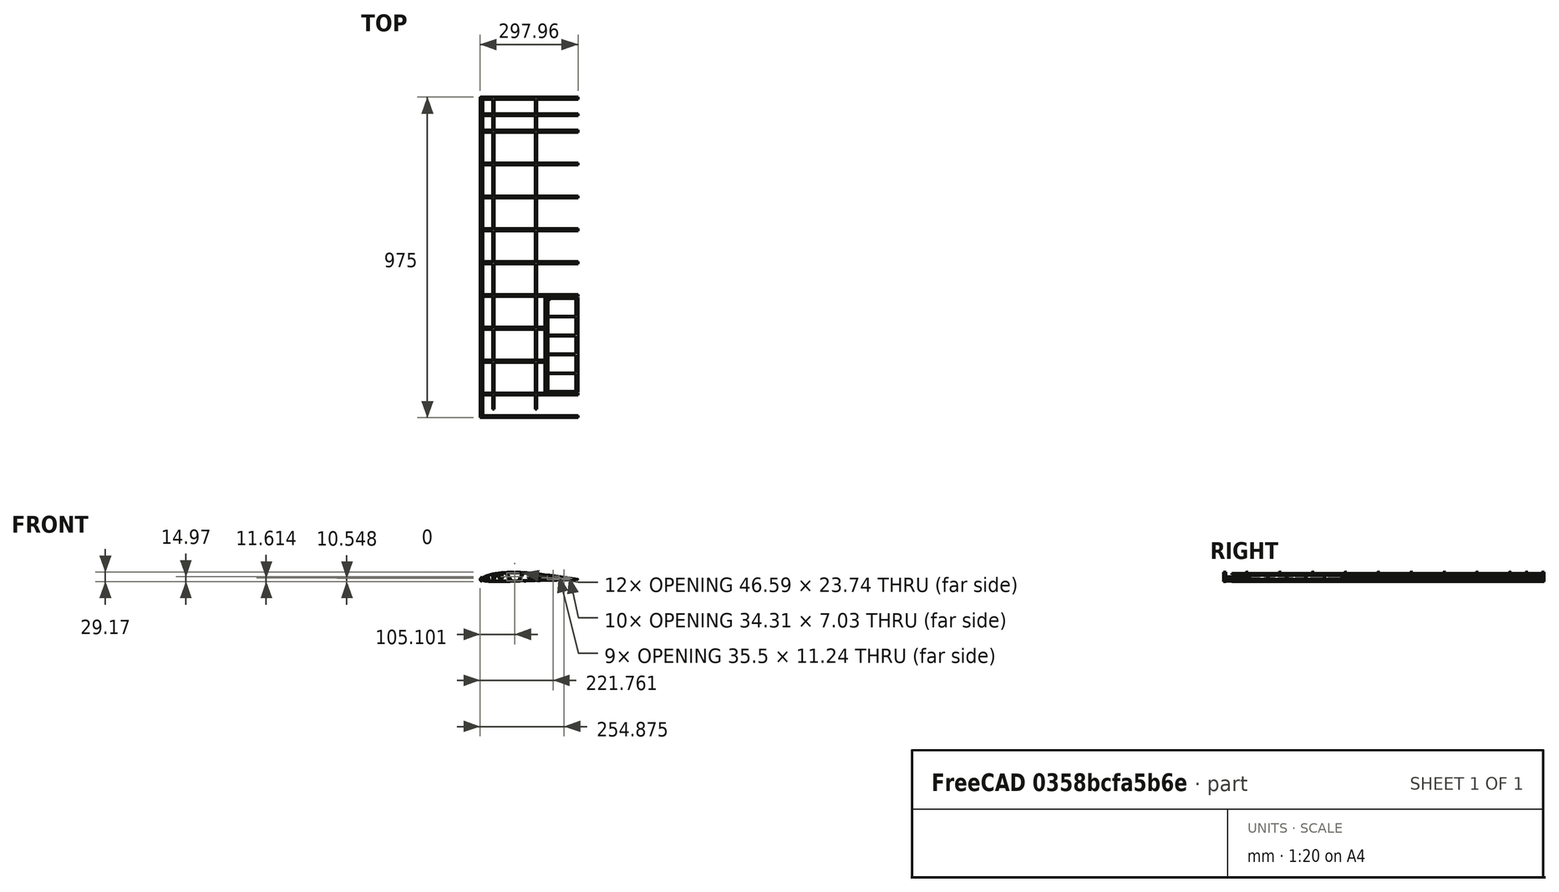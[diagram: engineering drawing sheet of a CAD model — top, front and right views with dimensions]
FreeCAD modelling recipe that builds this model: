
FCSTD DOCUMENT  (FreeCAD 1.0R39319 (Git))
Label: fpv_plane_wing_smarter
License: All rights reserved
LicenseURL: https://en.wikipedia.org/wiki/All_rights_reserved
objects: Sketcher::SketchObject×141, PartDesign::Pocket×77, PartDesign::Pad×64, PartDesign::Body×27, PartDesign::Thickness×11, PartDesign::Chamfer×5, Part::Part2DObjectPython×3, PartDesign::Plane×2, App::DocumentObjectGroup×1, PartDesign::Revolution×1
note: 788 computed .brp shape members not serialized (recipe doc carries the construction recipe); baked Part::Feature solids carry a one-line shape summary decoded from their .brp

FEATURE [Part::Part2DObjectPython] Wire  # Draft 2D object (typed FeaturePython)
  Area = 0.0621999
  ChamferSize = 0
  Closed = true
  End = (1.00001,0,0)
  FilletRadius = 0
  Length = 2.02855
  MakeFace = true
  Placement = pos=(0,0,0) rot=(1,0,0;1.5708rad)
  Points = (61) [(1,0,0),(0.99663,0.00039,0),(0.98679,0.00172,0),(0.97104,0.00419,0),(0.94996,0.00769,0),(0.92398,0.01193,0),(0.89336,0.0167,0),(0.8584,0.02198,0),+53 more]
  Start = (1,0,0)
  Subdivisions = 0
FEATURE [Part::Part2DObjectPython] Wire002  label="wing_wire_300mm"  # Draft 2D object (typed FeaturePython)
  Area = 5597.99
  ChamferSize = 0
  Closed = true
  End = (300.003,0,0)
  FilletRadius = 0
  Length = 608.564
  MakeFace = true
  Placement = pos=(0,0,0) rot=(1,0,0;1.5708rad)
  Points = (61) [(300,0,0),(298.989,0.117,0),(296.037,0.516,0),(291.312,1.257,0),(284.988,2.307,0),(277.194,3.579,0),(268.008,5.01,0),(257.52,6.594,0),+53 more]
  Start = (300,0,0)
  Subdivisions = 0
FEATURE [App::DocumentObjectGroup] s3021
  Group = -> [Wire,Wire002]
FEATURE [Part::Part2DObjectPython] BSpline001  label="wing_wire_300mm001"  # Draft 2D object (typed FeaturePython)
  Area = 5612.28
  Closed = true
  MakeFace = true
  Parameterization = 1
  Placement = pos=(0,0,0) rot=(1,0,0;1.5708rad)
  Points = (61) [(300,0,0),(298.989,0.117,0),(296.037,0.516,0),(291.312,1.257,0),(284.988,2.307,0),(277.194,3.579,0),(268.008,5.01,0),(257.52,6.594,0),+53 more]
FEATURE [Sketcher::SketchObject] Sketch003
  ArcFitTolerance = 1e-06
  FullyConstrained = false
  MakeInternals = false
  Placement = pos=(0,0,0) rot=(1,0,0;1.5708rad)
  sketch-geometry (125):
    g0: BSplineCurve PolesCount=62 KnotsCount=62 Degree=3 IsPeriodic=1
    g1-g62: Circle [constr] x62 (B-spline internal-alignment scaffolding for g0; pole/knot coordinates omitted)
    g63-g124: GeomPoint [constr] x62 (B-spline internal-alignment scaffolding for g0; pole/knot coordinates omitted)
  constraints (125):
    c: InternalAlignment(g1,g0)
    c: Weight(g1) = 1
    c: InternalAlignment(g2,g0)
    c: Equal(g2,g1)
    c: InternalAlignment(g3,g0)
    c: Equal(g3,g1)
    c: InternalAlignment(g4,g0)
    c: Equal(g4,g1)
    c: InternalAlignment(g5,g0)
    c: Equal(g5,g1)
    c: InternalAlignment(g6,g0)
    c: Equal(g6,g1)
    c: InternalAlignment(g7,g0)
    c: Equal(g7,g1)
    c: InternalAlignment(g8,g0)
    c: Equal(g8,g1)
    c: InternalAlignment(g9,g0)
    c: Equal(g9,g1)
    c: InternalAlignment(g10,g0)
    c: Equal(g10,g1)
    c: InternalAlignment(g11,g0)
    c: Equal(g11,g1)
    c: InternalAlignment(g12,g0)
    c: Equal(g12,g1)
    c: InternalAlignment(g13,g0)
    c: Equal(g13,g1)
    c: InternalAlignment(g14,g0)
    c: Equal(g14,g1)
    c: InternalAlignment(g15,g0)
    c: Equal(g15,g1)
    c: InternalAlignment(g16,g0)
    c: Equal(g16,g1)
    c: InternalAlignment(g17,g0)
    c: Equal(g17,g1)
    c: InternalAlignment(g18,g0)
    c: Equal(g18,g1)
    c: InternalAlignment(g19,g0)
    c: Equal(g19,g1)
    c: InternalAlignment(g20,g0)
    c: Equal(g20,g1)
    c: InternalAlignment(g21,g0)
    c: Equal(g21,g1)
    c: InternalAlignment(g22,g0)
    c: Equal(g22,g1)
    c: InternalAlignment(g23,g0)
    c: Equal(g23,g1)
    c: InternalAlignment(g24,g0)
    c: Equal(g24,g1)
    c: InternalAlignment(g25,g0)
    c: Equal(g25,g1)
    c: InternalAlignment(g26,g0)
    c: Equal(g26,g1)
    c: InternalAlignment(g27,g0)
    c: Equal(g27,g1)
    c: InternalAlignment(g28,g0)
    c: Equal(g28,g1)
    c: InternalAlignment(g29,g0)
    c: Equal(g29,g1)
    c: InternalAlignment(g30,g0)
    c: Equal(g30,g1)
    c: InternalAlignment(g31,g0)
    c: Equal(g31,g1)
    c: InternalAlignment(g32,g0)
    c: Equal(g32,g1)
    c: InternalAlignment(g33,g0)
    c: Equal(g33,g1)
    c: InternalAlignment(g34,g0)
    c: Equal(g34,g1)
    c: InternalAlignment(g35,g0)
    c: Equal(g35,g1)
    c: InternalAlignment(g36,g0)
    c: Equal(g36,g1)
    c: InternalAlignment(g37,g0)
    c: Equal(g37,g1)
    c: InternalAlignment(g38,g0)
    c: Equal(g38,g1)
    c: InternalAlignment(g39,g0)
    c: Equal(g39,g1)
    c: InternalAlignment(g40,g0)
    c: Equal(g40,g1)
    c: InternalAlignment(g41,g0)
    c: Equal(g41,g1)
    c: InternalAlignment(g42,g0)
    c: Equal(g42,g1)
    c: InternalAlignment(g43,g0)
    c: Equal(g43,g1)
    c: InternalAlignment(g44,g0)
    c: Equal(g44,g1)
    c: InternalAlignment(g45,g0)
    c: Equal(g45,g1)
    c: InternalAlignment(g46,g0)
    c: Equal(g46,g1)
    c: InternalAlignment(g47,g0)
    c: Equal(g47,g1)
    c: InternalAlignment(g48,g0)
    c: Equal(g48,g1)
    c: InternalAlignment(g49,g0)
    c: Equal(g49,g1)
    c: InternalAlignment(g50,g0)
    c: Equal(g50,g1)
    c: InternalAlignment(g51,g0)
    c: Equal(g51,g1)
    c: InternalAlignment(g52,g0)
    c: Equal(g52,g1)
    c: InternalAlignment(g53,g0)
    c: Equal(g53,g1)
    c: InternalAlignment(g54,g0)
    c: Equal(g54,g1)
    c: InternalAlignment(g55,g0)
    c: Equal(g55,g1)
    c: InternalAlignment(g56,g0)
    c: Equal(g56,g1)
    c: InternalAlignment(g57,g0)
    c: Equal(g57,g1)
    c: InternalAlignment(g58,g0)
    c: Equal(g58,g1)
    c: InternalAlignment(g59,g0)
    c: Equal(g59,g1)
    c: InternalAlignment(g60,g0)
    c: Equal(g60,g1)
    c: InternalAlignment(g61,g0)
    c: Equal(g61,g1)
    c: InternalAlignment(g62,g0)
    c: Equal(g62,g1)
    c: InternalAlignment(g63-g124 -> g0) x62
FEATURE [PartDesign::Pad] Pad
  Direction = (0,-1,2e-16)
  Length = 49.95
  Length2 = 10
  Placement = pos=(0,0,0) rot=(1,0,0;1.5708rad)
  Profile = -> Sketch003
  ReferenceAxis = -> Sketch003 [N_Axis]
  Refine = true
  Suppressed = false
  Type = 0
FEATURE [Sketcher::SketchObject] Sketch004
  ArcFitTolerance = 1e-06
  AttachmentSupport = -> [XY_Plane001]
  FullyConstrained = false
  MakeInternals = false
  MapMode = 5
  sketch-geometry (4):
    g0: LineSegment StartX=295 StartY=36.1981 StartZ=0 EndX=295 EndY=-1016.06 EndZ=0
    g1: LineSegment StartX=295 StartY=-1016.06 StartZ=0 EndX=488.335 EndY=-1016.06 EndZ=0
    g2: LineSegment StartX=488.335 StartY=-1016.06 StartZ=0 EndX=488.335 EndY=36.1981 EndZ=0
    g3: LineSegment StartX=488.335 StartY=36.1981 StartZ=0 EndX=295 EndY=36.1981 EndZ=0
  constraints (9):
    c: Coincident(g0,g1)
    c: Coincident(g1,g2)
    c: Coincident(g2,g3)
    c: Coincident(g3,g0)
    c: Vertical(g0)
    c: Vertical(g2)
    c: Horizontal(g1)
    c: Horizontal(g3)
    c: DistanceX(g-1,g0) = 295
FEATURE [Sketcher::SketchObject] Sketch006
  ArcFitTolerance = 1e-06
  AttachmentSupport = -> [Pad]
  FullyConstrained = false
  MakeInternals = false
  MapMode = 5
  Placement = pos=(0,-49.95,1.1e-14) rot=(1,0,0;1.5708rad)
  sketch-geometry (29):
    g0: LineSegment StartX=2.71326 StartY=0.775372 StartZ=0 EndX=3.3867 EndY=1.52303 EndZ=0
    g1: LineSegment StartX=3.3867 StartY=1.52303 StartZ=0 EndX=5.99321 EndY=4.17962 EndZ=0
    g2: LineSegment StartX=5.99321 StartY=4.17962 StartZ=0 EndX=11.2308 EndY=7.18071 EndZ=0
    g3: LineSegment StartX=11.2308 StartY=7.18071 StartZ=0 EndX=18.9287 EndY=10.4927 EndZ=0
    g4: LineSegment StartX=18.9287 StartY=10.4927 StartZ=0 EndX=30.0156 EndY=13.8045 EndZ=0
    g5: LineSegment StartX=30.0156 StartY=13.8045 StartZ=0 EndX=43.7053 EndY=16.6585 EndZ=0
    g6: LineSegment StartX=43.7053 StartY=16.6585 StartZ=0 EndX=58.3753 EndY=18.5837 EndZ=0
    g7: LineSegment StartX=58.3753 StartY=18.5837 StartZ=0 EndX=81.9328 EndY=20.1998 EndZ=0
    g8: LineSegment StartX=81.9328 StartY=20.1998 StartZ=0 EndX=99.116 EndY=20.5815 EndZ=0
    g9: LineSegment StartX=99.116 StartY=20.5815 StartZ=0 EndX=120.506 EndY=20.1998 EndZ=0
    g10: LineSegment StartX=120.506 StartY=20.1998 StartZ=0 EndX=145.772 EndY=18.6559 EndZ=0
    g11: LineSegment StartX=145.772 StartY=18.6559 StartZ=0 EndX=175.748 EndY=15.7728 EndZ=0
    g12: LineSegment StartX=175.748 StartY=15.7728 StartZ=0 EndX=200.436 EndY=12.5699 EndZ=0
    g13: LineSegment StartX=200.436 StartY=12.5699 StartZ=0 EndX=229.384 EndY=8.60252 EndZ=0
    g14: LineSegment StartX=229.384 StartY=8.60252 StartZ=0 EndX=252.135 EndY=5.21302 EndZ=0
    g15: LineSegment StartX=252.135 StartY=5.21302 StartZ=0 EndX=269.07 EndY=2.67143 EndZ=0
    g16: LineSegment StartX=269.07 StartY=2.67143 StartZ=0 EndX=269.07 EndY=1.39956 EndZ=0
    g17: LineSegment StartX=269.07 StartY=1.39956 StartZ=0 EndX=224.761 EndY=0.436598 EndZ=0
    g18: LineSegment StartX=224.761 StartY=0.436598 StartZ=0 EndX=175.487 EndY=-1.02731 EndZ=0
    g19: LineSegment StartX=175.487 StartY=-1.02731 StartZ=0 EndX=123.478 EndY=-2.41293 EndZ=0
    g20: LineSegment StartX=123.478 StartY=-2.41293 StartZ=0 EndX=62.0775 EndY=-3.87655 EndZ=0
    g21: LineSegment StartX=62.0775 StartY=-3.87655 StartZ=0 EndX=32.0529 EndY=-3.76091 EndZ=0
    g22: LineSegment StartX=32.0529 StartY=-3.76091 StartZ=0 EndX=18.888 EndY=-3.18288 EndZ=0
    g23: LineSegment StartX=18.888 StartY=-3.18288 StartZ=0 EndX=12.7286 EndY=-2.48971 EndZ=0
    g24: LineSegment StartX=12.7286 StartY=-2.48971 StartZ=0 EndX=8.49342 EndY=-1.8722 EndZ=0
    g25: LineSegment StartX=8.49342 StartY=-1.8722 StartZ=0 EndX=4.56236 EndY=-0.768246 EndZ=0
    g26: LineSegment StartX=4.56236 StartY=-0.768246 StartZ=0 EndX=3.01395 EndY=-0.301296 EndZ=0
    g27: ArcOfCircle CenterX=3.20505 CenterY=0.332397 CenterZ=0 NormalX=0 NormalY=0 NormalZ=1 AngleXU=0 Radius=0.661881 StartAngle=2.40837 EndAngle=4.41949
    g28: GeomPoint [constr] X=2.01486 Y=0 Z=0
  constraints (32):
    c: PointOnObject(g28,g-1)
    c: Coincident(g0,g1)
    c: Coincident(g1,g2)
    c: Coincident(g2,g3)
    c: Coincident(g3,g4)
    c: Coincident(g4,g5)
    c: Coincident(g5,g6)
    c: Coincident(g6,g7)
    c: Coincident(g7,g8)
    c: Coincident(g8,g9)
    c: Coincident(g9,g10)
    c: Coincident(g10,g11)
    c: Coincident(g11,g12)
    c: Coincident(g12,g13)
    c: Coincident(g13,g14)
    c: Coincident(g14,g15)
    c: Coincident(g15,g16)
    c: Vertical(g16)
    c: Coincident(g16,g17)
    c: Coincident(g17,g18)
    c: Coincident(g18,g19)
    c: Coincident(g19,g20)
    c: Coincident(g20,g21)
    c: Coincident(g21,g22)
    c: Coincident(g22,g23)
    c: Coincident(g23,g24)
    c: Coincident(g24,g25)
    c: Coincident(g25,g26)
    c: PointOnObject(g28,g0)
    c: PointOnObject(g28,g26)
    c: Tangent(g0,g27) = 1.5708
    c: Tangent(g26,g27) = 1.5708
FEATURE [PartDesign::Pocket] Pocket002
  BaseFeature = -> Pad
  Direction = (0,1,-2e-16)
  Length = 49.95
  Length2 = 5
  Placement = pos=(0,0,0) rot=(1,0,0;1.5708rad)
  Profile = -> Sketch006
  ReferenceAxis = -> Sketch006 [N_Axis]
  Refine = true
  Suppressed = false
  Type = 0
FEATURE [Sketcher::SketchObject] Sketch007
  ArcFitTolerance = 1e-06
  AttachmentSupport = -> [XY_Plane]
  FullyConstrained = false
  MakeInternals = false
  MapMode = 5
  sketch-geometry (4):
    g0: LineSegment StartX=295 StartY=17.3691 StartZ=0 EndX=295 EndY=-79.0747 EndZ=0
    g1: LineSegment StartX=295 StartY=-79.0747 StartZ=0 EndX=384.545 EndY=-79.0747 EndZ=0
    g2: LineSegment StartX=384.545 StartY=-79.0747 StartZ=0 EndX=384.545 EndY=17.3691 EndZ=0
    g3: LineSegment StartX=384.545 StartY=17.3691 StartZ=0 EndX=295 EndY=17.3691 EndZ=0
  constraints (9):
    c: Coincident(g0,g1)
    c: Coincident(g1,g2)
    c: Coincident(g2,g3)
    c: Coincident(g3,g0)
    c: Vertical(g0)
    c: Vertical(g2)
    c: Horizontal(g1)
    c: Horizontal(g3)
    c: DistanceX(g-1,g0) = 295
FEATURE [PartDesign::Pocket] Pocket003
  BaseFeature = -> Pocket002
  Direction = (0,0,-1)
  Length = 5
  Length2 = 5
  Midplane = true
  Placement = pos=(0,0,0) rot=(1,0,0;1.5708rad)
  Profile = -> Sketch007
  ReferenceAxis = -> Sketch007 [N_Axis]
  Refine = true
  Suppressed = false
  Type = 0
FEATURE [Sketcher::SketchObject] Sketch017
  ArcFitTolerance = 1e-06
  FullyConstrained = false
  MakeInternals = false
  Placement = pos=(0,0,0) rot=(1,0,0;1.5708rad)
  sketch-geometry (125):
    g0: BSplineCurve PolesCount=62 KnotsCount=62 Degree=3 IsPeriodic=1
    g1-g62: Circle [constr] x62 (B-spline internal-alignment scaffolding for g0; pole/knot coordinates omitted)
    g63-g124: GeomPoint [constr] x62 (B-spline internal-alignment scaffolding for g0; pole/knot coordinates omitted)
  constraints (125):
    c: InternalAlignment(g1,g0)
    c: Weight(g1) = 1
    c: InternalAlignment(g2,g0)
    c: Equal(g2,g1)
    c: InternalAlignment(g3,g0)
    c: Equal(g3,g1)
    c: InternalAlignment(g4,g0)
    c: Equal(g4,g1)
    c: InternalAlignment(g5,g0)
    c: Equal(g5,g1)
    c: InternalAlignment(g6,g0)
    c: Equal(g6,g1)
    c: InternalAlignment(g7,g0)
    c: Equal(g7,g1)
    c: InternalAlignment(g8,g0)
    c: Equal(g8,g1)
    c: InternalAlignment(g9,g0)
    c: Equal(g9,g1)
    c: InternalAlignment(g10,g0)
    c: Equal(g10,g1)
    c: InternalAlignment(g11,g0)
    c: Equal(g11,g1)
    c: InternalAlignment(g12,g0)
    c: Equal(g12,g1)
    c: InternalAlignment(g13,g0)
    c: Equal(g13,g1)
    c: InternalAlignment(g14,g0)
    c: Equal(g14,g1)
    c: InternalAlignment(g15,g0)
    c: Equal(g15,g1)
    c: InternalAlignment(g16,g0)
    c: Equal(g16,g1)
    c: InternalAlignment(g17,g0)
    c: Equal(g17,g1)
    c: InternalAlignment(g18,g0)
    c: Equal(g18,g1)
    c: InternalAlignment(g19,g0)
    c: Equal(g19,g1)
    c: InternalAlignment(g20,g0)
    c: Equal(g20,g1)
    c: InternalAlignment(g21,g0)
    c: Equal(g21,g1)
    c: InternalAlignment(g22,g0)
    c: Equal(g22,g1)
    c: InternalAlignment(g23,g0)
    c: Equal(g23,g1)
    c: InternalAlignment(g24,g0)
    c: Equal(g24,g1)
    c: InternalAlignment(g25,g0)
    c: Equal(g25,g1)
    c: InternalAlignment(g26,g0)
    c: Equal(g26,g1)
    c: InternalAlignment(g27,g0)
    c: Equal(g27,g1)
    c: InternalAlignment(g28,g0)
    c: Equal(g28,g1)
    c: InternalAlignment(g29,g0)
    c: Equal(g29,g1)
    c: InternalAlignment(g30,g0)
    c: Equal(g30,g1)
    c: InternalAlignment(g31,g0)
    c: Equal(g31,g1)
    c: InternalAlignment(g32,g0)
    c: Equal(g32,g1)
    c: InternalAlignment(g33,g0)
    c: Equal(g33,g1)
    c: InternalAlignment(g34,g0)
    c: Equal(g34,g1)
    c: InternalAlignment(g35,g0)
    c: Equal(g35,g1)
    c: InternalAlignment(g36,g0)
    c: Equal(g36,g1)
    c: InternalAlignment(g37,g0)
    c: Equal(g37,g1)
    c: InternalAlignment(g38,g0)
    c: Equal(g38,g1)
    c: InternalAlignment(g39,g0)
    c: Equal(g39,g1)
    c: InternalAlignment(g40,g0)
    c: Equal(g40,g1)
    c: InternalAlignment(g41,g0)
    c: Equal(g41,g1)
    c: InternalAlignment(g42,g0)
    c: Equal(g42,g1)
    c: InternalAlignment(g43,g0)
    c: Equal(g43,g1)
    c: InternalAlignment(g44,g0)
    c: Equal(g44,g1)
    c: InternalAlignment(g45,g0)
    c: Equal(g45,g1)
    c: InternalAlignment(g46,g0)
    c: Equal(g46,g1)
    c: InternalAlignment(g47,g0)
    c: Equal(g47,g1)
    c: InternalAlignment(g48,g0)
    c: Equal(g48,g1)
    c: InternalAlignment(g49,g0)
    c: Equal(g49,g1)
    c: InternalAlignment(g50,g0)
    c: Equal(g50,g1)
    c: InternalAlignment(g51,g0)
    c: Equal(g51,g1)
    c: InternalAlignment(g52,g0)
    c: Equal(g52,g1)
    c: InternalAlignment(g53,g0)
    c: Equal(g53,g1)
    c: InternalAlignment(g54,g0)
    c: Equal(g54,g1)
    c: InternalAlignment(g55,g0)
    c: Equal(g55,g1)
    c: InternalAlignment(g56,g0)
    c: Equal(g56,g1)
    c: InternalAlignment(g57,g0)
    c: Equal(g57,g1)
    c: InternalAlignment(g58,g0)
    c: Equal(g58,g1)
    c: InternalAlignment(g59,g0)
    c: Equal(g59,g1)
    c: InternalAlignment(g60,g0)
    c: Equal(g60,g1)
    c: InternalAlignment(g61,g0)
    c: Equal(g61,g1)
    c: InternalAlignment(g62,g0)
    c: Equal(g62,g1)
    c: InternalAlignment(g63-g124 -> g0) x62
FEATURE [PartDesign::Pad] Pad006
  Direction = (0,-1,2e-16)
  Length = 53.4
  Length2 = 10
  Placement = pos=(0,0,0) rot=(1,0,0;1.5708rad)
  Profile = -> Sketch017
  ReferenceAxis = -> Sketch017 [N_Axis]
  Refine = true
  Suppressed = false
  Type = 0
FEATURE [PartDesign::Pocket] Pocket
  BaseFeature = -> Pad006
  Direction = (0,0,-1)
  Length = 100
  Length2 = 5
  Midplane = true
  Placement = pos=(0,0,0) rot=(1,0,0;1.5708rad)
  Profile = -> Sketch004
  ReferenceAxis = -> Sketch004 [N_Axis]
  Refine = true
  Suppressed = false
  Type = 0
FEATURE [PartDesign::Thickness] Thickness
  Base = -> Pocket [Face4,Face2]
  BaseFeature = -> Pocket
  Intersection = false
  Join = 0
  Mode = 0
  Refine = true
  SupportTransform = false
  Suppressed = false
  Value = 3
FEATURE [Sketcher::SketchObject] Sketch005
  ArcFitTolerance = 1e-06
  AttachmentSupport = -> [Thickness]
  FullyConstrained = false
  MakeInternals = false
  MapMode = 5
  Placement = pos=(0,-53.4,1.17e-14) rot=(1,0,0;1.5708rad)
  sketch-geometry (15):
    g0: LineSegment [constr] StartX=4.5568 StartY=5.71171 StartZ=0 EndX=7.88662 EndY=7.89278 EndZ=0
    g1: LineSegment StartX=5.46609 StartY=6.3073 StartZ=0 EndX=2.696 EndY=10.5364 EndZ=0
    g2: LineSegment StartX=2.696 StartY=10.5364 StartZ=0 EndX=32.4943 EndY=27.0739 EndZ=0
    g3: LineSegment StartX=32.4943 StartY=27.0739 StartZ=0 EndX=156.488 EndY=39.0363 EndZ=0
    g4: LineSegment StartX=156.488 StartY=39.0363 StartZ=0 EndX=248.898 EndY=26.6449 EndZ=0
    g5: LineSegment StartX=248.898 StartY=26.6449 StartZ=0 EndX=329.144 EndY=7.08029 EndZ=0
    g6: LineSegment StartX=329.144 StartY=7.08029 StartZ=0 EndX=328 EndY=-15.9084 EndZ=0
    g7: LineSegment StartX=328 StartY=-15.9084 StartZ=0 EndX=200.054 EndY=-15.9084 EndZ=0
    g8: LineSegment StartX=200.054 StartY=-15.9084 StartZ=0 EndX=64.7748 EndY=-15.9084 EndZ=0
    g9: LineSegment StartX=64.7748 StartY=-15.9084 StartZ=0 EndX=16.3454 EndY=-20.7039 EndZ=0
    g10: LineSegment StartX=16.3454 StartY=-20.7039 StartZ=0 EndX=2.88885 EndY=-12.2412 EndZ=0
    g11: LineSegment [constr] StartX=2.3291 StartY=-2.35546 StartZ=0 EndX=5.23499 EndY=-3.24958 EndZ=0
    g12: LineSegment StartX=2.88053 StartY=-2.52513 StartZ=0 EndX=1.81302 EndY=-5.99451 EndZ=0
    g13: LineSegment StartX=1.81302 StartY=-5.99451 StartZ=0 EndX=2.88885 EndY=-12.2412 EndZ=0
    g14: LineSegment StartX=5.46609 StartY=6.3073 StartZ=0 EndX=2.88053 EndY=-2.52513 EndZ=0
  constraints (22):
    c: PointOnObject(g1,g0)
    c: Perpendicular(g0,g1)
    c: Block(g1)
    c: Block(g0)
    c: Coincident(g1,g2)
    c: Coincident(g2,g3)
    c: Coincident(g3,g4)
    c: Coincident(g4,g5)
    c: Coincident(g5,g6)
    c: Coincident(g6,g7)
    c: Horizontal(g7)
    c: Coincident(g7,g8)
    c: Horizontal(g8)
    c: Coincident(g8,g9)
    c: Coincident(g9,g10)
    c: Block(g11)
    c: PointOnObject(g12,g11)
    c: Perpendicular(g11,g12)
    c: Coincident(g13,g12)
    c: Coincident(g13,g10)
    c: Coincident(g14,g1)
    c: Coincident(g14,g12)
FEATURE [PartDesign::Pocket] Pocket001
  BaseFeature = -> Thickness
  Direction = (0,1,-2e-16)
  Length = 1000
  Length2 = 5
  Profile = -> Sketch005
  ReferenceAxis = -> Sketch005 [N_Axis]
  Refine = true
  Suppressed = false
  Type = 0
FEATURE [PartDesign::Body] Body001  label="leading edge 001"
  AllowCompound = false
  Group = -> [Pad006,Sketch004,Pocket,Thickness,Sketch005,Pocket001,Sketch017]
  Origin = -> Origin001
  Tip = -> Pocket001
FEATURE [Sketcher::SketchObject] Sketch027
  ArcFitTolerance = 1e-06
  AttachmentSupport = -> [XY_Plane005]
  FullyConstrained = false
  MakeInternals = false
  MapMode = 5
  sketch-geometry (4):
    g0: LineSegment StartX=295 StartY=36.1981 StartZ=0 EndX=295 EndY=-1016.06 EndZ=0
    g1: LineSegment StartX=295 StartY=-1016.06 StartZ=0 EndX=488.335 EndY=-1016.06 EndZ=0
    g2: LineSegment StartX=488.335 StartY=-1016.06 StartZ=0 EndX=488.335 EndY=36.1981 EndZ=0
    g3: LineSegment StartX=488.335 StartY=36.1981 StartZ=0 EndX=295 EndY=36.1981 EndZ=0
  constraints (9):
    c: Coincident(g0,g1)
    c: Coincident(g1,g2)
    c: Coincident(g2,g3)
    c: Coincident(g3,g0)
    c: Vertical(g0)
    c: Vertical(g2)
    c: Horizontal(g1)
    c: Horizontal(g3)
    c: DistanceX(g-1,g0) = 295
FEATURE [Sketcher::SketchObject] Sketch029
  ArcFitTolerance = 1e-06
  FullyConstrained = false
  MakeInternals = false
  Placement = pos=(0,0,0) rot=(1,0,0;1.5708rad)
  sketch-geometry (125):
    g0: BSplineCurve PolesCount=62 KnotsCount=62 Degree=3 IsPeriodic=1
    g1-g62: Circle [constr] x62 (B-spline internal-alignment scaffolding for g0; pole/knot coordinates omitted)
    g63-g124: GeomPoint [constr] x62 (B-spline internal-alignment scaffolding for g0; pole/knot coordinates omitted)
  constraints (125):
    c: InternalAlignment(g1,g0)
    c: Weight(g1) = 1
    c: InternalAlignment(g2,g0)
    c: Equal(g2,g1)
    c: InternalAlignment(g3,g0)
    c: Equal(g3,g1)
    c: InternalAlignment(g4,g0)
    c: Equal(g4,g1)
    c: InternalAlignment(g5,g0)
    c: Equal(g5,g1)
    c: InternalAlignment(g6,g0)
    c: Equal(g6,g1)
    c: InternalAlignment(g7,g0)
    c: Equal(g7,g1)
    c: InternalAlignment(g8,g0)
    c: Equal(g8,g1)
    c: InternalAlignment(g9,g0)
    c: Equal(g9,g1)
    c: InternalAlignment(g10,g0)
    c: Equal(g10,g1)
    c: InternalAlignment(g11,g0)
    c: Equal(g11,g1)
    c: InternalAlignment(g12,g0)
    c: Equal(g12,g1)
    c: InternalAlignment(g13,g0)
    c: Equal(g13,g1)
    c: InternalAlignment(g14,g0)
    c: Equal(g14,g1)
    c: InternalAlignment(g15,g0)
    c: Equal(g15,g1)
    c: InternalAlignment(g16,g0)
    c: Equal(g16,g1)
    c: InternalAlignment(g17,g0)
    c: Equal(g17,g1)
    c: InternalAlignment(g18,g0)
    c: Equal(g18,g1)
    c: InternalAlignment(g19,g0)
    c: Equal(g19,g1)
    c: InternalAlignment(g20,g0)
    c: Equal(g20,g1)
    c: InternalAlignment(g21,g0)
    c: Equal(g21,g1)
    c: InternalAlignment(g22,g0)
    c: Equal(g22,g1)
    c: InternalAlignment(g23,g0)
    c: Equal(g23,g1)
    c: InternalAlignment(g24,g0)
    c: Equal(g24,g1)
    c: InternalAlignment(g25,g0)
    c: Equal(g25,g1)
    c: InternalAlignment(g26,g0)
    c: Equal(g26,g1)
    c: InternalAlignment(g27,g0)
    c: Equal(g27,g1)
    c: InternalAlignment(g28,g0)
    c: Equal(g28,g1)
    c: InternalAlignment(g29,g0)
    c: Equal(g29,g1)
    c: InternalAlignment(g30,g0)
    c: Equal(g30,g1)
    c: InternalAlignment(g31,g0)
    c: Equal(g31,g1)
    c: InternalAlignment(g32,g0)
    c: Equal(g32,g1)
    c: InternalAlignment(g33,g0)
    c: Equal(g33,g1)
    c: InternalAlignment(g34,g0)
    c: Equal(g34,g1)
    c: InternalAlignment(g35,g0)
    c: Equal(g35,g1)
    c: InternalAlignment(g36,g0)
    c: Equal(g36,g1)
    c: InternalAlignment(g37,g0)
    c: Equal(g37,g1)
    c: InternalAlignment(g38,g0)
    c: Equal(g38,g1)
    c: InternalAlignment(g39,g0)
    c: Equal(g39,g1)
    c: InternalAlignment(g40,g0)
    c: Equal(g40,g1)
    c: InternalAlignment(g41,g0)
    c: Equal(g41,g1)
    c: InternalAlignment(g42,g0)
    c: Equal(g42,g1)
    c: InternalAlignment(g43,g0)
    c: Equal(g43,g1)
    c: InternalAlignment(g44,g0)
    c: Equal(g44,g1)
    c: InternalAlignment(g45,g0)
    c: Equal(g45,g1)
    c: InternalAlignment(g46,g0)
    c: Equal(g46,g1)
    c: InternalAlignment(g47,g0)
    c: Equal(g47,g1)
    c: InternalAlignment(g48,g0)
    c: Equal(g48,g1)
    c: InternalAlignment(g49,g0)
    c: Equal(g49,g1)
    c: InternalAlignment(g50,g0)
    c: Equal(g50,g1)
    c: InternalAlignment(g51,g0)
    c: Equal(g51,g1)
    c: InternalAlignment(g52,g0)
    c: Equal(g52,g1)
    c: InternalAlignment(g53,g0)
    c: Equal(g53,g1)
    c: InternalAlignment(g54,g0)
    c: Equal(g54,g1)
    c: InternalAlignment(g55,g0)
    c: Equal(g55,g1)
    c: InternalAlignment(g56,g0)
    c: Equal(g56,g1)
    c: InternalAlignment(g57,g0)
    c: Equal(g57,g1)
    c: InternalAlignment(g58,g0)
    c: Equal(g58,g1)
    c: InternalAlignment(g59,g0)
    c: Equal(g59,g1)
    c: InternalAlignment(g60,g0)
    c: Equal(g60,g1)
    c: InternalAlignment(g61,g0)
    c: Equal(g61,g1)
    c: InternalAlignment(g62,g0)
    c: Equal(g62,g1)
    c: InternalAlignment(g63-g124 -> g0) x62
FEATURE [PartDesign::Pad] Pad011
  Direction = (0,-1,2e-16)
  Length = 49.8
  Length2 = 10
  Placement = pos=(0,0,0) rot=(1,0,0;1.5708rad)
  Profile = -> Sketch029
  ReferenceAxis = -> Sketch029 [N_Axis]
  Refine = true
  Suppressed = false
  Type = 0
FEATURE [PartDesign::Pocket] Pocket014
  BaseFeature = -> Pad011
  Direction = (0,0,-1)
  Length = 100
  Length2 = 5
  Midplane = true
  Placement = pos=(0,0,0) rot=(1,0,0;1.5708rad)
  Profile = -> Sketch027
  ReferenceAxis = -> Sketch027 [N_Axis]
  Refine = true
  Suppressed = false
  Type = 0
FEATURE [PartDesign::Thickness] Thickness001
  Base = -> Pocket014 [Face4,Face2]
  BaseFeature = -> Pocket014
  Intersection = false
  Join = 0
  Mode = 0
  Refine = true
  SupportTransform = false
  Suppressed = false
  Value = 3
FEATURE [Sketcher::SketchObject] Sketch028
  ArcFitTolerance = 1e-06
  AttachmentSupport = -> [Thickness001]
  FullyConstrained = false
  MakeInternals = false
  MapMode = 5
  Placement = pos=(0,-49.8,1.1e-14) rot=(1,0,0;1.5708rad)
  sketch-geometry (15):
    g0: LineSegment [constr] StartX=4.5568 StartY=5.71171 StartZ=0 EndX=7.88662 EndY=7.89278 EndZ=0
    g1: LineSegment StartX=5.46609 StartY=6.3073 StartZ=0 EndX=2.696 EndY=10.5364 EndZ=0
    g2: LineSegment StartX=2.696 StartY=10.5364 StartZ=0 EndX=32.4943 EndY=27.0739 EndZ=0
    g3: LineSegment StartX=32.4943 StartY=27.0739 StartZ=0 EndX=156.488 EndY=39.0363 EndZ=0
    g4: LineSegment StartX=156.488 StartY=39.0363 StartZ=0 EndX=248.898 EndY=26.6449 EndZ=0
    g5: LineSegment StartX=248.898 StartY=26.6449 StartZ=0 EndX=329.144 EndY=7.08029 EndZ=0
    g6: LineSegment StartX=329.144 StartY=7.08029 StartZ=0 EndX=328 EndY=-15.9084 EndZ=0
    g7: LineSegment StartX=328 StartY=-15.9084 StartZ=0 EndX=200.054 EndY=-15.9084 EndZ=0
    g8: LineSegment StartX=200.054 StartY=-15.9084 StartZ=0 EndX=64.7748 EndY=-15.9084 EndZ=0
    g9: LineSegment StartX=64.7748 StartY=-15.9084 StartZ=0 EndX=16.3454 EndY=-20.7039 EndZ=0
    g10: LineSegment StartX=16.3454 StartY=-20.7039 StartZ=0 EndX=2.88885 EndY=-12.2412 EndZ=0
    g11: LineSegment [constr] StartX=2.3291 StartY=-2.35546 StartZ=0 EndX=5.23499 EndY=-3.24958 EndZ=0
    g12: LineSegment StartX=2.88053 StartY=-2.52513 StartZ=0 EndX=1.81302 EndY=-5.99451 EndZ=0
    g13: LineSegment StartX=1.81302 StartY=-5.99451 StartZ=0 EndX=2.88885 EndY=-12.2412 EndZ=0
    g14: LineSegment StartX=5.46609 StartY=6.3073 StartZ=0 EndX=2.88053 EndY=-2.52513 EndZ=0
  constraints (22):
    c: PointOnObject(g1,g0)
    c: Perpendicular(g0,g1)
    c: Block(g1)
    c: Block(g0)
    c: Coincident(g1,g2)
    c: Coincident(g2,g3)
    c: Coincident(g3,g4)
    c: Coincident(g4,g5)
    c: Coincident(g5,g6)
    c: Coincident(g6,g7)
    c: Horizontal(g7)
    c: Coincident(g7,g8)
    c: Horizontal(g8)
    c: Coincident(g8,g9)
    c: Coincident(g9,g10)
    c: Block(g11)
    c: PointOnObject(g12,g11)
    c: Perpendicular(g11,g12)
    c: Coincident(g13,g12)
    c: Coincident(g13,g10)
    c: Coincident(g14,g1)
    c: Coincident(g14,g12)
FEATURE [PartDesign::Pocket] Pocket015
  BaseFeature = -> Thickness001
  Direction = (0,1,-2e-16)
  Length = 1000
  Length2 = 5
  Profile = -> Sketch028
  ReferenceAxis = -> Sketch028 [N_Axis]
  Refine = true
  Suppressed = false
  Type = 0
FEATURE [PartDesign::Body] Body005  label="leading edge 002"
  AllowCompound = false
  Group = -> [Pad011,Sketch027,Pocket014,Thickness001,Sketch028,Pocket015,Sketch029]
  Origin = -> Origin005
  Placement = pos=(0,-53.6,0) rot=(0,0,1;0rad)
  Tip = -> Pocket015
FEATURE [Sketcher::SketchObject] Sketch030
  ArcFitTolerance = 1e-06
  FullyConstrained = false
  MakeInternals = false
  Placement = pos=(0,0,0) rot=(1,0,0;1.5708rad)
  sketch-geometry (125):
    g0: BSplineCurve PolesCount=62 KnotsCount=62 Degree=3 IsPeriodic=1
    g1-g62: Circle [constr] x62 (B-spline internal-alignment scaffolding for g0; pole/knot coordinates omitted)
    g63-g124: GeomPoint [constr] x62 (B-spline internal-alignment scaffolding for g0; pole/knot coordinates omitted)
  constraints (125):
    c: InternalAlignment(g1,g0)
    c: Weight(g1) = 1
    c: InternalAlignment(g2,g0)
    c: Equal(g2,g1)
    c: InternalAlignment(g3,g0)
    c: Equal(g3,g1)
    c: InternalAlignment(g4,g0)
    c: Equal(g4,g1)
    c: InternalAlignment(g5,g0)
    c: Equal(g5,g1)
    c: InternalAlignment(g6,g0)
    c: Equal(g6,g1)
    c: InternalAlignment(g7,g0)
    c: Equal(g7,g1)
    c: InternalAlignment(g8,g0)
    c: Equal(g8,g1)
    c: InternalAlignment(g9,g0)
    c: Equal(g9,g1)
    c: InternalAlignment(g10,g0)
    c: Equal(g10,g1)
    c: InternalAlignment(g11,g0)
    c: Equal(g11,g1)
    c: InternalAlignment(g12,g0)
    c: Equal(g12,g1)
    c: InternalAlignment(g13,g0)
    c: Equal(g13,g1)
    c: InternalAlignment(g14,g0)
    c: Equal(g14,g1)
    c: InternalAlignment(g15,g0)
    c: Equal(g15,g1)
    c: InternalAlignment(g16,g0)
    c: Equal(g16,g1)
    c: InternalAlignment(g17,g0)
    c: Equal(g17,g1)
    c: InternalAlignment(g18,g0)
    c: Equal(g18,g1)
    c: InternalAlignment(g19,g0)
    c: Equal(g19,g1)
    c: InternalAlignment(g20,g0)
    c: Equal(g20,g1)
    c: InternalAlignment(g21,g0)
    c: Equal(g21,g1)
    c: InternalAlignment(g22,g0)
    c: Equal(g22,g1)
    c: InternalAlignment(g23,g0)
    c: Equal(g23,g1)
    c: InternalAlignment(g24,g0)
    c: Equal(g24,g1)
    c: InternalAlignment(g25,g0)
    c: Equal(g25,g1)
    c: InternalAlignment(g26,g0)
    c: Equal(g26,g1)
    c: InternalAlignment(g27,g0)
    c: Equal(g27,g1)
    c: InternalAlignment(g28,g0)
    c: Equal(g28,g1)
    c: InternalAlignment(g29,g0)
    c: Equal(g29,g1)
    c: InternalAlignment(g30,g0)
    c: Equal(g30,g1)
    c: InternalAlignment(g31,g0)
    c: Equal(g31,g1)
    c: InternalAlignment(g32,g0)
    c: Equal(g32,g1)
    c: InternalAlignment(g33,g0)
    c: Equal(g33,g1)
    c: InternalAlignment(g34,g0)
    c: Equal(g34,g1)
    c: InternalAlignment(g35,g0)
    c: Equal(g35,g1)
    c: InternalAlignment(g36,g0)
    c: Equal(g36,g1)
    c: InternalAlignment(g37,g0)
    c: Equal(g37,g1)
    c: InternalAlignment(g38,g0)
    c: Equal(g38,g1)
    c: InternalAlignment(g39,g0)
    c: Equal(g39,g1)
    c: InternalAlignment(g40,g0)
    c: Equal(g40,g1)
    c: InternalAlignment(g41,g0)
    c: Equal(g41,g1)
    c: InternalAlignment(g42,g0)
    c: Equal(g42,g1)
    c: InternalAlignment(g43,g0)
    c: Equal(g43,g1)
    c: InternalAlignment(g44,g0)
    c: Equal(g44,g1)
    c: InternalAlignment(g45,g0)
    c: Equal(g45,g1)
    c: InternalAlignment(g46,g0)
    c: Equal(g46,g1)
    c: InternalAlignment(g47,g0)
    c: Equal(g47,g1)
    c: InternalAlignment(g48,g0)
    c: Equal(g48,g1)
    c: InternalAlignment(g49,g0)
    c: Equal(g49,g1)
    c: InternalAlignment(g50,g0)
    c: Equal(g50,g1)
    c: InternalAlignment(g51,g0)
    c: Equal(g51,g1)
    c: InternalAlignment(g52,g0)
    c: Equal(g52,g1)
    c: InternalAlignment(g53,g0)
    c: Equal(g53,g1)
    c: InternalAlignment(g54,g0)
    c: Equal(g54,g1)
    c: InternalAlignment(g55,g0)
    c: Equal(g55,g1)
    c: InternalAlignment(g56,g0)
    c: Equal(g56,g1)
    c: InternalAlignment(g57,g0)
    c: Equal(g57,g1)
    c: InternalAlignment(g58,g0)
    c: Equal(g58,g1)
    c: InternalAlignment(g59,g0)
    c: Equal(g59,g1)
    c: InternalAlignment(g60,g0)
    c: Equal(g60,g1)
    c: InternalAlignment(g61,g0)
    c: Equal(g61,g1)
    c: InternalAlignment(g62,g0)
    c: Equal(g62,g1)
    c: InternalAlignment(g63-g124 -> g0) x62
FEATURE [PartDesign::Pad] Pad012
  Direction = (0,-1,2e-16)
  Length = 99.95
  Length2 = 10
  Placement = pos=(0,0,0) rot=(1,0,0;1.5708rad)
  Profile = -> Sketch030
  ReferenceAxis = -> Sketch030 [N_Axis]
  Refine = true
  Suppressed = false
  Type = 0
FEATURE [Sketcher::SketchObject] Sketch031
  ArcFitTolerance = 1e-06
  AttachmentSupport = -> [Pad012]
  FullyConstrained = false
  MakeInternals = false
  MapMode = 5
  Placement = pos=(0,-99.95,2.2e-14) rot=(1,0,0;1.5708rad)
  sketch-geometry (29):
    g0: LineSegment StartX=2.71326 StartY=0.775372 StartZ=0 EndX=3.3867 EndY=1.52303 EndZ=0
    g1: LineSegment StartX=3.3867 StartY=1.52303 StartZ=0 EndX=5.99321 EndY=4.17962 EndZ=0
    g2: LineSegment StartX=5.99321 StartY=4.17962 StartZ=0 EndX=11.2308 EndY=7.18071 EndZ=0
    g3: LineSegment StartX=11.2308 StartY=7.18071 StartZ=0 EndX=18.9287 EndY=10.4927 EndZ=0
    g4: LineSegment StartX=18.9287 StartY=10.4927 StartZ=0 EndX=30.0156 EndY=13.8045 EndZ=0
    g5: LineSegment StartX=30.0156 StartY=13.8045 StartZ=0 EndX=43.7053 EndY=16.6585 EndZ=0
    g6: LineSegment StartX=43.7053 StartY=16.6585 StartZ=0 EndX=58.3753 EndY=18.5837 EndZ=0
    g7: LineSegment StartX=58.3753 StartY=18.5837 StartZ=0 EndX=81.9328 EndY=20.1998 EndZ=0
    g8: LineSegment StartX=81.9328 StartY=20.1998 StartZ=0 EndX=99.116 EndY=20.5815 EndZ=0
    g9: LineSegment StartX=99.116 StartY=20.5815 StartZ=0 EndX=120.506 EndY=20.1998 EndZ=0
    g10: LineSegment StartX=120.506 StartY=20.1998 StartZ=0 EndX=145.772 EndY=18.6559 EndZ=0
    g11: LineSegment StartX=145.772 StartY=18.6559 StartZ=0 EndX=175.748 EndY=15.7728 EndZ=0
    g12: LineSegment StartX=175.748 StartY=15.7728 StartZ=0 EndX=200.436 EndY=12.5699 EndZ=0
    g13: LineSegment StartX=200.436 StartY=12.5699 StartZ=0 EndX=229.384 EndY=8.60252 EndZ=0
    g14: LineSegment StartX=229.384 StartY=8.60252 StartZ=0 EndX=252.135 EndY=5.21302 EndZ=0
    g15: LineSegment StartX=252.135 StartY=5.21302 StartZ=0 EndX=269.07 EndY=2.67143 EndZ=0
    g16: LineSegment StartX=269.07 StartY=2.67143 StartZ=0 EndX=269.07 EndY=1.39956 EndZ=0
    g17: LineSegment StartX=269.07 StartY=1.39956 StartZ=0 EndX=224.761 EndY=0.436598 EndZ=0
    g18: LineSegment StartX=224.761 StartY=0.436598 StartZ=0 EndX=175.487 EndY=-1.02731 EndZ=0
    g19: LineSegment StartX=175.487 StartY=-1.02731 StartZ=0 EndX=123.478 EndY=-2.41293 EndZ=0
    g20: LineSegment StartX=123.478 StartY=-2.41293 StartZ=0 EndX=62.0775 EndY=-3.87655 EndZ=0
    g21: LineSegment StartX=62.0775 StartY=-3.87655 StartZ=0 EndX=32.0529 EndY=-3.76091 EndZ=0
    g22: LineSegment StartX=32.0529 StartY=-3.76091 StartZ=0 EndX=18.888 EndY=-3.18288 EndZ=0
    g23: LineSegment StartX=18.888 StartY=-3.18288 StartZ=0 EndX=12.7286 EndY=-2.48971 EndZ=0
    g24: LineSegment StartX=12.7286 StartY=-2.48971 StartZ=0 EndX=8.49342 EndY=-1.8722 EndZ=0
    g25: LineSegment StartX=8.49342 StartY=-1.8722 StartZ=0 EndX=4.56236 EndY=-0.768246 EndZ=0
    g26: LineSegment StartX=4.56236 StartY=-0.768246 StartZ=0 EndX=3.01395 EndY=-0.301296 EndZ=0
    g27: ArcOfCircle CenterX=3.20505 CenterY=0.332397 CenterZ=0 NormalX=0 NormalY=0 NormalZ=1 AngleXU=0 Radius=0.661881 StartAngle=2.40837 EndAngle=4.41949
    g28: GeomPoint [constr] X=2.01486 Y=0 Z=0
  constraints (32):
    c: PointOnObject(g28,g-1)
    c: Coincident(g0,g1)
    c: Coincident(g1,g2)
    c: Coincident(g2,g3)
    c: Coincident(g3,g4)
    c: Coincident(g4,g5)
    c: Coincident(g5,g6)
    c: Coincident(g6,g7)
    c: Coincident(g7,g8)
    c: Coincident(g8,g9)
    c: Coincident(g9,g10)
    c: Coincident(g10,g11)
    c: Coincident(g11,g12)
    c: Coincident(g12,g13)
    c: Coincident(g13,g14)
    c: Coincident(g14,g15)
    c: Coincident(g15,g16)
    c: Vertical(g16)
    c: Coincident(g16,g17)
    c: Coincident(g17,g18)
    c: Coincident(g18,g19)
    c: Coincident(g19,g20)
    c: Coincident(g20,g21)
    c: Coincident(g21,g22)
    c: Coincident(g22,g23)
    c: Coincident(g23,g24)
    c: Coincident(g24,g25)
    c: Coincident(g25,g26)
    c: PointOnObject(g28,g0)
    c: PointOnObject(g28,g26)
    c: Tangent(g0,g27) = 1.5708
    c: Tangent(g26,g27) = 1.5708
FEATURE [PartDesign::Pocket] Pocket016
  BaseFeature = -> Pad012
  Direction = (0,1,-2e-16)
  Length = 99.95
  Length2 = 5
  Placement = pos=(0,0,0) rot=(1,0,0;1.5708rad)
  Profile = -> Sketch031
  ReferenceAxis = -> Sketch031 [N_Axis]
  Refine = true
  Suppressed = false
  Type = 0
FEATURE [Sketcher::SketchObject] Sketch032
  ArcFitTolerance = 1e-06
  AttachmentSupport = -> [XY_Plane006]
  FullyConstrained = false
  MakeInternals = false
  MapMode = 5
  sketch-geometry (4):
    g0: LineSegment StartX=295 StartY=17.3691 StartZ=0 EndX=295 EndY=-107.641 EndZ=0
    g1: LineSegment StartX=295 StartY=-107.641 StartZ=0 EndX=389.553 EndY=-107.641 EndZ=0
    g2: LineSegment StartX=389.553 StartY=-107.641 StartZ=0 EndX=389.553 EndY=17.3691 EndZ=0
    g3: LineSegment StartX=389.553 StartY=17.3691 StartZ=0 EndX=295 EndY=17.3691 EndZ=0
  constraints (9):
    c: Coincident(g0,g1)
    c: Coincident(g1,g2)
    c: Coincident(g2,g3)
    c: Coincident(g3,g0)
    c: Vertical(g0)
    c: Vertical(g2)
    c: Horizontal(g1)
    c: Horizontal(g3)
    c: DistanceX(g-1,g0) = 295
FEATURE [PartDesign::Pocket] Pocket017
  BaseFeature = -> Pocket016
  Direction = (0,0,-1)
  Length = 5
  Length2 = 5
  Midplane = true
  Placement = pos=(0,0,0) rot=(1,0,0;1.5708rad)
  Profile = -> Sketch032
  ReferenceAxis = -> Sketch032 [N_Axis]
  Refine = true
  Suppressed = false
  Type = 0
FEATURE [Sketcher::SketchObject] Sketch044
  ArcFitTolerance = 1e-06
  AttachmentSupport = -> [XY_Plane009]
  FullyConstrained = false
  MakeInternals = false
  MapMode = 5
  sketch-geometry (4):
    g0: LineSegment StartX=295 StartY=36.1981 StartZ=0 EndX=295 EndY=-1016.06 EndZ=0
    g1: LineSegment StartX=295 StartY=-1016.06 StartZ=0 EndX=488.335 EndY=-1016.06 EndZ=0
    g2: LineSegment StartX=488.335 StartY=-1016.06 StartZ=0 EndX=488.335 EndY=36.1981 EndZ=0
    g3: LineSegment StartX=488.335 StartY=36.1981 StartZ=0 EndX=295 EndY=36.1981 EndZ=0
  constraints (9):
    c: Coincident(g0,g1)
    c: Coincident(g1,g2)
    c: Coincident(g2,g3)
    c: Coincident(g3,g0)
    c: Vertical(g0)
    c: Vertical(g2)
    c: Horizontal(g1)
    c: Horizontal(g3)
    c: DistanceX(g-1,g0) = 295
FEATURE [Sketcher::SketchObject] Sketch046
  ArcFitTolerance = 1e-06
  FullyConstrained = false
  MakeInternals = false
  Placement = pos=(0,0,0) rot=(1,0,0;1.5708rad)
  sketch-geometry (125):
    g0: BSplineCurve PolesCount=62 KnotsCount=62 Degree=3 IsPeriodic=1
    g1-g62: Circle [constr] x62 (B-spline internal-alignment scaffolding for g0; pole/knot coordinates omitted)
    g63-g124: GeomPoint [constr] x62 (B-spline internal-alignment scaffolding for g0; pole/knot coordinates omitted)
  constraints (125):
    c: InternalAlignment(g1,g0)
    c: Weight(g1) = 1
    c: InternalAlignment(g2,g0)
    c: Equal(g2,g1)
    c: InternalAlignment(g3,g0)
    c: Equal(g3,g1)
    c: InternalAlignment(g4,g0)
    c: Equal(g4,g1)
    c: InternalAlignment(g5,g0)
    c: Equal(g5,g1)
    c: InternalAlignment(g6,g0)
    c: Equal(g6,g1)
    c: InternalAlignment(g7,g0)
    c: Equal(g7,g1)
    c: InternalAlignment(g8,g0)
    c: Equal(g8,g1)
    c: InternalAlignment(g9,g0)
    c: Equal(g9,g1)
    c: InternalAlignment(g10,g0)
    c: Equal(g10,g1)
    c: InternalAlignment(g11,g0)
    c: Equal(g11,g1)
    c: InternalAlignment(g12,g0)
    c: Equal(g12,g1)
    c: InternalAlignment(g13,g0)
    c: Equal(g13,g1)
    c: InternalAlignment(g14,g0)
    c: Equal(g14,g1)
    c: InternalAlignment(g15,g0)
    c: Equal(g15,g1)
    c: InternalAlignment(g16,g0)
    c: Equal(g16,g1)
    c: InternalAlignment(g17,g0)
    c: Equal(g17,g1)
    c: InternalAlignment(g18,g0)
    c: Equal(g18,g1)
    c: InternalAlignment(g19,g0)
    c: Equal(g19,g1)
    c: InternalAlignment(g20,g0)
    c: Equal(g20,g1)
    c: InternalAlignment(g21,g0)
    c: Equal(g21,g1)
    c: InternalAlignment(g22,g0)
    c: Equal(g22,g1)
    c: InternalAlignment(g23,g0)
    c: Equal(g23,g1)
    c: InternalAlignment(g24,g0)
    c: Equal(g24,g1)
    c: InternalAlignment(g25,g0)
    c: Equal(g25,g1)
    c: InternalAlignment(g26,g0)
    c: Equal(g26,g1)
    c: InternalAlignment(g27,g0)
    c: Equal(g27,g1)
    c: InternalAlignment(g28,g0)
    c: Equal(g28,g1)
    c: InternalAlignment(g29,g0)
    c: Equal(g29,g1)
    c: InternalAlignment(g30,g0)
    c: Equal(g30,g1)
    c: InternalAlignment(g31,g0)
    c: Equal(g31,g1)
    c: InternalAlignment(g32,g0)
    c: Equal(g32,g1)
    c: InternalAlignment(g33,g0)
    c: Equal(g33,g1)
    c: InternalAlignment(g34,g0)
    c: Equal(g34,g1)
    c: InternalAlignment(g35,g0)
    c: Equal(g35,g1)
    c: InternalAlignment(g36,g0)
    c: Equal(g36,g1)
    c: InternalAlignment(g37,g0)
    c: Equal(g37,g1)
    c: InternalAlignment(g38,g0)
    c: Equal(g38,g1)
    c: InternalAlignment(g39,g0)
    c: Equal(g39,g1)
    c: InternalAlignment(g40,g0)
    c: Equal(g40,g1)
    c: InternalAlignment(g41,g0)
    c: Equal(g41,g1)
    c: InternalAlignment(g42,g0)
    c: Equal(g42,g1)
    c: InternalAlignment(g43,g0)
    c: Equal(g43,g1)
    c: InternalAlignment(g44,g0)
    c: Equal(g44,g1)
    c: InternalAlignment(g45,g0)
    c: Equal(g45,g1)
    c: InternalAlignment(g46,g0)
    c: Equal(g46,g1)
    c: InternalAlignment(g47,g0)
    c: Equal(g47,g1)
    c: InternalAlignment(g48,g0)
    c: Equal(g48,g1)
    c: InternalAlignment(g49,g0)
    c: Equal(g49,g1)
    c: InternalAlignment(g50,g0)
    c: Equal(g50,g1)
    c: InternalAlignment(g51,g0)
    c: Equal(g51,g1)
    c: InternalAlignment(g52,g0)
    c: Equal(g52,g1)
    c: InternalAlignment(g53,g0)
    c: Equal(g53,g1)
    c: InternalAlignment(g54,g0)
    c: Equal(g54,g1)
    c: InternalAlignment(g55,g0)
    c: Equal(g55,g1)
    c: InternalAlignment(g56,g0)
    c: Equal(g56,g1)
    c: InternalAlignment(g57,g0)
    c: Equal(g57,g1)
    c: InternalAlignment(g58,g0)
    c: Equal(g58,g1)
    c: InternalAlignment(g59,g0)
    c: Equal(g59,g1)
    c: InternalAlignment(g60,g0)
    c: Equal(g60,g1)
    c: InternalAlignment(g61,g0)
    c: Equal(g61,g1)
    c: InternalAlignment(g62,g0)
    c: Equal(g62,g1)
    c: InternalAlignment(g63-g124 -> g0) x62
FEATURE [PartDesign::Pad] Pad018
  Direction = (0,-1,2e-16)
  Length = 99.8
  Length2 = 10
  Placement = pos=(0,0,0) rot=(1,0,0;1.5708rad)
  Profile = -> Sketch046
  ReferenceAxis = -> Sketch046 [N_Axis]
  Refine = true
  Suppressed = false
  Type = 0
FEATURE [PartDesign::Pocket] Pocket024
  BaseFeature = -> Pad018
  Direction = (0,0,-1)
  Length = 100
  Length2 = 5
  Midplane = true
  Placement = pos=(0,0,0) rot=(1,0,0;1.5708rad)
  Profile = -> Sketch044
  ReferenceAxis = -> Sketch044 [N_Axis]
  Refine = true
  Suppressed = false
  Type = 0
FEATURE [PartDesign::Thickness] Thickness002
  Base = -> Pocket024 [Face4,Face2]
  BaseFeature = -> Pocket024
  Intersection = false
  Join = 0
  Mode = 0
  Refine = true
  SupportTransform = false
  Suppressed = false
  Value = 3
FEATURE [Sketcher::SketchObject] Sketch045
  ArcFitTolerance = 1e-06
  AttachmentSupport = -> [Thickness002]
  FullyConstrained = false
  MakeInternals = false
  MapMode = 5
  Placement = pos=(0,-99.8,2.2e-14) rot=(1,0,0;1.5708rad)
  sketch-geometry (15):
    g0: LineSegment [constr] StartX=4.5568 StartY=5.71171 StartZ=0 EndX=7.88662 EndY=7.89278 EndZ=0
    g1: LineSegment StartX=5.46609 StartY=6.3073 StartZ=0 EndX=2.696 EndY=10.5364 EndZ=0
    g2: LineSegment StartX=2.696 StartY=10.5364 StartZ=0 EndX=32.4943 EndY=27.0739 EndZ=0
    g3: LineSegment StartX=32.4943 StartY=27.0739 StartZ=0 EndX=156.488 EndY=39.0363 EndZ=0
    g4: LineSegment StartX=156.488 StartY=39.0363 StartZ=0 EndX=248.898 EndY=26.6449 EndZ=0
    g5: LineSegment StartX=248.898 StartY=26.6449 StartZ=0 EndX=329.144 EndY=7.08029 EndZ=0
    g6: LineSegment StartX=329.144 StartY=7.08029 StartZ=0 EndX=328 EndY=-15.9084 EndZ=0
    g7: LineSegment StartX=328 StartY=-15.9084 StartZ=0 EndX=200.054 EndY=-15.9084 EndZ=0
    g8: LineSegment StartX=200.054 StartY=-15.9084 StartZ=0 EndX=64.7748 EndY=-15.9084 EndZ=0
    g9: LineSegment StartX=64.7748 StartY=-15.9084 StartZ=0 EndX=16.3454 EndY=-20.7039 EndZ=0
    g10: LineSegment StartX=16.3454 StartY=-20.7039 StartZ=0 EndX=2.88885 EndY=-12.2412 EndZ=0
    g11: LineSegment [constr] StartX=2.3291 StartY=-2.35546 StartZ=0 EndX=5.23499 EndY=-3.24958 EndZ=0
    g12: LineSegment StartX=2.88053 StartY=-2.52513 StartZ=0 EndX=1.81302 EndY=-5.99451 EndZ=0
    g13: LineSegment StartX=1.81302 StartY=-5.99451 StartZ=0 EndX=2.88885 EndY=-12.2412 EndZ=0
    g14: LineSegment StartX=5.46609 StartY=6.3073 StartZ=0 EndX=2.88053 EndY=-2.52513 EndZ=0
  constraints (22):
    c: PointOnObject(g1,g0)
    c: Perpendicular(g0,g1)
    c: Block(g1)
    c: Block(g0)
    c: Coincident(g1,g2)
    c: Coincident(g2,g3)
    c: Coincident(g3,g4)
    c: Coincident(g4,g5)
    c: Coincident(g5,g6)
    c: Coincident(g6,g7)
    c: Horizontal(g7)
    c: Coincident(g7,g8)
    c: Horizontal(g8)
    c: Coincident(g8,g9)
    c: Coincident(g9,g10)
    c: Block(g11)
    c: PointOnObject(g12,g11)
    c: Perpendicular(g11,g12)
    c: Coincident(g13,g12)
    c: Coincident(g13,g10)
    c: Coincident(g14,g1)
    c: Coincident(g14,g12)
FEATURE [PartDesign::Pocket] Pocket025
  BaseFeature = -> Thickness002
  Direction = (0,1,-2e-16)
  Length = 1000
  Length2 = 5
  Profile = -> Sketch045
  ReferenceAxis = -> Sketch045 [N_Axis]
  Refine = true
  Suppressed = false
  Type = 0
FEATURE [PartDesign::Body] Body009  label="leading edge 003"
  AllowCompound = false
  Group = -> [Pad018,Sketch044,Pocket024,Thickness002,Sketch045,Pocket025,Sketch046]
  Origin = -> Origin009
  Placement = pos=(0,-103.6,0) rot=(0,0,1;0rad)
  Tip = -> Pocket025
FEATURE [Sketcher::SketchObject] Sketch047
  ArcFitTolerance = 1e-06
  AttachmentSupport = -> [XY_Plane010]
  FullyConstrained = false
  MakeInternals = false
  MapMode = 5
  sketch-geometry (4):
    g0: LineSegment StartX=295 StartY=36.1981 StartZ=0 EndX=295 EndY=-1016.06 EndZ=0
    g1: LineSegment StartX=295 StartY=-1016.06 StartZ=0 EndX=488.335 EndY=-1016.06 EndZ=0
    g2: LineSegment StartX=488.335 StartY=-1016.06 StartZ=0 EndX=488.335 EndY=36.1981 EndZ=0
    g3: LineSegment StartX=488.335 StartY=36.1981 StartZ=0 EndX=295 EndY=36.1981 EndZ=0
  constraints (9):
    c: Coincident(g0,g1)
    c: Coincident(g1,g2)
    c: Coincident(g2,g3)
    c: Coincident(g3,g0)
    c: Vertical(g0)
    c: Vertical(g2)
    c: Horizontal(g1)
    c: Horizontal(g3)
    c: DistanceX(g-1,g0) = 295
FEATURE [Sketcher::SketchObject] Sketch049
  ArcFitTolerance = 1e-06
  FullyConstrained = false
  MakeInternals = false
  Placement = pos=(0,0,0) rot=(1,0,0;1.5708rad)
  sketch-geometry (125):
    g0: BSplineCurve PolesCount=62 KnotsCount=62 Degree=3 IsPeriodic=1
    g1-g62: Circle [constr] x62 (B-spline internal-alignment scaffolding for g0; pole/knot coordinates omitted)
    g63-g124: GeomPoint [constr] x62 (B-spline internal-alignment scaffolding for g0; pole/knot coordinates omitted)
  constraints (125):
    c: InternalAlignment(g1,g0)
    c: Weight(g1) = 1
    c: InternalAlignment(g2,g0)
    c: Equal(g2,g1)
    c: InternalAlignment(g3,g0)
    c: Equal(g3,g1)
    c: InternalAlignment(g4,g0)
    c: Equal(g4,g1)
    c: InternalAlignment(g5,g0)
    c: Equal(g5,g1)
    c: InternalAlignment(g6,g0)
    c: Equal(g6,g1)
    c: InternalAlignment(g7,g0)
    c: Equal(g7,g1)
    c: InternalAlignment(g8,g0)
    c: Equal(g8,g1)
    c: InternalAlignment(g9,g0)
    c: Equal(g9,g1)
    c: InternalAlignment(g10,g0)
    c: Equal(g10,g1)
    c: InternalAlignment(g11,g0)
    c: Equal(g11,g1)
    c: InternalAlignment(g12,g0)
    c: Equal(g12,g1)
    c: InternalAlignment(g13,g0)
    c: Equal(g13,g1)
    c: InternalAlignment(g14,g0)
    c: Equal(g14,g1)
    c: InternalAlignment(g15,g0)
    c: Equal(g15,g1)
    c: InternalAlignment(g16,g0)
    c: Equal(g16,g1)
    c: InternalAlignment(g17,g0)
    c: Equal(g17,g1)
    c: InternalAlignment(g18,g0)
    c: Equal(g18,g1)
    c: InternalAlignment(g19,g0)
    c: Equal(g19,g1)
    c: InternalAlignment(g20,g0)
    c: Equal(g20,g1)
    c: InternalAlignment(g21,g0)
    c: Equal(g21,g1)
    c: InternalAlignment(g22,g0)
    c: Equal(g22,g1)
    c: InternalAlignment(g23,g0)
    c: Equal(g23,g1)
    c: InternalAlignment(g24,g0)
    c: Equal(g24,g1)
    c: InternalAlignment(g25,g0)
    c: Equal(g25,g1)
    c: InternalAlignment(g26,g0)
    c: Equal(g26,g1)
    c: InternalAlignment(g27,g0)
    c: Equal(g27,g1)
    c: InternalAlignment(g28,g0)
    c: Equal(g28,g1)
    c: InternalAlignment(g29,g0)
    c: Equal(g29,g1)
    c: InternalAlignment(g30,g0)
    c: Equal(g30,g1)
    c: InternalAlignment(g31,g0)
    c: Equal(g31,g1)
    c: InternalAlignment(g32,g0)
    c: Equal(g32,g1)
    c: InternalAlignment(g33,g0)
    c: Equal(g33,g1)
    c: InternalAlignment(g34,g0)
    c: Equal(g34,g1)
    c: InternalAlignment(g35,g0)
    c: Equal(g35,g1)
    c: InternalAlignment(g36,g0)
    c: Equal(g36,g1)
    c: InternalAlignment(g37,g0)
    c: Equal(g37,g1)
    c: InternalAlignment(g38,g0)
    c: Equal(g38,g1)
    c: InternalAlignment(g39,g0)
    c: Equal(g39,g1)
    c: InternalAlignment(g40,g0)
    c: Equal(g40,g1)
    c: InternalAlignment(g41,g0)
    c: Equal(g41,g1)
    c: InternalAlignment(g42,g0)
    c: Equal(g42,g1)
    c: InternalAlignment(g43,g0)
    c: Equal(g43,g1)
    c: InternalAlignment(g44,g0)
    c: Equal(g44,g1)
    c: InternalAlignment(g45,g0)
    c: Equal(g45,g1)
    c: InternalAlignment(g46,g0)
    c: Equal(g46,g1)
    c: InternalAlignment(g47,g0)
    c: Equal(g47,g1)
    c: InternalAlignment(g48,g0)
    c: Equal(g48,g1)
    c: InternalAlignment(g49,g0)
    c: Equal(g49,g1)
    c: InternalAlignment(g50,g0)
    c: Equal(g50,g1)
    c: InternalAlignment(g51,g0)
    c: Equal(g51,g1)
    c: InternalAlignment(g52,g0)
    c: Equal(g52,g1)
    c: InternalAlignment(g53,g0)
    c: Equal(g53,g1)
    c: InternalAlignment(g54,g0)
    c: Equal(g54,g1)
    c: InternalAlignment(g55,g0)
    c: Equal(g55,g1)
    c: InternalAlignment(g56,g0)
    c: Equal(g56,g1)
    c: InternalAlignment(g57,g0)
    c: Equal(g57,g1)
    c: InternalAlignment(g58,g0)
    c: Equal(g58,g1)
    c: InternalAlignment(g59,g0)
    c: Equal(g59,g1)
    c: InternalAlignment(g60,g0)
    c: Equal(g60,g1)
    c: InternalAlignment(g61,g0)
    c: Equal(g61,g1)
    c: InternalAlignment(g62,g0)
    c: Equal(g62,g1)
    c: InternalAlignment(g63-g124 -> g0) x62
FEATURE [PartDesign::Pad] Pad019
  Direction = (0,-1,2e-16)
  Length = 99.8
  Length2 = 10
  Placement = pos=(0,0,0) rot=(1,0,0;1.5708rad)
  Profile = -> Sketch049
  ReferenceAxis = -> Sketch049 [N_Axis]
  Refine = true
  Suppressed = false
  Type = 0
FEATURE [PartDesign::Pocket] Pocket026
  BaseFeature = -> Pad019
  Direction = (0,0,-1)
  Length = 100
  Length2 = 5
  Midplane = true
  Placement = pos=(0,0,0) rot=(1,0,0;1.5708rad)
  Profile = -> Sketch047
  ReferenceAxis = -> Sketch047 [N_Axis]
  Refine = true
  Suppressed = false
  Type = 0
FEATURE [PartDesign::Thickness] Thickness003
  Base = -> Pocket026 [Face4,Face2]
  BaseFeature = -> Pocket026
  Intersection = false
  Join = 0
  Mode = 0
  Refine = true
  SupportTransform = false
  Suppressed = false
  Value = 3
FEATURE [Sketcher::SketchObject] Sketch048
  ArcFitTolerance = 1e-06
  AttachmentSupport = -> [Thickness003]
  FullyConstrained = false
  MakeInternals = false
  MapMode = 5
  Placement = pos=(0,-99.8,2.2e-14) rot=(1,0,0;1.5708rad)
  sketch-geometry (15):
    g0: LineSegment [constr] StartX=4.5568 StartY=5.71171 StartZ=0 EndX=7.88662 EndY=7.89278 EndZ=0
    g1: LineSegment StartX=5.46609 StartY=6.3073 StartZ=0 EndX=2.696 EndY=10.5364 EndZ=0
    g2: LineSegment StartX=2.696 StartY=10.5364 StartZ=0 EndX=32.4943 EndY=27.0739 EndZ=0
    g3: LineSegment StartX=32.4943 StartY=27.0739 StartZ=0 EndX=156.488 EndY=39.0363 EndZ=0
    g4: LineSegment StartX=156.488 StartY=39.0363 StartZ=0 EndX=248.898 EndY=26.6449 EndZ=0
    g5: LineSegment StartX=248.898 StartY=26.6449 StartZ=0 EndX=329.144 EndY=7.08029 EndZ=0
    g6: LineSegment StartX=329.144 StartY=7.08029 StartZ=0 EndX=328 EndY=-15.9084 EndZ=0
    g7: LineSegment StartX=328 StartY=-15.9084 StartZ=0 EndX=200.054 EndY=-15.9084 EndZ=0
    g8: LineSegment StartX=200.054 StartY=-15.9084 StartZ=0 EndX=64.7748 EndY=-15.9084 EndZ=0
    g9: LineSegment StartX=64.7748 StartY=-15.9084 StartZ=0 EndX=16.3454 EndY=-20.7039 EndZ=0
    g10: LineSegment StartX=16.3454 StartY=-20.7039 StartZ=0 EndX=2.88885 EndY=-12.2412 EndZ=0
    g11: LineSegment [constr] StartX=2.3291 StartY=-2.35546 StartZ=0 EndX=5.23499 EndY=-3.24958 EndZ=0
    g12: LineSegment StartX=2.88053 StartY=-2.52513 StartZ=0 EndX=1.81302 EndY=-5.99451 EndZ=0
    g13: LineSegment StartX=1.81302 StartY=-5.99451 StartZ=0 EndX=2.88885 EndY=-12.2412 EndZ=0
    g14: LineSegment StartX=5.46609 StartY=6.3073 StartZ=0 EndX=2.88053 EndY=-2.52513 EndZ=0
  constraints (22):
    c: PointOnObject(g1,g0)
    c: Perpendicular(g0,g1)
    c: Block(g1)
    c: Block(g0)
    c: Coincident(g1,g2)
    c: Coincident(g2,g3)
    c: Coincident(g3,g4)
    c: Coincident(g4,g5)
    c: Coincident(g5,g6)
    c: Coincident(g6,g7)
    c: Horizontal(g7)
    c: Coincident(g7,g8)
    c: Horizontal(g8)
    c: Coincident(g8,g9)
    c: Coincident(g9,g10)
    c: Block(g11)
    c: PointOnObject(g12,g11)
    c: Perpendicular(g11,g12)
    c: Coincident(g13,g12)
    c: Coincident(g13,g10)
    c: Coincident(g14,g1)
    c: Coincident(g14,g12)
FEATURE [PartDesign::Pocket] Pocket027
  BaseFeature = -> Thickness003
  Direction = (0,1,-2e-16)
  Length = 1000
  Length2 = 5
  Profile = -> Sketch048
  ReferenceAxis = -> Sketch048 [N_Axis]
  Refine = true
  Suppressed = false
  Type = 0
FEATURE [PartDesign::Body] Body010  label="leading edge 004"
  AllowCompound = false
  Group = -> [Pad019,Sketch047,Pocket026,Thickness003,Sketch048,Pocket027,Sketch049]
  Origin = -> Origin010
  Placement = pos=(0,-203.6,0) rot=(0,0,1;0rad)
  Tip = -> Pocket027
FEATURE [Sketcher::SketchObject] Sketch059
  ArcFitTolerance = 1e-06
  AttachmentSupport = -> [XY_Plane013]
  FullyConstrained = false
  MakeInternals = false
  MapMode = 5
  sketch-geometry (4):
    g0: LineSegment StartX=295 StartY=36.1981 StartZ=0 EndX=295 EndY=-1016.06 EndZ=0
    g1: LineSegment StartX=295 StartY=-1016.06 StartZ=0 EndX=488.335 EndY=-1016.06 EndZ=0
    g2: LineSegment StartX=488.335 StartY=-1016.06 StartZ=0 EndX=488.335 EndY=36.1981 EndZ=0
    g3: LineSegment StartX=488.335 StartY=36.1981 StartZ=0 EndX=295 EndY=36.1981 EndZ=0
  constraints (9):
    c: Coincident(g0,g1)
    c: Coincident(g1,g2)
    c: Coincident(g2,g3)
    c: Coincident(g3,g0)
    c: Vertical(g0)
    c: Vertical(g2)
    c: Horizontal(g1)
    c: Horizontal(g3)
    c: DistanceX(g-1,g0) = 295
FEATURE [Sketcher::SketchObject] Sketch061
  ArcFitTolerance = 1e-06
  FullyConstrained = false
  MakeInternals = false
  Placement = pos=(0,0,0) rot=(1,0,0;1.5708rad)
  sketch-geometry (125):
    g0: BSplineCurve PolesCount=62 KnotsCount=62 Degree=3 IsPeriodic=1
    g1-g62: Circle [constr] x62 (B-spline internal-alignment scaffolding for g0; pole/knot coordinates omitted)
    g63-g124: GeomPoint [constr] x62 (B-spline internal-alignment scaffolding for g0; pole/knot coordinates omitted)
  constraints (125):
    c: InternalAlignment(g1,g0)
    c: Weight(g1) = 1
    c: InternalAlignment(g2,g0)
    c: Equal(g2,g1)
    c: InternalAlignment(g3,g0)
    c: Equal(g3,g1)
    c: InternalAlignment(g4,g0)
    c: Equal(g4,g1)
    c: InternalAlignment(g5,g0)
    c: Equal(g5,g1)
    c: InternalAlignment(g6,g0)
    c: Equal(g6,g1)
    c: InternalAlignment(g7,g0)
    c: Equal(g7,g1)
    c: InternalAlignment(g8,g0)
    c: Equal(g8,g1)
    c: InternalAlignment(g9,g0)
    c: Equal(g9,g1)
    c: InternalAlignment(g10,g0)
    c: Equal(g10,g1)
    c: InternalAlignment(g11,g0)
    c: Equal(g11,g1)
    c: InternalAlignment(g12,g0)
    c: Equal(g12,g1)
    c: InternalAlignment(g13,g0)
    c: Equal(g13,g1)
    c: InternalAlignment(g14,g0)
    c: Equal(g14,g1)
    c: InternalAlignment(g15,g0)
    c: Equal(g15,g1)
    c: InternalAlignment(g16,g0)
    c: Equal(g16,g1)
    c: InternalAlignment(g17,g0)
    c: Equal(g17,g1)
    c: InternalAlignment(g18,g0)
    c: Equal(g18,g1)
    c: InternalAlignment(g19,g0)
    c: Equal(g19,g1)
    c: InternalAlignment(g20,g0)
    c: Equal(g20,g1)
    c: InternalAlignment(g21,g0)
    c: Equal(g21,g1)
    c: InternalAlignment(g22,g0)
    c: Equal(g22,g1)
    c: InternalAlignment(g23,g0)
    c: Equal(g23,g1)
    c: InternalAlignment(g24,g0)
    c: Equal(g24,g1)
    c: InternalAlignment(g25,g0)
    c: Equal(g25,g1)
    c: InternalAlignment(g26,g0)
    c: Equal(g26,g1)
    c: InternalAlignment(g27,g0)
    c: Equal(g27,g1)
    c: InternalAlignment(g28,g0)
    c: Equal(g28,g1)
    c: InternalAlignment(g29,g0)
    c: Equal(g29,g1)
    c: InternalAlignment(g30,g0)
    c: Equal(g30,g1)
    c: InternalAlignment(g31,g0)
    c: Equal(g31,g1)
    c: InternalAlignment(g32,g0)
    c: Equal(g32,g1)
    c: InternalAlignment(g33,g0)
    c: Equal(g33,g1)
    c: InternalAlignment(g34,g0)
    c: Equal(g34,g1)
    c: InternalAlignment(g35,g0)
    c: Equal(g35,g1)
    c: InternalAlignment(g36,g0)
    c: Equal(g36,g1)
    c: InternalAlignment(g37,g0)
    c: Equal(g37,g1)
    c: InternalAlignment(g38,g0)
    c: Equal(g38,g1)
    c: InternalAlignment(g39,g0)
    c: Equal(g39,g1)
    c: InternalAlignment(g40,g0)
    c: Equal(g40,g1)
    c: InternalAlignment(g41,g0)
    c: Equal(g41,g1)
    c: InternalAlignment(g42,g0)
    c: Equal(g42,g1)
    c: InternalAlignment(g43,g0)
    c: Equal(g43,g1)
    c: InternalAlignment(g44,g0)
    c: Equal(g44,g1)
    c: InternalAlignment(g45,g0)
    c: Equal(g45,g1)
    c: InternalAlignment(g46,g0)
    c: Equal(g46,g1)
    c: InternalAlignment(g47,g0)
    c: Equal(g47,g1)
    c: InternalAlignment(g48,g0)
    c: Equal(g48,g1)
    c: InternalAlignment(g49,g0)
    c: Equal(g49,g1)
    c: InternalAlignment(g50,g0)
    c: Equal(g50,g1)
    c: InternalAlignment(g51,g0)
    c: Equal(g51,g1)
    c: InternalAlignment(g52,g0)
    c: Equal(g52,g1)
    c: InternalAlignment(g53,g0)
    c: Equal(g53,g1)
    c: InternalAlignment(g54,g0)
    c: Equal(g54,g1)
    c: InternalAlignment(g55,g0)
    c: Equal(g55,g1)
    c: InternalAlignment(g56,g0)
    c: Equal(g56,g1)
    c: InternalAlignment(g57,g0)
    c: Equal(g57,g1)
    c: InternalAlignment(g58,g0)
    c: Equal(g58,g1)
    c: InternalAlignment(g59,g0)
    c: Equal(g59,g1)
    c: InternalAlignment(g60,g0)
    c: Equal(g60,g1)
    c: InternalAlignment(g61,g0)
    c: Equal(g61,g1)
    c: InternalAlignment(g62,g0)
    c: Equal(g62,g1)
    c: InternalAlignment(g63-g124 -> g0) x62
FEATURE [PartDesign::Pad] Pad024
  Direction = (0,-1,2e-16)
  Length = 99.8
  Length2 = 10
  Placement = pos=(0,0,0) rot=(1,0,0;1.5708rad)
  Profile = -> Sketch061
  ReferenceAxis = -> Sketch061 [N_Axis]
  Refine = true
  Suppressed = false
  Type = 0
FEATURE [PartDesign::Pocket] Pocket033
  BaseFeature = -> Pad024
  Direction = (0,0,-1)
  Length = 100
  Length2 = 5
  Midplane = true
  Placement = pos=(0,0,0) rot=(1,0,0;1.5708rad)
  Profile = -> Sketch059
  ReferenceAxis = -> Sketch059 [N_Axis]
  Refine = true
  Suppressed = false
  Type = 0
FEATURE [PartDesign::Thickness] Thickness004
  Base = -> Pocket033 [Face4,Face2]
  BaseFeature = -> Pocket033
  Intersection = false
  Join = 0
  Mode = 0
  Refine = true
  SupportTransform = false
  Suppressed = false
  Value = 3
FEATURE [Sketcher::SketchObject] Sketch060
  ArcFitTolerance = 1e-06
  AttachmentSupport = -> [Thickness004]
  FullyConstrained = false
  MakeInternals = false
  MapMode = 5
  Placement = pos=(0,-99.8,2.2e-14) rot=(1,0,0;1.5708rad)
  sketch-geometry (15):
    g0: LineSegment [constr] StartX=4.5568 StartY=5.71171 StartZ=0 EndX=7.88662 EndY=7.89278 EndZ=0
    g1: LineSegment StartX=5.46609 StartY=6.3073 StartZ=0 EndX=2.696 EndY=10.5364 EndZ=0
    g2: LineSegment StartX=2.696 StartY=10.5364 StartZ=0 EndX=32.4943 EndY=27.0739 EndZ=0
    g3: LineSegment StartX=32.4943 StartY=27.0739 StartZ=0 EndX=156.488 EndY=39.0363 EndZ=0
    g4: LineSegment StartX=156.488 StartY=39.0363 StartZ=0 EndX=248.898 EndY=26.6449 EndZ=0
    g5: LineSegment StartX=248.898 StartY=26.6449 StartZ=0 EndX=329.144 EndY=7.08029 EndZ=0
    g6: LineSegment StartX=329.144 StartY=7.08029 StartZ=0 EndX=328 EndY=-15.9084 EndZ=0
    g7: LineSegment StartX=328 StartY=-15.9084 StartZ=0 EndX=200.054 EndY=-15.9084 EndZ=0
    g8: LineSegment StartX=200.054 StartY=-15.9084 StartZ=0 EndX=64.7748 EndY=-15.9084 EndZ=0
    g9: LineSegment StartX=64.7748 StartY=-15.9084 StartZ=0 EndX=16.3454 EndY=-20.7039 EndZ=0
    g10: LineSegment StartX=16.3454 StartY=-20.7039 StartZ=0 EndX=2.88885 EndY=-12.2412 EndZ=0
    g11: LineSegment [constr] StartX=2.3291 StartY=-2.35546 StartZ=0 EndX=5.23499 EndY=-3.24958 EndZ=0
    g12: LineSegment StartX=2.88053 StartY=-2.52513 StartZ=0 EndX=1.81302 EndY=-5.99451 EndZ=0
    g13: LineSegment StartX=1.81302 StartY=-5.99451 StartZ=0 EndX=2.88885 EndY=-12.2412 EndZ=0
    g14: LineSegment StartX=5.46609 StartY=6.3073 StartZ=0 EndX=2.88053 EndY=-2.52513 EndZ=0
  constraints (22):
    c: PointOnObject(g1,g0)
    c: Perpendicular(g0,g1)
    c: Block(g1)
    c: Block(g0)
    c: Coincident(g1,g2)
    c: Coincident(g2,g3)
    c: Coincident(g3,g4)
    c: Coincident(g4,g5)
    c: Coincident(g5,g6)
    c: Coincident(g6,g7)
    c: Horizontal(g7)
    c: Coincident(g7,g8)
    c: Horizontal(g8)
    c: Coincident(g8,g9)
    c: Coincident(g9,g10)
    c: Block(g11)
    c: PointOnObject(g12,g11)
    c: Perpendicular(g11,g12)
    c: Coincident(g13,g12)
    c: Coincident(g13,g10)
    c: Coincident(g14,g1)
    c: Coincident(g14,g12)
FEATURE [PartDesign::Pocket] Pocket034
  BaseFeature = -> Thickness004
  Direction = (0,1,-2e-16)
  Length = 1000
  Length2 = 5
  Profile = -> Sketch060
  ReferenceAxis = -> Sketch060 [N_Axis]
  Refine = true
  Suppressed = false
  Type = 0
FEATURE [PartDesign::Body] Body013  label="leading edge 005"
  AllowCompound = false
  Group = -> [Pad024,Sketch059,Pocket033,Thickness004,Sketch060,Pocket034,Sketch061]
  Origin = -> Origin013
  Placement = pos=(0,-303.6,0) rot=(0,0,1;0rad)
  Tip = -> Pocket034
FEATURE [Sketcher::SketchObject] Sketch071
  ArcFitTolerance = 1e-06
  AttachmentSupport = -> [XY_Plane016]
  FullyConstrained = false
  MakeInternals = false
  MapMode = 5
  sketch-geometry (4):
    g0: LineSegment StartX=295 StartY=36.1981 StartZ=0 EndX=295 EndY=-1016.06 EndZ=0
    g1: LineSegment StartX=295 StartY=-1016.06 StartZ=0 EndX=488.335 EndY=-1016.06 EndZ=0
    g2: LineSegment StartX=488.335 StartY=-1016.06 StartZ=0 EndX=488.335 EndY=36.1981 EndZ=0
    g3: LineSegment StartX=488.335 StartY=36.1981 StartZ=0 EndX=295 EndY=36.1981 EndZ=0
  constraints (9):
    c: Coincident(g0,g1)
    c: Coincident(g1,g2)
    c: Coincident(g2,g3)
    c: Coincident(g3,g0)
    c: Vertical(g0)
    c: Vertical(g2)
    c: Horizontal(g1)
    c: Horizontal(g3)
    c: DistanceX(g-1,g0) = 295
FEATURE [Sketcher::SketchObject] Sketch073
  ArcFitTolerance = 1e-06
  FullyConstrained = false
  MakeInternals = false
  Placement = pos=(0,0,0) rot=(1,0,0;1.5708rad)
  sketch-geometry (125):
    g0: BSplineCurve PolesCount=62 KnotsCount=62 Degree=3 IsPeriodic=1
    g1-g62: Circle [constr] x62 (B-spline internal-alignment scaffolding for g0; pole/knot coordinates omitted)
    g63-g124: GeomPoint [constr] x62 (B-spline internal-alignment scaffolding for g0; pole/knot coordinates omitted)
  constraints (125):
    c: InternalAlignment(g1,g0)
    c: Weight(g1) = 1
    c: InternalAlignment(g2,g0)
    c: Equal(g2,g1)
    c: InternalAlignment(g3,g0)
    c: Equal(g3,g1)
    c: InternalAlignment(g4,g0)
    c: Equal(g4,g1)
    c: InternalAlignment(g5,g0)
    c: Equal(g5,g1)
    c: InternalAlignment(g6,g0)
    c: Equal(g6,g1)
    c: InternalAlignment(g7,g0)
    c: Equal(g7,g1)
    c: InternalAlignment(g8,g0)
    c: Equal(g8,g1)
    c: InternalAlignment(g9,g0)
    c: Equal(g9,g1)
    c: InternalAlignment(g10,g0)
    c: Equal(g10,g1)
    c: InternalAlignment(g11,g0)
    c: Equal(g11,g1)
    c: InternalAlignment(g12,g0)
    c: Equal(g12,g1)
    c: InternalAlignment(g13,g0)
    c: Equal(g13,g1)
    c: InternalAlignment(g14,g0)
    c: Equal(g14,g1)
    c: InternalAlignment(g15,g0)
    c: Equal(g15,g1)
    c: InternalAlignment(g16,g0)
    c: Equal(g16,g1)
    c: InternalAlignment(g17,g0)
    c: Equal(g17,g1)
    c: InternalAlignment(g18,g0)
    c: Equal(g18,g1)
    c: InternalAlignment(g19,g0)
    c: Equal(g19,g1)
    c: InternalAlignment(g20,g0)
    c: Equal(g20,g1)
    c: InternalAlignment(g21,g0)
    c: Equal(g21,g1)
    c: InternalAlignment(g22,g0)
    c: Equal(g22,g1)
    c: InternalAlignment(g23,g0)
    c: Equal(g23,g1)
    c: InternalAlignment(g24,g0)
    c: Equal(g24,g1)
    c: InternalAlignment(g25,g0)
    c: Equal(g25,g1)
    c: InternalAlignment(g26,g0)
    c: Equal(g26,g1)
    c: InternalAlignment(g27,g0)
    c: Equal(g27,g1)
    c: InternalAlignment(g28,g0)
    c: Equal(g28,g1)
    c: InternalAlignment(g29,g0)
    c: Equal(g29,g1)
    c: InternalAlignment(g30,g0)
    c: Equal(g30,g1)
    c: InternalAlignment(g31,g0)
    c: Equal(g31,g1)
    c: InternalAlignment(g32,g0)
    c: Equal(g32,g1)
    c: InternalAlignment(g33,g0)
    c: Equal(g33,g1)
    c: InternalAlignment(g34,g0)
    c: Equal(g34,g1)
    c: InternalAlignment(g35,g0)
    c: Equal(g35,g1)
    c: InternalAlignment(g36,g0)
    c: Equal(g36,g1)
    c: InternalAlignment(g37,g0)
    c: Equal(g37,g1)
    c: InternalAlignment(g38,g0)
    c: Equal(g38,g1)
    c: InternalAlignment(g39,g0)
    c: Equal(g39,g1)
    c: InternalAlignment(g40,g0)
    c: Equal(g40,g1)
    c: InternalAlignment(g41,g0)
    c: Equal(g41,g1)
    c: InternalAlignment(g42,g0)
    c: Equal(g42,g1)
    c: InternalAlignment(g43,g0)
    c: Equal(g43,g1)
    c: InternalAlignment(g44,g0)
    c: Equal(g44,g1)
    c: InternalAlignment(g45,g0)
    c: Equal(g45,g1)
    c: InternalAlignment(g46,g0)
    c: Equal(g46,g1)
    c: InternalAlignment(g47,g0)
    c: Equal(g47,g1)
    c: InternalAlignment(g48,g0)
    c: Equal(g48,g1)
    c: InternalAlignment(g49,g0)
    c: Equal(g49,g1)
    c: InternalAlignment(g50,g0)
    c: Equal(g50,g1)
    c: InternalAlignment(g51,g0)
    c: Equal(g51,g1)
    c: InternalAlignment(g52,g0)
    c: Equal(g52,g1)
    c: InternalAlignment(g53,g0)
    c: Equal(g53,g1)
    c: InternalAlignment(g54,g0)
    c: Equal(g54,g1)
    c: InternalAlignment(g55,g0)
    c: Equal(g55,g1)
    c: InternalAlignment(g56,g0)
    c: Equal(g56,g1)
    c: InternalAlignment(g57,g0)
    c: Equal(g57,g1)
    c: InternalAlignment(g58,g0)
    c: Equal(g58,g1)
    c: InternalAlignment(g59,g0)
    c: Equal(g59,g1)
    c: InternalAlignment(g60,g0)
    c: Equal(g60,g1)
    c: InternalAlignment(g61,g0)
    c: Equal(g61,g1)
    c: InternalAlignment(g62,g0)
    c: Equal(g62,g1)
    c: InternalAlignment(g63-g124 -> g0) x62
FEATURE [PartDesign::Pad] Pad029
  Direction = (0,-1,2e-16)
  Length = 99.8
  Length2 = 10
  Placement = pos=(0,0,0) rot=(1,0,0;1.5708rad)
  Profile = -> Sketch073
  ReferenceAxis = -> Sketch073 [N_Axis]
  Refine = true
  Suppressed = false
  Type = 0
FEATURE [PartDesign::Pocket] Pocket040
  BaseFeature = -> Pad029
  Direction = (0,0,-1)
  Length = 100
  Length2 = 5
  Midplane = true
  Placement = pos=(0,0,0) rot=(1,0,0;1.5708rad)
  Profile = -> Sketch071
  ReferenceAxis = -> Sketch071 [N_Axis]
  Refine = true
  Suppressed = false
  Type = 0
FEATURE [PartDesign::Thickness] Thickness005
  Base = -> Pocket040 [Face4,Face2]
  BaseFeature = -> Pocket040
  Intersection = false
  Join = 0
  Mode = 0
  Refine = true
  SupportTransform = false
  Suppressed = false
  Value = 3
FEATURE [Sketcher::SketchObject] Sketch072
  ArcFitTolerance = 1e-06
  AttachmentSupport = -> [Thickness005]
  FullyConstrained = false
  MakeInternals = false
  MapMode = 5
  Placement = pos=(0,-99.8,2.2e-14) rot=(1,0,0;1.5708rad)
  sketch-geometry (15):
    g0: LineSegment [constr] StartX=4.5568 StartY=5.71171 StartZ=0 EndX=7.88662 EndY=7.89278 EndZ=0
    g1: LineSegment StartX=5.46609 StartY=6.3073 StartZ=0 EndX=2.696 EndY=10.5364 EndZ=0
    g2: LineSegment StartX=2.696 StartY=10.5364 StartZ=0 EndX=32.4943 EndY=27.0739 EndZ=0
    g3: LineSegment StartX=32.4943 StartY=27.0739 StartZ=0 EndX=156.488 EndY=39.0363 EndZ=0
    g4: LineSegment StartX=156.488 StartY=39.0363 StartZ=0 EndX=248.898 EndY=26.6449 EndZ=0
    g5: LineSegment StartX=248.898 StartY=26.6449 StartZ=0 EndX=329.144 EndY=7.08029 EndZ=0
    g6: LineSegment StartX=329.144 StartY=7.08029 StartZ=0 EndX=328 EndY=-15.9084 EndZ=0
    g7: LineSegment StartX=328 StartY=-15.9084 StartZ=0 EndX=200.054 EndY=-15.9084 EndZ=0
    g8: LineSegment StartX=200.054 StartY=-15.9084 StartZ=0 EndX=64.7748 EndY=-15.9084 EndZ=0
    g9: LineSegment StartX=64.7748 StartY=-15.9084 StartZ=0 EndX=16.3454 EndY=-20.7039 EndZ=0
    g10: LineSegment StartX=16.3454 StartY=-20.7039 StartZ=0 EndX=2.88885 EndY=-12.2412 EndZ=0
    g11: LineSegment [constr] StartX=2.3291 StartY=-2.35546 StartZ=0 EndX=5.23499 EndY=-3.24958 EndZ=0
    g12: LineSegment StartX=2.88053 StartY=-2.52513 StartZ=0 EndX=1.81302 EndY=-5.99451 EndZ=0
    g13: LineSegment StartX=1.81302 StartY=-5.99451 StartZ=0 EndX=2.88885 EndY=-12.2412 EndZ=0
    g14: LineSegment StartX=5.46609 StartY=6.3073 StartZ=0 EndX=2.88053 EndY=-2.52513 EndZ=0
  constraints (22):
    c: PointOnObject(g1,g0)
    c: Perpendicular(g0,g1)
    c: Block(g1)
    c: Block(g0)
    c: Coincident(g1,g2)
    c: Coincident(g2,g3)
    c: Coincident(g3,g4)
    c: Coincident(g4,g5)
    c: Coincident(g5,g6)
    c: Coincident(g6,g7)
    c: Horizontal(g7)
    c: Coincident(g7,g8)
    c: Horizontal(g8)
    c: Coincident(g8,g9)
    c: Coincident(g9,g10)
    c: Block(g11)
    c: PointOnObject(g12,g11)
    c: Perpendicular(g11,g12)
    c: Coincident(g13,g12)
    c: Coincident(g13,g10)
    c: Coincident(g14,g1)
    c: Coincident(g14,g12)
FEATURE [PartDesign::Pocket] Pocket041
  BaseFeature = -> Thickness005
  Direction = (0,1,-2e-16)
  Length = 1000
  Length2 = 5
  Profile = -> Sketch072
  ReferenceAxis = -> Sketch072 [N_Axis]
  Refine = true
  Suppressed = false
  Type = 0
FEATURE [PartDesign::Body] Body016  label="leading edge 006"
  AllowCompound = false
  Group = -> [Pad029,Sketch071,Pocket040,Thickness005,Sketch072,Pocket041,Sketch073]
  Origin = -> Origin016
  Placement = pos=(0,-403.6,0) rot=(0,0,1;0rad)
  Tip = -> Pocket041
FEATURE [Sketcher::SketchObject] Sketch083
  ArcFitTolerance = 1e-06
  AttachmentSupport = -> [XY_Plane019]
  FullyConstrained = false
  MakeInternals = false
  MapMode = 5
  sketch-geometry (4):
    g0: LineSegment StartX=295 StartY=36.1981 StartZ=0 EndX=295 EndY=-1016.06 EndZ=0
    g1: LineSegment StartX=295 StartY=-1016.06 StartZ=0 EndX=488.335 EndY=-1016.06 EndZ=0
    g2: LineSegment StartX=488.335 StartY=-1016.06 StartZ=0 EndX=488.335 EndY=36.1981 EndZ=0
    g3: LineSegment StartX=488.335 StartY=36.1981 StartZ=0 EndX=295 EndY=36.1981 EndZ=0
  constraints (9):
    c: Coincident(g0,g1)
    c: Coincident(g1,g2)
    c: Coincident(g2,g3)
    c: Coincident(g3,g0)
    c: Vertical(g0)
    c: Vertical(g2)
    c: Horizontal(g1)
    c: Horizontal(g3)
    c: DistanceX(g-1,g0) = 295
FEATURE [Sketcher::SketchObject] Sketch085
  ArcFitTolerance = 1e-06
  FullyConstrained = false
  MakeInternals = false
  Placement = pos=(0,0,0) rot=(1,0,0;1.5708rad)
  sketch-geometry (125):
    g0: BSplineCurve PolesCount=62 KnotsCount=62 Degree=3 IsPeriodic=1
    g1-g62: Circle [constr] x62 (B-spline internal-alignment scaffolding for g0; pole/knot coordinates omitted)
    g63-g124: GeomPoint [constr] x62 (B-spline internal-alignment scaffolding for g0; pole/knot coordinates omitted)
  constraints (125):
    c: InternalAlignment(g1,g0)
    c: Weight(g1) = 1
    c: InternalAlignment(g2,g0)
    c: Equal(g2,g1)
    c: InternalAlignment(g3,g0)
    c: Equal(g3,g1)
    c: InternalAlignment(g4,g0)
    c: Equal(g4,g1)
    c: InternalAlignment(g5,g0)
    c: Equal(g5,g1)
    c: InternalAlignment(g6,g0)
    c: Equal(g6,g1)
    c: InternalAlignment(g7,g0)
    c: Equal(g7,g1)
    c: InternalAlignment(g8,g0)
    c: Equal(g8,g1)
    c: InternalAlignment(g9,g0)
    c: Equal(g9,g1)
    c: InternalAlignment(g10,g0)
    c: Equal(g10,g1)
    c: InternalAlignment(g11,g0)
    c: Equal(g11,g1)
    c: InternalAlignment(g12,g0)
    c: Equal(g12,g1)
    c: InternalAlignment(g13,g0)
    c: Equal(g13,g1)
    c: InternalAlignment(g14,g0)
    c: Equal(g14,g1)
    c: InternalAlignment(g15,g0)
    c: Equal(g15,g1)
    c: InternalAlignment(g16,g0)
    c: Equal(g16,g1)
    c: InternalAlignment(g17,g0)
    c: Equal(g17,g1)
    c: InternalAlignment(g18,g0)
    c: Equal(g18,g1)
    c: InternalAlignment(g19,g0)
    c: Equal(g19,g1)
    c: InternalAlignment(g20,g0)
    c: Equal(g20,g1)
    c: InternalAlignment(g21,g0)
    c: Equal(g21,g1)
    c: InternalAlignment(g22,g0)
    c: Equal(g22,g1)
    c: InternalAlignment(g23,g0)
    c: Equal(g23,g1)
    c: InternalAlignment(g24,g0)
    c: Equal(g24,g1)
    c: InternalAlignment(g25,g0)
    c: Equal(g25,g1)
    c: InternalAlignment(g26,g0)
    c: Equal(g26,g1)
    c: InternalAlignment(g27,g0)
    c: Equal(g27,g1)
    c: InternalAlignment(g28,g0)
    c: Equal(g28,g1)
    c: InternalAlignment(g29,g0)
    c: Equal(g29,g1)
    c: InternalAlignment(g30,g0)
    c: Equal(g30,g1)
    c: InternalAlignment(g31,g0)
    c: Equal(g31,g1)
    c: InternalAlignment(g32,g0)
    c: Equal(g32,g1)
    c: InternalAlignment(g33,g0)
    c: Equal(g33,g1)
    c: InternalAlignment(g34,g0)
    c: Equal(g34,g1)
    c: InternalAlignment(g35,g0)
    c: Equal(g35,g1)
    c: InternalAlignment(g36,g0)
    c: Equal(g36,g1)
    c: InternalAlignment(g37,g0)
    c: Equal(g37,g1)
    c: InternalAlignment(g38,g0)
    c: Equal(g38,g1)
    c: InternalAlignment(g39,g0)
    c: Equal(g39,g1)
    c: InternalAlignment(g40,g0)
    c: Equal(g40,g1)
    c: InternalAlignment(g41,g0)
    c: Equal(g41,g1)
    c: InternalAlignment(g42,g0)
    c: Equal(g42,g1)
    c: InternalAlignment(g43,g0)
    c: Equal(g43,g1)
    c: InternalAlignment(g44,g0)
    c: Equal(g44,g1)
    c: InternalAlignment(g45,g0)
    c: Equal(g45,g1)
    c: InternalAlignment(g46,g0)
    c: Equal(g46,g1)
    c: InternalAlignment(g47,g0)
    c: Equal(g47,g1)
    c: InternalAlignment(g48,g0)
    c: Equal(g48,g1)
    c: InternalAlignment(g49,g0)
    c: Equal(g49,g1)
    c: InternalAlignment(g50,g0)
    c: Equal(g50,g1)
    c: InternalAlignment(g51,g0)
    c: Equal(g51,g1)
    c: InternalAlignment(g52,g0)
    c: Equal(g52,g1)
    c: InternalAlignment(g53,g0)
    c: Equal(g53,g1)
    c: InternalAlignment(g54,g0)
    c: Equal(g54,g1)
    c: InternalAlignment(g55,g0)
    c: Equal(g55,g1)
    c: InternalAlignment(g56,g0)
    c: Equal(g56,g1)
    c: InternalAlignment(g57,g0)
    c: Equal(g57,g1)
    c: InternalAlignment(g58,g0)
    c: Equal(g58,g1)
    c: InternalAlignment(g59,g0)
    c: Equal(g59,g1)
    c: InternalAlignment(g60,g0)
    c: Equal(g60,g1)
    c: InternalAlignment(g61,g0)
    c: Equal(g61,g1)
    c: InternalAlignment(g62,g0)
    c: Equal(g62,g1)
    c: InternalAlignment(g63-g124 -> g0) x62
FEATURE [PartDesign::Pad] Pad034
  Direction = (0,-1,2e-16)
  Length = 99.8
  Length2 = 10
  Placement = pos=(0,0,0) rot=(1,0,0;1.5708rad)
  Profile = -> Sketch085
  ReferenceAxis = -> Sketch085 [N_Axis]
  Refine = true
  Suppressed = false
  Type = 0
FEATURE [PartDesign::Pocket] Pocket047
  BaseFeature = -> Pad034
  Direction = (0,0,-1)
  Length = 100
  Length2 = 5
  Midplane = true
  Placement = pos=(0,0,0) rot=(1,0,0;1.5708rad)
  Profile = -> Sketch083
  ReferenceAxis = -> Sketch083 [N_Axis]
  Refine = true
  Suppressed = false
  Type = 0
FEATURE [PartDesign::Thickness] Thickness006
  Base = -> Pocket047 [Face4,Face2]
  BaseFeature = -> Pocket047
  Intersection = false
  Join = 0
  Mode = 0
  Refine = true
  SupportTransform = false
  Suppressed = false
  Value = 3
FEATURE [Sketcher::SketchObject] Sketch084
  ArcFitTolerance = 1e-06
  AttachmentSupport = -> [Thickness006]
  FullyConstrained = false
  MakeInternals = false
  MapMode = 5
  Placement = pos=(0,-99.8,2.2e-14) rot=(1,0,0;1.5708rad)
  sketch-geometry (15):
    g0: LineSegment [constr] StartX=4.5568 StartY=5.71171 StartZ=0 EndX=7.88662 EndY=7.89278 EndZ=0
    g1: LineSegment StartX=5.46609 StartY=6.3073 StartZ=0 EndX=2.696 EndY=10.5364 EndZ=0
    g2: LineSegment StartX=2.696 StartY=10.5364 StartZ=0 EndX=32.4943 EndY=27.0739 EndZ=0
    g3: LineSegment StartX=32.4943 StartY=27.0739 StartZ=0 EndX=156.488 EndY=39.0363 EndZ=0
    g4: LineSegment StartX=156.488 StartY=39.0363 StartZ=0 EndX=248.898 EndY=26.6449 EndZ=0
    g5: LineSegment StartX=248.898 StartY=26.6449 StartZ=0 EndX=329.144 EndY=7.08029 EndZ=0
    g6: LineSegment StartX=329.144 StartY=7.08029 StartZ=0 EndX=328 EndY=-15.9084 EndZ=0
    g7: LineSegment StartX=328 StartY=-15.9084 StartZ=0 EndX=200.054 EndY=-15.9084 EndZ=0
    g8: LineSegment StartX=200.054 StartY=-15.9084 StartZ=0 EndX=64.7748 EndY=-15.9084 EndZ=0
    g9: LineSegment StartX=64.7748 StartY=-15.9084 StartZ=0 EndX=16.3454 EndY=-20.7039 EndZ=0
    g10: LineSegment StartX=16.3454 StartY=-20.7039 StartZ=0 EndX=2.88885 EndY=-12.2412 EndZ=0
    g11: LineSegment [constr] StartX=2.3291 StartY=-2.35546 StartZ=0 EndX=5.23499 EndY=-3.24958 EndZ=0
    g12: LineSegment StartX=2.88053 StartY=-2.52513 StartZ=0 EndX=1.81302 EndY=-5.99451 EndZ=0
    g13: LineSegment StartX=1.81302 StartY=-5.99451 StartZ=0 EndX=2.88885 EndY=-12.2412 EndZ=0
    g14: LineSegment StartX=5.46609 StartY=6.3073 StartZ=0 EndX=2.88053 EndY=-2.52513 EndZ=0
  constraints (22):
    c: PointOnObject(g1,g0)
    c: Perpendicular(g0,g1)
    c: Block(g1)
    c: Block(g0)
    c: Coincident(g1,g2)
    c: Coincident(g2,g3)
    c: Coincident(g3,g4)
    c: Coincident(g4,g5)
    c: Coincident(g5,g6)
    c: Coincident(g6,g7)
    c: Horizontal(g7)
    c: Coincident(g7,g8)
    c: Horizontal(g8)
    c: Coincident(g8,g9)
    c: Coincident(g9,g10)
    c: Block(g11)
    c: PointOnObject(g12,g11)
    c: Perpendicular(g11,g12)
    c: Coincident(g13,g12)
    c: Coincident(g13,g10)
    c: Coincident(g14,g1)
    c: Coincident(g14,g12)
FEATURE [PartDesign::Pocket] Pocket048
  BaseFeature = -> Thickness006
  Direction = (0,1,-2e-16)
  Length = 1000
  Length2 = 5
  Profile = -> Sketch084
  ReferenceAxis = -> Sketch084 [N_Axis]
  Refine = true
  Suppressed = false
  Type = 0
FEATURE [PartDesign::Body] Body019  label="leading edge 007"
  AllowCompound = false
  Group = -> [Pad034,Sketch083,Pocket047,Thickness006,Sketch084,Pocket048,Sketch085]
  Origin = -> Origin019
  Placement = pos=(0,-503.6,0) rot=(0,0,1;0rad)
  Tip = -> Pocket048
FEATURE [Sketcher::SketchObject] Sketch095
  ArcFitTolerance = 1e-06
  AttachmentSupport = -> [XY_Plane022]
  FullyConstrained = false
  MakeInternals = false
  MapMode = 5
  sketch-geometry (4):
    g0: LineSegment StartX=295 StartY=36.1981 StartZ=0 EndX=295 EndY=-1016.06 EndZ=0
    g1: LineSegment StartX=295 StartY=-1016.06 StartZ=0 EndX=488.335 EndY=-1016.06 EndZ=0
    g2: LineSegment StartX=488.335 StartY=-1016.06 StartZ=0 EndX=488.335 EndY=36.1981 EndZ=0
    g3: LineSegment StartX=488.335 StartY=36.1981 StartZ=0 EndX=295 EndY=36.1981 EndZ=0
  constraints (9):
    c: Coincident(g0,g1)
    c: Coincident(g1,g2)
    c: Coincident(g2,g3)
    c: Coincident(g3,g0)
    c: Vertical(g0)
    c: Vertical(g2)
    c: Horizontal(g1)
    c: Horizontal(g3)
    c: DistanceX(g-1,g0) = 295
FEATURE [Sketcher::SketchObject] Sketch097
  ArcFitTolerance = 1e-06
  FullyConstrained = false
  MakeInternals = false
  Placement = pos=(0,0,0) rot=(1,0,0;1.5708rad)
  sketch-geometry (125):
    g0: BSplineCurve PolesCount=62 KnotsCount=62 Degree=3 IsPeriodic=1
    g1-g62: Circle [constr] x62 (B-spline internal-alignment scaffolding for g0; pole/knot coordinates omitted)
    g63-g124: GeomPoint [constr] x62 (B-spline internal-alignment scaffolding for g0; pole/knot coordinates omitted)
  constraints (125):
    c: InternalAlignment(g1,g0)
    c: Weight(g1) = 1
    c: InternalAlignment(g2,g0)
    c: Equal(g2,g1)
    c: InternalAlignment(g3,g0)
    c: Equal(g3,g1)
    c: InternalAlignment(g4,g0)
    c: Equal(g4,g1)
    c: InternalAlignment(g5,g0)
    c: Equal(g5,g1)
    c: InternalAlignment(g6,g0)
    c: Equal(g6,g1)
    c: InternalAlignment(g7,g0)
    c: Equal(g7,g1)
    c: InternalAlignment(g8,g0)
    c: Equal(g8,g1)
    c: InternalAlignment(g9,g0)
    c: Equal(g9,g1)
    c: InternalAlignment(g10,g0)
    c: Equal(g10,g1)
    c: InternalAlignment(g11,g0)
    c: Equal(g11,g1)
    c: InternalAlignment(g12,g0)
    c: Equal(g12,g1)
    c: InternalAlignment(g13,g0)
    c: Equal(g13,g1)
    c: InternalAlignment(g14,g0)
    c: Equal(g14,g1)
    c: InternalAlignment(g15,g0)
    c: Equal(g15,g1)
    c: InternalAlignment(g16,g0)
    c: Equal(g16,g1)
    c: InternalAlignment(g17,g0)
    c: Equal(g17,g1)
    c: InternalAlignment(g18,g0)
    c: Equal(g18,g1)
    c: InternalAlignment(g19,g0)
    c: Equal(g19,g1)
    c: InternalAlignment(g20,g0)
    c: Equal(g20,g1)
    c: InternalAlignment(g21,g0)
    c: Equal(g21,g1)
    c: InternalAlignment(g22,g0)
    c: Equal(g22,g1)
    c: InternalAlignment(g23,g0)
    c: Equal(g23,g1)
    c: InternalAlignment(g24,g0)
    c: Equal(g24,g1)
    c: InternalAlignment(g25,g0)
    c: Equal(g25,g1)
    c: InternalAlignment(g26,g0)
    c: Equal(g26,g1)
    c: InternalAlignment(g27,g0)
    c: Equal(g27,g1)
    c: InternalAlignment(g28,g0)
    c: Equal(g28,g1)
    c: InternalAlignment(g29,g0)
    c: Equal(g29,g1)
    c: InternalAlignment(g30,g0)
    c: Equal(g30,g1)
    c: InternalAlignment(g31,g0)
    c: Equal(g31,g1)
    c: InternalAlignment(g32,g0)
    c: Equal(g32,g1)
    c: InternalAlignment(g33,g0)
    c: Equal(g33,g1)
    c: InternalAlignment(g34,g0)
    c: Equal(g34,g1)
    c: InternalAlignment(g35,g0)
    c: Equal(g35,g1)
    c: InternalAlignment(g36,g0)
    c: Equal(g36,g1)
    c: InternalAlignment(g37,g0)
    c: Equal(g37,g1)
    c: InternalAlignment(g38,g0)
    c: Equal(g38,g1)
    c: InternalAlignment(g39,g0)
    c: Equal(g39,g1)
    c: InternalAlignment(g40,g0)
    c: Equal(g40,g1)
    c: InternalAlignment(g41,g0)
    c: Equal(g41,g1)
    c: InternalAlignment(g42,g0)
    c: Equal(g42,g1)
    c: InternalAlignment(g43,g0)
    c: Equal(g43,g1)
    c: InternalAlignment(g44,g0)
    c: Equal(g44,g1)
    c: InternalAlignment(g45,g0)
    c: Equal(g45,g1)
    c: InternalAlignment(g46,g0)
    c: Equal(g46,g1)
    c: InternalAlignment(g47,g0)
    c: Equal(g47,g1)
    c: InternalAlignment(g48,g0)
    c: Equal(g48,g1)
    c: InternalAlignment(g49,g0)
    c: Equal(g49,g1)
    c: InternalAlignment(g50,g0)
    c: Equal(g50,g1)
    c: InternalAlignment(g51,g0)
    c: Equal(g51,g1)
    c: InternalAlignment(g52,g0)
    c: Equal(g52,g1)
    c: InternalAlignment(g53,g0)
    c: Equal(g53,g1)
    c: InternalAlignment(g54,g0)
    c: Equal(g54,g1)
    c: InternalAlignment(g55,g0)
    c: Equal(g55,g1)
    c: InternalAlignment(g56,g0)
    c: Equal(g56,g1)
    c: InternalAlignment(g57,g0)
    c: Equal(g57,g1)
    c: InternalAlignment(g58,g0)
    c: Equal(g58,g1)
    c: InternalAlignment(g59,g0)
    c: Equal(g59,g1)
    c: InternalAlignment(g60,g0)
    c: Equal(g60,g1)
    c: InternalAlignment(g61,g0)
    c: Equal(g61,g1)
    c: InternalAlignment(g62,g0)
    c: Equal(g62,g1)
    c: InternalAlignment(g63-g124 -> g0) x62
FEATURE [PartDesign::Pad] Pad039
  Direction = (0,-1,2e-16)
  Length = 99.8
  Length2 = 10
  Placement = pos=(0,0,0) rot=(1,0,0;1.5708rad)
  Profile = -> Sketch097
  ReferenceAxis = -> Sketch097 [N_Axis]
  Refine = true
  Suppressed = false
  Type = 0
FEATURE [PartDesign::Pocket] Pocket054
  BaseFeature = -> Pad039
  Direction = (0,0,-1)
  Length = 100
  Length2 = 5
  Midplane = true
  Placement = pos=(0,0,0) rot=(1,0,0;1.5708rad)
  Profile = -> Sketch095
  ReferenceAxis = -> Sketch095 [N_Axis]
  Refine = true
  Suppressed = false
  Type = 0
FEATURE [PartDesign::Thickness] Thickness007
  Base = -> Pocket054 [Face4,Face2]
  BaseFeature = -> Pocket054
  Intersection = false
  Join = 0
  Mode = 0
  Refine = true
  SupportTransform = false
  Suppressed = false
  Value = 3
FEATURE [Sketcher::SketchObject] Sketch096
  ArcFitTolerance = 1e-06
  AttachmentSupport = -> [Thickness007]
  FullyConstrained = false
  MakeInternals = false
  MapMode = 5
  Placement = pos=(0,-99.8,2.2e-14) rot=(1,0,0;1.5708rad)
  sketch-geometry (15):
    g0: LineSegment [constr] StartX=4.5568 StartY=5.71171 StartZ=0 EndX=7.88662 EndY=7.89278 EndZ=0
    g1: LineSegment StartX=5.46609 StartY=6.3073 StartZ=0 EndX=2.696 EndY=10.5364 EndZ=0
    g2: LineSegment StartX=2.696 StartY=10.5364 StartZ=0 EndX=32.4943 EndY=27.0739 EndZ=0
    g3: LineSegment StartX=32.4943 StartY=27.0739 StartZ=0 EndX=156.488 EndY=39.0363 EndZ=0
    g4: LineSegment StartX=156.488 StartY=39.0363 StartZ=0 EndX=248.898 EndY=26.6449 EndZ=0
    g5: LineSegment StartX=248.898 StartY=26.6449 StartZ=0 EndX=329.144 EndY=7.08029 EndZ=0
    g6: LineSegment StartX=329.144 StartY=7.08029 StartZ=0 EndX=328 EndY=-15.9084 EndZ=0
    g7: LineSegment StartX=328 StartY=-15.9084 StartZ=0 EndX=200.054 EndY=-15.9084 EndZ=0
    g8: LineSegment StartX=200.054 StartY=-15.9084 StartZ=0 EndX=64.7748 EndY=-15.9084 EndZ=0
    g9: LineSegment StartX=64.7748 StartY=-15.9084 StartZ=0 EndX=16.3454 EndY=-20.7039 EndZ=0
    g10: LineSegment StartX=16.3454 StartY=-20.7039 StartZ=0 EndX=2.88885 EndY=-12.2412 EndZ=0
    g11: LineSegment [constr] StartX=2.3291 StartY=-2.35546 StartZ=0 EndX=5.23499 EndY=-3.24958 EndZ=0
    g12: LineSegment StartX=2.88053 StartY=-2.52513 StartZ=0 EndX=1.81302 EndY=-5.99451 EndZ=0
    g13: LineSegment StartX=1.81302 StartY=-5.99451 StartZ=0 EndX=2.88885 EndY=-12.2412 EndZ=0
    g14: LineSegment StartX=5.46609 StartY=6.3073 StartZ=0 EndX=2.88053 EndY=-2.52513 EndZ=0
  constraints (22):
    c: PointOnObject(g1,g0)
    c: Perpendicular(g0,g1)
    c: Block(g1)
    c: Block(g0)
    c: Coincident(g1,g2)
    c: Coincident(g2,g3)
    c: Coincident(g3,g4)
    c: Coincident(g4,g5)
    c: Coincident(g5,g6)
    c: Coincident(g6,g7)
    c: Horizontal(g7)
    c: Coincident(g7,g8)
    c: Horizontal(g8)
    c: Coincident(g8,g9)
    c: Coincident(g9,g10)
    c: Block(g11)
    c: PointOnObject(g12,g11)
    c: Perpendicular(g11,g12)
    c: Coincident(g13,g12)
    c: Coincident(g13,g10)
    c: Coincident(g14,g1)
    c: Coincident(g14,g12)
FEATURE [PartDesign::Pocket] Pocket055
  BaseFeature = -> Thickness007
  Direction = (0,1,-2e-16)
  Length = 1000
  Length2 = 5
  Profile = -> Sketch096
  ReferenceAxis = -> Sketch096 [N_Axis]
  Refine = true
  Suppressed = false
  Type = 0
FEATURE [PartDesign::Body] Body022  label="leading edge 008"
  AllowCompound = false
  Group = -> [Pad039,Sketch095,Pocket054,Thickness007,Sketch096,Pocket055,Sketch097]
  Origin = -> Origin022
  Placement = pos=(0,-603.6,0) rot=(0,0,1;0rad)
  Tip = -> Pocket055
FEATURE [Sketcher::SketchObject] Sketch107
  ArcFitTolerance = 1e-06
  AttachmentSupport = -> [XY_Plane025]
  FullyConstrained = false
  MakeInternals = false
  MapMode = 5
  sketch-geometry (4):
    g0: LineSegment StartX=295 StartY=36.1981 StartZ=0 EndX=295 EndY=-1016.06 EndZ=0
    g1: LineSegment StartX=295 StartY=-1016.06 StartZ=0 EndX=488.335 EndY=-1016.06 EndZ=0
    g2: LineSegment StartX=488.335 StartY=-1016.06 StartZ=0 EndX=488.335 EndY=36.1981 EndZ=0
    g3: LineSegment StartX=488.335 StartY=36.1981 StartZ=0 EndX=295 EndY=36.1981 EndZ=0
  constraints (9):
    c: Coincident(g0,g1)
    c: Coincident(g1,g2)
    c: Coincident(g2,g3)
    c: Coincident(g3,g0)
    c: Vertical(g0)
    c: Vertical(g2)
    c: Horizontal(g1)
    c: Horizontal(g3)
    c: DistanceX(g-1,g0) = 295
FEATURE [Sketcher::SketchObject] Sketch109
  ArcFitTolerance = 1e-06
  FullyConstrained = false
  MakeInternals = false
  Placement = pos=(0,0,0) rot=(1,0,0;1.5708rad)
  sketch-geometry (125):
    g0: BSplineCurve PolesCount=62 KnotsCount=62 Degree=3 IsPeriodic=1
    g1-g62: Circle [constr] x62 (B-spline internal-alignment scaffolding for g0; pole/knot coordinates omitted)
    g63-g124: GeomPoint [constr] x62 (B-spline internal-alignment scaffolding for g0; pole/knot coordinates omitted)
  constraints (125):
    c: InternalAlignment(g1,g0)
    c: Weight(g1) = 1
    c: InternalAlignment(g2,g0)
    c: Equal(g2,g1)
    c: InternalAlignment(g3,g0)
    c: Equal(g3,g1)
    c: InternalAlignment(g4,g0)
    c: Equal(g4,g1)
    c: InternalAlignment(g5,g0)
    c: Equal(g5,g1)
    c: InternalAlignment(g6,g0)
    c: Equal(g6,g1)
    c: InternalAlignment(g7,g0)
    c: Equal(g7,g1)
    c: InternalAlignment(g8,g0)
    c: Equal(g8,g1)
    c: InternalAlignment(g9,g0)
    c: Equal(g9,g1)
    c: InternalAlignment(g10,g0)
    c: Equal(g10,g1)
    c: InternalAlignment(g11,g0)
    c: Equal(g11,g1)
    c: InternalAlignment(g12,g0)
    c: Equal(g12,g1)
    c: InternalAlignment(g13,g0)
    c: Equal(g13,g1)
    c: InternalAlignment(g14,g0)
    c: Equal(g14,g1)
    c: InternalAlignment(g15,g0)
    c: Equal(g15,g1)
    c: InternalAlignment(g16,g0)
    c: Equal(g16,g1)
    c: InternalAlignment(g17,g0)
    c: Equal(g17,g1)
    c: InternalAlignment(g18,g0)
    c: Equal(g18,g1)
    c: InternalAlignment(g19,g0)
    c: Equal(g19,g1)
    c: InternalAlignment(g20,g0)
    c: Equal(g20,g1)
    c: InternalAlignment(g21,g0)
    c: Equal(g21,g1)
    c: InternalAlignment(g22,g0)
    c: Equal(g22,g1)
    c: InternalAlignment(g23,g0)
    c: Equal(g23,g1)
    c: InternalAlignment(g24,g0)
    c: Equal(g24,g1)
    c: InternalAlignment(g25,g0)
    c: Equal(g25,g1)
    c: InternalAlignment(g26,g0)
    c: Equal(g26,g1)
    c: InternalAlignment(g27,g0)
    c: Equal(g27,g1)
    c: InternalAlignment(g28,g0)
    c: Equal(g28,g1)
    c: InternalAlignment(g29,g0)
    c: Equal(g29,g1)
    c: InternalAlignment(g30,g0)
    c: Equal(g30,g1)
    c: InternalAlignment(g31,g0)
    c: Equal(g31,g1)
    c: InternalAlignment(g32,g0)
    c: Equal(g32,g1)
    c: InternalAlignment(g33,g0)
    c: Equal(g33,g1)
    c: InternalAlignment(g34,g0)
    c: Equal(g34,g1)
    c: InternalAlignment(g35,g0)
    c: Equal(g35,g1)
    c: InternalAlignment(g36,g0)
    c: Equal(g36,g1)
    c: InternalAlignment(g37,g0)
    c: Equal(g37,g1)
    c: InternalAlignment(g38,g0)
    c: Equal(g38,g1)
    c: InternalAlignment(g39,g0)
    c: Equal(g39,g1)
    c: InternalAlignment(g40,g0)
    c: Equal(g40,g1)
    c: InternalAlignment(g41,g0)
    c: Equal(g41,g1)
    c: InternalAlignment(g42,g0)
    c: Equal(g42,g1)
    c: InternalAlignment(g43,g0)
    c: Equal(g43,g1)
    c: InternalAlignment(g44,g0)
    c: Equal(g44,g1)
    c: InternalAlignment(g45,g0)
    c: Equal(g45,g1)
    c: InternalAlignment(g46,g0)
    c: Equal(g46,g1)
    c: InternalAlignment(g47,g0)
    c: Equal(g47,g1)
    c: InternalAlignment(g48,g0)
    c: Equal(g48,g1)
    c: InternalAlignment(g49,g0)
    c: Equal(g49,g1)
    c: InternalAlignment(g50,g0)
    c: Equal(g50,g1)
    c: InternalAlignment(g51,g0)
    c: Equal(g51,g1)
    c: InternalAlignment(g52,g0)
    c: Equal(g52,g1)
    c: InternalAlignment(g53,g0)
    c: Equal(g53,g1)
    c: InternalAlignment(g54,g0)
    c: Equal(g54,g1)
    c: InternalAlignment(g55,g0)
    c: Equal(g55,g1)
    c: InternalAlignment(g56,g0)
    c: Equal(g56,g1)
    c: InternalAlignment(g57,g0)
    c: Equal(g57,g1)
    c: InternalAlignment(g58,g0)
    c: Equal(g58,g1)
    c: InternalAlignment(g59,g0)
    c: Equal(g59,g1)
    c: InternalAlignment(g60,g0)
    c: Equal(g60,g1)
    c: InternalAlignment(g61,g0)
    c: Equal(g61,g1)
    c: InternalAlignment(g62,g0)
    c: Equal(g62,g1)
    c: InternalAlignment(g63-g124 -> g0) x62
FEATURE [PartDesign::Pad] Pad044
  Direction = (0,-1,2e-16)
  Length = 99.8
  Length2 = 10
  Placement = pos=(0,0,0) rot=(1,0,0;1.5708rad)
  Profile = -> Sketch109
  ReferenceAxis = -> Sketch109 [N_Axis]
  Refine = true
  Suppressed = false
  Type = 0
FEATURE [PartDesign::Pocket] Pocket061
  BaseFeature = -> Pad044
  Direction = (0,0,-1)
  Length = 100
  Length2 = 5
  Midplane = true
  Placement = pos=(0,0,0) rot=(1,0,0;1.5708rad)
  Profile = -> Sketch107
  ReferenceAxis = -> Sketch107 [N_Axis]
  Refine = true
  Suppressed = false
  Type = 0
FEATURE [PartDesign::Thickness] Thickness008
  Base = -> Pocket061 [Face4,Face2]
  BaseFeature = -> Pocket061
  Intersection = false
  Join = 0
  Mode = 0
  Refine = true
  SupportTransform = false
  Suppressed = false
  Value = 3
FEATURE [Sketcher::SketchObject] Sketch108
  ArcFitTolerance = 1e-06
  AttachmentSupport = -> [Thickness008]
  FullyConstrained = false
  MakeInternals = false
  MapMode = 5
  Placement = pos=(0,-99.8,2.2e-14) rot=(1,0,0;1.5708rad)
  sketch-geometry (15):
    g0: LineSegment [constr] StartX=4.5568 StartY=5.71171 StartZ=0 EndX=7.88662 EndY=7.89278 EndZ=0
    g1: LineSegment StartX=5.46609 StartY=6.3073 StartZ=0 EndX=2.696 EndY=10.5364 EndZ=0
    g2: LineSegment StartX=2.696 StartY=10.5364 StartZ=0 EndX=32.4943 EndY=27.0739 EndZ=0
    g3: LineSegment StartX=32.4943 StartY=27.0739 StartZ=0 EndX=156.488 EndY=39.0363 EndZ=0
    g4: LineSegment StartX=156.488 StartY=39.0363 StartZ=0 EndX=248.898 EndY=26.6449 EndZ=0
    g5: LineSegment StartX=248.898 StartY=26.6449 StartZ=0 EndX=329.144 EndY=7.08029 EndZ=0
    g6: LineSegment StartX=329.144 StartY=7.08029 StartZ=0 EndX=328 EndY=-15.9084 EndZ=0
    g7: LineSegment StartX=328 StartY=-15.9084 StartZ=0 EndX=200.054 EndY=-15.9084 EndZ=0
    g8: LineSegment StartX=200.054 StartY=-15.9084 StartZ=0 EndX=64.7748 EndY=-15.9084 EndZ=0
    g9: LineSegment StartX=64.7748 StartY=-15.9084 StartZ=0 EndX=16.3454 EndY=-20.7039 EndZ=0
    g10: LineSegment StartX=16.3454 StartY=-20.7039 StartZ=0 EndX=2.88885 EndY=-12.2412 EndZ=0
    g11: LineSegment [constr] StartX=2.3291 StartY=-2.35546 StartZ=0 EndX=5.23499 EndY=-3.24958 EndZ=0
    g12: LineSegment StartX=2.88053 StartY=-2.52513 StartZ=0 EndX=1.81302 EndY=-5.99451 EndZ=0
    g13: LineSegment StartX=1.81302 StartY=-5.99451 StartZ=0 EndX=2.88885 EndY=-12.2412 EndZ=0
    g14: LineSegment StartX=5.46609 StartY=6.3073 StartZ=0 EndX=2.88053 EndY=-2.52513 EndZ=0
  constraints (22):
    c: PointOnObject(g1,g0)
    c: Perpendicular(g0,g1)
    c: Block(g1)
    c: Block(g0)
    c: Coincident(g1,g2)
    c: Coincident(g2,g3)
    c: Coincident(g3,g4)
    c: Coincident(g4,g5)
    c: Coincident(g5,g6)
    c: Coincident(g6,g7)
    c: Horizontal(g7)
    c: Coincident(g7,g8)
    c: Horizontal(g8)
    c: Coincident(g8,g9)
    c: Coincident(g9,g10)
    c: Block(g11)
    c: PointOnObject(g12,g11)
    c: Perpendicular(g11,g12)
    c: Coincident(g13,g12)
    c: Coincident(g13,g10)
    c: Coincident(g14,g1)
    c: Coincident(g14,g12)
FEATURE [PartDesign::Pocket] Pocket062
  BaseFeature = -> Thickness008
  Direction = (0,1,-2e-16)
  Length = 1000
  Length2 = 5
  Profile = -> Sketch108
  ReferenceAxis = -> Sketch108 [N_Axis]
  Refine = true
  Suppressed = false
  Type = 0
FEATURE [PartDesign::Body] Body025  label="leading edge 009"
  AllowCompound = false
  Group = -> [Pad044,Sketch107,Pocket061,Thickness008,Sketch108,Pocket062,Sketch109]
  Origin = -> Origin025
  Placement = pos=(0,-703.6,0) rot=(0,0,1;0rad)
  Tip = -> Pocket062
FEATURE [Sketcher::SketchObject] Sketch119
  ArcFitTolerance = 1e-06
  AttachmentSupport = -> [XY_Plane028]
  FullyConstrained = false
  MakeInternals = false
  MapMode = 5
  sketch-geometry (4):
    g0: LineSegment StartX=295 StartY=36.1981 StartZ=0 EndX=295 EndY=-1016.06 EndZ=0
    g1: LineSegment StartX=295 StartY=-1016.06 StartZ=0 EndX=488.335 EndY=-1016.06 EndZ=0
    g2: LineSegment StartX=488.335 StartY=-1016.06 StartZ=0 EndX=488.335 EndY=36.1981 EndZ=0
    g3: LineSegment StartX=488.335 StartY=36.1981 StartZ=0 EndX=295 EndY=36.1981 EndZ=0
  constraints (9):
    c: Coincident(g0,g1)
    c: Coincident(g1,g2)
    c: Coincident(g2,g3)
    c: Coincident(g3,g0)
    c: Vertical(g0)
    c: Vertical(g2)
    c: Horizontal(g1)
    c: Horizontal(g3)
    c: DistanceX(g-1,g0) = 295
FEATURE [Sketcher::SketchObject] Sketch121
  ArcFitTolerance = 1e-06
  FullyConstrained = false
  MakeInternals = false
  Placement = pos=(0,0,0) rot=(1,0,0;1.5708rad)
  sketch-geometry (125):
    g0: BSplineCurve PolesCount=62 KnotsCount=62 Degree=3 IsPeriodic=1
    g1-g62: Circle [constr] x62 (B-spline internal-alignment scaffolding for g0; pole/knot coordinates omitted)
    g63-g124: GeomPoint [constr] x62 (B-spline internal-alignment scaffolding for g0; pole/knot coordinates omitted)
  constraints (125):
    c: InternalAlignment(g1,g0)
    c: Weight(g1) = 1
    c: InternalAlignment(g2,g0)
    c: Equal(g2,g1)
    c: InternalAlignment(g3,g0)
    c: Equal(g3,g1)
    c: InternalAlignment(g4,g0)
    c: Equal(g4,g1)
    c: InternalAlignment(g5,g0)
    c: Equal(g5,g1)
    c: InternalAlignment(g6,g0)
    c: Equal(g6,g1)
    c: InternalAlignment(g7,g0)
    c: Equal(g7,g1)
    c: InternalAlignment(g8,g0)
    c: Equal(g8,g1)
    c: InternalAlignment(g9,g0)
    c: Equal(g9,g1)
    c: InternalAlignment(g10,g0)
    c: Equal(g10,g1)
    c: InternalAlignment(g11,g0)
    c: Equal(g11,g1)
    c: InternalAlignment(g12,g0)
    c: Equal(g12,g1)
    c: InternalAlignment(g13,g0)
    c: Equal(g13,g1)
    c: InternalAlignment(g14,g0)
    c: Equal(g14,g1)
    c: InternalAlignment(g15,g0)
    c: Equal(g15,g1)
    c: InternalAlignment(g16,g0)
    c: Equal(g16,g1)
    c: InternalAlignment(g17,g0)
    c: Equal(g17,g1)
    c: InternalAlignment(g18,g0)
    c: Equal(g18,g1)
    c: InternalAlignment(g19,g0)
    c: Equal(g19,g1)
    c: InternalAlignment(g20,g0)
    c: Equal(g20,g1)
    c: InternalAlignment(g21,g0)
    c: Equal(g21,g1)
    c: InternalAlignment(g22,g0)
    c: Equal(g22,g1)
    c: InternalAlignment(g23,g0)
    c: Equal(g23,g1)
    c: InternalAlignment(g24,g0)
    c: Equal(g24,g1)
    c: InternalAlignment(g25,g0)
    c: Equal(g25,g1)
    c: InternalAlignment(g26,g0)
    c: Equal(g26,g1)
    c: InternalAlignment(g27,g0)
    c: Equal(g27,g1)
    c: InternalAlignment(g28,g0)
    c: Equal(g28,g1)
    c: InternalAlignment(g29,g0)
    c: Equal(g29,g1)
    c: InternalAlignment(g30,g0)
    c: Equal(g30,g1)
    c: InternalAlignment(g31,g0)
    c: Equal(g31,g1)
    c: InternalAlignment(g32,g0)
    c: Equal(g32,g1)
    c: InternalAlignment(g33,g0)
    c: Equal(g33,g1)
    c: InternalAlignment(g34,g0)
    c: Equal(g34,g1)
    c: InternalAlignment(g35,g0)
    c: Equal(g35,g1)
    c: InternalAlignment(g36,g0)
    c: Equal(g36,g1)
    c: InternalAlignment(g37,g0)
    c: Equal(g37,g1)
    c: InternalAlignment(g38,g0)
    c: Equal(g38,g1)
    c: InternalAlignment(g39,g0)
    c: Equal(g39,g1)
    c: InternalAlignment(g40,g0)
    c: Equal(g40,g1)
    c: InternalAlignment(g41,g0)
    c: Equal(g41,g1)
    c: InternalAlignment(g42,g0)
    c: Equal(g42,g1)
    c: InternalAlignment(g43,g0)
    c: Equal(g43,g1)
    c: InternalAlignment(g44,g0)
    c: Equal(g44,g1)
    c: InternalAlignment(g45,g0)
    c: Equal(g45,g1)
    c: InternalAlignment(g46,g0)
    c: Equal(g46,g1)
    c: InternalAlignment(g47,g0)
    c: Equal(g47,g1)
    c: InternalAlignment(g48,g0)
    c: Equal(g48,g1)
    c: InternalAlignment(g49,g0)
    c: Equal(g49,g1)
    c: InternalAlignment(g50,g0)
    c: Equal(g50,g1)
    c: InternalAlignment(g51,g0)
    c: Equal(g51,g1)
    c: InternalAlignment(g52,g0)
    c: Equal(g52,g1)
    c: InternalAlignment(g53,g0)
    c: Equal(g53,g1)
    c: InternalAlignment(g54,g0)
    c: Equal(g54,g1)
    c: InternalAlignment(g55,g0)
    c: Equal(g55,g1)
    c: InternalAlignment(g56,g0)
    c: Equal(g56,g1)
    c: InternalAlignment(g57,g0)
    c: Equal(g57,g1)
    c: InternalAlignment(g58,g0)
    c: Equal(g58,g1)
    c: InternalAlignment(g59,g0)
    c: Equal(g59,g1)
    c: InternalAlignment(g60,g0)
    c: Equal(g60,g1)
    c: InternalAlignment(g61,g0)
    c: Equal(g61,g1)
    c: InternalAlignment(g62,g0)
    c: Equal(g62,g1)
    c: InternalAlignment(g63-g124 -> g0) x62
FEATURE [PartDesign::Pad] Pad049
  Direction = (0,-1,2e-16)
  Length = 99.8
  Length2 = 10
  Placement = pos=(0,0,0) rot=(1,0,0;1.5708rad)
  Profile = -> Sketch121
  ReferenceAxis = -> Sketch121 [N_Axis]
  Refine = true
  Suppressed = false
  Type = 0
FEATURE [PartDesign::Pocket] Pocket068
  BaseFeature = -> Pad049
  Direction = (0,0,-1)
  Length = 100
  Length2 = 5
  Midplane = true
  Placement = pos=(0,0,0) rot=(1,0,0;1.5708rad)
  Profile = -> Sketch119
  ReferenceAxis = -> Sketch119 [N_Axis]
  Refine = true
  Suppressed = false
  Type = 0
FEATURE [PartDesign::Thickness] Thickness009
  Base = -> Pocket068 [Face4,Face2]
  BaseFeature = -> Pocket068
  Intersection = false
  Join = 0
  Mode = 0
  Refine = true
  SupportTransform = false
  Suppressed = false
  Value = 3
FEATURE [Sketcher::SketchObject] Sketch120
  ArcFitTolerance = 1e-06
  AttachmentSupport = -> [Thickness009]
  FullyConstrained = false
  MakeInternals = false
  MapMode = 5
  Placement = pos=(0,-99.8,2.2e-14) rot=(1,0,0;1.5708rad)
  sketch-geometry (15):
    g0: LineSegment [constr] StartX=4.5568 StartY=5.71171 StartZ=0 EndX=7.88662 EndY=7.89278 EndZ=0
    g1: LineSegment StartX=5.46609 StartY=6.3073 StartZ=0 EndX=2.696 EndY=10.5364 EndZ=0
    g2: LineSegment StartX=2.696 StartY=10.5364 StartZ=0 EndX=32.4943 EndY=27.0739 EndZ=0
    g3: LineSegment StartX=32.4943 StartY=27.0739 StartZ=0 EndX=156.488 EndY=39.0363 EndZ=0
    g4: LineSegment StartX=156.488 StartY=39.0363 StartZ=0 EndX=248.898 EndY=26.6449 EndZ=0
    g5: LineSegment StartX=248.898 StartY=26.6449 StartZ=0 EndX=329.144 EndY=7.08029 EndZ=0
    g6: LineSegment StartX=329.144 StartY=7.08029 StartZ=0 EndX=328 EndY=-15.9084 EndZ=0
    g7: LineSegment StartX=328 StartY=-15.9084 StartZ=0 EndX=200.054 EndY=-15.9084 EndZ=0
    g8: LineSegment StartX=200.054 StartY=-15.9084 StartZ=0 EndX=64.7748 EndY=-15.9084 EndZ=0
    g9: LineSegment StartX=64.7748 StartY=-15.9084 StartZ=0 EndX=16.3454 EndY=-20.7039 EndZ=0
    g10: LineSegment StartX=16.3454 StartY=-20.7039 StartZ=0 EndX=2.88885 EndY=-12.2412 EndZ=0
    g11: LineSegment [constr] StartX=2.3291 StartY=-2.35546 StartZ=0 EndX=5.23499 EndY=-3.24958 EndZ=0
    g12: LineSegment StartX=2.88053 StartY=-2.52513 StartZ=0 EndX=1.81302 EndY=-5.99451 EndZ=0
    g13: LineSegment StartX=1.81302 StartY=-5.99451 StartZ=0 EndX=2.88885 EndY=-12.2412 EndZ=0
    g14: LineSegment StartX=5.46609 StartY=6.3073 StartZ=0 EndX=2.88053 EndY=-2.52513 EndZ=0
  constraints (22):
    c: PointOnObject(g1,g0)
    c: Perpendicular(g0,g1)
    c: Block(g1)
    c: Block(g0)
    c: Coincident(g1,g2)
    c: Coincident(g2,g3)
    c: Coincident(g3,g4)
    c: Coincident(g4,g5)
    c: Coincident(g5,g6)
    c: Coincident(g6,g7)
    c: Horizontal(g7)
    c: Coincident(g7,g8)
    c: Horizontal(g8)
    c: Coincident(g8,g9)
    c: Coincident(g9,g10)
    c: Block(g11)
    c: PointOnObject(g12,g11)
    c: Perpendicular(g11,g12)
    c: Coincident(g13,g12)
    c: Coincident(g13,g10)
    c: Coincident(g14,g1)
    c: Coincident(g14,g12)
FEATURE [PartDesign::Pocket] Pocket069
  BaseFeature = -> Thickness009
  Direction = (0,1,-2e-16)
  Length = 1000
  Length2 = 5
  Profile = -> Sketch120
  ReferenceAxis = -> Sketch120 [N_Axis]
  Refine = true
  Suppressed = false
  Type = 0
FEATURE [PartDesign::Body] Body028  label="leading edge 010"
  AllowCompound = false
  Group = -> [Pad049,Sketch119,Pocket068,Thickness009,Sketch120,Pocket069,Sketch121]
  Origin = -> Origin028
  Placement = pos=(0,-803.6,0) rot=(0,0,1;0rad)
  Tip = -> Pocket069
FEATURE [Sketcher::SketchObject] Sketch131
  ArcFitTolerance = 1e-06
  AttachmentSupport = -> [XY_Plane031]
  FullyConstrained = false
  MakeInternals = false
  MapMode = 5
  sketch-geometry (4):
    g0: LineSegment StartX=295 StartY=36.1981 StartZ=0 EndX=295 EndY=-1016.06 EndZ=0
    g1: LineSegment StartX=295 StartY=-1016.06 StartZ=0 EndX=488.335 EndY=-1016.06 EndZ=0
    g2: LineSegment StartX=488.335 StartY=-1016.06 StartZ=0 EndX=488.335 EndY=36.1981 EndZ=0
    g3: LineSegment StartX=488.335 StartY=36.1981 StartZ=0 EndX=295 EndY=36.1981 EndZ=0
  constraints (9):
    c: Coincident(g0,g1)
    c: Coincident(g1,g2)
    c: Coincident(g2,g3)
    c: Coincident(g3,g0)
    c: Vertical(g0)
    c: Vertical(g2)
    c: Horizontal(g1)
    c: Horizontal(g3)
    c: DistanceX(g-1,g0) = 295
FEATURE [Sketcher::SketchObject] Sketch133
  ArcFitTolerance = 1e-06
  FullyConstrained = false
  MakeInternals = false
  Placement = pos=(0,0,0) rot=(1,0,0;1.5708rad)
  sketch-geometry (125):
    g0: BSplineCurve PolesCount=62 KnotsCount=62 Degree=3 IsPeriodic=1
    g1-g62: Circle [constr] x62 (B-spline internal-alignment scaffolding for g0; pole/knot coordinates omitted)
    g63-g124: GeomPoint [constr] x62 (B-spline internal-alignment scaffolding for g0; pole/knot coordinates omitted)
  constraints (125):
    c: InternalAlignment(g1,g0)
    c: Weight(g1) = 1
    c: InternalAlignment(g2,g0)
    c: Equal(g2,g1)
    c: InternalAlignment(g3,g0)
    c: Equal(g3,g1)
    c: InternalAlignment(g4,g0)
    c: Equal(g4,g1)
    c: InternalAlignment(g5,g0)
    c: Equal(g5,g1)
    c: InternalAlignment(g6,g0)
    c: Equal(g6,g1)
    c: InternalAlignment(g7,g0)
    c: Equal(g7,g1)
    c: InternalAlignment(g8,g0)
    c: Equal(g8,g1)
    c: InternalAlignment(g9,g0)
    c: Equal(g9,g1)
    c: InternalAlignment(g10,g0)
    c: Equal(g10,g1)
    c: InternalAlignment(g11,g0)
    c: Equal(g11,g1)
    c: InternalAlignment(g12,g0)
    c: Equal(g12,g1)
    c: InternalAlignment(g13,g0)
    c: Equal(g13,g1)
    c: InternalAlignment(g14,g0)
    c: Equal(g14,g1)
    c: InternalAlignment(g15,g0)
    c: Equal(g15,g1)
    c: InternalAlignment(g16,g0)
    c: Equal(g16,g1)
    c: InternalAlignment(g17,g0)
    c: Equal(g17,g1)
    c: InternalAlignment(g18,g0)
    c: Equal(g18,g1)
    c: InternalAlignment(g19,g0)
    c: Equal(g19,g1)
    c: InternalAlignment(g20,g0)
    c: Equal(g20,g1)
    c: InternalAlignment(g21,g0)
    c: Equal(g21,g1)
    c: InternalAlignment(g22,g0)
    c: Equal(g22,g1)
    c: InternalAlignment(g23,g0)
    c: Equal(g23,g1)
    c: InternalAlignment(g24,g0)
    c: Equal(g24,g1)
    c: InternalAlignment(g25,g0)
    c: Equal(g25,g1)
    c: InternalAlignment(g26,g0)
    c: Equal(g26,g1)
    c: InternalAlignment(g27,g0)
    c: Equal(g27,g1)
    c: InternalAlignment(g28,g0)
    c: Equal(g28,g1)
    c: InternalAlignment(g29,g0)
    c: Equal(g29,g1)
    c: InternalAlignment(g30,g0)
    c: Equal(g30,g1)
    c: InternalAlignment(g31,g0)
    c: Equal(g31,g1)
    c: InternalAlignment(g32,g0)
    c: Equal(g32,g1)
    c: InternalAlignment(g33,g0)
    c: Equal(g33,g1)
    c: InternalAlignment(g34,g0)
    c: Equal(g34,g1)
    c: InternalAlignment(g35,g0)
    c: Equal(g35,g1)
    c: InternalAlignment(g36,g0)
    c: Equal(g36,g1)
    c: InternalAlignment(g37,g0)
    c: Equal(g37,g1)
    c: InternalAlignment(g38,g0)
    c: Equal(g38,g1)
    c: InternalAlignment(g39,g0)
    c: Equal(g39,g1)
    c: InternalAlignment(g40,g0)
    c: Equal(g40,g1)
    c: InternalAlignment(g41,g0)
    c: Equal(g41,g1)
    c: InternalAlignment(g42,g0)
    c: Equal(g42,g1)
    c: InternalAlignment(g43,g0)
    c: Equal(g43,g1)
    c: InternalAlignment(g44,g0)
    c: Equal(g44,g1)
    c: InternalAlignment(g45,g0)
    c: Equal(g45,g1)
    c: InternalAlignment(g46,g0)
    c: Equal(g46,g1)
    c: InternalAlignment(g47,g0)
    c: Equal(g47,g1)
    c: InternalAlignment(g48,g0)
    c: Equal(g48,g1)
    c: InternalAlignment(g49,g0)
    c: Equal(g49,g1)
    c: InternalAlignment(g50,g0)
    c: Equal(g50,g1)
    c: InternalAlignment(g51,g0)
    c: Equal(g51,g1)
    c: InternalAlignment(g52,g0)
    c: Equal(g52,g1)
    c: InternalAlignment(g53,g0)
    c: Equal(g53,g1)
    c: InternalAlignment(g54,g0)
    c: Equal(g54,g1)
    c: InternalAlignment(g55,g0)
    c: Equal(g55,g1)
    c: InternalAlignment(g56,g0)
    c: Equal(g56,g1)
    c: InternalAlignment(g57,g0)
    c: Equal(g57,g1)
    c: InternalAlignment(g58,g0)
    c: Equal(g58,g1)
    c: InternalAlignment(g59,g0)
    c: Equal(g59,g1)
    c: InternalAlignment(g60,g0)
    c: Equal(g60,g1)
    c: InternalAlignment(g61,g0)
    c: Equal(g61,g1)
    c: InternalAlignment(g62,g0)
    c: Equal(g62,g1)
    c: InternalAlignment(g63-g124 -> g0) x62
FEATURE [PartDesign::Pad] Pad054
  Direction = (0,-1,2e-16)
  Length = 71.4
  Length2 = 10
  Placement = pos=(0,0,0) rot=(1,0,0;1.5708rad)
  Profile = -> Sketch133
  ReferenceAxis = -> Sketch133 [N_Axis]
  Refine = true
  Suppressed = false
  Type = 0
FEATURE [PartDesign::Pocket] Pocket075
  BaseFeature = -> Pad054
  Direction = (0,0,-1)
  Length = 100
  Length2 = 5
  Midplane = true
  Placement = pos=(0,0,0) rot=(1,0,0;1.5708rad)
  Profile = -> Sketch131
  ReferenceAxis = -> Sketch131 [N_Axis]
  Refine = true
  Suppressed = false
  Type = 0
FEATURE [PartDesign::Thickness] Thickness010
  Base = -> Pocket075 [Face4,Face2]
  BaseFeature = -> Pocket075
  Intersection = false
  Join = 0
  Mode = 0
  Refine = true
  SupportTransform = false
  Suppressed = false
  Value = 3
FEATURE [Sketcher::SketchObject] Sketch132
  ArcFitTolerance = 1e-06
  AttachmentSupport = -> [Thickness010]
  FullyConstrained = false
  MakeInternals = false
  MapMode = 5
  Placement = pos=(0,-71.4,1.57e-14) rot=(1,0,0;1.5708rad)
  sketch-geometry (15):
    g0: LineSegment [constr] StartX=4.5568 StartY=5.71171 StartZ=0 EndX=7.88662 EndY=7.89278 EndZ=0
    g1: LineSegment StartX=5.46609 StartY=6.3073 StartZ=0 EndX=2.696 EndY=10.5364 EndZ=0
    g2: LineSegment StartX=2.696 StartY=10.5364 StartZ=0 EndX=32.4943 EndY=27.0739 EndZ=0
    g3: LineSegment StartX=32.4943 StartY=27.0739 StartZ=0 EndX=156.488 EndY=39.0363 EndZ=0
    g4: LineSegment StartX=156.488 StartY=39.0363 StartZ=0 EndX=248.898 EndY=26.6449 EndZ=0
    g5: LineSegment StartX=248.898 StartY=26.6449 StartZ=0 EndX=329.144 EndY=7.08029 EndZ=0
    g6: LineSegment StartX=329.144 StartY=7.08029 StartZ=0 EndX=328 EndY=-15.9084 EndZ=0
    g7: LineSegment StartX=328 StartY=-15.9084 StartZ=0 EndX=200.054 EndY=-15.9084 EndZ=0
    g8: LineSegment StartX=200.054 StartY=-15.9084 StartZ=0 EndX=64.7748 EndY=-15.9084 EndZ=0
    g9: LineSegment StartX=64.7748 StartY=-15.9084 StartZ=0 EndX=16.3454 EndY=-20.7039 EndZ=0
    g10: LineSegment StartX=16.3454 StartY=-20.7039 StartZ=0 EndX=2.88885 EndY=-12.2412 EndZ=0
    g11: LineSegment [constr] StartX=2.3291 StartY=-2.35546 StartZ=0 EndX=5.23499 EndY=-3.24958 EndZ=0
    g12: LineSegment StartX=2.88053 StartY=-2.52513 StartZ=0 EndX=1.81302 EndY=-5.99451 EndZ=0
    g13: LineSegment StartX=1.81302 StartY=-5.99451 StartZ=0 EndX=2.88885 EndY=-12.2412 EndZ=0
    g14: LineSegment StartX=5.46609 StartY=6.3073 StartZ=0 EndX=2.88053 EndY=-2.52513 EndZ=0
  constraints (22):
    c: PointOnObject(g1,g0)
    c: Perpendicular(g0,g1)
    c: Block(g1)
    c: Block(g0)
    c: Coincident(g1,g2)
    c: Coincident(g2,g3)
    c: Coincident(g3,g4)
    c: Coincident(g4,g5)
    c: Coincident(g5,g6)
    c: Coincident(g6,g7)
    c: Horizontal(g7)
    c: Coincident(g7,g8)
    c: Horizontal(g8)
    c: Coincident(g8,g9)
    c: Coincident(g9,g10)
    c: Block(g11)
    c: PointOnObject(g12,g11)
    c: Perpendicular(g11,g12)
    c: Coincident(g13,g12)
    c: Coincident(g13,g10)
    c: Coincident(g14,g1)
    c: Coincident(g14,g12)
FEATURE [PartDesign::Pocket] Pocket076
  BaseFeature = -> Thickness010
  Direction = (0,1,-2e-16)
  Length = 1000
  Length2 = 5
  Profile = -> Sketch132
  ReferenceAxis = -> Sketch132 [N_Axis]
  Refine = true
  Suppressed = false
  Type = 0
FEATURE [PartDesign::Body] Body031  label="leading edge 011"
  AllowCompound = false
  Group = -> [Pad054,Sketch131,Pocket075,Thickness010,Sketch132,Pocket076,Sketch133]
  Origin = -> Origin031
  Placement = pos=(0,-903.6,0) rot=(0,0,1;0rad)
  Tip = -> Pocket076
FEATURE [Sketcher::SketchObject] Sketch138
  ArcFitTolerance = 1e-06
  FullyConstrained = false
  MakeInternals = false
  Placement = pos=(0,0,0) rot=(1,0,0;1.5708rad)
  sketch-geometry (125):
    g0: BSplineCurve PolesCount=62 KnotsCount=62 Degree=3 IsPeriodic=1
    g1-g62: Circle [constr] x62 (B-spline internal-alignment scaffolding for g0; pole/knot coordinates omitted)
    g63-g124: GeomPoint [constr] x62 (B-spline internal-alignment scaffolding for g0; pole/knot coordinates omitted)
  constraints (125):
    c: InternalAlignment(g1,g0)
    c: Weight(g1) = 1
    c: InternalAlignment(g2,g0)
    c: Equal(g2,g1)
    c: InternalAlignment(g3,g0)
    c: Equal(g3,g1)
    c: InternalAlignment(g4,g0)
    c: Equal(g4,g1)
    c: InternalAlignment(g5,g0)
    c: Equal(g5,g1)
    c: InternalAlignment(g6,g0)
    c: Equal(g6,g1)
    c: InternalAlignment(g7,g0)
    c: Equal(g7,g1)
    c: InternalAlignment(g8,g0)
    c: Equal(g8,g1)
    c: InternalAlignment(g9,g0)
    c: Equal(g9,g1)
    c: InternalAlignment(g10,g0)
    c: Equal(g10,g1)
    c: InternalAlignment(g11,g0)
    c: Equal(g11,g1)
    c: InternalAlignment(g12,g0)
    c: Equal(g12,g1)
    c: InternalAlignment(g13,g0)
    c: Equal(g13,g1)
    c: InternalAlignment(g14,g0)
    c: Equal(g14,g1)
    c: InternalAlignment(g15,g0)
    c: Equal(g15,g1)
    c: InternalAlignment(g16,g0)
    c: Equal(g16,g1)
    c: InternalAlignment(g17,g0)
    c: Equal(g17,g1)
    c: InternalAlignment(g18,g0)
    c: Equal(g18,g1)
    c: InternalAlignment(g19,g0)
    c: Equal(g19,g1)
    c: InternalAlignment(g20,g0)
    c: Equal(g20,g1)
    c: InternalAlignment(g21,g0)
    c: Equal(g21,g1)
    c: InternalAlignment(g22,g0)
    c: Equal(g22,g1)
    c: InternalAlignment(g23,g0)
    c: Equal(g23,g1)
    c: InternalAlignment(g24,g0)
    c: Equal(g24,g1)
    c: InternalAlignment(g25,g0)
    c: Equal(g25,g1)
    c: InternalAlignment(g26,g0)
    c: Equal(g26,g1)
    c: InternalAlignment(g27,g0)
    c: Equal(g27,g1)
    c: InternalAlignment(g28,g0)
    c: Equal(g28,g1)
    c: InternalAlignment(g29,g0)
    c: Equal(g29,g1)
    c: InternalAlignment(g30,g0)
    c: Equal(g30,g1)
    c: InternalAlignment(g31,g0)
    c: Equal(g31,g1)
    c: InternalAlignment(g32,g0)
    c: Equal(g32,g1)
    c: InternalAlignment(g33,g0)
    c: Equal(g33,g1)
    c: InternalAlignment(g34,g0)
    c: Equal(g34,g1)
    c: InternalAlignment(g35,g0)
    c: Equal(g35,g1)
    c: InternalAlignment(g36,g0)
    c: Equal(g36,g1)
    c: InternalAlignment(g37,g0)
    c: Equal(g37,g1)
    c: InternalAlignment(g38,g0)
    c: Equal(g38,g1)
    c: InternalAlignment(g39,g0)
    c: Equal(g39,g1)
    c: InternalAlignment(g40,g0)
    c: Equal(g40,g1)
    c: InternalAlignment(g41,g0)
    c: Equal(g41,g1)
    c: InternalAlignment(g42,g0)
    c: Equal(g42,g1)
    c: InternalAlignment(g43,g0)
    c: Equal(g43,g1)
    c: InternalAlignment(g44,g0)
    c: Equal(g44,g1)
    c: InternalAlignment(g45,g0)
    c: Equal(g45,g1)
    c: InternalAlignment(g46,g0)
    c: Equal(g46,g1)
    c: InternalAlignment(g47,g0)
    c: Equal(g47,g1)
    c: InternalAlignment(g48,g0)
    c: Equal(g48,g1)
    c: InternalAlignment(g49,g0)
    c: Equal(g49,g1)
    c: InternalAlignment(g50,g0)
    c: Equal(g50,g1)
    c: InternalAlignment(g51,g0)
    c: Equal(g51,g1)
    c: InternalAlignment(g52,g0)
    c: Equal(g52,g1)
    c: InternalAlignment(g53,g0)
    c: Equal(g53,g1)
    c: InternalAlignment(g54,g0)
    c: Equal(g54,g1)
    c: InternalAlignment(g55,g0)
    c: Equal(g55,g1)
    c: InternalAlignment(g56,g0)
    c: Equal(g56,g1)
    c: InternalAlignment(g57,g0)
    c: Equal(g57,g1)
    c: InternalAlignment(g58,g0)
    c: Equal(g58,g1)
    c: InternalAlignment(g59,g0)
    c: Equal(g59,g1)
    c: InternalAlignment(g60,g0)
    c: Equal(g60,g1)
    c: InternalAlignment(g61,g0)
    c: Equal(g61,g1)
    c: InternalAlignment(g62,g0)
    c: Equal(g62,g1)
    c: InternalAlignment(g63-g124 -> g0) x62
FEATURE [PartDesign::Pad] Pad057
  Direction = (0,-1,2e-16)
  Length = 7
  Length2 = 10
  Placement = pos=(0,0,0) rot=(1,0,0;1.5708rad)
  Profile = -> Sketch138
  ReferenceAxis = -> Sketch138 [N_Axis]
  Refine = true
  Suppressed = false
  Type = 0
FEATURE [Sketcher::SketchObject] Sketch139
  ArcFitTolerance = 1e-06
  AttachmentSupport = -> [Pad057]
  FullyConstrained = false
  MakeInternals = false
  MapMode = 5
  Placement = pos=(0,-7,1.5e-15) rot=(1,0,0;1.5708rad)
  sketch-geometry (29):
    g0: LineSegment StartX=2.71326 StartY=0.775372 StartZ=0 EndX=3.3867 EndY=1.52303 EndZ=0
    g1: LineSegment StartX=3.3867 StartY=1.52303 StartZ=0 EndX=5.99321 EndY=4.17962 EndZ=0
    g2: LineSegment StartX=5.99321 StartY=4.17962 StartZ=0 EndX=11.2308 EndY=7.18071 EndZ=0
    g3: LineSegment StartX=11.2308 StartY=7.18071 StartZ=0 EndX=18.9287 EndY=10.4927 EndZ=0
    g4: LineSegment StartX=18.9287 StartY=10.4927 StartZ=0 EndX=30.0156 EndY=13.8045 EndZ=0
    g5: LineSegment StartX=30.0156 StartY=13.8045 StartZ=0 EndX=43.7053 EndY=16.6585 EndZ=0
    g6: LineSegment StartX=43.7053 StartY=16.6585 StartZ=0 EndX=58.3753 EndY=18.5837 EndZ=0
    g7: LineSegment StartX=58.3753 StartY=18.5837 StartZ=0 EndX=81.9328 EndY=20.1998 EndZ=0
    g8: LineSegment StartX=81.9328 StartY=20.1998 StartZ=0 EndX=99.116 EndY=20.5815 EndZ=0
    g9: LineSegment StartX=99.116 StartY=20.5815 StartZ=0 EndX=120.506 EndY=20.1998 EndZ=0
    g10: LineSegment StartX=120.506 StartY=20.1998 StartZ=0 EndX=145.772 EndY=18.6559 EndZ=0
    g11: LineSegment StartX=145.772 StartY=18.6559 StartZ=0 EndX=175.748 EndY=15.7728 EndZ=0
    g12: LineSegment StartX=175.748 StartY=15.7728 StartZ=0 EndX=200.436 EndY=12.5699 EndZ=0
    g13: LineSegment StartX=200.436 StartY=12.5699 StartZ=0 EndX=229.384 EndY=8.60252 EndZ=0
    g14: LineSegment StartX=229.384 StartY=8.60252 StartZ=0 EndX=252.135 EndY=5.21302 EndZ=0
    g15: LineSegment StartX=252.135 StartY=5.21302 StartZ=0 EndX=269.07 EndY=2.67143 EndZ=0
    g16: LineSegment StartX=269.07 StartY=2.67143 StartZ=0 EndX=269.07 EndY=1.39956 EndZ=0
    g17: LineSegment StartX=269.07 StartY=1.39956 StartZ=0 EndX=224.761 EndY=0.436598 EndZ=0
    g18: LineSegment StartX=224.761 StartY=0.436598 StartZ=0 EndX=175.487 EndY=-1.02731 EndZ=0
    g19: LineSegment StartX=175.487 StartY=-1.02731 StartZ=0 EndX=123.478 EndY=-2.41293 EndZ=0
    g20: LineSegment StartX=123.478 StartY=-2.41293 StartZ=0 EndX=62.0775 EndY=-3.87655 EndZ=0
    g21: LineSegment StartX=62.0775 StartY=-3.87655 StartZ=0 EndX=32.0529 EndY=-3.76091 EndZ=0
    g22: LineSegment StartX=32.0529 StartY=-3.76091 StartZ=0 EndX=18.888 EndY=-3.18288 EndZ=0
    g23: LineSegment StartX=18.888 StartY=-3.18288 StartZ=0 EndX=12.7286 EndY=-2.48971 EndZ=0
    g24: LineSegment StartX=12.7286 StartY=-2.48971 StartZ=0 EndX=8.49342 EndY=-1.8722 EndZ=0
    g25: LineSegment StartX=8.49342 StartY=-1.8722 StartZ=0 EndX=4.56236 EndY=-0.768246 EndZ=0
    g26: LineSegment StartX=4.56236 StartY=-0.768246 StartZ=0 EndX=3.01395 EndY=-0.301296 EndZ=0
    g27: ArcOfCircle CenterX=3.20505 CenterY=0.332397 CenterZ=0 NormalX=0 NormalY=0 NormalZ=1 AngleXU=0 Radius=0.661881 StartAngle=2.40837 EndAngle=4.41949
    g28: GeomPoint [constr] X=2.01486 Y=0 Z=0
  constraints (32):
    c: PointOnObject(g28,g-1)
    c: Coincident(g0,g1)
    c: Coincident(g1,g2)
    c: Coincident(g2,g3)
    c: Coincident(g3,g4)
    c: Coincident(g4,g5)
    c: Coincident(g5,g6)
    c: Coincident(g6,g7)
    c: Coincident(g7,g8)
    c: Coincident(g8,g9)
    c: Coincident(g9,g10)
    c: Coincident(g10,g11)
    c: Coincident(g11,g12)
    c: Coincident(g12,g13)
    c: Coincident(g13,g14)
    c: Coincident(g14,g15)
    c: Coincident(g15,g16)
    c: Vertical(g16)
    c: Coincident(g16,g17)
    c: Coincident(g17,g18)
    c: Coincident(g18,g19)
    c: Coincident(g19,g20)
    c: Coincident(g20,g21)
    c: Coincident(g21,g22)
    c: Coincident(g22,g23)
    c: Coincident(g23,g24)
    c: Coincident(g24,g25)
    c: Coincident(g25,g26)
    c: PointOnObject(g28,g0)
    c: PointOnObject(g28,g26)
    c: Tangent(g0,g27) = 1.5708
    c: Tangent(g26,g27) = 1.5708
FEATURE [PartDesign::Pocket] Pocket079
  BaseFeature = -> Pad057
  Direction = (0,1,-2e-16)
  Length = 9
  Length2 = 5
  Placement = pos=(0,0,0) rot=(1,0,0;1.5708rad)
  Profile = -> Sketch139
  ReferenceAxis = -> Sketch139 [N_Axis]
  Refine = true
  Suppressed = false
  Type = 0
FEATURE [Sketcher::SketchObject] Sketch140
  ArcFitTolerance = 1e-06
  AttachmentSupport = -> [XY_Plane033]
  FullyConstrained = false
  MakeInternals = false
  MapMode = 5
  sketch-geometry (4):
    g0: LineSegment StartX=295 StartY=17.3691 StartZ=0 EndX=295 EndY=-79.0747 EndZ=0
    g1: LineSegment StartX=295 StartY=-79.0747 StartZ=0 EndX=384.545 EndY=-79.0747 EndZ=0
    g2: LineSegment StartX=384.545 StartY=-79.0747 StartZ=0 EndX=384.545 EndY=17.3691 EndZ=0
    g3: LineSegment StartX=384.545 StartY=17.3691 StartZ=0 EndX=295 EndY=17.3691 EndZ=0
  constraints (9):
    c: Coincident(g0,g1)
    c: Coincident(g1,g2)
    c: Coincident(g2,g3)
    c: Coincident(g3,g0)
    c: Vertical(g0)
    c: Vertical(g2)
    c: Horizontal(g1)
    c: Horizontal(g3)
    c: DistanceX(g-1,g0) = 295
FEATURE [PartDesign::Pocket] Pocket080
  BaseFeature = -> Pocket079
  Direction = (0,0,-1)
  Length = 5
  Length2 = 5
  Midplane = true
  Placement = pos=(0,0,0) rot=(1,0,0;1.5708rad)
  Profile = -> Sketch140
  ReferenceAxis = -> Sketch140 [N_Axis]
  Refine = true
  Suppressed = false
  Type = 0
FEATURE [Sketcher::SketchObject] Sketch141
  ArcFitTolerance = 1e-06
  AttachmentSupport = -> [Pocket080]
  FullyConstrained = false
  MakeInternals = false
  MapMode = 5
  Placement = pos=(0,-7,1.5e-15) rot=(1,0,0;1.5708rad)
  sketch-geometry (42):
    g0: LineSegment StartX=45.884 StartY=17.7219 StartZ=0 EndX=33.93 EndY=-4.65497 EndZ=0
    g1: LineSegment StartX=49.8645 StartY=18.8062 StartZ=0 EndX=37.3312 EndY=-4.65497 EndZ=0
    g2: LineSegment StartX=45.884 StartY=17.7219 StartZ=0 EndX=49.8645 EndY=18.8062 EndZ=0
    g3: LineSegment StartX=33.93 StartY=-4.65497 StartZ=0 EndX=37.3312 EndY=-4.65497 EndZ=0
    g4: ArcOfCircle CenterX=18 CenterY=3 CenterZ=0 NormalX=0 NormalY=0 NormalZ=1 AngleXU=0 Radius=6.5 StartAngle=2.58175 EndAngle=4.38597
    g5: LineSegment StartX=20.6963 StartY=8.91437 StartZ=0 EndX=19.1912 EndY=11.3613 EndZ=0
    g6: LineSegment StartX=12.4923 StartY=6.45183 StartZ=0 EndX=11.7252 EndY=8.2111 EndZ=0
    g7: LineSegment StartX=11.7252 StartY=8.2111 StartZ=0 EndX=19.1912 EndY=11.3613 EndZ=0
    g8: LineSegment StartX=23.9272 StartY=0.331954 StartZ=0 EndX=26.093 EndY=-4.58272 EndZ=0
    g9: LineSegment StartX=15.9158 StartY=-3.15679 StartZ=0 EndX=16.6159 EndY=-4.58272 EndZ=0
    g10: LineSegment StartX=16.6159 StartY=-4.58272 StartZ=0 EndX=26.093 EndY=-4.58272 EndZ=0
    g11: LineSegment StartX=74.8373 StartY=20.9684 StartZ=0 EndX=89.2063 EndY=-4.24973 EndZ=0
    g12: LineSegment StartX=89.2063 StartY=-4.24973 StartZ=0 EndX=92.6591 EndY=-4.24973 EndZ=0
    g13: LineSegment StartX=92.6591 StartY=-4.24973 StartZ=0 EndX=78.184 EndY=21.1546 EndZ=0
    g14: LineSegment StartX=78.184 StartY=21.1546 StartZ=0 EndX=74.8373 EndY=20.9684 EndZ=0
    g15: LineSegment StartX=113.372 StartY=-3.61742 StartZ=0 EndX=125.992 EndY=20.9865 EndZ=0
    g16: LineSegment StartX=125.992 StartY=20.9865 StartZ=0 EndX=129.338 EndY=20.9348 EndZ=0
    g17: LineSegment StartX=129.338 StartY=20.9348 StartZ=0 EndX=116.743 EndY=-3.61742 EndZ=0
    g18: LineSegment StartX=116.743 StartY=-3.61742 StartZ=0 EndX=113.372 EndY=-3.61742 EndZ=0
    g19: LineSegment StartX=156.49 StartY=19.0126 StartZ=0 EndX=171.224 EndY=-2.18705 EndZ=0
    g20: LineSegment StartX=171.224 StartY=-2.18705 StartZ=0 EndX=175.064 EndY=-2.45586 EndZ=0
    g21: LineSegment StartX=175.064 StartY=-2.45586 StartZ=0 EndX=160.386 EndY=18.6636 EndZ=0
    g22: LineSegment StartX=160.386 StartY=18.6636 StartZ=0 EndX=156.49 EndY=19.0126 EndZ=0
    g23: LineSegment StartX=195.991 StartY=-1.14503 StartZ=0 EndX=209.19 EndY=12.3205 EndZ=0
    g24: LineSegment StartX=209.19 StartY=12.3205 StartZ=0 EndX=213.44 EndY=12.3702 EndZ=0
    g25: LineSegment StartX=213.44 StartY=12.3702 StartZ=0 EndX=200.192 EndY=-1.14503 EndZ=0
    g26: LineSegment StartX=200.192 StartY=-1.14503 StartZ=0 EndX=195.991 EndY=-1.14503 EndZ=0
    g27: LineSegment StartX=229.838 StartY=9.19446 StartZ=0 EndX=237.096 EndY=0 EndZ=0
    g28: LineSegment StartX=237.096 StartY=0 StartZ=0 EndX=240.918 EndY=0 EndZ=0
    g29: LineSegment StartX=240.918 StartY=0 StartZ=0 EndX=234.226 EndY=8.47688 EndZ=0
    g30: LineSegment StartX=234.226 StartY=8.47688 StartZ=0 EndX=229.838 EndY=9.19446 EndZ=0
    g31: ArcOfCircle CenterX=18 CenterY=3 CenterZ=0 NormalX=0 NormalY=0 NormalZ=1 AngleXU=0 Radius=6.5 StartAngle=5.86022 EndAngle=7.42624
    g32: Circle CenterX=18 CenterY=3 CenterZ=0 NormalX=0 NormalY=0 NormalZ=1 AngleXU=0 Radius=4.1
    g33: Circle CenterX=185 CenterY=7 CenterZ=0 NormalX=0 NormalY=0 NormalZ=1 AngleXU=0 Radius=4.1
    g34: ArcOfCircle CenterX=185 CenterY=7 CenterZ=0 NormalX=0 NormalY=0 NormalZ=1 AngleXU=0 Radius=6.5 StartAngle=1.96559 EndAngle=4.3176
    g35: LineSegment StartX=182.5 StartY=13 StartZ=0 EndX=182.5 EndY=15.9367 EndZ=0
    g36: LineSegment StartX=182.5 StartY=15.9367 StartZ=0 EndX=187.5 EndY=15.5349 EndZ=0
    g37: LineSegment StartX=187.5 StartY=15.5349 StartZ=0 EndX=187.5 EndY=13 EndZ=0
    g38: LineSegment StartX=182.5 StartY=1 StartZ=0 EndX=182.5 EndY=-1.79994 EndZ=0
    g39: LineSegment StartX=182.5 StartY=-1.79994 StartZ=0 EndX=187.5 EndY=-1.79994 EndZ=0
    g40: LineSegment StartX=187.5 StartY=-1.79994 StartZ=0 EndX=187.5 EndY=1 EndZ=0
    g41: ArcOfCircle CenterX=185 CenterY=7 CenterZ=0 NormalX=0 NormalY=0 NormalZ=1 AngleXU=0 Radius=6.5 StartAngle=5.10718 EndAngle=7.45919
  constraints (83):
    c: Coincident(g2,g0)
    c: Coincident(g2,g1)
    c: Coincident(g3,g0)
    c: Coincident(g3,g1)
    c: Horizontal(g3)
    c: Parallel(g0,g1)
    c: Distance(g1,g0) = 3
    c: Diameter(g4) = 13
    c: DistanceY(g-1,g4) = 3
    c: DistanceX(g-1,g4) = 18
    c: Coincident(g7,g6)
    c: Coincident(g7,g5)
    c: PointOnObject(g8,g31)
    c: Coincident(g10,g9)
    c: Horizontal(g10)
    c: Coincident(g10,g8)
    c: Coincident(g11,g12)
    c: Horizontal(g12)
    c: Coincident(g12,g13)
    c: Coincident(g13,g14)
    c: Coincident(g14,g11)
    c: Parallel(g11,g13)
    c: Distance(g13,g11) = 3
    c: Coincident(g15,g16)
    c: Coincident(g16,g17)
    c: Coincident(g17,g18)
    c: Coincident(g18,g15)
    c: Horizontal(g18)
    c: Parallel(g17,g15)
    c: Distance(g17,g15) = 3
    c: Coincident(g19,g20)
    c: Coincident(g20,g21)
    c: Coincident(g21,g22)
    c: Parallel(g19,g21)
    c: Distance(g21,g19) = 3
    c: Coincident(g23,g24)
    c: Coincident(g24,g25)
    c: Coincident(g25,g26)
    c: Horizontal(g26)
    c: Parallel(g23,g25)
    c: Distance(g25,g23) = 3
    c: PointOnObject(g27,g-1)
    c: Coincident(g27,g28)
    c: PointOnObject(g28,g-1)
    c: Coincident(g28,g29)
    c: Coincident(g29,g30)
    c: Coincident(g30,g27)
    c: Parallel(g27,g29)
    c: Distance(g29,g27) = 3
    c: Coincident(g31,g5)
    c: Coincident(g4,g6)
    c: Equal(g4,g31)
    c: Coincident(g4,g9)
    c: PointOnObject(g31,g8)
    c: Coincident(g4,g31)
    c: Coincident(g26,g23)
    c: Diameter(g32) = 8.2
    c: Coincident(g32,g4)
    c: Diameter(g33) = 8.2
    c: DistanceY(g-1,g33) = 7
    c: DistanceX(g-1,g33) = 185
    c: Diameter(g34) = 13
    c: Coincident(g34,g33)
    c: Coincident(g35,g36)
    c: Coincident(g36,g37)
    c: Vertical(g37)
    c: Vertical(g38)
    c: Coincident(g38,g39)
    c: Horizontal(g39)
    c: Coincident(g39,g40)
    c: PointOnObject(g40,g41)
    c: Vertical(g40)
    c: Vertical(g35)
    c: Distance(g37,g35) = 5
    c: DistanceX(g35,g33) = 2.5
    c: Distance(g38,g40) = 5
    c: DistanceX(g38,g33) = 2.5
    c: Coincident(g41,g37)
    c: Coincident(g34,g35)
    c: Equal(g34,g41)
    c: Coincident(g34,g38)
    c: PointOnObject(g41,g40)
    c: Coincident(g34,g41)
FEATURE [PartDesign::Pad] Pad058
  BaseFeature = -> Pocket080
  Direction = (0,-1,2e-16)
  Length = 7
  Length2 = 10
  Placement = pos=(0,0,0) rot=(1,0,0;1.5708rad)
  Profile = -> Sketch141
  ReferenceAxis = -> Sketch141 [N_Axis]
  Refine = true
  Reversed = true
  Suppressed = false
  Type = 0
FEATURE [PartDesign::Body] Body033  label="wingspar 012"
  AllowCompound = false
  Group = -> [Sketch138,Pad057,Sketch139,Pocket079,Sketch140,Pocket080,Sketch141,Pad058]
  Origin = -> Origin033
  Placement = pos=(0,-968,0) rot=(0,0,1;0rad)
  Tip = -> Pad058
FEATURE [Sketcher::SketchObject] Sketch152
  ArcFitTolerance = 1e-06
  FullyConstrained = false
  MakeInternals = false
  Placement = pos=(0,0,0) rot=(1,0,0;1.5708rad)
  sketch-geometry (125):
    g0: BSplineCurve PolesCount=62 KnotsCount=62 Degree=3 IsPeriodic=1
    g1-g62: Circle [constr] x62 (B-spline internal-alignment scaffolding for g0; pole/knot coordinates omitted)
    g63-g124: GeomPoint [constr] x62 (B-spline internal-alignment scaffolding for g0; pole/knot coordinates omitted)
  constraints (125):
    c: InternalAlignment(g1,g0)
    c: Weight(g1) = 1
    c: InternalAlignment(g2,g0)
    c: Equal(g2,g1)
    c: InternalAlignment(g3,g0)
    c: Equal(g3,g1)
    c: InternalAlignment(g4,g0)
    c: Equal(g4,g1)
    c: InternalAlignment(g5,g0)
    c: Equal(g5,g1)
    c: InternalAlignment(g6,g0)
    c: Equal(g6,g1)
    c: InternalAlignment(g7,g0)
    c: Equal(g7,g1)
    c: InternalAlignment(g8,g0)
    c: Equal(g8,g1)
    c: InternalAlignment(g9,g0)
    c: Equal(g9,g1)
    c: InternalAlignment(g10,g0)
    c: Equal(g10,g1)
    c: InternalAlignment(g11,g0)
    c: Equal(g11,g1)
    c: InternalAlignment(g12,g0)
    c: Equal(g12,g1)
    c: InternalAlignment(g13,g0)
    c: Equal(g13,g1)
    c: InternalAlignment(g14,g0)
    c: Equal(g14,g1)
    c: InternalAlignment(g15,g0)
    c: Equal(g15,g1)
    c: InternalAlignment(g16,g0)
    c: Equal(g16,g1)
    c: InternalAlignment(g17,g0)
    c: Equal(g17,g1)
    c: InternalAlignment(g18,g0)
    c: Equal(g18,g1)
    c: InternalAlignment(g19,g0)
    c: Equal(g19,g1)
    c: InternalAlignment(g20,g0)
    c: Equal(g20,g1)
    c: InternalAlignment(g21,g0)
    c: Equal(g21,g1)
    c: InternalAlignment(g22,g0)
    c: Equal(g22,g1)
    c: InternalAlignment(g23,g0)
    c: Equal(g23,g1)
    c: InternalAlignment(g24,g0)
    c: Equal(g24,g1)
    c: InternalAlignment(g25,g0)
    c: Equal(g25,g1)
    c: InternalAlignment(g26,g0)
    c: Equal(g26,g1)
    c: InternalAlignment(g27,g0)
    c: Equal(g27,g1)
    c: InternalAlignment(g28,g0)
    c: Equal(g28,g1)
    c: InternalAlignment(g29,g0)
    c: Equal(g29,g1)
    c: InternalAlignment(g30,g0)
    c: Equal(g30,g1)
    c: InternalAlignment(g31,g0)
    c: Equal(g31,g1)
    c: InternalAlignment(g32,g0)
    c: Equal(g32,g1)
    c: InternalAlignment(g33,g0)
    c: Equal(g33,g1)
    c: InternalAlignment(g34,g0)
    c: Equal(g34,g1)
    c: InternalAlignment(g35,g0)
    c: Equal(g35,g1)
    c: InternalAlignment(g36,g0)
    c: Equal(g36,g1)
    c: InternalAlignment(g37,g0)
    c: Equal(g37,g1)
    c: InternalAlignment(g38,g0)
    c: Equal(g38,g1)
    c: InternalAlignment(g39,g0)
    c: Equal(g39,g1)
    c: InternalAlignment(g40,g0)
    c: Equal(g40,g1)
    c: InternalAlignment(g41,g0)
    c: Equal(g41,g1)
    c: InternalAlignment(g42,g0)
    c: Equal(g42,g1)
    c: InternalAlignment(g43,g0)
    c: Equal(g43,g1)
    c: InternalAlignment(g44,g0)
    c: Equal(g44,g1)
    c: InternalAlignment(g45,g0)
    c: Equal(g45,g1)
    c: InternalAlignment(g46,g0)
    c: Equal(g46,g1)
    c: InternalAlignment(g47,g0)
    c: Equal(g47,g1)
    c: InternalAlignment(g48,g0)
    c: Equal(g48,g1)
    c: InternalAlignment(g49,g0)
    c: Equal(g49,g1)
    c: InternalAlignment(g50,g0)
    c: Equal(g50,g1)
    c: InternalAlignment(g51,g0)
    c: Equal(g51,g1)
    c: InternalAlignment(g52,g0)
    c: Equal(g52,g1)
    c: InternalAlignment(g53,g0)
    c: Equal(g53,g1)
    c: InternalAlignment(g54,g0)
    c: Equal(g54,g1)
    c: InternalAlignment(g55,g0)
    c: Equal(g55,g1)
    c: InternalAlignment(g56,g0)
    c: Equal(g56,g1)
    c: InternalAlignment(g57,g0)
    c: Equal(g57,g1)
    c: InternalAlignment(g58,g0)
    c: Equal(g58,g1)
    c: InternalAlignment(g59,g0)
    c: Equal(g59,g1)
    c: InternalAlignment(g60,g0)
    c: Equal(g60,g1)
    c: InternalAlignment(g61,g0)
    c: Equal(g61,g1)
    c: InternalAlignment(g62,g0)
    c: Equal(g62,g1)
    c: InternalAlignment(g63-g124 -> g0) x62
FEATURE [PartDesign::Pad] Pad064
  Direction = (0,-1,2e-16)
  Length = 289
  Length2 = 10
  Placement = pos=(0,0,0) rot=(1,0,0;1.5708rad)
  Profile = -> Sketch152
  ReferenceAxis = -> Sketch152 [N_Axis]
  Refine = true
  Suppressed = false
  Type = 0
FEATURE [Sketcher::SketchObject] Sketch154
  ArcFitTolerance = 1e-06
  AttachmentSupport = -> [XY_Plane035]
  FullyConstrained = false
  MakeInternals = false
  MapMode = 5
  sketch-geometry (4):
    g0: LineSegment StartX=295 StartY=17.3691 StartZ=0 EndX=295 EndY=-319.321 EndZ=0
    g1: LineSegment StartX=295 StartY=-319.321 StartZ=0 EndX=401.455 EndY=-319.321 EndZ=0
    g2: LineSegment StartX=401.455 StartY=-319.321 StartZ=0 EndX=401.455 EndY=17.3691 EndZ=0
    g3: LineSegment StartX=401.455 StartY=17.3691 StartZ=0 EndX=295 EndY=17.3691 EndZ=0
  constraints (9):
    c: Coincident(g0,g1)
    c: Coincident(g1,g2)
    c: Coincident(g2,g3)
    c: Coincident(g3,g0)
    c: Vertical(g0)
    c: Vertical(g2)
    c: Horizontal(g1)
    c: Horizontal(g3)
    c: DistanceX(g-1,g0) = 295
FEATURE [PartDesign::Pocket] Pocket088
  BaseFeature = -> Pad064
  Direction = (0,0,-1)
  Length = 5
  Length2 = 5
  Midplane = true
  Placement = pos=(0,0,0) rot=(1,0,0;1.5708rad)
  Profile = -> Sketch154
  ReferenceAxis = -> Sketch154 [N_Axis]
  Refine = true
  Suppressed = false
  Type = 0
FEATURE [Sketcher::SketchObject] Sketch155
  ArcFitTolerance = 1e-06
  AttachmentSupport = -> [Pocket088]
  FullyConstrained = false
  MakeInternals = false
  MapMode = 5
  Placement = pos=(0,-289,6.36e-14) rot=(1,0,0;1.5708rad)
  sketch-geometry (7):
    g0: ArcOfCircle CenterX=202 CenterY=6 CenterZ=0 NormalX=0 NormalY=0 NormalZ=1 AngleXU=0 Radius=8.6 StartAngle=1.5708 EndAngle=4.71239
    g1: LineSegment [constr] StartX=202 StartY=-2.6 StartZ=0 EndX=202 EndY=14.6 EndZ=0
    g2: LineSegment StartX=202 StartY=14.6 StartZ=0 EndX=188.969 EndY=46.4532 EndZ=0
    g3: LineSegment StartX=188.969 StartY=46.4532 StartZ=0 EndX=-27.7275 EndY=31.7802 EndZ=0
    g4: LineSegment StartX=-27.7275 StartY=31.7802 StartZ=0 EndX=-22.8987 EndY=-30.946 EndZ=0
    g5: LineSegment StartX=-22.8987 StartY=-30.946 StartZ=0 EndX=213.748 EndY=-30.946 EndZ=0
    g6: LineSegment StartX=213.748 StartY=-30.946 StartZ=0 EndX=202 EndY=-2.6 EndZ=0
  constraints (14):
    c: DistanceX(g-1,g0) = 202
    c: DistanceY(g-1,g0) = 6
    c: Vertical(g1)
    c: PointOnObject(g0,g1)
    c: Coincident(g0,g1)
    c: Coincident(g1,g0)
    c: Radius(g0) = 8.6
    c: Coincident(g0,g2)
    c: Coincident(g2,g3)
    c: Coincident(g3,g4)
    c: Coincident(g4,g5)
    c: Horizontal(g5)
    c: Coincident(g5,g6)
    c: Coincident(g6,g0)
FEATURE [PartDesign::Pocket] Pocket089
  BaseFeature = -> Pocket088
  Direction = (0,1,-2e-16)
  Length = 300
  Length2 = 5
  Placement = pos=(0,0,0) rot=(1,0,0;1.5708rad)
  Profile = -> Sketch155
  ReferenceAxis = -> Sketch155 [N_Axis]
  Refine = true
  Suppressed = false
  Type = 0
FEATURE [PartDesign::Plane] DatumPlane
  AttachmentOffset = pos=(0,0,24) rot=(0,0,1;0rad)
  AttachmentSupport = -> [XY_Plane035]
  Length = 383.397
  MapMode = 5
  Placement = pos=(0,0,24) rot=(0,0,1;0rad)
  ResizeMode = 0
  Width = 377.397
FEATURE [Sketcher::SketchObject] Sketch156
  ArcFitTolerance = 1e-06
  AttachmentSupport = -> [DatumPlane]
  FullyConstrained = true
  MakeInternals = false
  MapMode = 5
  Placement = pos=(0,0,24) rot=(0,0,1;0rad)
  sketch-geometry (23):
    g0: LineSegment StartX=204 StartY=-11.9893 StartZ=0 EndX=204 EndY=-57.4 EndZ=0
    g1: LineSegment StartX=204 StartY=-57.4 StartZ=0 EndX=288 EndY=-57.4 EndZ=0
    g2: LineSegment StartX=288 StartY=-57.4 StartZ=0 EndX=288 EndY=-3.6 EndZ=0
    g3: LineSegment StartX=288 StartY=-3.6 StartZ=0 EndX=212.389 EndY=-3.6 EndZ=0
    g4: LineSegment StartX=204 StartY=-60.4 StartZ=0 EndX=204 EndY=-114.8 EndZ=0
    g5: LineSegment StartX=204 StartY=-114.8 StartZ=0 EndX=288 EndY=-114.8 EndZ=0
    g6: LineSegment StartX=288 StartY=-114.8 StartZ=0 EndX=288 EndY=-60.4 EndZ=0
    g7: LineSegment StartX=288 StartY=-60.4 StartZ=0 EndX=204 EndY=-60.4 EndZ=0
    g8: LineSegment StartX=204 StartY=-117.8 StartZ=0 EndX=204 EndY=-172.2 EndZ=0
    g9: LineSegment StartX=204 StartY=-172.2 StartZ=0 EndX=288 EndY=-172.2 EndZ=0
    g10: LineSegment StartX=288 StartY=-172.2 StartZ=0 EndX=288 EndY=-117.8 EndZ=0
    g11: LineSegment StartX=288 StartY=-117.8 StartZ=0 EndX=204 EndY=-117.8 EndZ=0
    g12: LineSegment StartX=204 StartY=-175.2 StartZ=0 EndX=204 EndY=-229.6 EndZ=0
    g13: LineSegment StartX=204 StartY=-229.6 StartZ=0 EndX=288 EndY=-229.6 EndZ=0
    g14: LineSegment StartX=288 StartY=-229.6 StartZ=0 EndX=288 EndY=-175.2 EndZ=0
    g15: LineSegment StartX=288 StartY=-175.2 StartZ=0 EndX=204 EndY=-175.2 EndZ=0
    g16: LineSegment StartX=204 StartY=-232.6 StartZ=0 EndX=204 EndY=-286.4 EndZ=0
    g17: LineSegment StartX=204 StartY=-286.4 StartZ=0 EndX=288 EndY=-286.4 EndZ=0
    g18: LineSegment StartX=288 StartY=-286.4 StartZ=0 EndX=288 EndY=-232.6 EndZ=0
    g19: LineSegment StartX=288 StartY=-232.6 StartZ=0 EndX=204 EndY=-232.6 EndZ=0
    g20: LineSegment [constr] StartX=204 StartY=0 StartZ=0 EndX=204 EndY=-290 EndZ=0
    g21: LineSegment [constr] StartX=288 StartY=0 StartZ=0 EndX=288 EndY=-290 EndZ=0
    g22: LineSegment StartX=204 StartY=-11.9893 StartZ=0 EndX=212.389 EndY=-3.6 EndZ=0
  constraints (68):
    c: Coincident(g0,g1)
    c: Coincident(g1,g2)
    c: Coincident(g2,g3)
    c: Vertical(g2)
    c: Horizontal(g1)
    c: Horizontal(g3)
    c: Coincident(g4,g5)
    c: Coincident(g5,g6)
    c: Coincident(g6,g7)
    c: Coincident(g7,g4)
    c: Vertical(g4)
    c: Vertical(g6)
    c: Horizontal(g5)
    c: Horizontal(g7)
    c: Coincident(g8,g9)
    c: Coincident(g9,g10)
    c: Coincident(g10,g11)
    c: Coincident(g11,g8)
    c: Vertical(g8)
    c: Vertical(g10)
    c: Horizontal(g9)
    c: Horizontal(g11)
    c: Coincident(g12,g13)
    c: Coincident(g13,g14)
    c: Coincident(g14,g15)
    c: Coincident(g15,g12)
    c: Vertical(g12)
    c: Vertical(g14)
    c: Horizontal(g13)
    c: Horizontal(g15)
    c: Coincident(g16,g17)
    c: Coincident(g17,g18)
    c: Coincident(g18,g19)
    c: Coincident(g19,g16)
    c: Vertical(g16)
    c: Vertical(g18)
    c: Horizontal(g17)
    c: Horizontal(g19)
    c: PointOnObject(g20,g-1)
    c: Vertical(g20)
    c: DistanceX(g-1,g20) = 204
    c: PointOnObject(g4,g20)
    c: PointOnObject(g8,g20)
    c: PointOnObject(g12,g20)
    c: PointOnObject(g16,g20)
    c: PointOnObject(g21,g-1)
    c: Vertical(g21)
    c: DistanceX(g-1,g21) = 288
    c: PointOnObject(g2,g21)
    c: PointOnObject(g6,g21)
    c: PointOnObject(g10,g21)
    c: PointOnObject(g14,g21)
    c: PointOnObject(g18,g21)
    c: DistanceY(g20,g20) = 290
    c: DistanceY(g21,g21) = 290
    c: Distance(g16,g20) = 3.6
    c: Distance(g7,g1) = 3
    c: Distance(g11,g5) = 3
    c: Distance(g15,g9) = 3
    c: Distance(g19,g13) = 3
    c: DistanceY(g4,g4) = 54.4
    c: DistanceY(g8,g8) = 54.4
    c: DistanceY(g12,g12) = 54.4
    c: Angle(g-1,g22) = 0.785398
    c: Block(g3)
    c: Block(g0)
    c: Coincident(g0,g22)
    c: Coincident(g3,g22)
FEATURE [PartDesign::Pocket] Pocket090
  BaseFeature = -> Pocket089
  Direction = (0,0,-1)
  Length = 100
  Length2 = 5
  Placement = pos=(0,0,0) rot=(1,0,0;1.5708rad)
  Profile = -> Sketch156
  ReferenceAxis = -> Sketch156 [N_Axis]
  Refine = true
  Suppressed = false
  Type = 0
FEATURE [Sketcher::SketchObject] Sketch157
  ArcFitTolerance = 1e-06
  AttachmentSupport = -> [Pocket090]
  FullyConstrained = true
  MakeInternals = false
  MapMode = 5
  Placement = pos=(0,-3.6,-1.2e-15) rot=(1,0,0;1.5708rad)
  sketch-geometry (1):
    g0: Circle CenterX=202 CenterY=6 CenterZ=0 NormalX=0 NormalY=0 NormalZ=1 AngleXU=0 Radius=7
  constraints (3):
    c: DistanceX(g-1,g0) = 202
    c: DistanceY(g-1,g0) = 6
    c: Diameter(g0) = 14
FEATURE [PartDesign::Pocket] Pocket091
  BaseFeature = -> Pocket090
  Direction = (0,1,-2e-16)
  Length = 54.4
  Length2 = 5
  Placement = pos=(0,0,0) rot=(1,0,0;1.5708rad)
  Profile = -> Sketch157
  ReferenceAxis = -> Sketch157 [N_Axis]
  Refine = true
  Reversed = true
  Suppressed = false
  Type = 0
FEATURE [Sketcher::SketchObject] Sketch158
  ArcFitTolerance = 1e-06
  AttachmentSupport = -> [Pocket090]
  FullyConstrained = true
  MakeInternals = false
  MapMode = 5
  Placement = pos=(0,-60.4,-1.99e-14) rot=(1,0,0;1.5708rad)
  sketch-geometry (1):
    g0: Circle CenterX=202 CenterY=6 CenterZ=0 NormalX=0 NormalY=0 NormalZ=1 AngleXU=0 Radius=7
  constraints (3):
    c: DistanceX(g-1,g0) = 202
    c: DistanceY(g-1,g0) = 6
    c: Diameter(g0) = 14
FEATURE [PartDesign::Pocket] Pocket092
  BaseFeature = -> Pocket091
  Direction = (0,1,-2e-16)
  Length = 54.4
  Length2 = 5
  Placement = pos=(0,0,0) rot=(1,0,0;1.5708rad)
  Profile = -> Sketch158
  ReferenceAxis = -> Sketch158 [N_Axis]
  Refine = true
  Reversed = true
  Suppressed = false
  Type = 0
FEATURE [Sketcher::SketchObject] Sketch159
  ArcFitTolerance = 1e-06
  AttachmentSupport = -> [Pocket090]
  FullyConstrained = true
  MakeInternals = false
  MapMode = 5
  Placement = pos=(0,-117.8,-3.89e-14) rot=(1,0,0;1.5708rad)
  sketch-geometry (1):
    g0: Circle CenterX=202 CenterY=6 CenterZ=0 NormalX=0 NormalY=0 NormalZ=1 AngleXU=0 Radius=7
  constraints (3):
    c: DistanceX(g-1,g0) = 202
    c: DistanceY(g-1,g0) = 6
    c: Diameter(g0) = 14
FEATURE [PartDesign::Pocket] Pocket093
  BaseFeature = -> Pocket092
  Direction = (0,1,-2e-16)
  Length = 54.4
  Length2 = 5
  Placement = pos=(0,0,0) rot=(1,0,0;1.5708rad)
  Profile = -> Sketch159
  ReferenceAxis = -> Sketch159 [N_Axis]
  Refine = true
  Reversed = true
  Suppressed = false
  Type = 0
FEATURE [Sketcher::SketchObject] Sketch160
  ArcFitTolerance = 1e-06
  AttachmentSupport = -> [Pocket090]
  FullyConstrained = true
  MakeInternals = false
  MapMode = 5
  Placement = pos=(0,-175.2,-5.78e-14) rot=(1,0,0;1.5708rad)
  sketch-geometry (1):
    g0: Circle CenterX=202 CenterY=6 CenterZ=0 NormalX=0 NormalY=0 NormalZ=1 AngleXU=0 Radius=7
  constraints (3):
    c: DistanceX(g-1,g0) = 202
    c: DistanceY(g-1,g0) = 6
    c: Diameter(g0) = 14
FEATURE [Sketcher::SketchObject] Sketch161
  ArcFitTolerance = 1e-06
  AttachmentSupport = -> [Pocket090]
  FullyConstrained = true
  MakeInternals = false
  MapMode = 5
  Placement = pos=(0,-232.6,-7.68e-14) rot=(1,0,0;1.5708rad)
  sketch-geometry (1):
    g0: Circle CenterX=202 CenterY=6 CenterZ=0 NormalX=0 NormalY=0 NormalZ=1 AngleXU=0 Radius=7
  constraints (3):
    c: DistanceX(g-1,g0) = 202
    c: DistanceY(g-1,g0) = 6
    c: Diameter(g0) = 14
FEATURE [PartDesign::Pocket] Pocket094
  BaseFeature = -> Pocket093
  Direction = (0,1,-2e-16)
  Length = 54.4
  Length2 = 5
  Placement = pos=(0,0,0) rot=(1,0,0;1.5708rad)
  Profile = -> Sketch160
  ReferenceAxis = -> Sketch160 [N_Axis]
  Refine = true
  Reversed = true
  Suppressed = false
  Type = 0
FEATURE [PartDesign::Pocket] Pocket095
  BaseFeature = -> Pocket094
  Direction = (0,1,-2e-16)
  Length = 54.4
  Length2 = 5
  Placement = pos=(0,0,0) rot=(1,0,0;1.5708rad)
  Profile = -> Sketch161
  ReferenceAxis = -> Sketch161 [N_Axis]
  Refine = true
  Reversed = true
  Suppressed = false
  Type = 0
FEATURE [Sketcher::SketchObject] Sketch162
  ArcFitTolerance = 1e-06
  AttachmentSupport = -> [Pocket095]
  FullyConstrained = true
  MakeInternals = false
  MapMode = 5
  Placement = pos=(0,0,0) rot=(-1,0,0;1.5708rad)
  sketch-geometry (1):
    g0: Circle CenterX=202 CenterY=-6 CenterZ=0 NormalX=0 NormalY=0 NormalZ=1 AngleXU=0 Radius=4.05
  constraints (3):
    c: DistanceX(g-1,g0) = 202
    c: Diameter(g0) = 8.1
    c: DistanceY(g0,g-1) = 6
FEATURE [PartDesign::Pocket] Pocket096
  BaseFeature = -> Pocket095
  Direction = (0,-1,-2e-16)
  Length = 6
  Length2 = 5
  Placement = pos=(0,0,0) rot=(1,0,0;1.5708rad)
  Profile = -> Sketch162
  ReferenceAxis = -> Sketch162 [N_Axis]
  Refine = true
  Suppressed = false
  Type = 0
FEATURE [Sketcher::SketchObject] Sketch167
  ArcFitTolerance = 1e-06
  AttachmentSupport = -> [XY_Plane]
  FullyConstrained = true
  MakeInternals = false
  MapMode = 5
  sketch-geometry (12):
    g0: LineSegment StartX=-10 StartY=-7 StartZ=0 EndX=-10 EndY=-67 EndZ=0
    g1: LineSegment StartX=-10 StartY=-67 StartZ=0 EndX=35 EndY=-67 EndZ=0
    g2: LineSegment StartX=35 StartY=-67 StartZ=0 EndX=35 EndY=-7 EndZ=0
    g3: LineSegment StartX=35 StartY=-7 StartZ=0 EndX=-10 EndY=-7 EndZ=0
    g4: LineSegment StartX=40 StartY=-67 StartZ=0 EndX=165 EndY=-67 EndZ=0
    g5: LineSegment StartX=165 StartY=-67 StartZ=0 EndX=165 EndY=-7 EndZ=0
    g6: LineSegment StartX=165 StartY=-7 StartZ=0 EndX=40 EndY=-7 EndZ=0
    g7: LineSegment StartX=40 StartY=-7 StartZ=0 EndX=40 EndY=-67 EndZ=0
    g8: LineSegment StartX=170 StartY=-67 StartZ=0 EndX=300 EndY=-67 EndZ=0
    g9: LineSegment StartX=300 StartY=-67 StartZ=0 EndX=300 EndY=-7 EndZ=0
    g10: LineSegment StartX=300 StartY=-7 StartZ=0 EndX=170 EndY=-7 EndZ=0
    g11: LineSegment StartX=170 StartY=-7 StartZ=0 EndX=170 EndY=-67 EndZ=0
  constraints (36):
    c: Coincident(g0,g1)
    c: Coincident(g1,g2)
    c: Coincident(g2,g3)
    c: Coincident(g3,g0)
    c: Vertical(g0)
    c: Vertical(g2)
    c: Horizontal(g1)
    c: Horizontal(g3)
    c: Coincident(g4,g5)
    c: Coincident(g5,g6)
    c: Coincident(g6,g7)
    c: Coincident(g7,g4)
    c: Horizontal(g4)
    c: Horizontal(g6)
    c: Vertical(g5)
    c: Vertical(g7)
    c: Coincident(g8,g9)
    c: Coincident(g9,g10)
    c: Coincident(g10,g11)
    c: Coincident(g11,g8)
    c: Horizontal(g8)
    c: Horizontal(g10)
    c: Vertical(g9)
    c: Vertical(g11)
    c: DistanceY(g9,g-1) = 7
    c: DistanceY(g5,g-1) = 7
    c: DistanceY(g2,g-1) = 7
    c: Distance(g2,g7) = 5
    c: DistanceX(g0,g-1) = 10
    c: DistanceX(g-1,g9) = 300
    c: DistanceX(g-1,g1) = 35
    c: DistanceX(g-1,g4) = 165
    c: Distance(g5,g11) = 5
    c: DistanceY(g0,g0) = 60
    c: DistanceY(g7,g7) = 60
    c: DistanceY(g11,g11) = 60
FEATURE [PartDesign::Pocket] Pocket097
  BaseFeature = -> Pocket003
  Direction = (0,0,-1)
  Length = 100
  Length2 = 5
  Midplane = true
  Placement = pos=(0,0,0) rot=(1,0,0;1.5708rad)
  Profile = -> Sketch167
  ReferenceAxis = -> Sketch167 [N_Axis]
  Refine = true
  Suppressed = false
  Type = 0
FEATURE [Sketcher::SketchObject] Sketch008
  ArcFitTolerance = 1e-06
  AttachmentSupport = -> [Pocket097]
  FullyConstrained = false
  MakeInternals = false
  MapMode = 5
  Placement = pos=(0,-7,-2.3e-15) rot=(1,0,0;1.5708rad)
  sketch-geometry (60):
    g0: LineSegment StartX=45.884 StartY=17.7219 StartZ=0 EndX=33.93 EndY=-4.65497 EndZ=0
    g1: LineSegment StartX=49.8645 StartY=18.8062 StartZ=0 EndX=37.3312 EndY=-4.65497 EndZ=0
    g2: LineSegment StartX=45.884 StartY=17.7219 StartZ=0 EndX=49.8645 EndY=18.8062 EndZ=0
    g3: LineSegment StartX=33.93 StartY=-4.65497 StartZ=0 EndX=37.3312 EndY=-4.65497 EndZ=0
    g4: ArcOfCircle CenterX=18 CenterY=3 CenterZ=0 NormalX=0 NormalY=0 NormalZ=1 AngleXU=0 Radius=6.5 StartAngle=2.58175 EndAngle=4.38597
    g5: LineSegment StartX=20.6963 StartY=8.91437 StartZ=0 EndX=19.1912 EndY=11.3613 EndZ=0
    g6: LineSegment StartX=12.4923 StartY=6.45183 StartZ=0 EndX=11.7252 EndY=8.2111 EndZ=0
    g7: LineSegment StartX=11.7252 StartY=8.2111 StartZ=0 EndX=19.1912 EndY=11.3613 EndZ=0
    g8: LineSegment StartX=23.9272 StartY=0.331954 StartZ=0 EndX=26.093 EndY=-4.58272 EndZ=0
    g9: LineSegment StartX=15.9158 StartY=-3.15679 StartZ=0 EndX=16.6159 EndY=-4.58272 EndZ=0
    g10: LineSegment StartX=16.6159 StartY=-4.58272 StartZ=0 EndX=26.093 EndY=-4.58272 EndZ=0
    g11: LineSegment StartX=74.8373 StartY=20.9684 StartZ=0 EndX=89.2063 EndY=-4.24973 EndZ=0
    g12: LineSegment StartX=89.2063 StartY=-4.24973 StartZ=0 EndX=92.6591 EndY=-4.24973 EndZ=0
    g13: LineSegment StartX=92.6591 StartY=-4.24973 StartZ=0 EndX=78.184 EndY=21.1546 EndZ=0
    g14: LineSegment StartX=78.184 StartY=21.1546 StartZ=0 EndX=74.8373 EndY=20.9684 EndZ=0
    g15: LineSegment StartX=113.372 StartY=-3.61742 StartZ=0 EndX=125.992 EndY=20.9865 EndZ=0
    g16: LineSegment StartX=125.992 StartY=20.9865 StartZ=0 EndX=129.338 EndY=20.9348 EndZ=0
    g17: LineSegment StartX=129.338 StartY=20.9348 StartZ=0 EndX=116.743 EndY=-3.61742 EndZ=0
    g18: LineSegment StartX=116.743 StartY=-3.61742 StartZ=0 EndX=113.372 EndY=-3.61742 EndZ=0
    g19: LineSegment StartX=156.49 StartY=19.0126 StartZ=0 EndX=171.224 EndY=-2.18705 EndZ=0
    g20: LineSegment StartX=171.224 StartY=-2.18705 StartZ=0 EndX=175.064 EndY=-2.45586 EndZ=0
    g21: LineSegment StartX=175.064 StartY=-2.45586 StartZ=0 EndX=160.386 EndY=18.6636 EndZ=0
    g22: LineSegment StartX=160.386 StartY=18.6636 StartZ=0 EndX=156.49 EndY=19.0126 EndZ=0
    g23: LineSegment StartX=195.991 StartY=-1.14503 StartZ=0 EndX=209.19 EndY=12.3205 EndZ=0
    g24: LineSegment StartX=209.19 StartY=12.3205 StartZ=0 EndX=213.44 EndY=12.3702 EndZ=0
    g25: LineSegment StartX=213.44 StartY=12.3702 StartZ=0 EndX=200.192 EndY=-1.14503 EndZ=0
    g26: LineSegment StartX=200.192 StartY=-1.14503 StartZ=0 EndX=195.991 EndY=-1.14503 EndZ=0
    g27: LineSegment StartX=229.838 StartY=9.19446 StartZ=0 EndX=237.096 EndY=0 EndZ=0
    g28: LineSegment StartX=237.096 StartY=0 StartZ=0 EndX=240.918 EndY=0 EndZ=0
    g29: LineSegment StartX=240.918 StartY=0 StartZ=0 EndX=234.226 EndY=8.47688 EndZ=0
    g30: LineSegment StartX=234.226 StartY=8.47688 StartZ=0 EndX=229.838 EndY=9.19446 EndZ=0
    g31: ArcOfCircle CenterX=18 CenterY=3 CenterZ=0 NormalX=0 NormalY=0 NormalZ=1 AngleXU=0 Radius=6.5 StartAngle=5.86022 EndAngle=7.42624
    g32: Circle CenterX=18 CenterY=3 CenterZ=0 NormalX=0 NormalY=0 NormalZ=1 AngleXU=0 Radius=4.1
    g33: Circle CenterX=60 CenterY=8 CenterZ=0 NormalX=0 NormalY=0 NormalZ=1 AngleXU=0 Radius=4.1
    g34: Circle CenterX=150 CenterY=8 CenterZ=0 NormalX=0 NormalY=0 NormalZ=1 AngleXU=0 Radius=4.1
    g35: ArcOfCircle CenterX=60 CenterY=8 CenterZ=0 NormalX=0 NormalY=0 NormalZ=1 AngleXU=0 Radius=6.5 StartAngle=1.96559 EndAngle=4.3176
    g36: Circle CenterX=185 CenterY=7 CenterZ=0 NormalX=0 NormalY=0 NormalZ=1 AngleXU=0 Radius=4.1
    g37: LineSegment StartX=57.5 StartY=14 StartZ=0 EndX=57.5 EndY=19.5561 EndZ=0
    g38: LineSegment StartX=62.5 StartY=14 StartZ=0 EndX=62.5 EndY=20.0342 EndZ=0
    g39: LineSegment StartX=62.5 StartY=20.0342 StartZ=0 EndX=57.5 EndY=19.5561 EndZ=0
    g40: LineSegment StartX=57.5 StartY=2 StartZ=0 EndX=57.5 EndY=-4.90591 EndZ=0
    g41: LineSegment StartX=57.5 StartY=-4.90591 StartZ=0 EndX=62.5 EndY=-4.90591 EndZ=0
    g42: LineSegment StartX=62.5 StartY=-4.90591 StartZ=0 EndX=62.5 EndY=2 EndZ=0
    g43: ArcOfCircle CenterX=60 CenterY=8 CenterZ=0 NormalX=0 NormalY=0 NormalZ=1 AngleXU=0 Radius=6.5 StartAngle=5.10718 EndAngle=7.45919
    g44: ArcOfCircle CenterX=150 CenterY=8 CenterZ=0 NormalX=0 NormalY=0 NormalZ=1 AngleXU=0 Radius=6.5 StartAngle=1.96559 EndAngle=4.3176
    g45: ArcOfCircle CenterX=185 CenterY=7 CenterZ=0 NormalX=0 NormalY=0 NormalZ=1 AngleXU=0 Radius=6.5 StartAngle=1.96559 EndAngle=4.3176
    g46: LineSegment StartX=147.5 StartY=14 StartZ=0 EndX=147.5 EndY=19.2414 EndZ=0
    g47: LineSegment StartX=147.5 StartY=19.2414 StartZ=0 EndX=152.5 EndY=18.961 EndZ=0
    g48: LineSegment StartX=152.5 StartY=18.961 StartZ=0 EndX=152.5 EndY=14 EndZ=0
    g49: LineSegment StartX=147.5 StartY=2 StartZ=0 EndX=147.5 EndY=-2.5624 EndZ=0
    g50: LineSegment StartX=147.5 StartY=-2.5624 StartZ=0 EndX=152.5 EndY=-2.5624 EndZ=0
    g51: LineSegment StartX=152.5 StartY=-2.5624 StartZ=0 EndX=152.5 EndY=2 EndZ=0
    g52: ArcOfCircle CenterX=150 CenterY=8 CenterZ=0 NormalX=0 NormalY=0 NormalZ=1 AngleXU=0 Radius=6.5 StartAngle=5.10718 EndAngle=7.45919
    g53: LineSegment StartX=182.5 StartY=13 StartZ=0 EndX=182.5 EndY=15.9367 EndZ=0
    g54: LineSegment StartX=182.5 StartY=15.9367 StartZ=0 EndX=187.5 EndY=15.5349 EndZ=0
    g55: LineSegment StartX=187.5 StartY=15.5349 StartZ=0 EndX=187.5 EndY=13 EndZ=0
    g56: LineSegment StartX=182.5 StartY=1 StartZ=0 EndX=182.5 EndY=-1.79994 EndZ=0
    g57: LineSegment StartX=182.5 StartY=-1.79994 StartZ=0 EndX=187.5 EndY=-1.79994 EndZ=0
    g58: LineSegment StartX=187.5 StartY=-1.79994 StartZ=0 EndX=187.5 EndY=1 EndZ=0
    g59: ArcOfCircle CenterX=185 CenterY=7 CenterZ=0 NormalX=0 NormalY=0 NormalZ=1 AngleXU=0 Radius=6.5 StartAngle=5.10718 EndAngle=7.45919
  constraints (134):
    c: Coincident(g2,g0)
    c: Coincident(g2,g1)
    c: Coincident(g3,g0)
    c: Coincident(g3,g1)
    c: Horizontal(g3)
    c: Parallel(g0,g1)
    c: Distance(g1,g0) = 3
    c: Diameter(g4) = 13
    c: DistanceY(g-1,g4) = 3
    c: DistanceX(g-1,g4) = 18
    c: Coincident(g7,g6)
    c: Coincident(g7,g5)
    c: PointOnObject(g8,g31)
    c: Coincident(g10,g9)
    c: Horizontal(g10)
    c: Coincident(g10,g8)
    c: Coincident(g11,g12)
    c: Horizontal(g12)
    c: Coincident(g12,g13)
    c: Coincident(g13,g14)
    c: Coincident(g14,g11)
    c: Parallel(g11,g13)
    c: Distance(g13,g11) = 3
    c: Coincident(g15,g16)
    c: Coincident(g16,g17)
    c: Coincident(g17,g18)
    c: Coincident(g18,g15)
    c: Horizontal(g18)
    c: Parallel(g17,g15)
    c: Distance(g17,g15) = 3
    c: Coincident(g19,g20)
    c: Coincident(g20,g21)
    c: Coincident(g21,g22)
    c: Coincident(g22,g19)
    c: Parallel(g19,g21)
    c: Distance(g21,g19) = 3
    c: Coincident(g23,g24)
    c: Coincident(g24,g25)
    c: Coincident(g25,g26)
    c: Horizontal(g26)
    c: Parallel(g23,g25)
    c: Distance(g25,g23) = 3
    c: PointOnObject(g27,g-1)
    c: Coincident(g27,g28)
    c: PointOnObject(g28,g-1)
    c: Coincident(g28,g29)
    c: Coincident(g29,g30)
    c: Coincident(g30,g27)
    c: Parallel(g27,g29)
    c: Distance(g29,g27) = 3
    c: Coincident(g31,g5)
    c: Coincident(g4,g6)
    c: Equal(g4,g31)
    c: Coincident(g4,g9)
    c: PointOnObject(g31,g8)
    c: Coincident(g4,g31)
    c: Coincident(g26,g23)
    c: Diameter(g32) = 8.2
    c: Coincident(g32,g4)
    c: Diameter(g33) = 8.2
    c: Diameter(g34) = 8.2
    c: DistanceX(g33,g34) = 90
    c: Coincident(g35,g33)
    c: Diameter(g35) = 13
    c: DistanceX(g-1,g33) = 60
    c: DistanceY(g-1,g33) = 8
    c: DistanceY(g-1,g34) = 8
    c: Diameter(g36) = 8.2
    c: DistanceY(g-1,g36) = 7
    c: DistanceX(g-1,g36) = 185
    c: Vertical(g37)
    c: Vertical(g38)
    c: Coincident(g39,g38)
    c: Coincident(g39,g37)
    c: Distance(g38,g37) = 5
    c: DistanceX(g37,g33) = 2.5
    c: Coincident(g40,g41)
    c: Horizontal(g41)
    c: Coincident(g41,g42)
    c: PointOnObject(g42,g43)
    c: Vertical(g40)
    c: Vertical(g42)
    c: DistanceX(g40,g33) = 2.5
    c: DistanceX(g41,g41) = 5
    c: Coincident(g43,g38)
    c: Coincident(g35,g37)
    c: Equal(g35,g43)
    c: Coincident(g35,g40)
    c: PointOnObject(g43,g42)
    c: Coincident(g35,g43)
    c: Diameter(g44) = 13
    c: Coincident(g44,g34)
    c: Diameter(g45) = 13
    c: Coincident(g45,g36)
    c: Vertical(g46)
    c: Coincident(g46,g47)
    c: Coincident(g47,g48)
    c: Vertical(g48)
    c: Vertical(g49)
    c: Coincident(g49,g50)
    c: Horizontal(g50)
    c: Coincident(g50,g51)
    c: PointOnObject(g51,g52)
    c: Vertical(g51)
    c: DistanceX(g50,g50) = 5
    c: DistanceX(g49,g34) = 2.5
    c: Distance(g48,g46) = 5
    c: DistanceX(g46,g34) = 2.5
    c: Coincident(g52,g48)
    c: Coincident(g44,g46)
    c: Equal(g44,g52)
    c: Coincident(g44,g49)
    c: PointOnObject(g52,g51)
    c: Coincident(g44,g52)
    c: Coincident(g53,g54)
    c: Coincident(g54,g55)
    c: Vertical(g55)
    c: Vertical(g56)
    c: Coincident(g56,g57)
    c: Horizontal(g57)
    c: Coincident(g57,g58)
    c: PointOnObject(g58,g59)
    c: Vertical(g58)
    c: Vertical(g53)
    c: Distance(g55,g53) = 5
    c: DistanceX(g53,g36) = 2.5
    c: Distance(g56,g58) = 5
    c: DistanceX(g56,g36) = 2.5
    c: Coincident(g59,g55)
    c: Coincident(g45,g53)
    c: Equal(g45,g59)
    c: Coincident(g45,g56)
    c: PointOnObject(g59,g58)
    c: Coincident(g45,g59)
FEATURE [PartDesign::Pad] Pad068
  BaseFeature = -> Pocket097
  Direction = (0,-1,2e-16)
  Length = 7
  Length2 = 10
  Placement = pos=(0,0,0) rot=(1,0,0;1.5708rad)
  Profile = -> Sketch008
  ReferenceAxis = -> Sketch008 [N_Axis]
  Refine = true
  Reversed = true
  Suppressed = false
  Type = 0
FEATURE [Sketcher::SketchObject] Sketch168
  ArcFitTolerance = 1e-06
  AttachmentSupport = -> [Pad068]
  FullyConstrained = false
  MakeInternals = false
  MapMode = 5
  Placement = pos=(170,0,0) rot=(0.707107,0,0.707107;3.14159rad)
  sketch-geometry (14):
    g0: LineSegment StartX=-2.86242 StartY=8.94149 StartZ=0 EndX=6.44299 EndY=28.05 EndZ=0
    g1: LineSegment StartX=16.796 StartY=49.3097 StartZ=0 EndX=17.6093 EndY=49.3097 EndZ=0
    g2: LineSegment StartX=17.6093 StartY=49.3097 StartZ=0 EndX=17.6093 EndY=46.4118 EndZ=0
    g3: LineSegment StartX=17.6093 StartY=46.4118 StartZ=0 EndX=8.66937 EndY=28.0538 EndZ=0
    g4: LineSegment StartX=-1.3402 StartY=7.49928 StartZ=0 EndX=-2.53265 EndY=7.49928 EndZ=0
    g5: LineSegment StartX=-2.53265 StartY=7.49928 StartZ=0 EndX=-2.86242 EndY=8.94149 EndZ=0
    g6: LineSegment StartX=-1.56722 StartY=48.7925 StartZ=0 EndX=7.5685 EndY=30.3349 EndZ=0
    g7: LineSegment StartX=18.4673 StartY=8.20781 StartZ=0 EndX=16.7969 EndY=7.18146 EndZ=0
    g8: LineSegment StartX=16.7969 StartY=7.18146 StartZ=0 EndX=7.58766 EndY=25.7876 EndZ=0
    g9: LineSegment StartX=-2.2596 StartY=45.768 StartZ=0 EndX=-1.56722 EndY=48.7925 EndZ=0
    g10: LineSegment StartX=8.66937 StartY=28.0538 StartZ=0 EndX=18.4673 EndY=8.20781 EndZ=0
    g11: LineSegment StartX=7.5685 StartY=30.3349 StartZ=0 EndX=16.796 EndY=49.3097 EndZ=0
    g12: LineSegment StartX=6.44299 StartY=28.05 StartZ=0 EndX=-2.2596 EndY=45.768 EndZ=0
    g13: LineSegment StartX=7.58766 StartY=25.7876 StartZ=0 EndX=-1.3402 EndY=7.49928 EndZ=0
  constraints (24):
    c: Coincident(g11,g1)
    c: Horizontal(g1)
    c: Coincident(g1,g2)
    c: Vertical(g2)
    c: Coincident(g2,g3)
    c: Coincident(g13,g4)
    c: Horizontal(g4)
    c: Coincident(g4,g5)
    c: Coincident(g5,g0)
    c: Parallel(g0,g3)
    c: Distance(g3,g0) = 2
    c: Coincident(g10,g7)
    c: Coincident(g7,g8)
    c: Parallel(g8,g6)
    c: Distance(g8,g6) = 2
    c: Coincident(g9,g12)
    c: Coincident(g9,g6)
    c: PointOnObject(g6,g11)
    c: PointOnObject(g0,g12)
    c: PointOnObject(g11,g6)
    c: PointOnObject(g8,g13)
    c: PointOnObject(g12,g0)
    c: Coincident(g3,g10)
    c: PointOnObject(g13,g8)
FEATURE [PartDesign::Pad] Pad069
  BaseFeature = -> Pad068
  Direction = (1,0,-2e-16)
  Length = 5
  Length2 = 10
  Placement = pos=(0,0,0) rot=(1,0,0;1.5708rad)
  Profile = -> Sketch168
  ReferenceAxis = -> Sketch168 [N_Axis]
  Refine = true
  Reversed = true
  Suppressed = false
  Type = 0
FEATURE [Sketcher::SketchObject] Sketch169
  ArcFitTolerance = 1e-06
  AttachmentSupport = -> [Pad069]
  FullyConstrained = false
  MakeInternals = false
  MapMode = 5
  Placement = pos=(35,0,0) rot=(0.707107,0,-0.707107;3.14159rad)
  sketch-geometry (12):
    g0: LineSegment StartX=-17.0415 StartY=48.3111 StartZ=0 EndX=-17.0415 EndY=49.7892 EndZ=0
    g1: LineSegment StartX=-17.0415 StartY=49.7892 StartZ=0 EndX=-15.5583 EndY=49.7892 EndZ=0
    g2: LineSegment StartX=-15.5583 StartY=49.7892 StartZ=0 EndX=5.93029 EndY=8.81738 EndZ=0
    g3: LineSegment StartX=5.93029 StartY=8.81738 StartZ=0 EndX=5.93029 EndY=7.1685 EndZ=0
    g4: LineSegment StartX=5.93029 StartY=7.1685 StartZ=0 EndX=4.5367 EndY=7.1685 EndZ=0
    g5: LineSegment StartX=4.5367 StartY=7.1685 StartZ=0 EndX=-17.0415 EndY=48.3111 EndZ=0
    g6: LineSegment StartX=-17.1124 StartY=7.28835 StartZ=0 EndX=-16.1126 EndY=7.28835 EndZ=0
    g7: LineSegment StartX=-16.1126 StartY=7.28835 StartZ=0 EndX=5.8579 EndY=48.0729 EndZ=0
    g8: LineSegment StartX=5.8579 StartY=48.0729 StartZ=0 EndX=5.97735 EndY=49.7725 EndZ=0
    g9: LineSegment StartX=5.97735 StartY=49.7725 StartZ=0 EndX=4.50171 EndY=49.7725 EndZ=0
    g10: LineSegment StartX=4.50171 StartY=49.7725 StartZ=0 EndX=-17.1124 EndY=9.64961 EndZ=0
    g11: LineSegment StartX=-17.1124 StartY=9.64961 StartZ=0 EndX=-17.1124 EndY=7.28835 EndZ=0
  constraints (23):
    c: Vertical(g0)
    c: Coincident(g0,g1)
    c: Horizontal(g1)
    c: Coincident(g1,g2)
    c: Coincident(g2,g3)
    c: Vertical(g3)
    c: Coincident(g3,g4)
    c: Horizontal(g4)
    c: Coincident(g4,g5)
    c: Coincident(g5,g0)
    c: Parallel(g2,g5)
    c: Distance(g5,g2) = 2
    c: Horizontal(g6)
    c: Coincident(g6,g7)
    c: Coincident(g7,g8)
    c: Coincident(g8,g9)
    c: Horizontal(g9)
    c: Coincident(g9,g10)
    c: Coincident(g10,g11)
    c: Coincident(g11,g6)
    c: Vertical(g11)
    c: Parallel(g10,g7)
    c: Distance(g7,g10) = 2
FEATURE [PartDesign::Pad] Pad070
  BaseFeature = -> Pad069
  Direction = (-1,0,-2e-16)
  Length = 5
  Length2 = 10
  Placement = pos=(0,0,0) rot=(1,0,0;1.5708rad)
  Profile = -> Sketch169
  ReferenceAxis = -> Sketch169 [N_Axis]
  Refine = true
  Reversed = true
  Suppressed = false
  Type = 0
FEATURE [PartDesign::Chamfer] Chamfer
  Angle = 45
  Base = -> Pad070 [Edge189,Edge188]
  BaseFeature = -> Pad070
  ChamferType = 0
  FlipDirection = false
  Placement = pos=(0,0,0) rot=(1,0,0;1.5708rad)
  Refine = true
  Size = 1
  Size2 = 1
  SupportTransform = false
  Suppressed = false
  UseAllEdges = false
FEATURE [PartDesign::Body] Body  label="wingspar 001"
  AllowCompound = false
  Group = -> [Sketch003,Pad,Sketch006,Pocket002,Sketch007,Pocket003,Pocket097,Sketch008,Sketch167,Pad068,Sketch168,Pad069,Sketch169,Pad070,Chamfer]
  Origin = -> Origin
  Tip = -> Chamfer
FEATURE [Sketcher::SketchObject] Sketch170
  ArcFitTolerance = 1e-06
  FullyConstrained = false
  MakeInternals = false
  Placement = pos=(0,0,0) rot=(1,0,0;1.5708rad)
  sketch-geometry (125):
    g0: BSplineCurve PolesCount=62 KnotsCount=62 Degree=3 IsPeriodic=1
    g1-g62: Circle [constr] x62 (B-spline internal-alignment scaffolding for g0; pole/knot coordinates omitted)
    g63-g124: GeomPoint [constr] x62 (B-spline internal-alignment scaffolding for g0; pole/knot coordinates omitted)
  constraints (125):
    c: InternalAlignment(g1,g0)
    c: Weight(g1) = 1
    c: InternalAlignment(g2,g0)
    c: Equal(g2,g1)
    c: InternalAlignment(g3,g0)
    c: Equal(g3,g1)
    c: InternalAlignment(g4,g0)
    c: Equal(g4,g1)
    c: InternalAlignment(g5,g0)
    c: Equal(g5,g1)
    c: InternalAlignment(g6,g0)
    c: Equal(g6,g1)
    c: InternalAlignment(g7,g0)
    c: Equal(g7,g1)
    c: InternalAlignment(g8,g0)
    c: Equal(g8,g1)
    c: InternalAlignment(g9,g0)
    c: Equal(g9,g1)
    c: InternalAlignment(g10,g0)
    c: Equal(g10,g1)
    c: InternalAlignment(g11,g0)
    c: Equal(g11,g1)
    c: InternalAlignment(g12,g0)
    c: Equal(g12,g1)
    c: InternalAlignment(g13,g0)
    c: Equal(g13,g1)
    c: InternalAlignment(g14,g0)
    c: Equal(g14,g1)
    c: InternalAlignment(g15,g0)
    c: Equal(g15,g1)
    c: InternalAlignment(g16,g0)
    c: Equal(g16,g1)
    c: InternalAlignment(g17,g0)
    c: Equal(g17,g1)
    c: InternalAlignment(g18,g0)
    c: Equal(g18,g1)
    c: InternalAlignment(g19,g0)
    c: Equal(g19,g1)
    c: InternalAlignment(g20,g0)
    c: Equal(g20,g1)
    c: InternalAlignment(g21,g0)
    c: Equal(g21,g1)
    c: InternalAlignment(g22,g0)
    c: Equal(g22,g1)
    c: InternalAlignment(g23,g0)
    c: Equal(g23,g1)
    c: InternalAlignment(g24,g0)
    c: Equal(g24,g1)
    c: InternalAlignment(g25,g0)
    c: Equal(g25,g1)
    c: InternalAlignment(g26,g0)
    c: Equal(g26,g1)
    c: InternalAlignment(g27,g0)
    c: Equal(g27,g1)
    c: InternalAlignment(g28,g0)
    c: Equal(g28,g1)
    c: InternalAlignment(g29,g0)
    c: Equal(g29,g1)
    c: InternalAlignment(g30,g0)
    c: Equal(g30,g1)
    c: InternalAlignment(g31,g0)
    c: Equal(g31,g1)
    c: InternalAlignment(g32,g0)
    c: Equal(g32,g1)
    c: InternalAlignment(g33,g0)
    c: Equal(g33,g1)
    c: InternalAlignment(g34,g0)
    c: Equal(g34,g1)
    c: InternalAlignment(g35,g0)
    c: Equal(g35,g1)
    c: InternalAlignment(g36,g0)
    c: Equal(g36,g1)
    c: InternalAlignment(g37,g0)
    c: Equal(g37,g1)
    c: InternalAlignment(g38,g0)
    c: Equal(g38,g1)
    c: InternalAlignment(g39,g0)
    c: Equal(g39,g1)
    c: InternalAlignment(g40,g0)
    c: Equal(g40,g1)
    c: InternalAlignment(g41,g0)
    c: Equal(g41,g1)
    c: InternalAlignment(g42,g0)
    c: Equal(g42,g1)
    c: InternalAlignment(g43,g0)
    c: Equal(g43,g1)
    c: InternalAlignment(g44,g0)
    c: Equal(g44,g1)
    c: InternalAlignment(g45,g0)
    c: Equal(g45,g1)
    c: InternalAlignment(g46,g0)
    c: Equal(g46,g1)
    c: InternalAlignment(g47,g0)
    c: Equal(g47,g1)
    c: InternalAlignment(g48,g0)
    c: Equal(g48,g1)
    c: InternalAlignment(g49,g0)
    c: Equal(g49,g1)
    c: InternalAlignment(g50,g0)
    c: Equal(g50,g1)
    c: InternalAlignment(g51,g0)
    c: Equal(g51,g1)
    c: InternalAlignment(g52,g0)
    c: Equal(g52,g1)
    c: InternalAlignment(g53,g0)
    c: Equal(g53,g1)
    c: InternalAlignment(g54,g0)
    c: Equal(g54,g1)
    c: InternalAlignment(g55,g0)
    c: Equal(g55,g1)
    c: InternalAlignment(g56,g0)
    c: Equal(g56,g1)
    c: InternalAlignment(g57,g0)
    c: Equal(g57,g1)
    c: InternalAlignment(g58,g0)
    c: Equal(g58,g1)
    c: InternalAlignment(g59,g0)
    c: Equal(g59,g1)
    c: InternalAlignment(g60,g0)
    c: Equal(g60,g1)
    c: InternalAlignment(g61,g0)
    c: Equal(g61,g1)
    c: InternalAlignment(g62,g0)
    c: Equal(g62,g1)
    c: InternalAlignment(g63-g124 -> g0) x62
FEATURE [PartDesign::Pad] Pad071
  Direction = (0,-1,2e-16)
  Length = 49.95
  Length2 = 10
  Placement = pos=(0,0,0) rot=(1,0,0;1.5708rad)
  Profile = -> Sketch170
  ReferenceAxis = -> Sketch170 [N_Axis]
  Refine = true
  Suppressed = false
  Type = 0
FEATURE [Sketcher::SketchObject] Sketch171
  ArcFitTolerance = 1e-06
  AttachmentSupport = -> [Pad071]
  FullyConstrained = false
  MakeInternals = false
  MapMode = 5
  Placement = pos=(0,-49.95,1.1e-14) rot=(1,0,0;1.5708rad)
  sketch-geometry (29):
    g0: LineSegment StartX=2.71326 StartY=0.775372 StartZ=0 EndX=3.3867 EndY=1.52303 EndZ=0
    g1: LineSegment StartX=3.3867 StartY=1.52303 StartZ=0 EndX=5.99321 EndY=4.17962 EndZ=0
    g2: LineSegment StartX=5.99321 StartY=4.17962 StartZ=0 EndX=11.2308 EndY=7.18071 EndZ=0
    g3: LineSegment StartX=11.2308 StartY=7.18071 StartZ=0 EndX=18.9287 EndY=10.4927 EndZ=0
    g4: LineSegment StartX=18.9287 StartY=10.4927 StartZ=0 EndX=30.0156 EndY=13.8045 EndZ=0
    g5: LineSegment StartX=30.0156 StartY=13.8045 StartZ=0 EndX=43.7053 EndY=16.6585 EndZ=0
    g6: LineSegment StartX=43.7053 StartY=16.6585 StartZ=0 EndX=58.3753 EndY=18.5837 EndZ=0
    g7: LineSegment StartX=58.3753 StartY=18.5837 StartZ=0 EndX=81.9328 EndY=20.1998 EndZ=0
    g8: LineSegment StartX=81.9328 StartY=20.1998 StartZ=0 EndX=99.116 EndY=20.5815 EndZ=0
    g9: LineSegment StartX=99.116 StartY=20.5815 StartZ=0 EndX=120.506 EndY=20.1998 EndZ=0
    g10: LineSegment StartX=120.506 StartY=20.1998 StartZ=0 EndX=145.772 EndY=18.6559 EndZ=0
    g11: LineSegment StartX=145.772 StartY=18.6559 StartZ=0 EndX=175.748 EndY=15.7728 EndZ=0
    g12: LineSegment StartX=175.748 StartY=15.7728 StartZ=0 EndX=200.436 EndY=12.5699 EndZ=0
    g13: LineSegment StartX=200.436 StartY=12.5699 StartZ=0 EndX=229.384 EndY=8.60252 EndZ=0
    g14: LineSegment StartX=229.384 StartY=8.60252 StartZ=0 EndX=252.135 EndY=5.21302 EndZ=0
    g15: LineSegment StartX=252.135 StartY=5.21302 StartZ=0 EndX=269.07 EndY=2.67143 EndZ=0
    g16: LineSegment StartX=269.07 StartY=2.67143 StartZ=0 EndX=269.07 EndY=1.39956 EndZ=0
    g17: LineSegment StartX=269.07 StartY=1.39956 StartZ=0 EndX=224.761 EndY=0.436598 EndZ=0
    g18: LineSegment StartX=224.761 StartY=0.436598 StartZ=0 EndX=175.487 EndY=-1.02731 EndZ=0
    g19: LineSegment StartX=175.487 StartY=-1.02731 StartZ=0 EndX=123.478 EndY=-2.41293 EndZ=0
    g20: LineSegment StartX=123.478 StartY=-2.41293 StartZ=0 EndX=62.0775 EndY=-3.87655 EndZ=0
    g21: LineSegment StartX=62.0775 StartY=-3.87655 StartZ=0 EndX=32.0529 EndY=-3.76091 EndZ=0
    g22: LineSegment StartX=32.0529 StartY=-3.76091 StartZ=0 EndX=18.888 EndY=-3.18288 EndZ=0
    g23: LineSegment StartX=18.888 StartY=-3.18288 StartZ=0 EndX=12.7286 EndY=-2.48971 EndZ=0
    g24: LineSegment StartX=12.7286 StartY=-2.48971 StartZ=0 EndX=8.49342 EndY=-1.8722 EndZ=0
    g25: LineSegment StartX=8.49342 StartY=-1.8722 StartZ=0 EndX=4.56236 EndY=-0.768246 EndZ=0
    g26: LineSegment StartX=4.56236 StartY=-0.768246 StartZ=0 EndX=3.01395 EndY=-0.301296 EndZ=0
    g27: ArcOfCircle CenterX=3.20505 CenterY=0.332397 CenterZ=0 NormalX=0 NormalY=0 NormalZ=1 AngleXU=0 Radius=0.661881 StartAngle=2.40837 EndAngle=4.41949
    g28: GeomPoint [constr] X=2.01486 Y=0 Z=0
  constraints (32):
    c: PointOnObject(g28,g-1)
    c: Coincident(g0,g1)
    c: Coincident(g1,g2)
    c: Coincident(g2,g3)
    c: Coincident(g3,g4)
    c: Coincident(g4,g5)
    c: Coincident(g5,g6)
    c: Coincident(g6,g7)
    c: Coincident(g7,g8)
    c: Coincident(g8,g9)
    c: Coincident(g9,g10)
    c: Coincident(g10,g11)
    c: Coincident(g11,g12)
    c: Coincident(g12,g13)
    c: Coincident(g13,g14)
    c: Coincident(g14,g15)
    c: Coincident(g15,g16)
    c: Vertical(g16)
    c: Coincident(g16,g17)
    c: Coincident(g17,g18)
    c: Coincident(g18,g19)
    c: Coincident(g19,g20)
    c: Coincident(g20,g21)
    c: Coincident(g21,g22)
    c: Coincident(g22,g23)
    c: Coincident(g23,g24)
    c: Coincident(g24,g25)
    c: Coincident(g25,g26)
    c: PointOnObject(g28,g0)
    c: PointOnObject(g28,g26)
    c: Tangent(g0,g27) = 1.5708
    c: Tangent(g26,g27) = 1.5708
FEATURE [PartDesign::Pocket] Pocket098
  BaseFeature = -> Pad071
  Direction = (0,1,-2e-16)
  Length = 49.95
  Length2 = 5
  Placement = pos=(0,0,0) rot=(1,0,0;1.5708rad)
  Profile = -> Sketch171
  ReferenceAxis = -> Sketch171 [N_Axis]
  Refine = true
  Suppressed = false
  Type = 0
FEATURE [Sketcher::SketchObject] Sketch172
  ArcFitTolerance = 1e-06
  AttachmentSupport = -> [XY_Plane036]
  FullyConstrained = false
  MakeInternals = false
  MapMode = 5
  sketch-geometry (4):
    g0: LineSegment StartX=295 StartY=17.3691 StartZ=0 EndX=295 EndY=-79.0747 EndZ=0
    g1: LineSegment StartX=295 StartY=-79.0747 StartZ=0 EndX=384.545 EndY=-79.0747 EndZ=0
    g2: LineSegment StartX=384.545 StartY=-79.0747 StartZ=0 EndX=384.545 EndY=17.3691 EndZ=0
    g3: LineSegment StartX=384.545 StartY=17.3691 StartZ=0 EndX=295 EndY=17.3691 EndZ=0
  constraints (9):
    c: Coincident(g0,g1)
    c: Coincident(g1,g2)
    c: Coincident(g2,g3)
    c: Coincident(g3,g0)
    c: Vertical(g0)
    c: Vertical(g2)
    c: Horizontal(g1)
    c: Horizontal(g3)
    c: DistanceX(g-1,g0) = 295
FEATURE [PartDesign::Pocket] Pocket099
  BaseFeature = -> Pocket098
  Direction = (0,0,-1)
  Length = 5
  Length2 = 5
  Midplane = true
  Placement = pos=(0,0,0) rot=(1,0,0;1.5708rad)
  Profile = -> Sketch172
  ReferenceAxis = -> Sketch172 [N_Axis]
  Refine = true
  Suppressed = false
  Type = 0
FEATURE [Sketcher::SketchObject] Sketch174
  ArcFitTolerance = 1e-06
  AttachmentSupport = -> [XY_Plane036]
  FullyConstrained = true
  MakeInternals = false
  MapMode = 5
  sketch-geometry (12):
    g0: LineSegment StartX=-10 StartY=-7 StartZ=0 EndX=-10 EndY=-67 EndZ=0
    g1: LineSegment StartX=-10 StartY=-67 StartZ=0 EndX=35 EndY=-67 EndZ=0
    g2: LineSegment StartX=35 StartY=-67 StartZ=0 EndX=35 EndY=-7 EndZ=0
    g3: LineSegment StartX=35 StartY=-7 StartZ=0 EndX=-10 EndY=-7 EndZ=0
    g4: LineSegment StartX=40 StartY=-67 StartZ=0 EndX=165 EndY=-67 EndZ=0
    g5: LineSegment StartX=165 StartY=-67 StartZ=0 EndX=165 EndY=-7 EndZ=0
    g6: LineSegment StartX=165 StartY=-7 StartZ=0 EndX=40 EndY=-7 EndZ=0
    g7: LineSegment StartX=40 StartY=-7 StartZ=0 EndX=40 EndY=-67 EndZ=0
    g8: LineSegment StartX=170 StartY=-67 StartZ=0 EndX=300 EndY=-67 EndZ=0
    g9: LineSegment StartX=300 StartY=-67 StartZ=0 EndX=300 EndY=-7 EndZ=0
    g10: LineSegment StartX=300 StartY=-7 StartZ=0 EndX=170 EndY=-7 EndZ=0
    g11: LineSegment StartX=170 StartY=-7 StartZ=0 EndX=170 EndY=-67 EndZ=0
  constraints (36):
    c: Coincident(g0,g1)
    c: Coincident(g1,g2)
    c: Coincident(g2,g3)
    c: Coincident(g3,g0)
    c: Vertical(g0)
    c: Vertical(g2)
    c: Horizontal(g1)
    c: Horizontal(g3)
    c: Coincident(g4,g5)
    c: Coincident(g5,g6)
    c: Coincident(g6,g7)
    c: Coincident(g7,g4)
    c: Horizontal(g4)
    c: Horizontal(g6)
    c: Vertical(g5)
    c: Vertical(g7)
    c: Coincident(g8,g9)
    c: Coincident(g9,g10)
    c: Coincident(g10,g11)
    c: Coincident(g11,g8)
    c: Horizontal(g8)
    c: Horizontal(g10)
    c: Vertical(g9)
    c: Vertical(g11)
    c: DistanceY(g9,g-1) = 7
    c: DistanceY(g5,g-1) = 7
    c: DistanceY(g2,g-1) = 7
    c: Distance(g2,g7) = 5
    c: DistanceX(g0,g-1) = 10
    c: DistanceX(g-1,g9) = 300
    c: DistanceX(g-1,g1) = 35
    c: DistanceX(g-1,g4) = 165
    c: Distance(g5,g11) = 5
    c: DistanceY(g0,g0) = 60
    c: DistanceY(g7,g7) = 60
    c: DistanceY(g11,g11) = 60
FEATURE [PartDesign::Pocket] Pocket100
  BaseFeature = -> Pocket099
  Direction = (0,0,-1)
  Length = 100
  Length2 = 5
  Midplane = true
  Placement = pos=(0,0,0) rot=(1,0,0;1.5708rad)
  Profile = -> Sketch174
  ReferenceAxis = -> Sketch174 [N_Axis]
  Refine = true
  Suppressed = false
  Type = 0
FEATURE [Sketcher::SketchObject] Sketch173
  ArcFitTolerance = 1e-06
  AttachmentSupport = -> [Pocket100]
  FullyConstrained = false
  MakeInternals = false
  MapMode = 5
  Placement = pos=(0,-7,-2.3e-15) rot=(1,0,0;1.5708rad)
  sketch-geometry (60):
    g0: LineSegment StartX=45.884 StartY=17.7219 StartZ=0 EndX=33.93 EndY=-4.65497 EndZ=0
    g1: LineSegment StartX=49.8645 StartY=18.8062 StartZ=0 EndX=37.3312 EndY=-4.65497 EndZ=0
    g2: LineSegment StartX=45.884 StartY=17.7219 StartZ=0 EndX=49.8645 EndY=18.8062 EndZ=0
    g3: LineSegment StartX=33.93 StartY=-4.65497 StartZ=0 EndX=37.3312 EndY=-4.65497 EndZ=0
    g4: ArcOfCircle CenterX=18 CenterY=3 CenterZ=0 NormalX=0 NormalY=0 NormalZ=1 AngleXU=0 Radius=6.5 StartAngle=2.58175 EndAngle=4.38597
    g5: LineSegment StartX=20.6963 StartY=8.91437 StartZ=0 EndX=19.1912 EndY=11.3613 EndZ=0
    g6: LineSegment StartX=12.4923 StartY=6.45183 StartZ=0 EndX=11.7252 EndY=8.2111 EndZ=0
    g7: LineSegment StartX=11.7252 StartY=8.2111 StartZ=0 EndX=19.1912 EndY=11.3613 EndZ=0
    g8: LineSegment StartX=23.9272 StartY=0.331954 StartZ=0 EndX=26.093 EndY=-4.58272 EndZ=0
    g9: LineSegment StartX=15.9158 StartY=-3.15679 StartZ=0 EndX=16.6159 EndY=-4.58272 EndZ=0
    g10: LineSegment StartX=16.6159 StartY=-4.58272 StartZ=0 EndX=26.093 EndY=-4.58272 EndZ=0
    g11: LineSegment StartX=74.8373 StartY=20.9684 StartZ=0 EndX=89.2063 EndY=-4.24973 EndZ=0
    g12: LineSegment StartX=89.2063 StartY=-4.24973 StartZ=0 EndX=92.6591 EndY=-4.24973 EndZ=0
    g13: LineSegment StartX=92.6591 StartY=-4.24973 StartZ=0 EndX=78.184 EndY=21.1546 EndZ=0
    g14: LineSegment StartX=78.184 StartY=21.1546 StartZ=0 EndX=74.8373 EndY=20.9684 EndZ=0
    g15: LineSegment StartX=113.372 StartY=-3.61742 StartZ=0 EndX=125.992 EndY=20.9865 EndZ=0
    g16: LineSegment StartX=125.992 StartY=20.9865 StartZ=0 EndX=129.338 EndY=20.9348 EndZ=0
    g17: LineSegment StartX=129.338 StartY=20.9348 StartZ=0 EndX=116.743 EndY=-3.61742 EndZ=0
    g18: LineSegment StartX=116.743 StartY=-3.61742 StartZ=0 EndX=113.372 EndY=-3.61742 EndZ=0
    g19: LineSegment StartX=156.49 StartY=19.0126 StartZ=0 EndX=171.224 EndY=-2.18705 EndZ=0
    g20: LineSegment StartX=171.224 StartY=-2.18705 StartZ=0 EndX=175.064 EndY=-2.45586 EndZ=0
    g21: LineSegment StartX=175.064 StartY=-2.45586 StartZ=0 EndX=160.386 EndY=18.6636 EndZ=0
    g22: LineSegment StartX=160.386 StartY=18.6636 StartZ=0 EndX=156.49 EndY=19.0126 EndZ=0
    g23: LineSegment StartX=195.991 StartY=-1.14503 StartZ=0 EndX=209.19 EndY=12.3205 EndZ=0
    g24: LineSegment StartX=209.19 StartY=12.3205 StartZ=0 EndX=213.44 EndY=12.3702 EndZ=0
    g25: LineSegment StartX=213.44 StartY=12.3702 StartZ=0 EndX=200.192 EndY=-1.14503 EndZ=0
    g26: LineSegment StartX=200.192 StartY=-1.14503 StartZ=0 EndX=195.991 EndY=-1.14503 EndZ=0
    g27: LineSegment StartX=229.838 StartY=9.19446 StartZ=0 EndX=237.096 EndY=0 EndZ=0
    g28: LineSegment StartX=237.096 StartY=0 StartZ=0 EndX=240.918 EndY=0 EndZ=0
    g29: LineSegment StartX=240.918 StartY=0 StartZ=0 EndX=234.226 EndY=8.47688 EndZ=0
    g30: LineSegment StartX=234.226 StartY=8.47688 StartZ=0 EndX=229.838 EndY=9.19446 EndZ=0
    g31: ArcOfCircle CenterX=18 CenterY=3 CenterZ=0 NormalX=0 NormalY=0 NormalZ=1 AngleXU=0 Radius=6.5 StartAngle=5.86022 EndAngle=7.42624
    g32: Circle CenterX=18 CenterY=3 CenterZ=0 NormalX=0 NormalY=0 NormalZ=1 AngleXU=0 Radius=4.1
    g33: Circle CenterX=60 CenterY=8 CenterZ=0 NormalX=0 NormalY=0 NormalZ=1 AngleXU=0 Radius=4.1
    g34: Circle CenterX=150 CenterY=8 CenterZ=0 NormalX=0 NormalY=0 NormalZ=1 AngleXU=0 Radius=4.1
    g35: ArcOfCircle CenterX=60 CenterY=8 CenterZ=0 NormalX=0 NormalY=0 NormalZ=1 AngleXU=0 Radius=6.5 StartAngle=1.96559 EndAngle=4.3176
    g36: Circle CenterX=185 CenterY=7 CenterZ=0 NormalX=0 NormalY=0 NormalZ=1 AngleXU=0 Radius=4.1
    g37: LineSegment StartX=57.5 StartY=14 StartZ=0 EndX=57.5 EndY=19.5561 EndZ=0
    g38: LineSegment StartX=62.5 StartY=14 StartZ=0 EndX=62.5 EndY=20.0342 EndZ=0
    g39: LineSegment StartX=62.5 StartY=20.0342 StartZ=0 EndX=57.5 EndY=19.5561 EndZ=0
    g40: LineSegment StartX=57.5 StartY=2 StartZ=0 EndX=57.5 EndY=-4.90591 EndZ=0
    g41: LineSegment StartX=57.5 StartY=-4.90591 StartZ=0 EndX=62.5 EndY=-4.90591 EndZ=0
    g42: LineSegment StartX=62.5 StartY=-4.90591 StartZ=0 EndX=62.5 EndY=2 EndZ=0
    g43: ArcOfCircle CenterX=60 CenterY=8 CenterZ=0 NormalX=0 NormalY=0 NormalZ=1 AngleXU=0 Radius=6.5 StartAngle=5.10718 EndAngle=7.45919
    g44: ArcOfCircle CenterX=150 CenterY=8 CenterZ=0 NormalX=0 NormalY=0 NormalZ=1 AngleXU=0 Radius=6.5 StartAngle=1.96559 EndAngle=4.3176
    g45: ArcOfCircle CenterX=185 CenterY=7 CenterZ=0 NormalX=0 NormalY=0 NormalZ=1 AngleXU=0 Radius=6.5 StartAngle=1.96559 EndAngle=4.3176
    g46: LineSegment StartX=147.5 StartY=14 StartZ=0 EndX=147.5 EndY=19.2414 EndZ=0
    g47: LineSegment StartX=147.5 StartY=19.2414 StartZ=0 EndX=152.5 EndY=18.961 EndZ=0
    g48: LineSegment StartX=152.5 StartY=18.961 StartZ=0 EndX=152.5 EndY=14 EndZ=0
    g49: LineSegment StartX=147.5 StartY=2 StartZ=0 EndX=147.5 EndY=-2.5624 EndZ=0
    g50: LineSegment StartX=147.5 StartY=-2.5624 StartZ=0 EndX=152.5 EndY=-2.5624 EndZ=0
    g51: LineSegment StartX=152.5 StartY=-2.5624 StartZ=0 EndX=152.5 EndY=2 EndZ=0
    g52: ArcOfCircle CenterX=150 CenterY=8 CenterZ=0 NormalX=0 NormalY=0 NormalZ=1 AngleXU=0 Radius=6.5 StartAngle=5.10718 EndAngle=7.45919
    g53: LineSegment StartX=182.5 StartY=13 StartZ=0 EndX=182.5 EndY=15.9367 EndZ=0
    g54: LineSegment StartX=182.5 StartY=15.9367 StartZ=0 EndX=187.5 EndY=15.5349 EndZ=0
    g55: LineSegment StartX=187.5 StartY=15.5349 StartZ=0 EndX=187.5 EndY=13 EndZ=0
    g56: LineSegment StartX=182.5 StartY=1 StartZ=0 EndX=182.5 EndY=-1.79994 EndZ=0
    g57: LineSegment StartX=182.5 StartY=-1.79994 StartZ=0 EndX=187.5 EndY=-1.79994 EndZ=0
    g58: LineSegment StartX=187.5 StartY=-1.79994 StartZ=0 EndX=187.5 EndY=1 EndZ=0
    g59: ArcOfCircle CenterX=185 CenterY=7 CenterZ=0 NormalX=0 NormalY=0 NormalZ=1 AngleXU=0 Radius=6.5 StartAngle=5.10718 EndAngle=7.45919
  constraints (134):
    c: Coincident(g2,g0)
    c: Coincident(g2,g1)
    c: Coincident(g3,g0)
    c: Coincident(g3,g1)
    c: Horizontal(g3)
    c: Parallel(g0,g1)
    c: Distance(g1,g0) = 3
    c: Diameter(g4) = 13
    c: DistanceY(g-1,g4) = 3
    c: DistanceX(g-1,g4) = 18
    c: Coincident(g7,g6)
    c: Coincident(g7,g5)
    c: PointOnObject(g8,g31)
    c: Coincident(g10,g9)
    c: Horizontal(g10)
    c: Coincident(g10,g8)
    c: Coincident(g11,g12)
    c: Horizontal(g12)
    c: Coincident(g12,g13)
    c: Coincident(g13,g14)
    c: Coincident(g14,g11)
    c: Parallel(g11,g13)
    c: Distance(g13,g11) = 3
    c: Coincident(g15,g16)
    c: Coincident(g16,g17)
    c: Coincident(g17,g18)
    c: Coincident(g18,g15)
    c: Horizontal(g18)
    c: Parallel(g17,g15)
    c: Distance(g17,g15) = 3
    c: Coincident(g19,g20)
    c: Coincident(g20,g21)
    c: Coincident(g21,g22)
    c: Coincident(g22,g19)
    c: Parallel(g19,g21)
    c: Distance(g21,g19) = 3
    c: Coincident(g23,g24)
    c: Coincident(g24,g25)
    c: Coincident(g25,g26)
    c: Horizontal(g26)
    c: Parallel(g23,g25)
    c: Distance(g25,g23) = 3
    c: PointOnObject(g27,g-1)
    c: Coincident(g27,g28)
    c: PointOnObject(g28,g-1)
    c: Coincident(g28,g29)
    c: Coincident(g29,g30)
    c: Coincident(g30,g27)
    c: Parallel(g27,g29)
    c: Distance(g29,g27) = 3
    c: Coincident(g31,g5)
    c: Coincident(g4,g6)
    c: Equal(g4,g31)
    c: Coincident(g4,g9)
    c: PointOnObject(g31,g8)
    c: Coincident(g4,g31)
    c: Coincident(g26,g23)
    c: Diameter(g32) = 8.2
    c: Coincident(g32,g4)
    c: Diameter(g33) = 8.2
    c: Diameter(g34) = 8.2
    c: DistanceX(g33,g34) = 90
    c: Coincident(g35,g33)
    c: Diameter(g35) = 13
    c: DistanceX(g-1,g33) = 60
    c: DistanceY(g-1,g33) = 8
    c: DistanceY(g-1,g34) = 8
    c: Diameter(g36) = 8.2
    c: DistanceY(g-1,g36) = 7
    c: DistanceX(g-1,g36) = 185
    c: Vertical(g37)
    c: Vertical(g38)
    c: Coincident(g39,g38)
    c: Coincident(g39,g37)
    c: Distance(g38,g37) = 5
    c: DistanceX(g37,g33) = 2.5
    c: Coincident(g40,g41)
    c: Horizontal(g41)
    c: Coincident(g41,g42)
    c: PointOnObject(g42,g43)
    c: Vertical(g40)
    c: Vertical(g42)
    c: DistanceX(g40,g33) = 2.5
    c: DistanceX(g41,g41) = 5
    c: Coincident(g43,g38)
    c: Coincident(g35,g37)
    c: Equal(g35,g43)
    c: Coincident(g35,g40)
    c: PointOnObject(g43,g42)
    c: Coincident(g35,g43)
    c: Diameter(g44) = 13
    c: Coincident(g44,g34)
    c: Diameter(g45) = 13
    c: Coincident(g45,g36)
    c: Vertical(g46)
    c: Coincident(g46,g47)
    c: Coincident(g47,g48)
    c: Vertical(g48)
    c: Vertical(g49)
    c: Coincident(g49,g50)
    c: Horizontal(g50)
    c: Coincident(g50,g51)
    c: PointOnObject(g51,g52)
    c: Vertical(g51)
    c: DistanceX(g50,g50) = 5
    c: DistanceX(g49,g34) = 2.5
    c: Distance(g48,g46) = 5
    c: DistanceX(g46,g34) = 2.5
    c: Coincident(g52,g48)
    c: Coincident(g44,g46)
    c: Equal(g44,g52)
    c: Coincident(g44,g49)
    c: PointOnObject(g52,g51)
    c: Coincident(g44,g52)
    c: Coincident(g53,g54)
    c: Coincident(g54,g55)
    c: Vertical(g55)
    c: Vertical(g56)
    c: Coincident(g56,g57)
    c: Horizontal(g57)
    c: Coincident(g57,g58)
    c: PointOnObject(g58,g59)
    c: Vertical(g58)
    c: Vertical(g53)
    c: Distance(g55,g53) = 5
    c: DistanceX(g53,g36) = 2.5
    c: Distance(g56,g58) = 5
    c: DistanceX(g56,g36) = 2.5
    c: Coincident(g59,g55)
    c: Coincident(g45,g53)
    c: Equal(g45,g59)
    c: Coincident(g45,g56)
    c: PointOnObject(g59,g58)
    c: Coincident(g45,g59)
FEATURE [PartDesign::Pad] Pad072
  BaseFeature = -> Pocket100
  Direction = (0,-1,2e-16)
  Length = 7
  Length2 = 10
  Placement = pos=(0,0,0) rot=(1,0,0;1.5708rad)
  Profile = -> Sketch173
  ReferenceAxis = -> Sketch173 [N_Axis]
  Refine = true
  Reversed = true
  Suppressed = false
  Type = 0
FEATURE [Sketcher::SketchObject] Sketch175
  ArcFitTolerance = 1e-06
  AttachmentSupport = -> [Pad072]
  FullyConstrained = false
  MakeInternals = false
  MapMode = 5
  Placement = pos=(170,0,0) rot=(0.707107,0,0.707107;3.14159rad)
  sketch-geometry (14):
    g0: LineSegment StartX=-2.86242 StartY=8.94149 StartZ=0 EndX=6.44299 EndY=28.05 EndZ=0
    g1: LineSegment StartX=16.796 StartY=49.3097 StartZ=0 EndX=17.6093 EndY=49.3097 EndZ=0
    g2: LineSegment StartX=17.6093 StartY=49.3097 StartZ=0 EndX=17.6093 EndY=46.4118 EndZ=0
    g3: LineSegment StartX=17.6093 StartY=46.4118 StartZ=0 EndX=8.66937 EndY=28.0538 EndZ=0
    g4: LineSegment StartX=-1.3402 StartY=7.49928 StartZ=0 EndX=-2.53265 EndY=7.49928 EndZ=0
    g5: LineSegment StartX=-2.53265 StartY=7.49928 StartZ=0 EndX=-2.86242 EndY=8.94149 EndZ=0
    g6: LineSegment StartX=-1.56722 StartY=48.7925 StartZ=0 EndX=7.5685 EndY=30.3349 EndZ=0
    g7: LineSegment StartX=18.4673 StartY=8.20781 StartZ=0 EndX=16.7969 EndY=7.18146 EndZ=0
    g8: LineSegment StartX=16.7969 StartY=7.18146 StartZ=0 EndX=7.58766 EndY=25.7876 EndZ=0
    g9: LineSegment StartX=-2.2596 StartY=45.768 StartZ=0 EndX=-1.56722 EndY=48.7925 EndZ=0
    g10: LineSegment StartX=8.66937 StartY=28.0538 StartZ=0 EndX=18.4673 EndY=8.20781 EndZ=0
    g11: LineSegment StartX=7.5685 StartY=30.3349 StartZ=0 EndX=16.796 EndY=49.3097 EndZ=0
    g12: LineSegment StartX=6.44299 StartY=28.05 StartZ=0 EndX=-2.2596 EndY=45.768 EndZ=0
    g13: LineSegment StartX=7.58766 StartY=25.7876 StartZ=0 EndX=-1.3402 EndY=7.49928 EndZ=0
  constraints (24):
    c: Coincident(g11,g1)
    c: Horizontal(g1)
    c: Coincident(g1,g2)
    c: Vertical(g2)
    c: Coincident(g2,g3)
    c: Coincident(g13,g4)
    c: Horizontal(g4)
    c: Coincident(g4,g5)
    c: Coincident(g5,g0)
    c: Parallel(g0,g3)
    c: Distance(g3,g0) = 2
    c: Coincident(g10,g7)
    c: Coincident(g7,g8)
    c: Parallel(g8,g6)
    c: Distance(g8,g6) = 2
    c: Coincident(g9,g12)
    c: Coincident(g9,g6)
    c: PointOnObject(g6,g11)
    c: PointOnObject(g0,g12)
    c: PointOnObject(g11,g6)
    c: PointOnObject(g8,g13)
    c: PointOnObject(g12,g0)
    c: Coincident(g3,g10)
    c: PointOnObject(g13,g8)
FEATURE [PartDesign::Pad] Pad073
  BaseFeature = -> Pad072
  Direction = (1,0,-2e-16)
  Length = 5
  Length2 = 10
  Placement = pos=(0,0,0) rot=(1,0,0;1.5708rad)
  Profile = -> Sketch175
  ReferenceAxis = -> Sketch175 [N_Axis]
  Refine = true
  Reversed = true
  Suppressed = false
  Type = 0
FEATURE [Sketcher::SketchObject] Sketch176
  ArcFitTolerance = 1e-06
  AttachmentSupport = -> [Pad073]
  FullyConstrained = false
  MakeInternals = false
  MapMode = 5
  Placement = pos=(35,0,0) rot=(0.707107,0,-0.707107;3.14159rad)
  sketch-geometry (12):
    g0: LineSegment StartX=-17.0415 StartY=48.3111 StartZ=0 EndX=-17.0415 EndY=49.7892 EndZ=0
    g1: LineSegment StartX=-17.0415 StartY=49.7892 StartZ=0 EndX=-15.5583 EndY=49.7892 EndZ=0
    g2: LineSegment StartX=-15.5583 StartY=49.7892 StartZ=0 EndX=5.93029 EndY=8.81738 EndZ=0
    g3: LineSegment StartX=5.93029 StartY=8.81738 StartZ=0 EndX=5.93029 EndY=7.1685 EndZ=0
    g4: LineSegment StartX=5.93029 StartY=7.1685 StartZ=0 EndX=4.5367 EndY=7.1685 EndZ=0
    g5: LineSegment StartX=4.5367 StartY=7.1685 StartZ=0 EndX=-17.0415 EndY=48.3111 EndZ=0
    g6: LineSegment StartX=-17.1124 StartY=7.28835 StartZ=0 EndX=-16.1126 EndY=7.28835 EndZ=0
    g7: LineSegment StartX=-16.1126 StartY=7.28835 StartZ=0 EndX=5.8579 EndY=48.0729 EndZ=0
    g8: LineSegment StartX=5.8579 StartY=48.0729 StartZ=0 EndX=5.97735 EndY=49.7725 EndZ=0
    g9: LineSegment StartX=5.97735 StartY=49.7725 StartZ=0 EndX=4.50171 EndY=49.7725 EndZ=0
    g10: LineSegment StartX=4.50171 StartY=49.7725 StartZ=0 EndX=-17.1124 EndY=9.64961 EndZ=0
    g11: LineSegment StartX=-17.1124 StartY=9.64961 StartZ=0 EndX=-17.1124 EndY=7.28835 EndZ=0
  constraints (23):
    c: Vertical(g0)
    c: Coincident(g0,g1)
    c: Horizontal(g1)
    c: Coincident(g1,g2)
    c: Coincident(g2,g3)
    c: Vertical(g3)
    c: Coincident(g3,g4)
    c: Horizontal(g4)
    c: Coincident(g4,g5)
    c: Coincident(g5,g0)
    c: Parallel(g2,g5)
    c: Distance(g5,g2) = 2
    c: Horizontal(g6)
    c: Coincident(g6,g7)
    c: Coincident(g7,g8)
    c: Coincident(g8,g9)
    c: Horizontal(g9)
    c: Coincident(g9,g10)
    c: Coincident(g10,g11)
    c: Coincident(g11,g6)
    c: Vertical(g11)
    c: Parallel(g10,g7)
    c: Distance(g7,g10) = 2
FEATURE [PartDesign::Pad] Pad074
  BaseFeature = -> Pad073
  Direction = (-1,0,-2e-16)
  Length = 5
  Length2 = 10
  Placement = pos=(0,0,0) rot=(1,0,0;1.5708rad)
  Profile = -> Sketch176
  ReferenceAxis = -> Sketch176 [N_Axis]
  Refine = true
  Reversed = true
  Suppressed = false
  Type = 0
FEATURE [PartDesign::Chamfer] Chamfer004
  Angle = 45
  Base = -> Pad074 [Edge189,Edge188]
  BaseFeature = -> Pad074
  ChamferType = 0
  FlipDirection = false
  Placement = pos=(0,0,0) rot=(1,0,0;1.5708rad)
  Refine = true
  Size = 1
  Size2 = 1
  SupportTransform = false
  Suppressed = false
  UseAllEdges = false
FEATURE [PartDesign::Body] Body036  label="wingspar 002"
  AllowCompound = false
  Group = -> [Sketch170,Pad071,Sketch171,Pocket098,Sketch172,Pocket099,Pocket100,Sketch173,Sketch174,Pad072,Sketch175,Pad073,Sketch176,Pad074,Chamfer004]
  Origin = -> Origin036
  Placement = pos=(0,-50,0) rot=(0,0,1;0rad)
  Tip = -> Chamfer004
FEATURE [Sketcher::SketchObject] Sketch177
  ArcFitTolerance = 1e-06
  AttachmentSupport = -> [XY_Plane006]
  FullyConstrained = true
  MakeInternals = false
  MapMode = 5
  sketch-geometry (12):
    g0: LineSegment StartX=-20 StartY=-7 StartZ=0 EndX=-20 EndY=-117 EndZ=0
    g1: LineSegment StartX=-20 StartY=-117 StartZ=0 EndX=35 EndY=-117 EndZ=0
    g2: LineSegment StartX=35 StartY=-117 StartZ=0 EndX=35 EndY=-7 EndZ=0
    g3: LineSegment StartX=35 StartY=-7 StartZ=0 EndX=-20 EndY=-7 EndZ=0
    g4: LineSegment StartX=40 StartY=-7 StartZ=0 EndX=40 EndY=-117 EndZ=0
    g5: LineSegment StartX=40 StartY=-117 StartZ=0 EndX=165 EndY=-117 EndZ=0
    g6: LineSegment StartX=165 StartY=-117 StartZ=0 EndX=165 EndY=-7 EndZ=0
    g7: LineSegment StartX=165 StartY=-7 StartZ=0 EndX=40 EndY=-7 EndZ=0
    g8: LineSegment StartX=170 StartY=-7 StartZ=0 EndX=170 EndY=-117 EndZ=0
    g9: LineSegment StartX=170 StartY=-117 StartZ=0 EndX=300 EndY=-117 EndZ=0
    g10: LineSegment StartX=300 StartY=-117 StartZ=0 EndX=300 EndY=-7 EndZ=0
    g11: LineSegment StartX=300 StartY=-7 StartZ=0 EndX=170 EndY=-7 EndZ=0
  constraints (36):
    c: Coincident(g0,g1)
    c: Coincident(g1,g2)
    c: Coincident(g2,g3)
    c: Coincident(g3,g0)
    c: Vertical(g0)
    c: Vertical(g2)
    c: Horizontal(g1)
    c: Horizontal(g3)
    c: Coincident(g4,g5)
    c: Coincident(g5,g6)
    c: Coincident(g6,g7)
    c: Coincident(g7,g4)
    c: Vertical(g4)
    c: Vertical(g6)
    c: Horizontal(g5)
    c: Horizontal(g7)
    c: Coincident(g8,g9)
    c: Coincident(g9,g10)
    c: Coincident(g10,g11)
    c: Coincident(g11,g8)
    c: Vertical(g8)
    c: Vertical(g10)
    c: Horizontal(g9)
    c: Horizontal(g11)
    c: DistanceY(g10,g-1) = 7
    c: DistanceY(g6,g-1) = 7
    c: DistanceY(g2,g-1) = 7
    c: DistanceX(g0,g-1) = 20
    c: DistanceY(g0,g0) = 110
    c: Distance(g4,g2) = 5
    c: Distance(g8,g6) = 5
    c: DistanceY(g4,g4) = 110
    c: DistanceY(g8,g8) = 110
    c: DistanceX(g-1,g9) = 300
    c: DistanceX(g-1,g1) = 35
    c: DistanceX(g-1,g5) = 165
FEATURE [PartDesign::Pocket] Pocket101
  BaseFeature = -> Pocket017
  Direction = (0,0,-1)
  Length = 100
  Length2 = 5
  Midplane = true
  Placement = pos=(0,0,0) rot=(1,0,0;1.5708rad)
  Profile = -> Sketch177
  ReferenceAxis = -> Sketch177 [N_Axis]
  Refine = true
  Suppressed = false
  Type = 0
FEATURE [Sketcher::SketchObject] Sketch033
  ArcFitTolerance = 1e-06
  AttachmentSupport = -> [Pocket101]
  FullyConstrained = false
  MakeInternals = false
  MapMode = 5
  Placement = pos=(0,-7,-2.3e-15) rot=(1,0,0;1.5708rad)
  sketch-geometry (60):
    g0: LineSegment StartX=45.884 StartY=17.7219 StartZ=0 EndX=33.93 EndY=-4.65497 EndZ=0
    g1: LineSegment StartX=49.8645 StartY=18.8062 StartZ=0 EndX=37.3312 EndY=-4.65497 EndZ=0
    g2: LineSegment StartX=45.884 StartY=17.7219 StartZ=0 EndX=49.8645 EndY=18.8062 EndZ=0
    g3: LineSegment StartX=33.93 StartY=-4.65497 StartZ=0 EndX=37.3312 EndY=-4.65497 EndZ=0
    g4: ArcOfCircle CenterX=18 CenterY=3 CenterZ=0 NormalX=0 NormalY=0 NormalZ=1 AngleXU=0 Radius=6.5 StartAngle=2.58175 EndAngle=4.38597
    g5: LineSegment StartX=20.6963 StartY=8.91437 StartZ=0 EndX=19.1912 EndY=11.3613 EndZ=0
    g6: LineSegment StartX=12.4923 StartY=6.45183 StartZ=0 EndX=11.7252 EndY=8.2111 EndZ=0
    g7: LineSegment StartX=11.7252 StartY=8.2111 StartZ=0 EndX=19.1912 EndY=11.3613 EndZ=0
    g8: LineSegment StartX=23.9272 StartY=0.331954 StartZ=0 EndX=26.093 EndY=-4.58272 EndZ=0
    g9: LineSegment StartX=15.9158 StartY=-3.15679 StartZ=0 EndX=16.6159 EndY=-4.58272 EndZ=0
    g10: LineSegment StartX=16.6159 StartY=-4.58272 StartZ=0 EndX=26.093 EndY=-4.58272 EndZ=0
    g11: LineSegment StartX=74.8373 StartY=20.9684 StartZ=0 EndX=89.2063 EndY=-4.24973 EndZ=0
    g12: LineSegment StartX=89.2063 StartY=-4.24973 StartZ=0 EndX=92.6591 EndY=-4.24973 EndZ=0
    g13: LineSegment StartX=92.6591 StartY=-4.24973 StartZ=0 EndX=78.184 EndY=21.1546 EndZ=0
    g14: LineSegment StartX=78.184 StartY=21.1546 StartZ=0 EndX=74.8373 EndY=20.9684 EndZ=0
    g15: LineSegment StartX=113.372 StartY=-3.61742 StartZ=0 EndX=125.992 EndY=20.9865 EndZ=0
    g16: LineSegment StartX=125.992 StartY=20.9865 StartZ=0 EndX=129.338 EndY=20.9348 EndZ=0
    g17: LineSegment StartX=129.338 StartY=20.9348 StartZ=0 EndX=116.743 EndY=-3.61742 EndZ=0
    g18: LineSegment StartX=116.743 StartY=-3.61742 StartZ=0 EndX=113.372 EndY=-3.61742 EndZ=0
    g19: LineSegment StartX=156.49 StartY=19.0126 StartZ=0 EndX=171.224 EndY=-2.18705 EndZ=0
    g20: LineSegment StartX=171.224 StartY=-2.18705 StartZ=0 EndX=175.064 EndY=-2.45586 EndZ=0
    g21: LineSegment StartX=175.064 StartY=-2.45586 StartZ=0 EndX=160.386 EndY=18.6636 EndZ=0
    g22: LineSegment StartX=160.386 StartY=18.6636 StartZ=0 EndX=156.49 EndY=19.0126 EndZ=0
    g23: LineSegment StartX=195.991 StartY=-1.14503 StartZ=0 EndX=209.19 EndY=12.3205 EndZ=0
    g24: LineSegment StartX=209.19 StartY=12.3205 StartZ=0 EndX=213.44 EndY=12.3702 EndZ=0
    g25: LineSegment StartX=213.44 StartY=12.3702 StartZ=0 EndX=200.192 EndY=-1.14503 EndZ=0
    g26: LineSegment StartX=200.192 StartY=-1.14503 StartZ=0 EndX=195.991 EndY=-1.14503 EndZ=0
    g27: LineSegment StartX=229.838 StartY=9.19446 StartZ=0 EndX=237.096 EndY=0 EndZ=0
    g28: LineSegment StartX=237.096 StartY=0 StartZ=0 EndX=240.918 EndY=0 EndZ=0
    g29: LineSegment StartX=240.918 StartY=0 StartZ=0 EndX=234.226 EndY=8.47688 EndZ=0
    g30: LineSegment StartX=234.226 StartY=8.47688 StartZ=0 EndX=229.838 EndY=9.19446 EndZ=0
    g31: ArcOfCircle CenterX=18 CenterY=3 CenterZ=0 NormalX=0 NormalY=0 NormalZ=1 AngleXU=0 Radius=6.5 StartAngle=5.86022 EndAngle=7.42624
    g32: Circle CenterX=18 CenterY=3 CenterZ=0 NormalX=0 NormalY=0 NormalZ=1 AngleXU=0 Radius=4.1
    g33: Circle CenterX=60 CenterY=8 CenterZ=0 NormalX=0 NormalY=0 NormalZ=1 AngleXU=0 Radius=4.1
    g34: Circle CenterX=150 CenterY=8 CenterZ=0 NormalX=0 NormalY=0 NormalZ=1 AngleXU=0 Radius=4.1
    g35: ArcOfCircle CenterX=60 CenterY=8 CenterZ=0 NormalX=0 NormalY=0 NormalZ=1 AngleXU=0 Radius=6.5 StartAngle=1.96559 EndAngle=4.3176
    g36: Circle CenterX=185 CenterY=7 CenterZ=0 NormalX=0 NormalY=0 NormalZ=1 AngleXU=0 Radius=4.1
    g37: LineSegment StartX=57.5 StartY=14 StartZ=0 EndX=57.5 EndY=19.5561 EndZ=0
    g38: LineSegment StartX=62.5 StartY=14 StartZ=0 EndX=62.5 EndY=20.0342 EndZ=0
    g39: LineSegment StartX=62.5 StartY=20.0342 StartZ=0 EndX=57.5 EndY=19.5561 EndZ=0
    g40: LineSegment StartX=57.5 StartY=2 StartZ=0 EndX=57.5 EndY=-4.90591 EndZ=0
    g41: LineSegment StartX=57.5 StartY=-4.90591 StartZ=0 EndX=62.5 EndY=-4.90591 EndZ=0
    g42: LineSegment StartX=62.5 StartY=-4.90591 StartZ=0 EndX=62.5 EndY=2 EndZ=0
    g43: ArcOfCircle CenterX=60 CenterY=8 CenterZ=0 NormalX=0 NormalY=0 NormalZ=1 AngleXU=0 Radius=6.5 StartAngle=5.10718 EndAngle=7.45919
    g44: ArcOfCircle CenterX=150 CenterY=8 CenterZ=0 NormalX=0 NormalY=0 NormalZ=1 AngleXU=0 Radius=6.5 StartAngle=1.96559 EndAngle=4.3176
    g45: ArcOfCircle CenterX=185 CenterY=7 CenterZ=0 NormalX=0 NormalY=0 NormalZ=1 AngleXU=0 Radius=6.5 StartAngle=1.96559 EndAngle=4.3176
    g46: LineSegment StartX=147.5 StartY=14 StartZ=0 EndX=147.5 EndY=19.2414 EndZ=0
    g47: LineSegment StartX=147.5 StartY=19.2414 StartZ=0 EndX=152.5 EndY=18.961 EndZ=0
    g48: LineSegment StartX=152.5 StartY=18.961 StartZ=0 EndX=152.5 EndY=14 EndZ=0
    g49: LineSegment StartX=147.5 StartY=2 StartZ=0 EndX=147.5 EndY=-2.5624 EndZ=0
    g50: LineSegment StartX=147.5 StartY=-2.5624 StartZ=0 EndX=152.5 EndY=-2.5624 EndZ=0
    g51: LineSegment StartX=152.5 StartY=-2.5624 StartZ=0 EndX=152.5 EndY=2 EndZ=0
    g52: ArcOfCircle CenterX=150 CenterY=8 CenterZ=0 NormalX=0 NormalY=0 NormalZ=1 AngleXU=0 Radius=6.5 StartAngle=5.10718 EndAngle=7.45919
    g53: LineSegment StartX=182.5 StartY=13 StartZ=0 EndX=182.5 EndY=15.9367 EndZ=0
    g54: LineSegment StartX=182.5 StartY=15.9367 StartZ=0 EndX=187.5 EndY=15.5349 EndZ=0
    g55: LineSegment StartX=187.5 StartY=15.5349 StartZ=0 EndX=187.5 EndY=13 EndZ=0
    g56: LineSegment StartX=182.5 StartY=1 StartZ=0 EndX=182.5 EndY=-1.79994 EndZ=0
    g57: LineSegment StartX=182.5 StartY=-1.79994 StartZ=0 EndX=187.5 EndY=-1.79994 EndZ=0
    g58: LineSegment StartX=187.5 StartY=-1.79994 StartZ=0 EndX=187.5 EndY=1 EndZ=0
    g59: ArcOfCircle CenterX=185 CenterY=7 CenterZ=0 NormalX=0 NormalY=0 NormalZ=1 AngleXU=0 Radius=6.5 StartAngle=5.10718 EndAngle=7.45919
  constraints (134):
    c: Coincident(g2,g0)
    c: Coincident(g2,g1)
    c: Coincident(g3,g0)
    c: Coincident(g3,g1)
    c: Horizontal(g3)
    c: Parallel(g0,g1)
    c: Distance(g1,g0) = 3
    c: Diameter(g4) = 13
    c: DistanceY(g-1,g4) = 3
    c: DistanceX(g-1,g4) = 18
    c: Coincident(g7,g6)
    c: Coincident(g7,g5)
    c: PointOnObject(g8,g31)
    c: Coincident(g10,g9)
    c: Horizontal(g10)
    c: Coincident(g10,g8)
    c: Coincident(g11,g12)
    c: Horizontal(g12)
    c: Coincident(g12,g13)
    c: Coincident(g13,g14)
    c: Coincident(g14,g11)
    c: Parallel(g11,g13)
    c: Distance(g13,g11) = 3
    c: Coincident(g15,g16)
    c: Coincident(g16,g17)
    c: Coincident(g17,g18)
    c: Coincident(g18,g15)
    c: Horizontal(g18)
    c: Parallel(g17,g15)
    c: Distance(g17,g15) = 3
    c: Coincident(g19,g20)
    c: Coincident(g20,g21)
    c: Coincident(g21,g22)
    c: Coincident(g22,g19)
    c: Parallel(g19,g21)
    c: Distance(g21,g19) = 3
    c: Coincident(g23,g24)
    c: Coincident(g24,g25)
    c: Coincident(g25,g26)
    c: Horizontal(g26)
    c: Parallel(g23,g25)
    c: Distance(g25,g23) = 3
    c: PointOnObject(g27,g-1)
    c: Coincident(g27,g28)
    c: PointOnObject(g28,g-1)
    c: Coincident(g28,g29)
    c: Coincident(g29,g30)
    c: Coincident(g30,g27)
    c: Parallel(g27,g29)
    c: Distance(g29,g27) = 3
    c: Coincident(g31,g5)
    c: Coincident(g4,g6)
    c: Equal(g4,g31)
    c: Coincident(g4,g9)
    c: PointOnObject(g31,g8)
    c: Coincident(g4,g31)
    c: Coincident(g26,g23)
    c: Diameter(g32) = 8.2
    c: Coincident(g32,g4)
    c: Diameter(g33) = 8.2
    c: Diameter(g34) = 8.2
    c: DistanceX(g33,g34) = 90
    c: Coincident(g35,g33)
    c: Diameter(g35) = 13
    c: DistanceX(g-1,g33) = 60
    c: DistanceY(g-1,g33) = 8
    c: DistanceY(g-1,g34) = 8
    c: Diameter(g36) = 8.2
    c: DistanceY(g-1,g36) = 7
    c: DistanceX(g-1,g36) = 185
    c: Vertical(g37)
    c: Vertical(g38)
    c: Coincident(g39,g38)
    c: Coincident(g39,g37)
    c: Distance(g38,g37) = 5
    c: DistanceX(g37,g33) = 2.5
    c: Coincident(g40,g41)
    c: Horizontal(g41)
    c: Coincident(g41,g42)
    c: PointOnObject(g42,g43)
    c: Vertical(g40)
    c: Vertical(g42)
    c: DistanceX(g40,g33) = 2.5
    c: DistanceX(g41,g41) = 5
    c: Coincident(g43,g38)
    c: Coincident(g35,g37)
    c: Equal(g35,g43)
    c: Coincident(g35,g40)
    c: PointOnObject(g43,g42)
    c: Coincident(g35,g43)
    c: Diameter(g44) = 13
    c: Coincident(g44,g34)
    c: Diameter(g45) = 13
    c: Coincident(g45,g36)
    c: Vertical(g46)
    c: Coincident(g46,g47)
    c: Coincident(g47,g48)
    c: Vertical(g48)
    c: Vertical(g49)
    c: Coincident(g49,g50)
    c: Horizontal(g50)
    c: Coincident(g50,g51)
    c: PointOnObject(g51,g52)
    c: Vertical(g51)
    c: DistanceX(g50,g50) = 5
    c: DistanceX(g49,g34) = 2.5
    c: Distance(g48,g46) = 5
    c: DistanceX(g46,g34) = 2.5
    c: Coincident(g52,g48)
    c: Coincident(g44,g46)
    c: Equal(g44,g52)
    c: Coincident(g44,g49)
    c: PointOnObject(g52,g51)
    c: Coincident(g44,g52)
    c: Coincident(g53,g54)
    c: Coincident(g54,g55)
    c: Vertical(g55)
    c: Vertical(g56)
    c: Coincident(g56,g57)
    c: Horizontal(g57)
    c: Coincident(g57,g58)
    c: PointOnObject(g58,g59)
    c: Vertical(g58)
    c: Vertical(g53)
    c: Distance(g55,g53) = 5
    c: DistanceX(g53,g36) = 2.5
    c: Distance(g56,g58) = 5
    c: DistanceX(g56,g36) = 2.5
    c: Coincident(g59,g55)
    c: Coincident(g45,g53)
    c: Equal(g45,g59)
    c: Coincident(g45,g56)
    c: PointOnObject(g59,g58)
    c: Coincident(g45,g59)
FEATURE [PartDesign::Pad] Pad013
  BaseFeature = -> Pocket101
  Direction = (0,-1,2e-16)
  Length = 7
  Length2 = 10
  Placement = pos=(0,0,0) rot=(1,0,0;1.5708rad)
  Profile = -> Sketch033
  ReferenceAxis = -> Sketch033 [N_Axis]
  Refine = true
  Reversed = true
  Suppressed = false
  Type = 0
FEATURE [Sketcher::SketchObject] Sketch178
  ArcFitTolerance = 1e-06
  AttachmentSupport = -> [Pad013]
  FullyConstrained = false
  MakeInternals = false
  MapMode = 5
  Placement = pos=(35,0,0) rot=(0.707107,0,-0.707107;3.14159rad)
  sketch-geometry (25):
    g0: LineSegment [constr] StartX=-33.5639 StartY=50 StartZ=0 EndX=22.3562 EndY=50 EndZ=0
    g1: LineSegment StartX=-17.0984 StartY=50 StartZ=0 EndX=-16.0002 EndY=50 EndZ=0
    g2: LineSegment StartX=-16.0002 StartY=50 StartZ=0 EndX=5.93914 EndY=8.47552 EndZ=0
    g3: LineSegment StartX=5.93914 StartY=8.47552 StartZ=0 EndX=5.96134 EndY=7.0893 EndZ=0
    g4: LineSegment StartX=5.96134 StartY=7.0893 StartZ=0 EndX=4.40956 EndY=7.0893 EndZ=0
    g5: LineSegment StartX=4.40956 StartY=7.0893 StartZ=0 EndX=-17.1228 EndY=47.8435 EndZ=0
    g6: LineSegment StartX=-17.1228 StartY=47.8435 StartZ=0 EndX=-17.0984 EndY=50 EndZ=0
    g7: LineSegment StartX=-17.1293 StartY=7.10705 StartZ=0 EndX=-17.1293 EndY=9.14543 EndZ=0
    g8: LineSegment StartX=-17.1293 StartY=9.14543 StartZ=0 EndX=4.55828 EndY=50 EndZ=0
    g9: LineSegment StartX=4.55828 StartY=50 StartZ=0 EndX=5.87403 EndY=50.0018 EndZ=0
    g10: LineSegment StartX=5.87403 StartY=50.0018 StartZ=0 EndX=5.93974 EndY=48.3369 EndZ=0
    g11: LineSegment StartX=5.93974 StartY=48.3369 StartZ=0 EndX=-15.9471 EndY=7.10705 EndZ=0
    g12: LineSegment StartX=-15.9471 StartY=7.10705 StartZ=0 EndX=-17.1293 EndY=7.10705 EndZ=0
    g13: LineSegment StartX=-17.1358 StartY=50 StartZ=0 EndX=-15.9776 EndY=50.0877 EndZ=0
    g14: LineSegment StartX=-15.9776 StartY=50.0877 StartZ=0 EndX=5.97119 EndY=97.9201 EndZ=0
    g15: LineSegment StartX=5.97119 StartY=97.9201 StartZ=0 EndX=5.97119 EndY=99.8598 EndZ=0
    g16: LineSegment StartX=5.97119 StartY=99.8598 StartZ=0 EndX=4.66077 EndY=99.8598 EndZ=0
    g17: LineSegment StartX=4.66077 StartY=99.8598 StartZ=0 EndX=-17.1358 EndY=52.3592 EndZ=0
    g18: LineSegment StartX=-17.1358 StartY=52.3592 StartZ=0 EndX=-17.1358 EndY=50 EndZ=0
    g19: LineSegment StartX=-15.9576 StartY=99.8854 StartZ=0 EndX=-17.034 EndY=99.8854 EndZ=0
    g20: LineSegment StartX=-17.034 StartY=99.8854 StartZ=0 EndX=-17.0782 EndY=97.5311 EndZ=0
    g21: LineSegment StartX=-17.0782 StartY=97.5311 StartZ=0 EndX=4.71765 EndY=50 EndZ=0
    g22: LineSegment StartX=4.71765 StartY=50 StartZ=0 EndX=5.8275 EndY=50.1579 EndZ=0
    g23: LineSegment StartX=5.8275 StartY=50.1579 StartZ=0 EndX=5.8275 EndY=52.3779 EndZ=0
    g24: LineSegment StartX=5.8275 StartY=52.3779 StartZ=0 EndX=-15.9576 EndY=99.8854 EndZ=0
  constraints (47):
    c: Horizontal(g0)
    c: DistanceY(g-1,g0) = 50
    c: PointOnObject(g1,g0)
    c: Horizontal(g1)
    c: Coincident(g1,g2)
    c: Coincident(g2,g3)
    c: Coincident(g3,g4)
    c: Horizontal(g4)
    c: Coincident(g4,g5)
    c: Coincident(g5,g6)
    c: Vertical(g7)
    c: Coincident(g7,g8)
    c: PointOnObject(g8,g0)
    c: Coincident(g8,g9)
    c: Coincident(g9,g10)
    c: Coincident(g10,g11)
    c: Coincident(g11,g12)
    c: Coincident(g12,g7)
    c: Horizontal(g12)
    c: Parallel(g5,g2)
    c: Parallel(g8,g11)
    c: Distance(g2,g5) = 2
    c: Distance(g8,g11) = 2
    c: Coincident(g6,g1)
    c: PointOnObject(g13,g0)
    c: Coincident(g13,g14)
    c: Coincident(g14,g15)
    c: Vertical(g15)
    c: Coincident(g15,g16)
    c: Horizontal(g16)
    c: Coincident(g16,g17)
    c: Coincident(g17,g18)
    c: Coincident(g18,g13)
    c: Parallel(g17,g14)
    c: Vertical(g18)
    c: Distance(g14,g17) = 2
    c: Horizontal(g19)
    c: Coincident(g19,g20)
    c: Coincident(g20,g21)
    c: PointOnObject(g21,g0)
    c: Coincident(g21,g22)
    c: Coincident(g22,g23)
    c: Vertical(g23)
    c: Coincident(g23,g24)
    c: Coincident(g24,g19)
    c: Parallel(g24,g21)
    c: Distance(g21,g24) = 2
FEATURE [PartDesign::Pad] Pad075
  BaseFeature = -> Pad013
  Direction = (-1,0,-2e-16)
  Length = 5
  Length2 = 10
  Placement = pos=(0,0,0) rot=(1,0,0;1.5708rad)
  Profile = -> Sketch178
  ReferenceAxis = -> Sketch178 [N_Axis]
  Refine = true
  Reversed = true
  Suppressed = false
  Type = 0
FEATURE [Sketcher::SketchObject] Sketch179
  ArcFitTolerance = 1e-06
  AttachmentSupport = -> [Pad075]
  FullyConstrained = false
  MakeInternals = false
  MapMode = 5
  Placement = pos=(170,0,0) rot=(0.707107,0,0.707107;3.14159rad)
  sketch-geometry (25):
    g0: LineSegment [constr] StartX=-9.20711 StartY=50 StartZ=0 EndX=31.5955 EndY=50 EndZ=0
    g1: LineSegment StartX=-3.23071 StartY=7.09197 StartZ=0 EndX=-2.05702 EndY=7.09197 EndZ=0
    g2: LineSegment StartX=-2.05702 StartY=7.09197 StartZ=0 EndX=18.4375 EndY=47.7755 EndZ=0
    g3: LineSegment StartX=18.4375 StartY=47.7755 StartZ=0 EndX=18.4375 EndY=50 EndZ=0
    g4: LineSegment StartX=18.4375 StartY=50 StartZ=0 EndX=17.3084 EndY=49.9795 EndZ=0
    g5: LineSegment StartX=17.3084 StartY=49.9795 StartZ=0 EndX=-3.23071 EndY=9.20758 EndZ=0
    g6: LineSegment StartX=-3.23071 StartY=9.20758 StartZ=0 EndX=-3.23071 EndY=7.09197 EndZ=0
    g7: LineSegment StartX=17.1226 StartY=7.07983 StartZ=0 EndX=18.4953 EndY=7.07983 EndZ=0
    g8: LineSegment StartX=18.4953 StartY=7.07983 StartZ=0 EndX=18.4953 EndY=8.80663 EndZ=0
    g9: LineSegment StartX=18.4953 StartY=8.80663 StartZ=0 EndX=-2.09857 EndY=50 EndZ=0
    g10: LineSegment StartX=-2.09857 StartY=50 StartZ=0 EndX=-3.17562 EndY=49.9159 EndZ=0
    g11: LineSegment StartX=-3.17562 StartY=49.9159 StartZ=0 EndX=-3.17562 EndY=47.6818 EndZ=0
    g12: LineSegment StartX=-3.17562 StartY=47.6818 StartZ=0 EndX=17.1226 EndY=7.07983 EndZ=0
    g13: LineSegment StartX=-3.19345 StartY=99.8693 StartZ=0 EndX=-2.03057 EndY=99.8693 EndZ=0
    g14: LineSegment StartX=-2.03057 StartY=99.8693 StartZ=0 EndX=18.4277 EndY=53.15 EndZ=0
    g15: LineSegment StartX=18.4277 StartY=53.15 StartZ=0 EndX=18.5025 EndY=50 EndZ=0
    g16: LineSegment StartX=18.5025 StartY=50 StartZ=0 EndX=17.5757 EndY=50.1098 EndZ=0
    g17: LineSegment StartX=17.5757 StartY=50.1098 StartZ=0 EndX=-3.19345 EndY=97.5389 EndZ=0
    g18: LineSegment StartX=-3.19345 StartY=97.5389 StartZ=0 EndX=-3.19345 EndY=99.8693 EndZ=0
    g19: LineSegment StartX=-3.22366 StartY=50 StartZ=0 EndX=-3.22366 EndY=52.3177 EndZ=0
    g20: LineSegment StartX=-3.22366 StartY=52.3177 StartZ=0 EndX=17.471 EndY=99.8606 EndZ=0
    g21: LineSegment StartX=17.471 StartY=99.8606 StartZ=0 EndX=18.4521 EndY=99.8606 EndZ=0
    g22: LineSegment StartX=18.4521 StartY=99.8606 StartZ=0 EndX=18.4521 EndY=97.1035 EndZ=0
    g23: LineSegment StartX=18.4521 StartY=97.1035 StartZ=0 EndX=-2.05909 EndY=49.982 EndZ=0
    g24: LineSegment StartX=-2.05909 StartY=49.982 StartZ=0 EndX=-3.22366 EndY=50 EndZ=0
  constraints (49):
    c: Horizontal(g0)
    c: DistanceY(g-1,g0) = 50
    c: Horizontal(g1)
    c: Coincident(g1,g2)
    c: Coincident(g2,g3)
    c: PointOnObject(g3,g0)
    c: Vertical(g3)
    c: Coincident(g3,g4)
    c: Coincident(g4,g5)
    c: Coincident(g5,g6)
    c: Coincident(g6,g1)
    c: Horizontal(g7)
    c: Coincident(g7,g8)
    c: Vertical(g8)
    c: Coincident(g8,g9)
    c: PointOnObject(g9,g0)
    c: Coincident(g9,g10)
    c: Coincident(g10,g11)
    c: Vertical(g11)
    c: Coincident(g11,g12)
    c: Coincident(g12,g7)
    c: Parallel(g9,g12)
    c: Parallel(g5,g2)
    c: Distance(g2,g5) = 2
    c: Distance(g12,g9) = 2
    c: Vertical(g6)
    c: Horizontal(g13)
    c: Coincident(g13,g14)
    c: Coincident(g14,g15)
    c: PointOnObject(g15,g0)
    c: Coincident(g15,g16)
    c: Coincident(g16,g17)
    c: Coincident(g17,g18)
    c: Coincident(g18,g13)
    c: Vertical(g18)
    c: PointOnObject(g19,g0)
    c: Vertical(g19)
    c: Coincident(g19,g20)
    c: Coincident(g20,g21)
    c: Horizontal(g21)
    c: Coincident(g21,g22)
    c: Vertical(g22)
    c: Coincident(g22,g23)
    c: Coincident(g23,g24)
    c: Coincident(g24,g19)
    c: Parallel(g17,g14)
    c: Parallel(g23,g20)
    c: Distance(g23,g20) = 2
    c: Distance(g14,g17) = 2
FEATURE [PartDesign::Pad] Pad076
  BaseFeature = -> Pad075
  Direction = (1,0,-2e-16)
  Length = 5
  Length2 = 10
  Placement = pos=(0,0,0) rot=(1,0,0;1.5708rad)
  Profile = -> Sketch179
  ReferenceAxis = -> Sketch179 [N_Axis]
  Refine = true
  Reversed = true
  Suppressed = false
  Type = 0
FEATURE [Sketcher::SketchObject] Sketch180
  ArcFitTolerance = 1e-06
  FullyConstrained = false
  MakeInternals = false
  Placement = pos=(0,0,0) rot=(1,0,0;1.5708rad)
  sketch-geometry (125):
    g0: BSplineCurve PolesCount=62 KnotsCount=62 Degree=3 IsPeriodic=1
    g1-g62: Circle [constr] x62 (B-spline internal-alignment scaffolding for g0; pole/knot coordinates omitted)
    g63-g124: GeomPoint [constr] x62 (B-spline internal-alignment scaffolding for g0; pole/knot coordinates omitted)
  constraints (125):
    c: InternalAlignment(g1,g0)
    c: Weight(g1) = 1
    c: InternalAlignment(g2,g0)
    c: Equal(g2,g1)
    c: InternalAlignment(g3,g0)
    c: Equal(g3,g1)
    c: InternalAlignment(g4,g0)
    c: Equal(g4,g1)
    c: InternalAlignment(g5,g0)
    c: Equal(g5,g1)
    c: InternalAlignment(g6,g0)
    c: Equal(g6,g1)
    c: InternalAlignment(g7,g0)
    c: Equal(g7,g1)
    c: InternalAlignment(g8,g0)
    c: Equal(g8,g1)
    c: InternalAlignment(g9,g0)
    c: Equal(g9,g1)
    c: InternalAlignment(g10,g0)
    c: Equal(g10,g1)
    c: InternalAlignment(g11,g0)
    c: Equal(g11,g1)
    c: InternalAlignment(g12,g0)
    c: Equal(g12,g1)
    c: InternalAlignment(g13,g0)
    c: Equal(g13,g1)
    c: InternalAlignment(g14,g0)
    c: Equal(g14,g1)
    c: InternalAlignment(g15,g0)
    c: Equal(g15,g1)
    c: InternalAlignment(g16,g0)
    c: Equal(g16,g1)
    c: InternalAlignment(g17,g0)
    c: Equal(g17,g1)
    c: InternalAlignment(g18,g0)
    c: Equal(g18,g1)
    c: InternalAlignment(g19,g0)
    c: Equal(g19,g1)
    c: InternalAlignment(g20,g0)
    c: Equal(g20,g1)
    c: InternalAlignment(g21,g0)
    c: Equal(g21,g1)
    c: InternalAlignment(g22,g0)
    c: Equal(g22,g1)
    c: InternalAlignment(g23,g0)
    c: Equal(g23,g1)
    c: InternalAlignment(g24,g0)
    c: Equal(g24,g1)
    c: InternalAlignment(g25,g0)
    c: Equal(g25,g1)
    c: InternalAlignment(g26,g0)
    c: Equal(g26,g1)
    c: InternalAlignment(g27,g0)
    c: Equal(g27,g1)
    c: InternalAlignment(g28,g0)
    c: Equal(g28,g1)
    c: InternalAlignment(g29,g0)
    c: Equal(g29,g1)
    c: InternalAlignment(g30,g0)
    c: Equal(g30,g1)
    c: InternalAlignment(g31,g0)
    c: Equal(g31,g1)
    c: InternalAlignment(g32,g0)
    c: Equal(g32,g1)
    c: InternalAlignment(g33,g0)
    c: Equal(g33,g1)
    c: InternalAlignment(g34,g0)
    c: Equal(g34,g1)
    c: InternalAlignment(g35,g0)
    c: Equal(g35,g1)
    c: InternalAlignment(g36,g0)
    c: Equal(g36,g1)
    c: InternalAlignment(g37,g0)
    c: Equal(g37,g1)
    c: InternalAlignment(g38,g0)
    c: Equal(g38,g1)
    c: InternalAlignment(g39,g0)
    c: Equal(g39,g1)
    c: InternalAlignment(g40,g0)
    c: Equal(g40,g1)
    c: InternalAlignment(g41,g0)
    c: Equal(g41,g1)
    c: InternalAlignment(g42,g0)
    c: Equal(g42,g1)
    c: InternalAlignment(g43,g0)
    c: Equal(g43,g1)
    c: InternalAlignment(g44,g0)
    c: Equal(g44,g1)
    c: InternalAlignment(g45,g0)
    c: Equal(g45,g1)
    c: InternalAlignment(g46,g0)
    c: Equal(g46,g1)
    c: InternalAlignment(g47,g0)
    c: Equal(g47,g1)
    c: InternalAlignment(g48,g0)
    c: Equal(g48,g1)
    c: InternalAlignment(g49,g0)
    c: Equal(g49,g1)
    c: InternalAlignment(g50,g0)
    c: Equal(g50,g1)
    c: InternalAlignment(g51,g0)
    c: Equal(g51,g1)
    c: InternalAlignment(g52,g0)
    c: Equal(g52,g1)
    c: InternalAlignment(g53,g0)
    c: Equal(g53,g1)
    c: InternalAlignment(g54,g0)
    c: Equal(g54,g1)
    c: InternalAlignment(g55,g0)
    c: Equal(g55,g1)
    c: InternalAlignment(g56,g0)
    c: Equal(g56,g1)
    c: InternalAlignment(g57,g0)
    c: Equal(g57,g1)
    c: InternalAlignment(g58,g0)
    c: Equal(g58,g1)
    c: InternalAlignment(g59,g0)
    c: Equal(g59,g1)
    c: InternalAlignment(g60,g0)
    c: Equal(g60,g1)
    c: InternalAlignment(g61,g0)
    c: Equal(g61,g1)
    c: InternalAlignment(g62,g0)
    c: Equal(g62,g1)
    c: InternalAlignment(g63-g124 -> g0) x62
FEATURE [PartDesign::Pad] Pad077
  Direction = (0,-1,2e-16)
  Length = 99.95
  Length2 = 10
  Placement = pos=(0,0,0) rot=(1,0,0;1.5708rad)
  Profile = -> Sketch180
  ReferenceAxis = -> Sketch180 [N_Axis]
  Refine = true
  Suppressed = false
  Type = 0
FEATURE [Sketcher::SketchObject] Sketch181
  ArcFitTolerance = 1e-06
  AttachmentSupport = -> [Pad077]
  FullyConstrained = false
  MakeInternals = false
  MapMode = 5
  Placement = pos=(0,-99.95,2.2e-14) rot=(1,0,0;1.5708rad)
  sketch-geometry (29):
    g0: LineSegment StartX=2.71326 StartY=0.775372 StartZ=0 EndX=3.3867 EndY=1.52303 EndZ=0
    g1: LineSegment StartX=3.3867 StartY=1.52303 StartZ=0 EndX=5.99321 EndY=4.17962 EndZ=0
    g2: LineSegment StartX=5.99321 StartY=4.17962 StartZ=0 EndX=11.2308 EndY=7.18071 EndZ=0
    g3: LineSegment StartX=11.2308 StartY=7.18071 StartZ=0 EndX=18.9287 EndY=10.4927 EndZ=0
    g4: LineSegment StartX=18.9287 StartY=10.4927 StartZ=0 EndX=30.0156 EndY=13.8045 EndZ=0
    g5: LineSegment StartX=30.0156 StartY=13.8045 StartZ=0 EndX=43.7053 EndY=16.6585 EndZ=0
    g6: LineSegment StartX=43.7053 StartY=16.6585 StartZ=0 EndX=58.3753 EndY=18.5837 EndZ=0
    g7: LineSegment StartX=58.3753 StartY=18.5837 StartZ=0 EndX=81.9328 EndY=20.1998 EndZ=0
    g8: LineSegment StartX=81.9328 StartY=20.1998 StartZ=0 EndX=99.116 EndY=20.5815 EndZ=0
    g9: LineSegment StartX=99.116 StartY=20.5815 StartZ=0 EndX=120.506 EndY=20.1998 EndZ=0
    g10: LineSegment StartX=120.506 StartY=20.1998 StartZ=0 EndX=145.772 EndY=18.6559 EndZ=0
    g11: LineSegment StartX=145.772 StartY=18.6559 StartZ=0 EndX=175.748 EndY=15.7728 EndZ=0
    g12: LineSegment StartX=175.748 StartY=15.7728 StartZ=0 EndX=200.436 EndY=12.5699 EndZ=0
    g13: LineSegment StartX=200.436 StartY=12.5699 StartZ=0 EndX=229.384 EndY=8.60252 EndZ=0
    g14: LineSegment StartX=229.384 StartY=8.60252 StartZ=0 EndX=252.135 EndY=5.21302 EndZ=0
    g15: LineSegment StartX=252.135 StartY=5.21302 StartZ=0 EndX=269.07 EndY=2.67143 EndZ=0
    g16: LineSegment StartX=269.07 StartY=2.67143 StartZ=0 EndX=269.07 EndY=1.39956 EndZ=0
    g17: LineSegment StartX=269.07 StartY=1.39956 StartZ=0 EndX=224.761 EndY=0.436598 EndZ=0
    g18: LineSegment StartX=224.761 StartY=0.436598 StartZ=0 EndX=175.487 EndY=-1.02731 EndZ=0
    g19: LineSegment StartX=175.487 StartY=-1.02731 StartZ=0 EndX=123.478 EndY=-2.41293 EndZ=0
    g20: LineSegment StartX=123.478 StartY=-2.41293 StartZ=0 EndX=62.0775 EndY=-3.87655 EndZ=0
    g21: LineSegment StartX=62.0775 StartY=-3.87655 StartZ=0 EndX=32.0529 EndY=-3.76091 EndZ=0
    g22: LineSegment StartX=32.0529 StartY=-3.76091 StartZ=0 EndX=18.888 EndY=-3.18288 EndZ=0
    g23: LineSegment StartX=18.888 StartY=-3.18288 StartZ=0 EndX=12.7286 EndY=-2.48971 EndZ=0
    g24: LineSegment StartX=12.7286 StartY=-2.48971 StartZ=0 EndX=8.49342 EndY=-1.8722 EndZ=0
    g25: LineSegment StartX=8.49342 StartY=-1.8722 StartZ=0 EndX=4.56236 EndY=-0.768246 EndZ=0
    g26: LineSegment StartX=4.56236 StartY=-0.768246 StartZ=0 EndX=3.01395 EndY=-0.301296 EndZ=0
    g27: ArcOfCircle CenterX=3.20505 CenterY=0.332397 CenterZ=0 NormalX=0 NormalY=0 NormalZ=1 AngleXU=0 Radius=0.661881 StartAngle=2.40837 EndAngle=4.41949
    g28: GeomPoint [constr] X=2.01486 Y=0 Z=0
  constraints (32):
    c: PointOnObject(g28,g-1)
    c: Coincident(g0,g1)
    c: Coincident(g1,g2)
    c: Coincident(g2,g3)
    c: Coincident(g3,g4)
    c: Coincident(g4,g5)
    c: Coincident(g5,g6)
    c: Coincident(g6,g7)
    c: Coincident(g7,g8)
    c: Coincident(g8,g9)
    c: Coincident(g9,g10)
    c: Coincident(g10,g11)
    c: Coincident(g11,g12)
    c: Coincident(g12,g13)
    c: Coincident(g13,g14)
    c: Coincident(g14,g15)
    c: Coincident(g15,g16)
    c: Vertical(g16)
    c: Coincident(g16,g17)
    c: Coincident(g17,g18)
    c: Coincident(g18,g19)
    c: Coincident(g19,g20)
    c: Coincident(g20,g21)
    c: Coincident(g21,g22)
    c: Coincident(g22,g23)
    c: Coincident(g23,g24)
    c: Coincident(g24,g25)
    c: Coincident(g25,g26)
    c: PointOnObject(g28,g0)
    c: PointOnObject(g28,g26)
    c: Tangent(g0,g27) = 1.5708
    c: Tangent(g26,g27) = 1.5708
FEATURE [PartDesign::Pocket] Pocket102
  BaseFeature = -> Pad077
  Direction = (0,1,-2e-16)
  Length = 99.95
  Length2 = 5
  Placement = pos=(0,0,0) rot=(1,0,0;1.5708rad)
  Profile = -> Sketch181
  ReferenceAxis = -> Sketch181 [N_Axis]
  Refine = true
  Suppressed = false
  Type = 0
FEATURE [Sketcher::SketchObject] Sketch182
  ArcFitTolerance = 1e-06
  AttachmentSupport = -> [XY_Plane037]
  FullyConstrained = false
  MakeInternals = false
  MapMode = 5
  sketch-geometry (4):
    g0: LineSegment StartX=295 StartY=17.3691 StartZ=0 EndX=295 EndY=-107.641 EndZ=0
    g1: LineSegment StartX=295 StartY=-107.641 StartZ=0 EndX=389.553 EndY=-107.641 EndZ=0
    g2: LineSegment StartX=389.553 StartY=-107.641 StartZ=0 EndX=389.553 EndY=17.3691 EndZ=0
    g3: LineSegment StartX=389.553 StartY=17.3691 StartZ=0 EndX=295 EndY=17.3691 EndZ=0
  constraints (9):
    c: Coincident(g0,g1)
    c: Coincident(g1,g2)
    c: Coincident(g2,g3)
    c: Coincident(g3,g0)
    c: Vertical(g0)
    c: Vertical(g2)
    c: Horizontal(g1)
    c: Horizontal(g3)
    c: DistanceX(g-1,g0) = 295
FEATURE [PartDesign::Pocket] Pocket103
  BaseFeature = -> Pocket102
  Direction = (0,0,-1)
  Length = 5
  Length2 = 5
  Midplane = true
  Placement = pos=(0,0,0) rot=(1,0,0;1.5708rad)
  Profile = -> Sketch182
  ReferenceAxis = -> Sketch182 [N_Axis]
  Refine = true
  Suppressed = false
  Type = 0
FEATURE [Sketcher::SketchObject] Sketch184
  ArcFitTolerance = 1e-06
  AttachmentSupport = -> [XY_Plane037]
  FullyConstrained = true
  MakeInternals = false
  MapMode = 5
  sketch-geometry (12):
    g0: LineSegment StartX=-20 StartY=-7 StartZ=0 EndX=-20 EndY=-117 EndZ=0
    g1: LineSegment StartX=-20 StartY=-117 StartZ=0 EndX=35 EndY=-117 EndZ=0
    g2: LineSegment StartX=35 StartY=-117 StartZ=0 EndX=35 EndY=-7 EndZ=0
    g3: LineSegment StartX=35 StartY=-7 StartZ=0 EndX=-20 EndY=-7 EndZ=0
    g4: LineSegment StartX=40 StartY=-7 StartZ=0 EndX=40 EndY=-117 EndZ=0
    g5: LineSegment StartX=40 StartY=-117 StartZ=0 EndX=165 EndY=-117 EndZ=0
    g6: LineSegment StartX=165 StartY=-117 StartZ=0 EndX=165 EndY=-7 EndZ=0
    g7: LineSegment StartX=165 StartY=-7 StartZ=0 EndX=40 EndY=-7 EndZ=0
    g8: LineSegment StartX=170 StartY=-7 StartZ=0 EndX=170 EndY=-117 EndZ=0
    g9: LineSegment StartX=170 StartY=-117 StartZ=0 EndX=300 EndY=-117 EndZ=0
    g10: LineSegment StartX=300 StartY=-117 StartZ=0 EndX=300 EndY=-7 EndZ=0
    g11: LineSegment StartX=300 StartY=-7 StartZ=0 EndX=170 EndY=-7 EndZ=0
  constraints (36):
    c: Coincident(g0,g1)
    c: Coincident(g1,g2)
    c: Coincident(g2,g3)
    c: Coincident(g3,g0)
    c: Vertical(g0)
    c: Vertical(g2)
    c: Horizontal(g1)
    c: Horizontal(g3)
    c: Coincident(g4,g5)
    c: Coincident(g5,g6)
    c: Coincident(g6,g7)
    c: Coincident(g7,g4)
    c: Vertical(g4)
    c: Vertical(g6)
    c: Horizontal(g5)
    c: Horizontal(g7)
    c: Coincident(g8,g9)
    c: Coincident(g9,g10)
    c: Coincident(g10,g11)
    c: Coincident(g11,g8)
    c: Vertical(g8)
    c: Vertical(g10)
    c: Horizontal(g9)
    c: Horizontal(g11)
    c: DistanceY(g10,g-1) = 7
    c: DistanceY(g6,g-1) = 7
    c: DistanceY(g2,g-1) = 7
    c: DistanceX(g0,g-1) = 20
    c: DistanceY(g0,g0) = 110
    c: Distance(g4,g2) = 5
    c: Distance(g8,g6) = 5
    c: DistanceY(g4,g4) = 110
    c: DistanceY(g8,g8) = 110
    c: DistanceX(g-1,g9) = 300
    c: DistanceX(g-1,g1) = 35
    c: DistanceX(g-1,g5) = 165
FEATURE [PartDesign::Pocket] Pocket104
  BaseFeature = -> Pocket103
  Direction = (0,0,-1)
  Length = 100
  Length2 = 5
  Midplane = true
  Placement = pos=(0,0,0) rot=(1,0,0;1.5708rad)
  Profile = -> Sketch184
  ReferenceAxis = -> Sketch184 [N_Axis]
  Refine = true
  Suppressed = false
  Type = 0
FEATURE [Sketcher::SketchObject] Sketch183
  ArcFitTolerance = 1e-06
  AttachmentSupport = -> [Pocket104]
  FullyConstrained = false
  MakeInternals = false
  MapMode = 5
  Placement = pos=(0,-7,-2.3e-15) rot=(1,0,0;1.5708rad)
  sketch-geometry (42):
    g0: LineSegment StartX=45.884 StartY=17.7219 StartZ=0 EndX=33.93 EndY=-4.65497 EndZ=0
    g1: LineSegment StartX=49.8645 StartY=18.8062 StartZ=0 EndX=37.3312 EndY=-4.65497 EndZ=0
    g2: LineSegment StartX=45.884 StartY=17.7219 StartZ=0 EndX=49.8645 EndY=18.8062 EndZ=0
    g3: LineSegment StartX=33.93 StartY=-4.65497 StartZ=0 EndX=37.3312 EndY=-4.65497 EndZ=0
    g4: ArcOfCircle CenterX=18 CenterY=3 CenterZ=0 NormalX=0 NormalY=0 NormalZ=1 AngleXU=0 Radius=6.5 StartAngle=2.58175 EndAngle=4.38597
    g5: LineSegment StartX=20.6963 StartY=8.91437 StartZ=0 EndX=19.1912 EndY=11.3613 EndZ=0
    g6: LineSegment StartX=12.4923 StartY=6.45183 StartZ=0 EndX=11.7252 EndY=8.2111 EndZ=0
    g7: LineSegment StartX=11.7252 StartY=8.2111 StartZ=0 EndX=19.1912 EndY=11.3613 EndZ=0
    g8: LineSegment StartX=23.9272 StartY=0.331954 StartZ=0 EndX=26.093 EndY=-4.58272 EndZ=0
    g9: LineSegment StartX=15.9158 StartY=-3.15679 StartZ=0 EndX=16.6159 EndY=-4.58272 EndZ=0
    g10: LineSegment StartX=16.6159 StartY=-4.58272 StartZ=0 EndX=26.093 EndY=-4.58272 EndZ=0
    g11: LineSegment StartX=74.8373 StartY=20.9684 StartZ=0 EndX=89.2063 EndY=-4.24973 EndZ=0
    g12: LineSegment StartX=89.2063 StartY=-4.24973 StartZ=0 EndX=92.6591 EndY=-4.24973 EndZ=0
    g13: LineSegment StartX=92.6591 StartY=-4.24973 StartZ=0 EndX=78.184 EndY=21.1546 EndZ=0
    g14: LineSegment StartX=78.184 StartY=21.1546 StartZ=0 EndX=74.8373 EndY=20.9684 EndZ=0
    g15: LineSegment StartX=113.372 StartY=-3.61742 StartZ=0 EndX=125.992 EndY=20.9865 EndZ=0
    g16: LineSegment StartX=125.992 StartY=20.9865 StartZ=0 EndX=129.338 EndY=20.9348 EndZ=0
    g17: LineSegment StartX=129.338 StartY=20.9348 StartZ=0 EndX=116.743 EndY=-3.61742 EndZ=0
    g18: LineSegment StartX=116.743 StartY=-3.61742 StartZ=0 EndX=113.372 EndY=-3.61742 EndZ=0
    g19: LineSegment StartX=156.49 StartY=19.0126 StartZ=0 EndX=171.224 EndY=-2.18705 EndZ=0
    g20: LineSegment StartX=171.224 StartY=-2.18705 StartZ=0 EndX=175.064 EndY=-2.45586 EndZ=0
    g21: LineSegment StartX=175.064 StartY=-2.45586 StartZ=0 EndX=160.386 EndY=18.6636 EndZ=0
    g22: LineSegment StartX=160.386 StartY=18.6636 StartZ=0 EndX=156.49 EndY=19.0126 EndZ=0
    g23: LineSegment StartX=195.991 StartY=-1.14503 StartZ=0 EndX=209.19 EndY=12.3205 EndZ=0
    g24: LineSegment StartX=209.19 StartY=12.3205 StartZ=0 EndX=213.44 EndY=12.3702 EndZ=0
    g25: LineSegment StartX=213.44 StartY=12.3702 StartZ=0 EndX=200.192 EndY=-1.14503 EndZ=0
    g26: LineSegment StartX=200.192 StartY=-1.14503 StartZ=0 EndX=195.991 EndY=-1.14503 EndZ=0
    g27: LineSegment StartX=229.838 StartY=9.19446 StartZ=0 EndX=237.096 EndY=0 EndZ=0
    g28: LineSegment StartX=237.096 StartY=0 StartZ=0 EndX=240.918 EndY=0 EndZ=0
    g29: LineSegment StartX=240.918 StartY=0 StartZ=0 EndX=234.226 EndY=8.47688 EndZ=0
    g30: LineSegment StartX=234.226 StartY=8.47688 StartZ=0 EndX=229.838 EndY=9.19446 EndZ=0
    g31: ArcOfCircle CenterX=18 CenterY=3 CenterZ=0 NormalX=0 NormalY=0 NormalZ=1 AngleXU=0 Radius=6.5 StartAngle=5.86022 EndAngle=7.42624
    g32: Circle CenterX=18 CenterY=3 CenterZ=0 NormalX=0 NormalY=0 NormalZ=1 AngleXU=0 Radius=4.1
    g33: Circle CenterX=185 CenterY=7 CenterZ=0 NormalX=0 NormalY=0 NormalZ=1 AngleXU=0 Radius=4.1
    g34: ArcOfCircle CenterX=185 CenterY=7 CenterZ=0 NormalX=0 NormalY=0 NormalZ=1 AngleXU=0 Radius=6.5 StartAngle=1.96559 EndAngle=4.3176
    g35: LineSegment StartX=182.5 StartY=13 StartZ=0 EndX=182.5 EndY=15.9367 EndZ=0
    g36: LineSegment StartX=182.5 StartY=15.9367 StartZ=0 EndX=187.5 EndY=15.5349 EndZ=0
    g37: LineSegment StartX=187.5 StartY=15.5349 StartZ=0 EndX=187.5 EndY=13 EndZ=0
    g38: LineSegment StartX=182.5 StartY=1 StartZ=0 EndX=182.5 EndY=-1.79994 EndZ=0
    g39: LineSegment StartX=182.5 StartY=-1.79994 StartZ=0 EndX=187.5 EndY=-1.79994 EndZ=0
    g40: LineSegment StartX=187.5 StartY=-1.79994 StartZ=0 EndX=187.5 EndY=1 EndZ=0
    g41: ArcOfCircle CenterX=185 CenterY=7 CenterZ=0 NormalX=0 NormalY=0 NormalZ=1 AngleXU=0 Radius=6.5 StartAngle=5.10718 EndAngle=7.45919
  constraints (84):
    c: Coincident(g2,g0)
    c: Coincident(g2,g1)
    c: Coincident(g3,g0)
    c: Coincident(g3,g1)
    c: Horizontal(g3)
    c: Parallel(g0,g1)
    c: Distance(g1,g0) = 3
    c: Diameter(g4) = 13
    c: DistanceY(g-1,g4) = 3
    c: DistanceX(g-1,g4) = 18
    c: Coincident(g7,g6)
    c: Coincident(g7,g5)
    c: PointOnObject(g8,g31)
    c: Coincident(g10,g9)
    c: Horizontal(g10)
    c: Coincident(g10,g8)
    c: Coincident(g11,g12)
    c: Horizontal(g12)
    c: Coincident(g12,g13)
    c: Coincident(g13,g14)
    c: Coincident(g14,g11)
    c: Parallel(g11,g13)
    c: Distance(g13,g11) = 3
    c: Coincident(g15,g16)
    c: Coincident(g16,g17)
    c: Coincident(g17,g18)
    c: Coincident(g18,g15)
    c: Horizontal(g18)
    c: Parallel(g17,g15)
    c: Distance(g17,g15) = 3
    c: Coincident(g19,g20)
    c: Coincident(g20,g21)
    c: Coincident(g21,g22)
    c: Coincident(g22,g19)
    c: Parallel(g19,g21)
    c: Distance(g21,g19) = 3
    c: Coincident(g23,g24)
    c: Coincident(g24,g25)
    c: Coincident(g25,g26)
    c: Horizontal(g26)
    c: Parallel(g23,g25)
    c: Distance(g25,g23) = 3
    c: PointOnObject(g27,g-1)
    c: Coincident(g27,g28)
    c: PointOnObject(g28,g-1)
    c: Coincident(g28,g29)
    c: Coincident(g29,g30)
    c: Coincident(g30,g27)
    c: Parallel(g27,g29)
    c: Distance(g29,g27) = 3
    c: Coincident(g31,g5)
    c: Coincident(g4,g6)
    c: Equal(g4,g31)
    c: Coincident(g4,g9)
    c: PointOnObject(g31,g8)
    c: Coincident(g4,g31)
    c: Coincident(g26,g23)
    c: Diameter(g32) = 8.2
    c: Coincident(g32,g4)
    c: Diameter(g33) = 8.2
    c: DistanceY(g-1,g33) = 7
    c: DistanceX(g-1,g33) = 185
    c: Diameter(g34) = 13
    c: Coincident(g34,g33)
    c: Coincident(g35,g36)
    c: Coincident(g36,g37)
    c: Vertical(g37)
    c: Vertical(g38)
    c: Coincident(g38,g39)
    c: Horizontal(g39)
    c: Coincident(g39,g40)
    c: PointOnObject(g40,g41)
    c: Vertical(g40)
    c: Vertical(g35)
    c: Distance(g37,g35) = 5
    c: DistanceX(g35,g33) = 2.5
    c: Distance(g38,g40) = 5
    c: DistanceX(g38,g33) = 2.5
    c: Coincident(g41,g37)
    c: Coincident(g34,g35)
    c: Equal(g34,g41)
    c: Coincident(g34,g38)
    c: PointOnObject(g41,g40)
    c: Coincident(g34,g41)
FEATURE [PartDesign::Pad] Pad078
  BaseFeature = -> Pocket104
  Direction = (0,-1,2e-16)
  Length = 7
  Length2 = 10
  Placement = pos=(0,0,0) rot=(1,0,0;1.5708rad)
  Profile = -> Sketch183
  ReferenceAxis = -> Sketch183 [N_Axis]
  Refine = true
  Reversed = true
  Suppressed = false
  Type = 0
FEATURE [Sketcher::SketchObject] Sketch185
  ArcFitTolerance = 1e-06
  AttachmentSupport = -> [Pad078]
  FullyConstrained = false
  MakeInternals = false
  MapMode = 5
  Placement = pos=(35,0,0) rot=(0.707107,0,-0.707107;3.14159rad)
  sketch-geometry (25):
    g0: LineSegment [constr] StartX=-33.5639 StartY=50 StartZ=0 EndX=22.3562 EndY=50 EndZ=0
    g1: LineSegment StartX=-17.0984 StartY=50 StartZ=0 EndX=-16.0002 EndY=50 EndZ=0
    g2: LineSegment StartX=-16.0002 StartY=50 StartZ=0 EndX=5.93914 EndY=8.47552 EndZ=0
    g3: LineSegment StartX=5.93914 StartY=8.47552 StartZ=0 EndX=5.96134 EndY=7.0893 EndZ=0
    g4: LineSegment StartX=5.96134 StartY=7.0893 StartZ=0 EndX=4.40956 EndY=7.0893 EndZ=0
    g5: LineSegment StartX=4.40956 StartY=7.0893 StartZ=0 EndX=-17.1228 EndY=47.8435 EndZ=0
    g6: LineSegment StartX=-17.1228 StartY=47.8435 StartZ=0 EndX=-17.0984 EndY=50 EndZ=0
    g7: LineSegment StartX=-17.1293 StartY=7.10705 StartZ=0 EndX=-17.1293 EndY=9.14543 EndZ=0
    g8: LineSegment StartX=-17.1293 StartY=9.14543 StartZ=0 EndX=4.55828 EndY=50 EndZ=0
    g9: LineSegment StartX=4.55828 StartY=50 StartZ=0 EndX=5.87403 EndY=50.0018 EndZ=0
    g10: LineSegment StartX=5.87403 StartY=50.0018 StartZ=0 EndX=5.93974 EndY=48.3369 EndZ=0
    g11: LineSegment StartX=5.93974 StartY=48.3369 StartZ=0 EndX=-15.9471 EndY=7.10705 EndZ=0
    g12: LineSegment StartX=-15.9471 StartY=7.10705 StartZ=0 EndX=-17.1293 EndY=7.10705 EndZ=0
    g13: LineSegment StartX=-17.1358 StartY=50 StartZ=0 EndX=-15.9776 EndY=50.0877 EndZ=0
    g14: LineSegment StartX=-15.9776 StartY=50.0877 StartZ=0 EndX=5.97119 EndY=97.9201 EndZ=0
    g15: LineSegment StartX=5.97119 StartY=97.9201 StartZ=0 EndX=5.97119 EndY=99.8598 EndZ=0
    g16: LineSegment StartX=5.97119 StartY=99.8598 StartZ=0 EndX=4.66077 EndY=99.8598 EndZ=0
    g17: LineSegment StartX=4.66077 StartY=99.8598 StartZ=0 EndX=-17.1358 EndY=52.3592 EndZ=0
    g18: LineSegment StartX=-17.1358 StartY=52.3592 StartZ=0 EndX=-17.1358 EndY=50 EndZ=0
    g19: LineSegment StartX=-15.9576 StartY=99.8854 StartZ=0 EndX=-17.034 EndY=99.8854 EndZ=0
    g20: LineSegment StartX=-17.034 StartY=99.8854 StartZ=0 EndX=-17.0782 EndY=97.5311 EndZ=0
    g21: LineSegment StartX=-17.0782 StartY=97.5311 StartZ=0 EndX=4.71765 EndY=50 EndZ=0
    g22: LineSegment StartX=4.71765 StartY=50 StartZ=0 EndX=5.8275 EndY=50.1579 EndZ=0
    g23: LineSegment StartX=5.8275 StartY=50.1579 StartZ=0 EndX=5.8275 EndY=52.3779 EndZ=0
    g24: LineSegment StartX=5.8275 StartY=52.3779 StartZ=0 EndX=-15.9576 EndY=99.8854 EndZ=0
  constraints (47):
    c: Horizontal(g0)
    c: DistanceY(g-1,g0) = 50
    c: PointOnObject(g1,g0)
    c: Horizontal(g1)
    c: Coincident(g1,g2)
    c: Coincident(g2,g3)
    c: Coincident(g3,g4)
    c: Horizontal(g4)
    c: Coincident(g4,g5)
    c: Coincident(g5,g6)
    c: Vertical(g7)
    c: Coincident(g7,g8)
    c: PointOnObject(g8,g0)
    c: Coincident(g8,g9)
    c: Coincident(g9,g10)
    c: Coincident(g10,g11)
    c: Coincident(g11,g12)
    c: Coincident(g12,g7)
    c: Horizontal(g12)
    c: Parallel(g5,g2)
    c: Parallel(g8,g11)
    c: Distance(g2,g5) = 2
    c: Distance(g8,g11) = 2
    c: Coincident(g6,g1)
    c: PointOnObject(g13,g0)
    c: Coincident(g13,g14)
    c: Coincident(g14,g15)
    c: Vertical(g15)
    c: Coincident(g15,g16)
    c: Horizontal(g16)
    c: Coincident(g16,g17)
    c: Coincident(g17,g18)
    c: Coincident(g18,g13)
    c: Parallel(g17,g14)
    c: Vertical(g18)
    c: Distance(g14,g17) = 2
    c: Horizontal(g19)
    c: Coincident(g19,g20)
    c: Coincident(g20,g21)
    c: PointOnObject(g21,g0)
    c: Coincident(g21,g22)
    c: Coincident(g22,g23)
    c: Vertical(g23)
    c: Coincident(g23,g24)
    c: Coincident(g24,g19)
    c: Parallel(g24,g21)
    c: Distance(g21,g24) = 2
FEATURE [PartDesign::Pad] Pad079
  BaseFeature = -> Pad078
  Direction = (-1,0,-2e-16)
  Length = 5
  Length2 = 10
  Placement = pos=(0,0,0) rot=(1,0,0;1.5708rad)
  Profile = -> Sketch185
  ReferenceAxis = -> Sketch185 [N_Axis]
  Refine = true
  Reversed = true
  Suppressed = false
  Type = 0
FEATURE [Sketcher::SketchObject] Sketch186
  ArcFitTolerance = 1e-06
  AttachmentSupport = -> [Pad079]
  FullyConstrained = false
  MakeInternals = false
  MapMode = 5
  Placement = pos=(170,0,0) rot=(0.707107,0,0.707107;3.14159rad)
  sketch-geometry (25):
    g0: LineSegment [constr] StartX=-9.20711 StartY=50 StartZ=0 EndX=31.5955 EndY=50 EndZ=0
    g1: LineSegment StartX=-3.23071 StartY=7.09197 StartZ=0 EndX=-2.05702 EndY=7.09197 EndZ=0
    g2: LineSegment StartX=-2.05702 StartY=7.09197 StartZ=0 EndX=18.4375 EndY=47.7755 EndZ=0
    g3: LineSegment StartX=18.4375 StartY=47.7755 StartZ=0 EndX=18.4375 EndY=50 EndZ=0
    g4: LineSegment StartX=18.4375 StartY=50 StartZ=0 EndX=17.3084 EndY=49.9795 EndZ=0
    g5: LineSegment StartX=17.3084 StartY=49.9795 StartZ=0 EndX=-3.23071 EndY=9.20758 EndZ=0
    g6: LineSegment StartX=-3.23071 StartY=9.20758 StartZ=0 EndX=-3.23071 EndY=7.09197 EndZ=0
    g7: LineSegment StartX=17.1226 StartY=7.07983 StartZ=0 EndX=18.4953 EndY=7.07983 EndZ=0
    g8: LineSegment StartX=18.4953 StartY=7.07983 StartZ=0 EndX=18.4953 EndY=8.80663 EndZ=0
    g9: LineSegment StartX=18.4953 StartY=8.80663 StartZ=0 EndX=-2.09857 EndY=50 EndZ=0
    g10: LineSegment StartX=-2.09857 StartY=50 StartZ=0 EndX=-3.17562 EndY=49.9159 EndZ=0
    g11: LineSegment StartX=-3.17562 StartY=49.9159 StartZ=0 EndX=-3.17562 EndY=47.6818 EndZ=0
    g12: LineSegment StartX=-3.17562 StartY=47.6818 StartZ=0 EndX=17.1226 EndY=7.07983 EndZ=0
    g13: LineSegment StartX=-3.19345 StartY=99.8693 StartZ=0 EndX=-2.03057 EndY=99.8693 EndZ=0
    g14: LineSegment StartX=-2.03057 StartY=99.8693 StartZ=0 EndX=18.4277 EndY=53.15 EndZ=0
    g15: LineSegment StartX=18.4277 StartY=53.15 StartZ=0 EndX=18.5025 EndY=50 EndZ=0
    g16: LineSegment StartX=18.5025 StartY=50 StartZ=0 EndX=17.5757 EndY=50.1098 EndZ=0
    g17: LineSegment StartX=17.5757 StartY=50.1098 StartZ=0 EndX=-3.19345 EndY=97.5389 EndZ=0
    g18: LineSegment StartX=-3.19345 StartY=97.5389 StartZ=0 EndX=-3.19345 EndY=99.8693 EndZ=0
    g19: LineSegment StartX=-3.22366 StartY=50 StartZ=0 EndX=-3.22366 EndY=52.3177 EndZ=0
    g20: LineSegment StartX=-3.22366 StartY=52.3177 StartZ=0 EndX=17.471 EndY=99.8606 EndZ=0
    g21: LineSegment StartX=17.471 StartY=99.8606 StartZ=0 EndX=18.4521 EndY=99.8606 EndZ=0
    g22: LineSegment StartX=18.4521 StartY=99.8606 StartZ=0 EndX=18.4521 EndY=97.1035 EndZ=0
    g23: LineSegment StartX=18.4521 StartY=97.1035 StartZ=0 EndX=-2.05909 EndY=49.982 EndZ=0
    g24: LineSegment StartX=-2.05909 StartY=49.982 StartZ=0 EndX=-3.22366 EndY=50 EndZ=0
  constraints (49):
    c: Horizontal(g0)
    c: DistanceY(g-1,g0) = 50
    c: Horizontal(g1)
    c: Coincident(g1,g2)
    c: Coincident(g2,g3)
    c: PointOnObject(g3,g0)
    c: Vertical(g3)
    c: Coincident(g3,g4)
    c: Coincident(g4,g5)
    c: Coincident(g5,g6)
    c: Coincident(g6,g1)
    c: Horizontal(g7)
    c: Coincident(g7,g8)
    c: Vertical(g8)
    c: Coincident(g8,g9)
    c: PointOnObject(g9,g0)
    c: Coincident(g9,g10)
    c: Coincident(g10,g11)
    c: Vertical(g11)
    c: Coincident(g11,g12)
    c: Coincident(g12,g7)
    c: Parallel(g9,g12)
    c: Parallel(g5,g2)
    c: Distance(g2,g5) = 2
    c: Distance(g12,g9) = 2
    c: Vertical(g6)
    c: Horizontal(g13)
    c: Coincident(g13,g14)
    c: Coincident(g14,g15)
    c: PointOnObject(g15,g0)
    c: Coincident(g15,g16)
    c: Coincident(g16,g17)
    c: Coincident(g17,g18)
    c: Coincident(g18,g13)
    c: Vertical(g18)
    c: PointOnObject(g19,g0)
    c: Vertical(g19)
    c: Coincident(g19,g20)
    c: Coincident(g20,g21)
    c: Horizontal(g21)
    c: Coincident(g21,g22)
    c: Vertical(g22)
    c: Coincident(g22,g23)
    c: Coincident(g23,g24)
    c: Coincident(g24,g19)
    c: Parallel(g17,g14)
    c: Parallel(g23,g20)
    c: Distance(g23,g20) = 2
    c: Distance(g14,g17) = 2
FEATURE [PartDesign::Pad] Pad080
  BaseFeature = -> Pad079
  Direction = (1,0,-2e-16)
  Length = 5
  Length2 = 10
  Placement = pos=(0,0,0) rot=(1,0,0;1.5708rad)
  Profile = -> Sketch186
  ReferenceAxis = -> Sketch186 [N_Axis]
  Refine = true
  Reversed = true
  Suppressed = false
  Type = 0
FEATURE [PartDesign::Body] Body037  label="wingspar 004"
  AllowCompound = false
  Group = -> [Sketch180,Pad077,Sketch181,Pocket102,Sketch182,Pocket103,Pocket104,Sketch183,Pad078,Sketch184,Sketch185,Pad079,Sketch186,Pad080]
  Origin = -> Origin037
  Placement = pos=(0,-200,0) rot=(0,0,1;0rad)
  Tip = -> Pad080
FEATURE [Sketcher::SketchObject] Sketch187
  ArcFitTolerance = 1e-06
  FullyConstrained = false
  MakeInternals = false
  Placement = pos=(0,0,0) rot=(1,0,0;1.5708rad)
  sketch-geometry (125):
    g0: BSplineCurve PolesCount=62 KnotsCount=62 Degree=3 IsPeriodic=1
    g1-g62: Circle [constr] x62 (B-spline internal-alignment scaffolding for g0; pole/knot coordinates omitted)
    g63-g124: GeomPoint [constr] x62 (B-spline internal-alignment scaffolding for g0; pole/knot coordinates omitted)
  constraints (125):
    c: InternalAlignment(g1,g0)
    c: Weight(g1) = 1
    c: InternalAlignment(g2,g0)
    c: Equal(g2,g1)
    c: InternalAlignment(g3,g0)
    c: Equal(g3,g1)
    c: InternalAlignment(g4,g0)
    c: Equal(g4,g1)
    c: InternalAlignment(g5,g0)
    c: Equal(g5,g1)
    c: InternalAlignment(g6,g0)
    c: Equal(g6,g1)
    c: InternalAlignment(g7,g0)
    c: Equal(g7,g1)
    c: InternalAlignment(g8,g0)
    c: Equal(g8,g1)
    c: InternalAlignment(g9,g0)
    c: Equal(g9,g1)
    c: InternalAlignment(g10,g0)
    c: Equal(g10,g1)
    c: InternalAlignment(g11,g0)
    c: Equal(g11,g1)
    c: InternalAlignment(g12,g0)
    c: Equal(g12,g1)
    c: InternalAlignment(g13,g0)
    c: Equal(g13,g1)
    c: InternalAlignment(g14,g0)
    c: Equal(g14,g1)
    c: InternalAlignment(g15,g0)
    c: Equal(g15,g1)
    c: InternalAlignment(g16,g0)
    c: Equal(g16,g1)
    c: InternalAlignment(g17,g0)
    c: Equal(g17,g1)
    c: InternalAlignment(g18,g0)
    c: Equal(g18,g1)
    c: InternalAlignment(g19,g0)
    c: Equal(g19,g1)
    c: InternalAlignment(g20,g0)
    c: Equal(g20,g1)
    c: InternalAlignment(g21,g0)
    c: Equal(g21,g1)
    c: InternalAlignment(g22,g0)
    c: Equal(g22,g1)
    c: InternalAlignment(g23,g0)
    c: Equal(g23,g1)
    c: InternalAlignment(g24,g0)
    c: Equal(g24,g1)
    c: InternalAlignment(g25,g0)
    c: Equal(g25,g1)
    c: InternalAlignment(g26,g0)
    c: Equal(g26,g1)
    c: InternalAlignment(g27,g0)
    c: Equal(g27,g1)
    c: InternalAlignment(g28,g0)
    c: Equal(g28,g1)
    c: InternalAlignment(g29,g0)
    c: Equal(g29,g1)
    c: InternalAlignment(g30,g0)
    c: Equal(g30,g1)
    c: InternalAlignment(g31,g0)
    c: Equal(g31,g1)
    c: InternalAlignment(g32,g0)
    c: Equal(g32,g1)
    c: InternalAlignment(g33,g0)
    c: Equal(g33,g1)
    c: InternalAlignment(g34,g0)
    c: Equal(g34,g1)
    c: InternalAlignment(g35,g0)
    c: Equal(g35,g1)
    c: InternalAlignment(g36,g0)
    c: Equal(g36,g1)
    c: InternalAlignment(g37,g0)
    c: Equal(g37,g1)
    c: InternalAlignment(g38,g0)
    c: Equal(g38,g1)
    c: InternalAlignment(g39,g0)
    c: Equal(g39,g1)
    c: InternalAlignment(g40,g0)
    c: Equal(g40,g1)
    c: InternalAlignment(g41,g0)
    c: Equal(g41,g1)
    c: InternalAlignment(g42,g0)
    c: Equal(g42,g1)
    c: InternalAlignment(g43,g0)
    c: Equal(g43,g1)
    c: InternalAlignment(g44,g0)
    c: Equal(g44,g1)
    c: InternalAlignment(g45,g0)
    c: Equal(g45,g1)
    c: InternalAlignment(g46,g0)
    c: Equal(g46,g1)
    c: InternalAlignment(g47,g0)
    c: Equal(g47,g1)
    c: InternalAlignment(g48,g0)
    c: Equal(g48,g1)
    c: InternalAlignment(g49,g0)
    c: Equal(g49,g1)
    c: InternalAlignment(g50,g0)
    c: Equal(g50,g1)
    c: InternalAlignment(g51,g0)
    c: Equal(g51,g1)
    c: InternalAlignment(g52,g0)
    c: Equal(g52,g1)
    c: InternalAlignment(g53,g0)
    c: Equal(g53,g1)
    c: InternalAlignment(g54,g0)
    c: Equal(g54,g1)
    c: InternalAlignment(g55,g0)
    c: Equal(g55,g1)
    c: InternalAlignment(g56,g0)
    c: Equal(g56,g1)
    c: InternalAlignment(g57,g0)
    c: Equal(g57,g1)
    c: InternalAlignment(g58,g0)
    c: Equal(g58,g1)
    c: InternalAlignment(g59,g0)
    c: Equal(g59,g1)
    c: InternalAlignment(g60,g0)
    c: Equal(g60,g1)
    c: InternalAlignment(g61,g0)
    c: Equal(g61,g1)
    c: InternalAlignment(g62,g0)
    c: Equal(g62,g1)
    c: InternalAlignment(g63-g124 -> g0) x62
FEATURE [PartDesign::Pad] Pad081
  Direction = (0,-1,2e-16)
  Length = 99.95
  Length2 = 10
  Placement = pos=(0,0,0) rot=(1,0,0;1.5708rad)
  Profile = -> Sketch187
  ReferenceAxis = -> Sketch187 [N_Axis]
  Refine = true
  Suppressed = false
  Type = 0
FEATURE [Sketcher::SketchObject] Sketch188
  ArcFitTolerance = 1e-06
  AttachmentSupport = -> [Pad081]
  FullyConstrained = false
  MakeInternals = false
  MapMode = 5
  Placement = pos=(0,-99.95,2.2e-14) rot=(1,0,0;1.5708rad)
  sketch-geometry (29):
    g0: LineSegment StartX=2.71326 StartY=0.775372 StartZ=0 EndX=3.3867 EndY=1.52303 EndZ=0
    g1: LineSegment StartX=3.3867 StartY=1.52303 StartZ=0 EndX=5.99321 EndY=4.17962 EndZ=0
    g2: LineSegment StartX=5.99321 StartY=4.17962 StartZ=0 EndX=11.2308 EndY=7.18071 EndZ=0
    g3: LineSegment StartX=11.2308 StartY=7.18071 StartZ=0 EndX=18.9287 EndY=10.4927 EndZ=0
    g4: LineSegment StartX=18.9287 StartY=10.4927 StartZ=0 EndX=30.0156 EndY=13.8045 EndZ=0
    g5: LineSegment StartX=30.0156 StartY=13.8045 StartZ=0 EndX=43.7053 EndY=16.6585 EndZ=0
    g6: LineSegment StartX=43.7053 StartY=16.6585 StartZ=0 EndX=58.3753 EndY=18.5837 EndZ=0
    g7: LineSegment StartX=58.3753 StartY=18.5837 StartZ=0 EndX=81.9328 EndY=20.1998 EndZ=0
    g8: LineSegment StartX=81.9328 StartY=20.1998 StartZ=0 EndX=99.116 EndY=20.5815 EndZ=0
    g9: LineSegment StartX=99.116 StartY=20.5815 StartZ=0 EndX=120.506 EndY=20.1998 EndZ=0
    g10: LineSegment StartX=120.506 StartY=20.1998 StartZ=0 EndX=145.772 EndY=18.6559 EndZ=0
    g11: LineSegment StartX=145.772 StartY=18.6559 StartZ=0 EndX=175.748 EndY=15.7728 EndZ=0
    g12: LineSegment StartX=175.748 StartY=15.7728 StartZ=0 EndX=200.436 EndY=12.5699 EndZ=0
    g13: LineSegment StartX=200.436 StartY=12.5699 StartZ=0 EndX=229.384 EndY=8.60252 EndZ=0
    g14: LineSegment StartX=229.384 StartY=8.60252 StartZ=0 EndX=252.135 EndY=5.21302 EndZ=0
    g15: LineSegment StartX=252.135 StartY=5.21302 StartZ=0 EndX=269.07 EndY=2.67143 EndZ=0
    g16: LineSegment StartX=269.07 StartY=2.67143 StartZ=0 EndX=269.07 EndY=1.39956 EndZ=0
    g17: LineSegment StartX=269.07 StartY=1.39956 StartZ=0 EndX=224.761 EndY=0.436598 EndZ=0
    g18: LineSegment StartX=224.761 StartY=0.436598 StartZ=0 EndX=175.487 EndY=-1.02731 EndZ=0
    g19: LineSegment StartX=175.487 StartY=-1.02731 StartZ=0 EndX=123.478 EndY=-2.41293 EndZ=0
    g20: LineSegment StartX=123.478 StartY=-2.41293 StartZ=0 EndX=62.0775 EndY=-3.87655 EndZ=0
    g21: LineSegment StartX=62.0775 StartY=-3.87655 StartZ=0 EndX=32.0529 EndY=-3.76091 EndZ=0
    g22: LineSegment StartX=32.0529 StartY=-3.76091 StartZ=0 EndX=18.888 EndY=-3.18288 EndZ=0
    g23: LineSegment StartX=18.888 StartY=-3.18288 StartZ=0 EndX=12.7286 EndY=-2.48971 EndZ=0
    g24: LineSegment StartX=12.7286 StartY=-2.48971 StartZ=0 EndX=8.49342 EndY=-1.8722 EndZ=0
    g25: LineSegment StartX=8.49342 StartY=-1.8722 StartZ=0 EndX=4.56236 EndY=-0.768246 EndZ=0
    g26: LineSegment StartX=4.56236 StartY=-0.768246 StartZ=0 EndX=3.01395 EndY=-0.301296 EndZ=0
    g27: ArcOfCircle CenterX=3.20505 CenterY=0.332397 CenterZ=0 NormalX=0 NormalY=0 NormalZ=1 AngleXU=0 Radius=0.661881 StartAngle=2.40837 EndAngle=4.41949
    g28: GeomPoint [constr] X=2.01486 Y=0 Z=0
  constraints (32):
    c: PointOnObject(g28,g-1)
    c: Coincident(g0,g1)
    c: Coincident(g1,g2)
    c: Coincident(g2,g3)
    c: Coincident(g3,g4)
    c: Coincident(g4,g5)
    c: Coincident(g5,g6)
    c: Coincident(g6,g7)
    c: Coincident(g7,g8)
    c: Coincident(g8,g9)
    c: Coincident(g9,g10)
    c: Coincident(g10,g11)
    c: Coincident(g11,g12)
    c: Coincident(g12,g13)
    c: Coincident(g13,g14)
    c: Coincident(g14,g15)
    c: Coincident(g15,g16)
    c: Vertical(g16)
    c: Coincident(g16,g17)
    c: Coincident(g17,g18)
    c: Coincident(g18,g19)
    c: Coincident(g19,g20)
    c: Coincident(g20,g21)
    c: Coincident(g21,g22)
    c: Coincident(g22,g23)
    c: Coincident(g23,g24)
    c: Coincident(g24,g25)
    c: Coincident(g25,g26)
    c: PointOnObject(g28,g0)
    c: PointOnObject(g28,g26)
    c: Tangent(g0,g27) = 1.5708
    c: Tangent(g26,g27) = 1.5708
FEATURE [PartDesign::Pocket] Pocket105
  BaseFeature = -> Pad081
  Direction = (0,1,-2e-16)
  Length = 99.95
  Length2 = 5
  Placement = pos=(0,0,0) rot=(1,0,0;1.5708rad)
  Profile = -> Sketch188
  ReferenceAxis = -> Sketch188 [N_Axis]
  Refine = true
  Suppressed = false
  Type = 0
FEATURE [Sketcher::SketchObject] Sketch189
  ArcFitTolerance = 1e-06
  AttachmentSupport = -> [XY_Plane038]
  FullyConstrained = false
  MakeInternals = false
  MapMode = 5
  sketch-geometry (4):
    g0: LineSegment StartX=295 StartY=17.3691 StartZ=0 EndX=295 EndY=-107.641 EndZ=0
    g1: LineSegment StartX=295 StartY=-107.641 StartZ=0 EndX=389.553 EndY=-107.641 EndZ=0
    g2: LineSegment StartX=389.553 StartY=-107.641 StartZ=0 EndX=389.553 EndY=17.3691 EndZ=0
    g3: LineSegment StartX=389.553 StartY=17.3691 StartZ=0 EndX=295 EndY=17.3691 EndZ=0
  constraints (9):
    c: Coincident(g0,g1)
    c: Coincident(g1,g2)
    c: Coincident(g2,g3)
    c: Coincident(g3,g0)
    c: Vertical(g0)
    c: Vertical(g2)
    c: Horizontal(g1)
    c: Horizontal(g3)
    c: DistanceX(g-1,g0) = 295
FEATURE [PartDesign::Pocket] Pocket106
  BaseFeature = -> Pocket105
  Direction = (0,0,-1)
  Length = 5
  Length2 = 5
  Midplane = true
  Placement = pos=(0,0,0) rot=(1,0,0;1.5708rad)
  Profile = -> Sketch189
  ReferenceAxis = -> Sketch189 [N_Axis]
  Refine = true
  Suppressed = false
  Type = 0
FEATURE [Sketcher::SketchObject] Sketch191
  ArcFitTolerance = 1e-06
  AttachmentSupport = -> [XY_Plane038]
  FullyConstrained = true
  MakeInternals = false
  MapMode = 5
  sketch-geometry (12):
    g0: LineSegment StartX=-20 StartY=-7 StartZ=0 EndX=-20 EndY=-117 EndZ=0
    g1: LineSegment StartX=-20 StartY=-117 StartZ=0 EndX=35 EndY=-117 EndZ=0
    g2: LineSegment StartX=35 StartY=-117 StartZ=0 EndX=35 EndY=-7 EndZ=0
    g3: LineSegment StartX=35 StartY=-7 StartZ=0 EndX=-20 EndY=-7 EndZ=0
    g4: LineSegment StartX=40 StartY=-7 StartZ=0 EndX=40 EndY=-117 EndZ=0
    g5: LineSegment StartX=40 StartY=-117 StartZ=0 EndX=165 EndY=-117 EndZ=0
    g6: LineSegment StartX=165 StartY=-117 StartZ=0 EndX=165 EndY=-7 EndZ=0
    g7: LineSegment StartX=165 StartY=-7 StartZ=0 EndX=40 EndY=-7 EndZ=0
    g8: LineSegment StartX=170 StartY=-7 StartZ=0 EndX=170 EndY=-117 EndZ=0
    g9: LineSegment StartX=170 StartY=-117 StartZ=0 EndX=300 EndY=-117 EndZ=0
    g10: LineSegment StartX=300 StartY=-117 StartZ=0 EndX=300 EndY=-7 EndZ=0
    g11: LineSegment StartX=300 StartY=-7 StartZ=0 EndX=170 EndY=-7 EndZ=0
  constraints (36):
    c: Coincident(g0,g1)
    c: Coincident(g1,g2)
    c: Coincident(g2,g3)
    c: Coincident(g3,g0)
    c: Vertical(g0)
    c: Vertical(g2)
    c: Horizontal(g1)
    c: Horizontal(g3)
    c: Coincident(g4,g5)
    c: Coincident(g5,g6)
    c: Coincident(g6,g7)
    c: Coincident(g7,g4)
    c: Vertical(g4)
    c: Vertical(g6)
    c: Horizontal(g5)
    c: Horizontal(g7)
    c: Coincident(g8,g9)
    c: Coincident(g9,g10)
    c: Coincident(g10,g11)
    c: Coincident(g11,g8)
    c: Vertical(g8)
    c: Vertical(g10)
    c: Horizontal(g9)
    c: Horizontal(g11)
    c: DistanceY(g10,g-1) = 7
    c: DistanceY(g6,g-1) = 7
    c: DistanceY(g2,g-1) = 7
    c: DistanceX(g0,g-1) = 20
    c: DistanceY(g0,g0) = 110
    c: Distance(g4,g2) = 5
    c: Distance(g8,g6) = 5
    c: DistanceY(g4,g4) = 110
    c: DistanceY(g8,g8) = 110
    c: DistanceX(g-1,g9) = 300
    c: DistanceX(g-1,g1) = 35
    c: DistanceX(g-1,g5) = 165
FEATURE [PartDesign::Pocket] Pocket107
  BaseFeature = -> Pocket106
  Direction = (0,0,-1)
  Length = 100
  Length2 = 5
  Midplane = true
  Placement = pos=(0,0,0) rot=(1,0,0;1.5708rad)
  Profile = -> Sketch191
  ReferenceAxis = -> Sketch191 [N_Axis]
  Refine = true
  Suppressed = false
  Type = 0
FEATURE [Sketcher::SketchObject] Sketch190
  ArcFitTolerance = 1e-06
  AttachmentSupport = -> [Pocket107]
  FullyConstrained = false
  MakeInternals = false
  MapMode = 5
  Placement = pos=(0,-7,-2.3e-15) rot=(1,0,0;1.5708rad)
  sketch-geometry (42):
    g0: LineSegment StartX=45.884 StartY=17.7219 StartZ=0 EndX=33.93 EndY=-4.65497 EndZ=0
    g1: LineSegment StartX=49.8645 StartY=18.8062 StartZ=0 EndX=37.3312 EndY=-4.65497 EndZ=0
    g2: LineSegment StartX=45.884 StartY=17.7219 StartZ=0 EndX=49.8645 EndY=18.8062 EndZ=0
    g3: LineSegment StartX=33.93 StartY=-4.65497 StartZ=0 EndX=37.3312 EndY=-4.65497 EndZ=0
    g4: ArcOfCircle CenterX=18 CenterY=3 CenterZ=0 NormalX=0 NormalY=0 NormalZ=1 AngleXU=0 Radius=6.5 StartAngle=2.58175 EndAngle=4.38597
    g5: LineSegment StartX=20.6963 StartY=8.91437 StartZ=0 EndX=19.1912 EndY=11.3613 EndZ=0
    g6: LineSegment StartX=12.4923 StartY=6.45183 StartZ=0 EndX=11.7252 EndY=8.2111 EndZ=0
    g7: LineSegment StartX=11.7252 StartY=8.2111 StartZ=0 EndX=19.1912 EndY=11.3613 EndZ=0
    g8: LineSegment StartX=23.9272 StartY=0.331954 StartZ=0 EndX=26.093 EndY=-4.58272 EndZ=0
    g9: LineSegment StartX=15.9158 StartY=-3.15679 StartZ=0 EndX=16.6159 EndY=-4.58272 EndZ=0
    g10: LineSegment StartX=16.6159 StartY=-4.58272 StartZ=0 EndX=26.093 EndY=-4.58272 EndZ=0
    g11: LineSegment StartX=74.8373 StartY=20.9684 StartZ=0 EndX=89.2063 EndY=-4.24973 EndZ=0
    g12: LineSegment StartX=89.2063 StartY=-4.24973 StartZ=0 EndX=92.6591 EndY=-4.24973 EndZ=0
    g13: LineSegment StartX=92.6591 StartY=-4.24973 StartZ=0 EndX=78.184 EndY=21.1546 EndZ=0
    g14: LineSegment StartX=78.184 StartY=21.1546 StartZ=0 EndX=74.8373 EndY=20.9684 EndZ=0
    g15: LineSegment StartX=113.372 StartY=-3.61742 StartZ=0 EndX=125.992 EndY=20.9865 EndZ=0
    g16: LineSegment StartX=125.992 StartY=20.9865 StartZ=0 EndX=129.338 EndY=20.9348 EndZ=0
    g17: LineSegment StartX=129.338 StartY=20.9348 StartZ=0 EndX=116.743 EndY=-3.61742 EndZ=0
    g18: LineSegment StartX=116.743 StartY=-3.61742 StartZ=0 EndX=113.372 EndY=-3.61742 EndZ=0
    g19: LineSegment StartX=156.49 StartY=19.0126 StartZ=0 EndX=171.224 EndY=-2.18705 EndZ=0
    g20: LineSegment StartX=171.224 StartY=-2.18705 StartZ=0 EndX=175.064 EndY=-2.45586 EndZ=0
    g21: LineSegment StartX=175.064 StartY=-2.45586 StartZ=0 EndX=160.386 EndY=18.6636 EndZ=0
    g22: LineSegment StartX=160.386 StartY=18.6636 StartZ=0 EndX=156.49 EndY=19.0126 EndZ=0
    g23: LineSegment StartX=195.991 StartY=-1.14503 StartZ=0 EndX=209.19 EndY=12.3205 EndZ=0
    g24: LineSegment StartX=209.19 StartY=12.3205 StartZ=0 EndX=213.44 EndY=12.3702 EndZ=0
    g25: LineSegment StartX=213.44 StartY=12.3702 StartZ=0 EndX=200.192 EndY=-1.14503 EndZ=0
    g26: LineSegment StartX=200.192 StartY=-1.14503 StartZ=0 EndX=195.991 EndY=-1.14503 EndZ=0
    g27: LineSegment StartX=229.838 StartY=9.19446 StartZ=0 EndX=237.096 EndY=0 EndZ=0
    g28: LineSegment StartX=237.096 StartY=0 StartZ=0 EndX=240.918 EndY=0 EndZ=0
    g29: LineSegment StartX=240.918 StartY=0 StartZ=0 EndX=234.226 EndY=8.47688 EndZ=0
    g30: LineSegment StartX=234.226 StartY=8.47688 StartZ=0 EndX=229.838 EndY=9.19446 EndZ=0
    g31: ArcOfCircle CenterX=18 CenterY=3 CenterZ=0 NormalX=0 NormalY=0 NormalZ=1 AngleXU=0 Radius=6.5 StartAngle=5.86022 EndAngle=7.42624
    g32: Circle CenterX=18 CenterY=3 CenterZ=0 NormalX=0 NormalY=0 NormalZ=1 AngleXU=0 Radius=4.1
    g33: Circle CenterX=185 CenterY=7 CenterZ=0 NormalX=0 NormalY=0 NormalZ=1 AngleXU=0 Radius=4.1
    g34: ArcOfCircle CenterX=185 CenterY=7 CenterZ=0 NormalX=0 NormalY=0 NormalZ=1 AngleXU=0 Radius=6.5 StartAngle=1.96559 EndAngle=4.3176
    g35: LineSegment StartX=182.5 StartY=13 StartZ=0 EndX=182.5 EndY=15.9367 EndZ=0
    g36: LineSegment StartX=182.5 StartY=15.9367 StartZ=0 EndX=187.5 EndY=15.5349 EndZ=0
    g37: LineSegment StartX=187.5 StartY=15.5349 StartZ=0 EndX=187.5 EndY=13 EndZ=0
    g38: LineSegment StartX=182.5 StartY=1 StartZ=0 EndX=182.5 EndY=-1.79994 EndZ=0
    g39: LineSegment StartX=182.5 StartY=-1.79994 StartZ=0 EndX=187.5 EndY=-1.79994 EndZ=0
    g40: LineSegment StartX=187.5 StartY=-1.79994 StartZ=0 EndX=187.5 EndY=1 EndZ=0
    g41: ArcOfCircle CenterX=185 CenterY=7 CenterZ=0 NormalX=0 NormalY=0 NormalZ=1 AngleXU=0 Radius=6.5 StartAngle=5.10718 EndAngle=7.45919
  constraints (84):
    c: Coincident(g2,g0)
    c: Coincident(g2,g1)
    c: Coincident(g3,g0)
    c: Coincident(g3,g1)
    c: Horizontal(g3)
    c: Parallel(g0,g1)
    c: Distance(g1,g0) = 3
    c: Diameter(g4) = 13
    c: DistanceY(g-1,g4) = 3
    c: DistanceX(g-1,g4) = 18
    c: Coincident(g7,g6)
    c: Coincident(g7,g5)
    c: PointOnObject(g8,g31)
    c: Coincident(g10,g9)
    c: Horizontal(g10)
    c: Coincident(g10,g8)
    c: Coincident(g11,g12)
    c: Horizontal(g12)
    c: Coincident(g12,g13)
    c: Coincident(g13,g14)
    c: Coincident(g14,g11)
    c: Parallel(g11,g13)
    c: Distance(g13,g11) = 3
    c: Coincident(g15,g16)
    c: Coincident(g16,g17)
    c: Coincident(g17,g18)
    c: Coincident(g18,g15)
    c: Horizontal(g18)
    c: Parallel(g17,g15)
    c: Distance(g17,g15) = 3
    c: Coincident(g19,g20)
    c: Coincident(g20,g21)
    c: Coincident(g21,g22)
    c: Coincident(g22,g19)
    c: Parallel(g19,g21)
    c: Distance(g21,g19) = 3
    c: Coincident(g23,g24)
    c: Coincident(g24,g25)
    c: Coincident(g25,g26)
    c: Horizontal(g26)
    c: Parallel(g23,g25)
    c: Distance(g25,g23) = 3
    c: PointOnObject(g27,g-1)
    c: Coincident(g27,g28)
    c: PointOnObject(g28,g-1)
    c: Coincident(g28,g29)
    c: Coincident(g29,g30)
    c: Coincident(g30,g27)
    c: Parallel(g27,g29)
    c: Distance(g29,g27) = 3
    c: Coincident(g31,g5)
    c: Coincident(g4,g6)
    c: Equal(g4,g31)
    c: Coincident(g4,g9)
    c: PointOnObject(g31,g8)
    c: Coincident(g4,g31)
    c: Coincident(g26,g23)
    c: Diameter(g32) = 8.2
    c: Coincident(g32,g4)
    c: Diameter(g33) = 8.2
    c: DistanceY(g-1,g33) = 7
    c: DistanceX(g-1,g33) = 185
    c: Diameter(g34) = 13
    c: Coincident(g34,g33)
    c: Coincident(g35,g36)
    c: Coincident(g36,g37)
    c: Vertical(g37)
    c: Vertical(g38)
    c: Coincident(g38,g39)
    c: Horizontal(g39)
    c: Coincident(g39,g40)
    c: PointOnObject(g40,g41)
    c: Vertical(g40)
    c: Vertical(g35)
    c: Distance(g37,g35) = 5
    c: DistanceX(g35,g33) = 2.5
    c: Distance(g38,g40) = 5
    c: DistanceX(g38,g33) = 2.5
    c: Coincident(g41,g37)
    c: Coincident(g34,g35)
    c: Equal(g34,g41)
    c: Coincident(g34,g38)
    c: PointOnObject(g41,g40)
    c: Coincident(g34,g41)
FEATURE [PartDesign::Pad] Pad082
  BaseFeature = -> Pocket107
  Direction = (0,-1,2e-16)
  Length = 7
  Length2 = 10
  Placement = pos=(0,0,0) rot=(1,0,0;1.5708rad)
  Profile = -> Sketch190
  ReferenceAxis = -> Sketch190 [N_Axis]
  Refine = true
  Reversed = true
  Suppressed = false
  Type = 0
FEATURE [Sketcher::SketchObject] Sketch192
  ArcFitTolerance = 1e-06
  AttachmentSupport = -> [Pad082]
  FullyConstrained = false
  MakeInternals = false
  MapMode = 5
  Placement = pos=(35,0,0) rot=(0.707107,0,-0.707107;3.14159rad)
  sketch-geometry (25):
    g0: LineSegment [constr] StartX=-33.5639 StartY=50 StartZ=0 EndX=22.3562 EndY=50 EndZ=0
    g1: LineSegment StartX=-17.0984 StartY=50 StartZ=0 EndX=-16.0002 EndY=50 EndZ=0
    g2: LineSegment StartX=-16.0002 StartY=50 StartZ=0 EndX=5.93914 EndY=8.47552 EndZ=0
    g3: LineSegment StartX=5.93914 StartY=8.47552 StartZ=0 EndX=5.96134 EndY=7.0893 EndZ=0
    g4: LineSegment StartX=5.96134 StartY=7.0893 StartZ=0 EndX=4.40956 EndY=7.0893 EndZ=0
    g5: LineSegment StartX=4.40956 StartY=7.0893 StartZ=0 EndX=-17.1228 EndY=47.8435 EndZ=0
    g6: LineSegment StartX=-17.1228 StartY=47.8435 StartZ=0 EndX=-17.0984 EndY=50 EndZ=0
    g7: LineSegment StartX=-17.1293 StartY=7.10705 StartZ=0 EndX=-17.1293 EndY=9.14543 EndZ=0
    g8: LineSegment StartX=-17.1293 StartY=9.14543 StartZ=0 EndX=4.55828 EndY=50 EndZ=0
    g9: LineSegment StartX=4.55828 StartY=50 StartZ=0 EndX=5.87403 EndY=50.0018 EndZ=0
    g10: LineSegment StartX=5.87403 StartY=50.0018 StartZ=0 EndX=5.93974 EndY=48.3369 EndZ=0
    g11: LineSegment StartX=5.93974 StartY=48.3369 StartZ=0 EndX=-15.9471 EndY=7.10705 EndZ=0
    g12: LineSegment StartX=-15.9471 StartY=7.10705 StartZ=0 EndX=-17.1293 EndY=7.10705 EndZ=0
    g13: LineSegment StartX=-17.1358 StartY=50 StartZ=0 EndX=-15.9776 EndY=50.0877 EndZ=0
    g14: LineSegment StartX=-15.9776 StartY=50.0877 StartZ=0 EndX=5.97119 EndY=97.9201 EndZ=0
    g15: LineSegment StartX=5.97119 StartY=97.9201 StartZ=0 EndX=5.97119 EndY=99.8598 EndZ=0
    g16: LineSegment StartX=5.97119 StartY=99.8598 StartZ=0 EndX=4.66077 EndY=99.8598 EndZ=0
    g17: LineSegment StartX=4.66077 StartY=99.8598 StartZ=0 EndX=-17.1358 EndY=52.3592 EndZ=0
    g18: LineSegment StartX=-17.1358 StartY=52.3592 StartZ=0 EndX=-17.1358 EndY=50 EndZ=0
    g19: LineSegment StartX=-15.9576 StartY=99.8854 StartZ=0 EndX=-17.034 EndY=99.8854 EndZ=0
    g20: LineSegment StartX=-17.034 StartY=99.8854 StartZ=0 EndX=-17.0782 EndY=97.5311 EndZ=0
    g21: LineSegment StartX=-17.0782 StartY=97.5311 StartZ=0 EndX=4.71765 EndY=50 EndZ=0
    g22: LineSegment StartX=4.71765 StartY=50 StartZ=0 EndX=5.8275 EndY=50.1579 EndZ=0
    g23: LineSegment StartX=5.8275 StartY=50.1579 StartZ=0 EndX=5.8275 EndY=52.3779 EndZ=0
    g24: LineSegment StartX=5.8275 StartY=52.3779 StartZ=0 EndX=-15.9576 EndY=99.8854 EndZ=0
  constraints (47):
    c: Horizontal(g0)
    c: DistanceY(g-1,g0) = 50
    c: PointOnObject(g1,g0)
    c: Horizontal(g1)
    c: Coincident(g1,g2)
    c: Coincident(g2,g3)
    c: Coincident(g3,g4)
    c: Horizontal(g4)
    c: Coincident(g4,g5)
    c: Coincident(g5,g6)
    c: Vertical(g7)
    c: Coincident(g7,g8)
    c: PointOnObject(g8,g0)
    c: Coincident(g8,g9)
    c: Coincident(g9,g10)
    c: Coincident(g10,g11)
    c: Coincident(g11,g12)
    c: Coincident(g12,g7)
    c: Horizontal(g12)
    c: Parallel(g5,g2)
    c: Parallel(g8,g11)
    c: Distance(g2,g5) = 2
    c: Distance(g8,g11) = 2
    c: Coincident(g6,g1)
    c: PointOnObject(g13,g0)
    c: Coincident(g13,g14)
    c: Coincident(g14,g15)
    c: Vertical(g15)
    c: Coincident(g15,g16)
    c: Horizontal(g16)
    c: Coincident(g16,g17)
    c: Coincident(g17,g18)
    c: Coincident(g18,g13)
    c: Parallel(g17,g14)
    c: Vertical(g18)
    c: Distance(g14,g17) = 2
    c: Horizontal(g19)
    c: Coincident(g19,g20)
    c: Coincident(g20,g21)
    c: PointOnObject(g21,g0)
    c: Coincident(g21,g22)
    c: Coincident(g22,g23)
    c: Vertical(g23)
    c: Coincident(g23,g24)
    c: Coincident(g24,g19)
    c: Parallel(g24,g21)
    c: Distance(g21,g24) = 2
FEATURE [PartDesign::Pad] Pad083
  BaseFeature = -> Pad082
  Direction = (-1,0,-2e-16)
  Length = 5
  Length2 = 10
  Placement = pos=(0,0,0) rot=(1,0,0;1.5708rad)
  Profile = -> Sketch192
  ReferenceAxis = -> Sketch192 [N_Axis]
  Refine = true
  Reversed = true
  Suppressed = false
  Type = 0
FEATURE [Sketcher::SketchObject] Sketch193
  ArcFitTolerance = 1e-06
  AttachmentSupport = -> [Pad083]
  FullyConstrained = false
  MakeInternals = false
  MapMode = 5
  Placement = pos=(170,0,0) rot=(0.707107,0,0.707107;3.14159rad)
  sketch-geometry (25):
    g0: LineSegment [constr] StartX=-9.20711 StartY=50 StartZ=0 EndX=31.5955 EndY=50 EndZ=0
    g1: LineSegment StartX=-3.23071 StartY=7.09197 StartZ=0 EndX=-2.05702 EndY=7.09197 EndZ=0
    g2: LineSegment StartX=-2.05702 StartY=7.09197 StartZ=0 EndX=18.4375 EndY=47.7755 EndZ=0
    g3: LineSegment StartX=18.4375 StartY=47.7755 StartZ=0 EndX=18.4375 EndY=50 EndZ=0
    g4: LineSegment StartX=18.4375 StartY=50 StartZ=0 EndX=17.3084 EndY=49.9795 EndZ=0
    g5: LineSegment StartX=17.3084 StartY=49.9795 StartZ=0 EndX=-3.23071 EndY=9.20758 EndZ=0
    g6: LineSegment StartX=-3.23071 StartY=9.20758 StartZ=0 EndX=-3.23071 EndY=7.09197 EndZ=0
    g7: LineSegment StartX=17.1226 StartY=7.07983 StartZ=0 EndX=18.4953 EndY=7.07983 EndZ=0
    g8: LineSegment StartX=18.4953 StartY=7.07983 StartZ=0 EndX=18.4953 EndY=8.80663 EndZ=0
    g9: LineSegment StartX=18.4953 StartY=8.80663 StartZ=0 EndX=-2.09857 EndY=50 EndZ=0
    g10: LineSegment StartX=-2.09857 StartY=50 StartZ=0 EndX=-3.17562 EndY=49.9159 EndZ=0
    g11: LineSegment StartX=-3.17562 StartY=49.9159 StartZ=0 EndX=-3.17562 EndY=47.6818 EndZ=0
    g12: LineSegment StartX=-3.17562 StartY=47.6818 StartZ=0 EndX=17.1226 EndY=7.07983 EndZ=0
    g13: LineSegment StartX=-3.19345 StartY=99.8693 StartZ=0 EndX=-2.03057 EndY=99.8693 EndZ=0
    g14: LineSegment StartX=-2.03057 StartY=99.8693 StartZ=0 EndX=18.4277 EndY=53.15 EndZ=0
    g15: LineSegment StartX=18.4277 StartY=53.15 StartZ=0 EndX=18.5025 EndY=50 EndZ=0
    g16: LineSegment StartX=18.5025 StartY=50 StartZ=0 EndX=17.5757 EndY=50.1098 EndZ=0
    g17: LineSegment StartX=17.5757 StartY=50.1098 StartZ=0 EndX=-3.19345 EndY=97.5389 EndZ=0
    g18: LineSegment StartX=-3.19345 StartY=97.5389 StartZ=0 EndX=-3.19345 EndY=99.8693 EndZ=0
    g19: LineSegment StartX=-3.22366 StartY=50 StartZ=0 EndX=-3.22366 EndY=52.3177 EndZ=0
    g20: LineSegment StartX=-3.22366 StartY=52.3177 StartZ=0 EndX=17.471 EndY=99.8606 EndZ=0
    g21: LineSegment StartX=17.471 StartY=99.8606 StartZ=0 EndX=18.4521 EndY=99.8606 EndZ=0
    g22: LineSegment StartX=18.4521 StartY=99.8606 StartZ=0 EndX=18.4521 EndY=97.1035 EndZ=0
    g23: LineSegment StartX=18.4521 StartY=97.1035 StartZ=0 EndX=-2.05909 EndY=49.982 EndZ=0
    g24: LineSegment StartX=-2.05909 StartY=49.982 StartZ=0 EndX=-3.22366 EndY=50 EndZ=0
  constraints (49):
    c: Horizontal(g0)
    c: DistanceY(g-1,g0) = 50
    c: Horizontal(g1)
    c: Coincident(g1,g2)
    c: Coincident(g2,g3)
    c: PointOnObject(g3,g0)
    c: Vertical(g3)
    c: Coincident(g3,g4)
    c: Coincident(g4,g5)
    c: Coincident(g5,g6)
    c: Coincident(g6,g1)
    c: Horizontal(g7)
    c: Coincident(g7,g8)
    c: Vertical(g8)
    c: Coincident(g8,g9)
    c: PointOnObject(g9,g0)
    c: Coincident(g9,g10)
    c: Coincident(g10,g11)
    c: Vertical(g11)
    c: Coincident(g11,g12)
    c: Coincident(g12,g7)
    c: Parallel(g9,g12)
    c: Parallel(g5,g2)
    c: Distance(g2,g5) = 2
    c: Distance(g12,g9) = 2
    c: Vertical(g6)
    c: Horizontal(g13)
    c: Coincident(g13,g14)
    c: Coincident(g14,g15)
    c: PointOnObject(g15,g0)
    c: Coincident(g15,g16)
    c: Coincident(g16,g17)
    c: Coincident(g17,g18)
    c: Coincident(g18,g13)
    c: Vertical(g18)
    c: PointOnObject(g19,g0)
    c: Vertical(g19)
    c: Coincident(g19,g20)
    c: Coincident(g20,g21)
    c: Horizontal(g21)
    c: Coincident(g21,g22)
    c: Vertical(g22)
    c: Coincident(g22,g23)
    c: Coincident(g23,g24)
    c: Coincident(g24,g19)
    c: Parallel(g17,g14)
    c: Parallel(g23,g20)
    c: Distance(g23,g20) = 2
    c: Distance(g14,g17) = 2
FEATURE [PartDesign::Pad] Pad084
  BaseFeature = -> Pad083
  Direction = (1,0,-2e-16)
  Length = 5
  Length2 = 10
  Placement = pos=(0,0,0) rot=(1,0,0;1.5708rad)
  Profile = -> Sketch193
  ReferenceAxis = -> Sketch193 [N_Axis]
  Refine = true
  Reversed = true
  Suppressed = false
  Type = 0
FEATURE [PartDesign::Body] Body038  label="wingspar 005"
  AllowCompound = false
  Group = -> [Sketch187,Pad081,Sketch188,Pocket105,Sketch189,Pocket106,Pocket107,Sketch190,Pad082,Sketch191,Sketch192,Pad083,Sketch193,Pad084]
  Origin = -> Origin038
  Placement = pos=(0,-300,0) rot=(0,0,1;0rad)
  Tip = -> Pad084
FEATURE [Sketcher::SketchObject] Sketch194
  ArcFitTolerance = 1e-06
  FullyConstrained = false
  MakeInternals = false
  Placement = pos=(0,0,0) rot=(1,0,0;1.5708rad)
  sketch-geometry (125):
    g0: BSplineCurve PolesCount=62 KnotsCount=62 Degree=3 IsPeriodic=1
    g1-g62: Circle [constr] x62 (B-spline internal-alignment scaffolding for g0; pole/knot coordinates omitted)
    g63-g124: GeomPoint [constr] x62 (B-spline internal-alignment scaffolding for g0; pole/knot coordinates omitted)
  constraints (125):
    c: InternalAlignment(g1,g0)
    c: Weight(g1) = 1
    c: InternalAlignment(g2,g0)
    c: Equal(g2,g1)
    c: InternalAlignment(g3,g0)
    c: Equal(g3,g1)
    c: InternalAlignment(g4,g0)
    c: Equal(g4,g1)
    c: InternalAlignment(g5,g0)
    c: Equal(g5,g1)
    c: InternalAlignment(g6,g0)
    c: Equal(g6,g1)
    c: InternalAlignment(g7,g0)
    c: Equal(g7,g1)
    c: InternalAlignment(g8,g0)
    c: Equal(g8,g1)
    c: InternalAlignment(g9,g0)
    c: Equal(g9,g1)
    c: InternalAlignment(g10,g0)
    c: Equal(g10,g1)
    c: InternalAlignment(g11,g0)
    c: Equal(g11,g1)
    c: InternalAlignment(g12,g0)
    c: Equal(g12,g1)
    c: InternalAlignment(g13,g0)
    c: Equal(g13,g1)
    c: InternalAlignment(g14,g0)
    c: Equal(g14,g1)
    c: InternalAlignment(g15,g0)
    c: Equal(g15,g1)
    c: InternalAlignment(g16,g0)
    c: Equal(g16,g1)
    c: InternalAlignment(g17,g0)
    c: Equal(g17,g1)
    c: InternalAlignment(g18,g0)
    c: Equal(g18,g1)
    c: InternalAlignment(g19,g0)
    c: Equal(g19,g1)
    c: InternalAlignment(g20,g0)
    c: Equal(g20,g1)
    c: InternalAlignment(g21,g0)
    c: Equal(g21,g1)
    c: InternalAlignment(g22,g0)
    c: Equal(g22,g1)
    c: InternalAlignment(g23,g0)
    c: Equal(g23,g1)
    c: InternalAlignment(g24,g0)
    c: Equal(g24,g1)
    c: InternalAlignment(g25,g0)
    c: Equal(g25,g1)
    c: InternalAlignment(g26,g0)
    c: Equal(g26,g1)
    c: InternalAlignment(g27,g0)
    c: Equal(g27,g1)
    c: InternalAlignment(g28,g0)
    c: Equal(g28,g1)
    c: InternalAlignment(g29,g0)
    c: Equal(g29,g1)
    c: InternalAlignment(g30,g0)
    c: Equal(g30,g1)
    c: InternalAlignment(g31,g0)
    c: Equal(g31,g1)
    c: InternalAlignment(g32,g0)
    c: Equal(g32,g1)
    c: InternalAlignment(g33,g0)
    c: Equal(g33,g1)
    c: InternalAlignment(g34,g0)
    c: Equal(g34,g1)
    c: InternalAlignment(g35,g0)
    c: Equal(g35,g1)
    c: InternalAlignment(g36,g0)
    c: Equal(g36,g1)
    c: InternalAlignment(g37,g0)
    c: Equal(g37,g1)
    c: InternalAlignment(g38,g0)
    c: Equal(g38,g1)
    c: InternalAlignment(g39,g0)
    c: Equal(g39,g1)
    c: InternalAlignment(g40,g0)
    c: Equal(g40,g1)
    c: InternalAlignment(g41,g0)
    c: Equal(g41,g1)
    c: InternalAlignment(g42,g0)
    c: Equal(g42,g1)
    c: InternalAlignment(g43,g0)
    c: Equal(g43,g1)
    c: InternalAlignment(g44,g0)
    c: Equal(g44,g1)
    c: InternalAlignment(g45,g0)
    c: Equal(g45,g1)
    c: InternalAlignment(g46,g0)
    c: Equal(g46,g1)
    c: InternalAlignment(g47,g0)
    c: Equal(g47,g1)
    c: InternalAlignment(g48,g0)
    c: Equal(g48,g1)
    c: InternalAlignment(g49,g0)
    c: Equal(g49,g1)
    c: InternalAlignment(g50,g0)
    c: Equal(g50,g1)
    c: InternalAlignment(g51,g0)
    c: Equal(g51,g1)
    c: InternalAlignment(g52,g0)
    c: Equal(g52,g1)
    c: InternalAlignment(g53,g0)
    c: Equal(g53,g1)
    c: InternalAlignment(g54,g0)
    c: Equal(g54,g1)
    c: InternalAlignment(g55,g0)
    c: Equal(g55,g1)
    c: InternalAlignment(g56,g0)
    c: Equal(g56,g1)
    c: InternalAlignment(g57,g0)
    c: Equal(g57,g1)
    c: InternalAlignment(g58,g0)
    c: Equal(g58,g1)
    c: InternalAlignment(g59,g0)
    c: Equal(g59,g1)
    c: InternalAlignment(g60,g0)
    c: Equal(g60,g1)
    c: InternalAlignment(g61,g0)
    c: Equal(g61,g1)
    c: InternalAlignment(g62,g0)
    c: Equal(g62,g1)
    c: InternalAlignment(g63-g124 -> g0) x62
FEATURE [PartDesign::Pad] Pad085
  Direction = (0,-1,2e-16)
  Length = 99.95
  Length2 = 10
  Placement = pos=(0,0,0) rot=(1,0,0;1.5708rad)
  Profile = -> Sketch194
  ReferenceAxis = -> Sketch194 [N_Axis]
  Refine = true
  Suppressed = false
  Type = 0
FEATURE [Sketcher::SketchObject] Sketch195
  ArcFitTolerance = 1e-06
  AttachmentSupport = -> [Pad085]
  FullyConstrained = false
  MakeInternals = false
  MapMode = 5
  Placement = pos=(0,-99.95,2.2e-14) rot=(1,0,0;1.5708rad)
  sketch-geometry (29):
    g0: LineSegment StartX=2.71326 StartY=0.775372 StartZ=0 EndX=3.3867 EndY=1.52303 EndZ=0
    g1: LineSegment StartX=3.3867 StartY=1.52303 StartZ=0 EndX=5.99321 EndY=4.17962 EndZ=0
    g2: LineSegment StartX=5.99321 StartY=4.17962 StartZ=0 EndX=11.2308 EndY=7.18071 EndZ=0
    g3: LineSegment StartX=11.2308 StartY=7.18071 StartZ=0 EndX=18.9287 EndY=10.4927 EndZ=0
    g4: LineSegment StartX=18.9287 StartY=10.4927 StartZ=0 EndX=30.0156 EndY=13.8045 EndZ=0
    g5: LineSegment StartX=30.0156 StartY=13.8045 StartZ=0 EndX=43.7053 EndY=16.6585 EndZ=0
    g6: LineSegment StartX=43.7053 StartY=16.6585 StartZ=0 EndX=58.3753 EndY=18.5837 EndZ=0
    g7: LineSegment StartX=58.3753 StartY=18.5837 StartZ=0 EndX=81.9328 EndY=20.1998 EndZ=0
    g8: LineSegment StartX=81.9328 StartY=20.1998 StartZ=0 EndX=99.116 EndY=20.5815 EndZ=0
    g9: LineSegment StartX=99.116 StartY=20.5815 StartZ=0 EndX=120.506 EndY=20.1998 EndZ=0
    g10: LineSegment StartX=120.506 StartY=20.1998 StartZ=0 EndX=145.772 EndY=18.6559 EndZ=0
    g11: LineSegment StartX=145.772 StartY=18.6559 StartZ=0 EndX=175.748 EndY=15.7728 EndZ=0
    g12: LineSegment StartX=175.748 StartY=15.7728 StartZ=0 EndX=200.436 EndY=12.5699 EndZ=0
    g13: LineSegment StartX=200.436 StartY=12.5699 StartZ=0 EndX=229.384 EndY=8.60252 EndZ=0
    g14: LineSegment StartX=229.384 StartY=8.60252 StartZ=0 EndX=252.135 EndY=5.21302 EndZ=0
    g15: LineSegment StartX=252.135 StartY=5.21302 StartZ=0 EndX=269.07 EndY=2.67143 EndZ=0
    g16: LineSegment StartX=269.07 StartY=2.67143 StartZ=0 EndX=269.07 EndY=1.39956 EndZ=0
    g17: LineSegment StartX=269.07 StartY=1.39956 StartZ=0 EndX=224.761 EndY=0.436598 EndZ=0
    g18: LineSegment StartX=224.761 StartY=0.436598 StartZ=0 EndX=175.487 EndY=-1.02731 EndZ=0
    g19: LineSegment StartX=175.487 StartY=-1.02731 StartZ=0 EndX=123.478 EndY=-2.41293 EndZ=0
    g20: LineSegment StartX=123.478 StartY=-2.41293 StartZ=0 EndX=62.0775 EndY=-3.87655 EndZ=0
    g21: LineSegment StartX=62.0775 StartY=-3.87655 StartZ=0 EndX=32.0529 EndY=-3.76091 EndZ=0
    g22: LineSegment StartX=32.0529 StartY=-3.76091 StartZ=0 EndX=18.888 EndY=-3.18288 EndZ=0
    g23: LineSegment StartX=18.888 StartY=-3.18288 StartZ=0 EndX=12.7286 EndY=-2.48971 EndZ=0
    g24: LineSegment StartX=12.7286 StartY=-2.48971 StartZ=0 EndX=8.49342 EndY=-1.8722 EndZ=0
    g25: LineSegment StartX=8.49342 StartY=-1.8722 StartZ=0 EndX=4.56236 EndY=-0.768246 EndZ=0
    g26: LineSegment StartX=4.56236 StartY=-0.768246 StartZ=0 EndX=3.01395 EndY=-0.301296 EndZ=0
    g27: ArcOfCircle CenterX=3.20505 CenterY=0.332397 CenterZ=0 NormalX=0 NormalY=0 NormalZ=1 AngleXU=0 Radius=0.661881 StartAngle=2.40837 EndAngle=4.41949
    g28: GeomPoint [constr] X=2.01486 Y=0 Z=0
  constraints (32):
    c: PointOnObject(g28,g-1)
    c: Coincident(g0,g1)
    c: Coincident(g1,g2)
    c: Coincident(g2,g3)
    c: Coincident(g3,g4)
    c: Coincident(g4,g5)
    c: Coincident(g5,g6)
    c: Coincident(g6,g7)
    c: Coincident(g7,g8)
    c: Coincident(g8,g9)
    c: Coincident(g9,g10)
    c: Coincident(g10,g11)
    c: Coincident(g11,g12)
    c: Coincident(g12,g13)
    c: Coincident(g13,g14)
    c: Coincident(g14,g15)
    c: Coincident(g15,g16)
    c: Vertical(g16)
    c: Coincident(g16,g17)
    c: Coincident(g17,g18)
    c: Coincident(g18,g19)
    c: Coincident(g19,g20)
    c: Coincident(g20,g21)
    c: Coincident(g21,g22)
    c: Coincident(g22,g23)
    c: Coincident(g23,g24)
    c: Coincident(g24,g25)
    c: Coincident(g25,g26)
    c: PointOnObject(g28,g0)
    c: PointOnObject(g28,g26)
    c: Tangent(g0,g27) = 1.5708
    c: Tangent(g26,g27) = 1.5708
FEATURE [PartDesign::Pocket] Pocket108
  BaseFeature = -> Pad085
  Direction = (0,1,-2e-16)
  Length = 99.95
  Length2 = 5
  Placement = pos=(0,0,0) rot=(1,0,0;1.5708rad)
  Profile = -> Sketch195
  ReferenceAxis = -> Sketch195 [N_Axis]
  Refine = true
  Suppressed = false
  Type = 0
FEATURE [Sketcher::SketchObject] Sketch196
  ArcFitTolerance = 1e-06
  AttachmentSupport = -> [XY_Plane039]
  FullyConstrained = false
  MakeInternals = false
  MapMode = 5
  sketch-geometry (4):
    g0: LineSegment StartX=295 StartY=17.3691 StartZ=0 EndX=295 EndY=-107.641 EndZ=0
    g1: LineSegment StartX=295 StartY=-107.641 StartZ=0 EndX=389.553 EndY=-107.641 EndZ=0
    g2: LineSegment StartX=389.553 StartY=-107.641 StartZ=0 EndX=389.553 EndY=17.3691 EndZ=0
    g3: LineSegment StartX=389.553 StartY=17.3691 StartZ=0 EndX=295 EndY=17.3691 EndZ=0
  constraints (9):
    c: Coincident(g0,g1)
    c: Coincident(g1,g2)
    c: Coincident(g2,g3)
    c: Coincident(g3,g0)
    c: Vertical(g0)
    c: Vertical(g2)
    c: Horizontal(g1)
    c: Horizontal(g3)
    c: DistanceX(g-1,g0) = 295
FEATURE [PartDesign::Pocket] Pocket109
  BaseFeature = -> Pocket108
  Direction = (0,0,-1)
  Length = 5
  Length2 = 5
  Midplane = true
  Placement = pos=(0,0,0) rot=(1,0,0;1.5708rad)
  Profile = -> Sketch196
  ReferenceAxis = -> Sketch196 [N_Axis]
  Refine = true
  Suppressed = false
  Type = 0
FEATURE [Sketcher::SketchObject] Sketch198
  ArcFitTolerance = 1e-06
  AttachmentSupport = -> [XY_Plane039]
  FullyConstrained = true
  MakeInternals = false
  MapMode = 5
  sketch-geometry (12):
    g0: LineSegment StartX=-20 StartY=-7 StartZ=0 EndX=-20 EndY=-117 EndZ=0
    g1: LineSegment StartX=-20 StartY=-117 StartZ=0 EndX=35 EndY=-117 EndZ=0
    g2: LineSegment StartX=35 StartY=-117 StartZ=0 EndX=35 EndY=-7 EndZ=0
    g3: LineSegment StartX=35 StartY=-7 StartZ=0 EndX=-20 EndY=-7 EndZ=0
    g4: LineSegment StartX=40 StartY=-7 StartZ=0 EndX=40 EndY=-117 EndZ=0
    g5: LineSegment StartX=40 StartY=-117 StartZ=0 EndX=165 EndY=-117 EndZ=0
    g6: LineSegment StartX=165 StartY=-117 StartZ=0 EndX=165 EndY=-7 EndZ=0
    g7: LineSegment StartX=165 StartY=-7 StartZ=0 EndX=40 EndY=-7 EndZ=0
    g8: LineSegment StartX=170 StartY=-7 StartZ=0 EndX=170 EndY=-117 EndZ=0
    g9: LineSegment StartX=170 StartY=-117 StartZ=0 EndX=300 EndY=-117 EndZ=0
    g10: LineSegment StartX=300 StartY=-117 StartZ=0 EndX=300 EndY=-7 EndZ=0
    g11: LineSegment StartX=300 StartY=-7 StartZ=0 EndX=170 EndY=-7 EndZ=0
  constraints (36):
    c: Coincident(g0,g1)
    c: Coincident(g1,g2)
    c: Coincident(g2,g3)
    c: Coincident(g3,g0)
    c: Vertical(g0)
    c: Vertical(g2)
    c: Horizontal(g1)
    c: Horizontal(g3)
    c: Coincident(g4,g5)
    c: Coincident(g5,g6)
    c: Coincident(g6,g7)
    c: Coincident(g7,g4)
    c: Vertical(g4)
    c: Vertical(g6)
    c: Horizontal(g5)
    c: Horizontal(g7)
    c: Coincident(g8,g9)
    c: Coincident(g9,g10)
    c: Coincident(g10,g11)
    c: Coincident(g11,g8)
    c: Vertical(g8)
    c: Vertical(g10)
    c: Horizontal(g9)
    c: Horizontal(g11)
    c: DistanceY(g10,g-1) = 7
    c: DistanceY(g6,g-1) = 7
    c: DistanceY(g2,g-1) = 7
    c: DistanceX(g0,g-1) = 20
    c: DistanceY(g0,g0) = 110
    c: Distance(g4,g2) = 5
    c: Distance(g8,g6) = 5
    c: DistanceY(g4,g4) = 110
    c: DistanceY(g8,g8) = 110
    c: DistanceX(g-1,g9) = 300
    c: DistanceX(g-1,g1) = 35
    c: DistanceX(g-1,g5) = 165
FEATURE [PartDesign::Pocket] Pocket110
  BaseFeature = -> Pocket109
  Direction = (0,0,-1)
  Length = 100
  Length2 = 5
  Midplane = true
  Placement = pos=(0,0,0) rot=(1,0,0;1.5708rad)
  Profile = -> Sketch198
  ReferenceAxis = -> Sketch198 [N_Axis]
  Refine = true
  Suppressed = false
  Type = 0
FEATURE [Sketcher::SketchObject] Sketch197
  ArcFitTolerance = 1e-06
  AttachmentSupport = -> [Pocket110]
  FullyConstrained = false
  MakeInternals = false
  MapMode = 5
  Placement = pos=(0,-7,-2.3e-15) rot=(1,0,0;1.5708rad)
  sketch-geometry (42):
    g0: LineSegment StartX=45.884 StartY=17.7219 StartZ=0 EndX=33.93 EndY=-4.65497 EndZ=0
    g1: LineSegment StartX=49.8645 StartY=18.8062 StartZ=0 EndX=37.3312 EndY=-4.65497 EndZ=0
    g2: LineSegment StartX=45.884 StartY=17.7219 StartZ=0 EndX=49.8645 EndY=18.8062 EndZ=0
    g3: LineSegment StartX=33.93 StartY=-4.65497 StartZ=0 EndX=37.3312 EndY=-4.65497 EndZ=0
    g4: ArcOfCircle CenterX=18 CenterY=3 CenterZ=0 NormalX=0 NormalY=0 NormalZ=1 AngleXU=0 Radius=6.5 StartAngle=2.58175 EndAngle=4.38597
    g5: LineSegment StartX=20.6963 StartY=8.91437 StartZ=0 EndX=19.1912 EndY=11.3613 EndZ=0
    g6: LineSegment StartX=12.4923 StartY=6.45183 StartZ=0 EndX=11.7252 EndY=8.2111 EndZ=0
    g7: LineSegment StartX=11.7252 StartY=8.2111 StartZ=0 EndX=19.1912 EndY=11.3613 EndZ=0
    g8: LineSegment StartX=23.9272 StartY=0.331954 StartZ=0 EndX=26.093 EndY=-4.58272 EndZ=0
    g9: LineSegment StartX=15.9158 StartY=-3.15679 StartZ=0 EndX=16.6159 EndY=-4.58272 EndZ=0
    g10: LineSegment StartX=16.6159 StartY=-4.58272 StartZ=0 EndX=26.093 EndY=-4.58272 EndZ=0
    g11: LineSegment StartX=74.8373 StartY=20.9684 StartZ=0 EndX=89.2063 EndY=-4.24973 EndZ=0
    g12: LineSegment StartX=89.2063 StartY=-4.24973 StartZ=0 EndX=92.6591 EndY=-4.24973 EndZ=0
    g13: LineSegment StartX=92.6591 StartY=-4.24973 StartZ=0 EndX=78.184 EndY=21.1546 EndZ=0
    g14: LineSegment StartX=78.184 StartY=21.1546 StartZ=0 EndX=74.8373 EndY=20.9684 EndZ=0
    g15: LineSegment StartX=113.372 StartY=-3.61742 StartZ=0 EndX=125.992 EndY=20.9865 EndZ=0
    g16: LineSegment StartX=125.992 StartY=20.9865 StartZ=0 EndX=129.338 EndY=20.9348 EndZ=0
    g17: LineSegment StartX=129.338 StartY=20.9348 StartZ=0 EndX=116.743 EndY=-3.61742 EndZ=0
    g18: LineSegment StartX=116.743 StartY=-3.61742 StartZ=0 EndX=113.372 EndY=-3.61742 EndZ=0
    g19: LineSegment StartX=156.49 StartY=19.0126 StartZ=0 EndX=171.224 EndY=-2.18705 EndZ=0
    g20: LineSegment StartX=171.224 StartY=-2.18705 StartZ=0 EndX=175.064 EndY=-2.45586 EndZ=0
    g21: LineSegment StartX=175.064 StartY=-2.45586 StartZ=0 EndX=160.386 EndY=18.6636 EndZ=0
    g22: LineSegment StartX=160.386 StartY=18.6636 StartZ=0 EndX=156.49 EndY=19.0126 EndZ=0
    g23: LineSegment StartX=195.991 StartY=-1.14503 StartZ=0 EndX=209.19 EndY=12.3205 EndZ=0
    g24: LineSegment StartX=209.19 StartY=12.3205 StartZ=0 EndX=213.44 EndY=12.3702 EndZ=0
    g25: LineSegment StartX=213.44 StartY=12.3702 StartZ=0 EndX=200.192 EndY=-1.14503 EndZ=0
    g26: LineSegment StartX=200.192 StartY=-1.14503 StartZ=0 EndX=195.991 EndY=-1.14503 EndZ=0
    g27: LineSegment StartX=229.838 StartY=9.19446 StartZ=0 EndX=237.096 EndY=0 EndZ=0
    g28: LineSegment StartX=237.096 StartY=0 StartZ=0 EndX=240.918 EndY=0 EndZ=0
    g29: LineSegment StartX=240.918 StartY=0 StartZ=0 EndX=234.226 EndY=8.47688 EndZ=0
    g30: LineSegment StartX=234.226 StartY=8.47688 StartZ=0 EndX=229.838 EndY=9.19446 EndZ=0
    g31: ArcOfCircle CenterX=18 CenterY=3 CenterZ=0 NormalX=0 NormalY=0 NormalZ=1 AngleXU=0 Radius=6.5 StartAngle=5.86022 EndAngle=7.42624
    g32: Circle CenterX=18 CenterY=3 CenterZ=0 NormalX=0 NormalY=0 NormalZ=1 AngleXU=0 Radius=4.1
    g33: Circle CenterX=185 CenterY=7 CenterZ=0 NormalX=0 NormalY=0 NormalZ=1 AngleXU=0 Radius=4.1
    g34: ArcOfCircle CenterX=185 CenterY=7 CenterZ=0 NormalX=0 NormalY=0 NormalZ=1 AngleXU=0 Radius=6.5 StartAngle=1.96559 EndAngle=4.3176
    g35: LineSegment StartX=182.5 StartY=13 StartZ=0 EndX=182.5 EndY=15.9367 EndZ=0
    g36: LineSegment StartX=182.5 StartY=15.9367 StartZ=0 EndX=187.5 EndY=15.5349 EndZ=0
    g37: LineSegment StartX=187.5 StartY=15.5349 StartZ=0 EndX=187.5 EndY=13 EndZ=0
    g38: LineSegment StartX=182.5 StartY=1 StartZ=0 EndX=182.5 EndY=-1.79994 EndZ=0
    g39: LineSegment StartX=182.5 StartY=-1.79994 StartZ=0 EndX=187.5 EndY=-1.79994 EndZ=0
    g40: LineSegment StartX=187.5 StartY=-1.79994 StartZ=0 EndX=187.5 EndY=1 EndZ=0
    g41: ArcOfCircle CenterX=185 CenterY=7 CenterZ=0 NormalX=0 NormalY=0 NormalZ=1 AngleXU=0 Radius=6.5 StartAngle=5.10718 EndAngle=7.45919
  constraints (84):
    c: Coincident(g2,g0)
    c: Coincident(g2,g1)
    c: Coincident(g3,g0)
    c: Coincident(g3,g1)
    c: Horizontal(g3)
    c: Parallel(g0,g1)
    c: Distance(g1,g0) = 3
    c: Diameter(g4) = 13
    c: DistanceY(g-1,g4) = 3
    c: DistanceX(g-1,g4) = 18
    c: Coincident(g7,g6)
    c: Coincident(g7,g5)
    c: PointOnObject(g8,g31)
    c: Coincident(g10,g9)
    c: Horizontal(g10)
    c: Coincident(g10,g8)
    c: Coincident(g11,g12)
    c: Horizontal(g12)
    c: Coincident(g12,g13)
    c: Coincident(g13,g14)
    c: Coincident(g14,g11)
    c: Parallel(g11,g13)
    c: Distance(g13,g11) = 3
    c: Coincident(g15,g16)
    c: Coincident(g16,g17)
    c: Coincident(g17,g18)
    c: Coincident(g18,g15)
    c: Horizontal(g18)
    c: Parallel(g17,g15)
    c: Distance(g17,g15) = 3
    c: Coincident(g19,g20)
    c: Coincident(g20,g21)
    c: Coincident(g21,g22)
    c: Coincident(g22,g19)
    c: Parallel(g19,g21)
    c: Distance(g21,g19) = 3
    c: Coincident(g23,g24)
    c: Coincident(g24,g25)
    c: Coincident(g25,g26)
    c: Horizontal(g26)
    c: Parallel(g23,g25)
    c: Distance(g25,g23) = 3
    c: PointOnObject(g27,g-1)
    c: Coincident(g27,g28)
    c: PointOnObject(g28,g-1)
    c: Coincident(g28,g29)
    c: Coincident(g29,g30)
    c: Coincident(g30,g27)
    c: Parallel(g27,g29)
    c: Distance(g29,g27) = 3
    c: Coincident(g31,g5)
    c: Coincident(g4,g6)
    c: Equal(g4,g31)
    c: Coincident(g4,g9)
    c: PointOnObject(g31,g8)
    c: Coincident(g4,g31)
    c: Coincident(g26,g23)
    c: Diameter(g32) = 8.2
    c: Coincident(g32,g4)
    c: Diameter(g33) = 8.2
    c: DistanceY(g-1,g33) = 7
    c: DistanceX(g-1,g33) = 185
    c: Diameter(g34) = 13
    c: Coincident(g34,g33)
    c: Coincident(g35,g36)
    c: Coincident(g36,g37)
    c: Vertical(g37)
    c: Vertical(g38)
    c: Coincident(g38,g39)
    c: Horizontal(g39)
    c: Coincident(g39,g40)
    c: PointOnObject(g40,g41)
    c: Vertical(g40)
    c: Vertical(g35)
    c: Distance(g37,g35) = 5
    c: DistanceX(g35,g33) = 2.5
    c: Distance(g38,g40) = 5
    c: DistanceX(g38,g33) = 2.5
    c: Coincident(g41,g37)
    c: Coincident(g34,g35)
    c: Equal(g34,g41)
    c: Coincident(g34,g38)
    c: PointOnObject(g41,g40)
    c: Coincident(g34,g41)
FEATURE [PartDesign::Pad] Pad086
  BaseFeature = -> Pocket110
  Direction = (0,-1,2e-16)
  Length = 7
  Length2 = 10
  Placement = pos=(0,0,0) rot=(1,0,0;1.5708rad)
  Profile = -> Sketch197
  ReferenceAxis = -> Sketch197 [N_Axis]
  Refine = true
  Reversed = true
  Suppressed = false
  Type = 0
FEATURE [Sketcher::SketchObject] Sketch199
  ArcFitTolerance = 1e-06
  AttachmentSupport = -> [Pad086]
  FullyConstrained = false
  MakeInternals = false
  MapMode = 5
  Placement = pos=(35,0,0) rot=(0.707107,0,-0.707107;3.14159rad)
  sketch-geometry (25):
    g0: LineSegment [constr] StartX=-33.5639 StartY=50 StartZ=0 EndX=22.3562 EndY=50 EndZ=0
    g1: LineSegment StartX=-17.0984 StartY=50 StartZ=0 EndX=-16.0002 EndY=50 EndZ=0
    g2: LineSegment StartX=-16.0002 StartY=50 StartZ=0 EndX=5.93914 EndY=8.47552 EndZ=0
    g3: LineSegment StartX=5.93914 StartY=8.47552 StartZ=0 EndX=5.96134 EndY=7.0893 EndZ=0
    g4: LineSegment StartX=5.96134 StartY=7.0893 StartZ=0 EndX=4.40956 EndY=7.0893 EndZ=0
    g5: LineSegment StartX=4.40956 StartY=7.0893 StartZ=0 EndX=-17.1228 EndY=47.8435 EndZ=0
    g6: LineSegment StartX=-17.1228 StartY=47.8435 StartZ=0 EndX=-17.0984 EndY=50 EndZ=0
    g7: LineSegment StartX=-17.1293 StartY=7.10705 StartZ=0 EndX=-17.1293 EndY=9.14543 EndZ=0
    g8: LineSegment StartX=-17.1293 StartY=9.14543 StartZ=0 EndX=4.55828 EndY=50 EndZ=0
    g9: LineSegment StartX=4.55828 StartY=50 StartZ=0 EndX=5.87403 EndY=50.0018 EndZ=0
    g10: LineSegment StartX=5.87403 StartY=50.0018 StartZ=0 EndX=5.93974 EndY=48.3369 EndZ=0
    g11: LineSegment StartX=5.93974 StartY=48.3369 StartZ=0 EndX=-15.9471 EndY=7.10705 EndZ=0
    g12: LineSegment StartX=-15.9471 StartY=7.10705 StartZ=0 EndX=-17.1293 EndY=7.10705 EndZ=0
    g13: LineSegment StartX=-17.1358 StartY=50 StartZ=0 EndX=-15.9776 EndY=50.0877 EndZ=0
    g14: LineSegment StartX=-15.9776 StartY=50.0877 StartZ=0 EndX=5.97119 EndY=97.9201 EndZ=0
    g15: LineSegment StartX=5.97119 StartY=97.9201 StartZ=0 EndX=5.97119 EndY=99.8598 EndZ=0
    g16: LineSegment StartX=5.97119 StartY=99.8598 StartZ=0 EndX=4.66077 EndY=99.8598 EndZ=0
    g17: LineSegment StartX=4.66077 StartY=99.8598 StartZ=0 EndX=-17.1358 EndY=52.3592 EndZ=0
    g18: LineSegment StartX=-17.1358 StartY=52.3592 StartZ=0 EndX=-17.1358 EndY=50 EndZ=0
    g19: LineSegment StartX=-15.9576 StartY=99.8854 StartZ=0 EndX=-17.034 EndY=99.8854 EndZ=0
    g20: LineSegment StartX=-17.034 StartY=99.8854 StartZ=0 EndX=-17.0782 EndY=97.5311 EndZ=0
    g21: LineSegment StartX=-17.0782 StartY=97.5311 StartZ=0 EndX=4.71765 EndY=50 EndZ=0
    g22: LineSegment StartX=4.71765 StartY=50 StartZ=0 EndX=5.8275 EndY=50.1579 EndZ=0
    g23: LineSegment StartX=5.8275 StartY=50.1579 StartZ=0 EndX=5.8275 EndY=52.3779 EndZ=0
    g24: LineSegment StartX=5.8275 StartY=52.3779 StartZ=0 EndX=-15.9576 EndY=99.8854 EndZ=0
  constraints (47):
    c: Horizontal(g0)
    c: DistanceY(g-1,g0) = 50
    c: PointOnObject(g1,g0)
    c: Horizontal(g1)
    c: Coincident(g1,g2)
    c: Coincident(g2,g3)
    c: Coincident(g3,g4)
    c: Horizontal(g4)
    c: Coincident(g4,g5)
    c: Coincident(g5,g6)
    c: Vertical(g7)
    c: Coincident(g7,g8)
    c: PointOnObject(g8,g0)
    c: Coincident(g8,g9)
    c: Coincident(g9,g10)
    c: Coincident(g10,g11)
    c: Coincident(g11,g12)
    c: Coincident(g12,g7)
    c: Horizontal(g12)
    c: Parallel(g5,g2)
    c: Parallel(g8,g11)
    c: Distance(g2,g5) = 2
    c: Distance(g8,g11) = 2
    c: Coincident(g6,g1)
    c: PointOnObject(g13,g0)
    c: Coincident(g13,g14)
    c: Coincident(g14,g15)
    c: Vertical(g15)
    c: Coincident(g15,g16)
    c: Horizontal(g16)
    c: Coincident(g16,g17)
    c: Coincident(g17,g18)
    c: Coincident(g18,g13)
    c: Parallel(g17,g14)
    c: Vertical(g18)
    c: Distance(g14,g17) = 2
    c: Horizontal(g19)
    c: Coincident(g19,g20)
    c: Coincident(g20,g21)
    c: PointOnObject(g21,g0)
    c: Coincident(g21,g22)
    c: Coincident(g22,g23)
    c: Vertical(g23)
    c: Coincident(g23,g24)
    c: Coincident(g24,g19)
    c: Parallel(g24,g21)
    c: Distance(g21,g24) = 2
FEATURE [PartDesign::Pad] Pad087
  BaseFeature = -> Pad086
  Direction = (-1,0,-2e-16)
  Length = 5
  Length2 = 10
  Placement = pos=(0,0,0) rot=(1,0,0;1.5708rad)
  Profile = -> Sketch199
  ReferenceAxis = -> Sketch199 [N_Axis]
  Refine = true
  Reversed = true
  Suppressed = false
  Type = 0
FEATURE [Sketcher::SketchObject] Sketch200
  ArcFitTolerance = 1e-06
  AttachmentSupport = -> [Pad087]
  FullyConstrained = false
  MakeInternals = false
  MapMode = 5
  Placement = pos=(170,0,0) rot=(0.707107,0,0.707107;3.14159rad)
  sketch-geometry (25):
    g0: LineSegment [constr] StartX=-9.20711 StartY=50 StartZ=0 EndX=31.5955 EndY=50 EndZ=0
    g1: LineSegment StartX=-3.23071 StartY=7.09197 StartZ=0 EndX=-2.05702 EndY=7.09197 EndZ=0
    g2: LineSegment StartX=-2.05702 StartY=7.09197 StartZ=0 EndX=18.4375 EndY=47.7755 EndZ=0
    g3: LineSegment StartX=18.4375 StartY=47.7755 StartZ=0 EndX=18.4375 EndY=50 EndZ=0
    g4: LineSegment StartX=18.4375 StartY=50 StartZ=0 EndX=17.3084 EndY=49.9795 EndZ=0
    g5: LineSegment StartX=17.3084 StartY=49.9795 StartZ=0 EndX=-3.23071 EndY=9.20758 EndZ=0
    g6: LineSegment StartX=-3.23071 StartY=9.20758 StartZ=0 EndX=-3.23071 EndY=7.09197 EndZ=0
    g7: LineSegment StartX=17.1226 StartY=7.07983 StartZ=0 EndX=18.4953 EndY=7.07983 EndZ=0
    g8: LineSegment StartX=18.4953 StartY=7.07983 StartZ=0 EndX=18.4953 EndY=8.80663 EndZ=0
    g9: LineSegment StartX=18.4953 StartY=8.80663 StartZ=0 EndX=-2.09857 EndY=50 EndZ=0
    g10: LineSegment StartX=-2.09857 StartY=50 StartZ=0 EndX=-3.17562 EndY=49.9159 EndZ=0
    g11: LineSegment StartX=-3.17562 StartY=49.9159 StartZ=0 EndX=-3.17562 EndY=47.6818 EndZ=0
    g12: LineSegment StartX=-3.17562 StartY=47.6818 StartZ=0 EndX=17.1226 EndY=7.07983 EndZ=0
    g13: LineSegment StartX=-3.19345 StartY=99.8693 StartZ=0 EndX=-2.03057 EndY=99.8693 EndZ=0
    g14: LineSegment StartX=-2.03057 StartY=99.8693 StartZ=0 EndX=18.4277 EndY=53.15 EndZ=0
    g15: LineSegment StartX=18.4277 StartY=53.15 StartZ=0 EndX=18.5025 EndY=50 EndZ=0
    g16: LineSegment StartX=18.5025 StartY=50 StartZ=0 EndX=17.5757 EndY=50.1098 EndZ=0
    g17: LineSegment StartX=17.5757 StartY=50.1098 StartZ=0 EndX=-3.19345 EndY=97.5389 EndZ=0
    g18: LineSegment StartX=-3.19345 StartY=97.5389 StartZ=0 EndX=-3.19345 EndY=99.8693 EndZ=0
    g19: LineSegment StartX=-3.22366 StartY=50 StartZ=0 EndX=-3.22366 EndY=52.3177 EndZ=0
    g20: LineSegment StartX=-3.22366 StartY=52.3177 StartZ=0 EndX=17.471 EndY=99.8606 EndZ=0
    g21: LineSegment StartX=17.471 StartY=99.8606 StartZ=0 EndX=18.4521 EndY=99.8606 EndZ=0
    g22: LineSegment StartX=18.4521 StartY=99.8606 StartZ=0 EndX=18.4521 EndY=97.1035 EndZ=0
    g23: LineSegment StartX=18.4521 StartY=97.1035 StartZ=0 EndX=-2.05909 EndY=49.982 EndZ=0
    g24: LineSegment StartX=-2.05909 StartY=49.982 StartZ=0 EndX=-3.22366 EndY=50 EndZ=0
  constraints (49):
    c: Horizontal(g0)
    c: DistanceY(g-1,g0) = 50
    c: Horizontal(g1)
    c: Coincident(g1,g2)
    c: Coincident(g2,g3)
    c: PointOnObject(g3,g0)
    c: Vertical(g3)
    c: Coincident(g3,g4)
    c: Coincident(g4,g5)
    c: Coincident(g5,g6)
    c: Coincident(g6,g1)
    c: Horizontal(g7)
    c: Coincident(g7,g8)
    c: Vertical(g8)
    c: Coincident(g8,g9)
    c: PointOnObject(g9,g0)
    c: Coincident(g9,g10)
    c: Coincident(g10,g11)
    c: Vertical(g11)
    c: Coincident(g11,g12)
    c: Coincident(g12,g7)
    c: Parallel(g9,g12)
    c: Parallel(g5,g2)
    c: Distance(g2,g5) = 2
    c: Distance(g12,g9) = 2
    c: Vertical(g6)
    c: Horizontal(g13)
    c: Coincident(g13,g14)
    c: Coincident(g14,g15)
    c: PointOnObject(g15,g0)
    c: Coincident(g15,g16)
    c: Coincident(g16,g17)
    c: Coincident(g17,g18)
    c: Coincident(g18,g13)
    c: Vertical(g18)
    c: PointOnObject(g19,g0)
    c: Vertical(g19)
    c: Coincident(g19,g20)
    c: Coincident(g20,g21)
    c: Horizontal(g21)
    c: Coincident(g21,g22)
    c: Vertical(g22)
    c: Coincident(g22,g23)
    c: Coincident(g23,g24)
    c: Coincident(g24,g19)
    c: Parallel(g17,g14)
    c: Parallel(g23,g20)
    c: Distance(g23,g20) = 2
    c: Distance(g14,g17) = 2
FEATURE [PartDesign::Pad] Pad088
  BaseFeature = -> Pad087
  Direction = (1,0,-2e-16)
  Length = 5
  Length2 = 10
  Placement = pos=(0,0,0) rot=(1,0,0;1.5708rad)
  Profile = -> Sketch200
  ReferenceAxis = -> Sketch200 [N_Axis]
  Refine = true
  Reversed = true
  Suppressed = false
  Type = 0
FEATURE [PartDesign::Body] Body039  label="wingspar 006"
  AllowCompound = false
  Group = -> [Sketch194,Pad085,Sketch195,Pocket108,Sketch196,Pocket109,Pocket110,Sketch197,Pad086,Sketch198,Sketch199,Pad087,Sketch200,Pad088]
  Origin = -> Origin039
  Placement = pos=(0,-400,0) rot=(0,0,1;0rad)
  Tip = -> Pad088
FEATURE [Sketcher::SketchObject] Sketch201
  ArcFitTolerance = 1e-06
  FullyConstrained = false
  MakeInternals = false
  Placement = pos=(0,0,0) rot=(1,0,0;1.5708rad)
  sketch-geometry (125):
    g0: BSplineCurve PolesCount=62 KnotsCount=62 Degree=3 IsPeriodic=1
    g1-g62: Circle [constr] x62 (B-spline internal-alignment scaffolding for g0; pole/knot coordinates omitted)
    g63-g124: GeomPoint [constr] x62 (B-spline internal-alignment scaffolding for g0; pole/knot coordinates omitted)
  constraints (125):
    c: InternalAlignment(g1,g0)
    c: Weight(g1) = 1
    c: InternalAlignment(g2,g0)
    c: Equal(g2,g1)
    c: InternalAlignment(g3,g0)
    c: Equal(g3,g1)
    c: InternalAlignment(g4,g0)
    c: Equal(g4,g1)
    c: InternalAlignment(g5,g0)
    c: Equal(g5,g1)
    c: InternalAlignment(g6,g0)
    c: Equal(g6,g1)
    c: InternalAlignment(g7,g0)
    c: Equal(g7,g1)
    c: InternalAlignment(g8,g0)
    c: Equal(g8,g1)
    c: InternalAlignment(g9,g0)
    c: Equal(g9,g1)
    c: InternalAlignment(g10,g0)
    c: Equal(g10,g1)
    c: InternalAlignment(g11,g0)
    c: Equal(g11,g1)
    c: InternalAlignment(g12,g0)
    c: Equal(g12,g1)
    c: InternalAlignment(g13,g0)
    c: Equal(g13,g1)
    c: InternalAlignment(g14,g0)
    c: Equal(g14,g1)
    c: InternalAlignment(g15,g0)
    c: Equal(g15,g1)
    c: InternalAlignment(g16,g0)
    c: Equal(g16,g1)
    c: InternalAlignment(g17,g0)
    c: Equal(g17,g1)
    c: InternalAlignment(g18,g0)
    c: Equal(g18,g1)
    c: InternalAlignment(g19,g0)
    c: Equal(g19,g1)
    c: InternalAlignment(g20,g0)
    c: Equal(g20,g1)
    c: InternalAlignment(g21,g0)
    c: Equal(g21,g1)
    c: InternalAlignment(g22,g0)
    c: Equal(g22,g1)
    c: InternalAlignment(g23,g0)
    c: Equal(g23,g1)
    c: InternalAlignment(g24,g0)
    c: Equal(g24,g1)
    c: InternalAlignment(g25,g0)
    c: Equal(g25,g1)
    c: InternalAlignment(g26,g0)
    c: Equal(g26,g1)
    c: InternalAlignment(g27,g0)
    c: Equal(g27,g1)
    c: InternalAlignment(g28,g0)
    c: Equal(g28,g1)
    c: InternalAlignment(g29,g0)
    c: Equal(g29,g1)
    c: InternalAlignment(g30,g0)
    c: Equal(g30,g1)
    c: InternalAlignment(g31,g0)
    c: Equal(g31,g1)
    c: InternalAlignment(g32,g0)
    c: Equal(g32,g1)
    c: InternalAlignment(g33,g0)
    c: Equal(g33,g1)
    c: InternalAlignment(g34,g0)
    c: Equal(g34,g1)
    c: InternalAlignment(g35,g0)
    c: Equal(g35,g1)
    c: InternalAlignment(g36,g0)
    c: Equal(g36,g1)
    c: InternalAlignment(g37,g0)
    c: Equal(g37,g1)
    c: InternalAlignment(g38,g0)
    c: Equal(g38,g1)
    c: InternalAlignment(g39,g0)
    c: Equal(g39,g1)
    c: InternalAlignment(g40,g0)
    c: Equal(g40,g1)
    c: InternalAlignment(g41,g0)
    c: Equal(g41,g1)
    c: InternalAlignment(g42,g0)
    c: Equal(g42,g1)
    c: InternalAlignment(g43,g0)
    c: Equal(g43,g1)
    c: InternalAlignment(g44,g0)
    c: Equal(g44,g1)
    c: InternalAlignment(g45,g0)
    c: Equal(g45,g1)
    c: InternalAlignment(g46,g0)
    c: Equal(g46,g1)
    c: InternalAlignment(g47,g0)
    c: Equal(g47,g1)
    c: InternalAlignment(g48,g0)
    c: Equal(g48,g1)
    c: InternalAlignment(g49,g0)
    c: Equal(g49,g1)
    c: InternalAlignment(g50,g0)
    c: Equal(g50,g1)
    c: InternalAlignment(g51,g0)
    c: Equal(g51,g1)
    c: InternalAlignment(g52,g0)
    c: Equal(g52,g1)
    c: InternalAlignment(g53,g0)
    c: Equal(g53,g1)
    c: InternalAlignment(g54,g0)
    c: Equal(g54,g1)
    c: InternalAlignment(g55,g0)
    c: Equal(g55,g1)
    c: InternalAlignment(g56,g0)
    c: Equal(g56,g1)
    c: InternalAlignment(g57,g0)
    c: Equal(g57,g1)
    c: InternalAlignment(g58,g0)
    c: Equal(g58,g1)
    c: InternalAlignment(g59,g0)
    c: Equal(g59,g1)
    c: InternalAlignment(g60,g0)
    c: Equal(g60,g1)
    c: InternalAlignment(g61,g0)
    c: Equal(g61,g1)
    c: InternalAlignment(g62,g0)
    c: Equal(g62,g1)
    c: InternalAlignment(g63-g124 -> g0) x62
FEATURE [PartDesign::Pad] Pad089
  Direction = (0,-1,2e-16)
  Length = 99.95
  Length2 = 10
  Placement = pos=(0,0,0) rot=(1,0,0;1.5708rad)
  Profile = -> Sketch201
  ReferenceAxis = -> Sketch201 [N_Axis]
  Refine = true
  Suppressed = false
  Type = 0
FEATURE [Sketcher::SketchObject] Sketch202
  ArcFitTolerance = 1e-06
  AttachmentSupport = -> [Pad089]
  FullyConstrained = false
  MakeInternals = false
  MapMode = 5
  Placement = pos=(0,-99.95,2.2e-14) rot=(1,0,0;1.5708rad)
  sketch-geometry (29):
    g0: LineSegment StartX=2.71326 StartY=0.775372 StartZ=0 EndX=3.3867 EndY=1.52303 EndZ=0
    g1: LineSegment StartX=3.3867 StartY=1.52303 StartZ=0 EndX=5.99321 EndY=4.17962 EndZ=0
    g2: LineSegment StartX=5.99321 StartY=4.17962 StartZ=0 EndX=11.2308 EndY=7.18071 EndZ=0
    g3: LineSegment StartX=11.2308 StartY=7.18071 StartZ=0 EndX=18.9287 EndY=10.4927 EndZ=0
    g4: LineSegment StartX=18.9287 StartY=10.4927 StartZ=0 EndX=30.0156 EndY=13.8045 EndZ=0
    g5: LineSegment StartX=30.0156 StartY=13.8045 StartZ=0 EndX=43.7053 EndY=16.6585 EndZ=0
    g6: LineSegment StartX=43.7053 StartY=16.6585 StartZ=0 EndX=58.3753 EndY=18.5837 EndZ=0
    g7: LineSegment StartX=58.3753 StartY=18.5837 StartZ=0 EndX=81.9328 EndY=20.1998 EndZ=0
    g8: LineSegment StartX=81.9328 StartY=20.1998 StartZ=0 EndX=99.116 EndY=20.5815 EndZ=0
    g9: LineSegment StartX=99.116 StartY=20.5815 StartZ=0 EndX=120.506 EndY=20.1998 EndZ=0
    g10: LineSegment StartX=120.506 StartY=20.1998 StartZ=0 EndX=145.772 EndY=18.6559 EndZ=0
    g11: LineSegment StartX=145.772 StartY=18.6559 StartZ=0 EndX=175.748 EndY=15.7728 EndZ=0
    g12: LineSegment StartX=175.748 StartY=15.7728 StartZ=0 EndX=200.436 EndY=12.5699 EndZ=0
    g13: LineSegment StartX=200.436 StartY=12.5699 StartZ=0 EndX=229.384 EndY=8.60252 EndZ=0
    g14: LineSegment StartX=229.384 StartY=8.60252 StartZ=0 EndX=252.135 EndY=5.21302 EndZ=0
    g15: LineSegment StartX=252.135 StartY=5.21302 StartZ=0 EndX=269.07 EndY=2.67143 EndZ=0
    g16: LineSegment StartX=269.07 StartY=2.67143 StartZ=0 EndX=269.07 EndY=1.39956 EndZ=0
    g17: LineSegment StartX=269.07 StartY=1.39956 StartZ=0 EndX=224.761 EndY=0.436598 EndZ=0
    g18: LineSegment StartX=224.761 StartY=0.436598 StartZ=0 EndX=175.487 EndY=-1.02731 EndZ=0
    g19: LineSegment StartX=175.487 StartY=-1.02731 StartZ=0 EndX=123.478 EndY=-2.41293 EndZ=0
    g20: LineSegment StartX=123.478 StartY=-2.41293 StartZ=0 EndX=62.0775 EndY=-3.87655 EndZ=0
    g21: LineSegment StartX=62.0775 StartY=-3.87655 StartZ=0 EndX=32.0529 EndY=-3.76091 EndZ=0
    g22: LineSegment StartX=32.0529 StartY=-3.76091 StartZ=0 EndX=18.888 EndY=-3.18288 EndZ=0
    g23: LineSegment StartX=18.888 StartY=-3.18288 StartZ=0 EndX=12.7286 EndY=-2.48971 EndZ=0
    g24: LineSegment StartX=12.7286 StartY=-2.48971 StartZ=0 EndX=8.49342 EndY=-1.8722 EndZ=0
    g25: LineSegment StartX=8.49342 StartY=-1.8722 StartZ=0 EndX=4.56236 EndY=-0.768246 EndZ=0
    g26: LineSegment StartX=4.56236 StartY=-0.768246 StartZ=0 EndX=3.01395 EndY=-0.301296 EndZ=0
    g27: ArcOfCircle CenterX=3.20505 CenterY=0.332397 CenterZ=0 NormalX=0 NormalY=0 NormalZ=1 AngleXU=0 Radius=0.661881 StartAngle=2.40837 EndAngle=4.41949
    g28: GeomPoint [constr] X=2.01486 Y=0 Z=0
  constraints (32):
    c: PointOnObject(g28,g-1)
    c: Coincident(g0,g1)
    c: Coincident(g1,g2)
    c: Coincident(g2,g3)
    c: Coincident(g3,g4)
    c: Coincident(g4,g5)
    c: Coincident(g5,g6)
    c: Coincident(g6,g7)
    c: Coincident(g7,g8)
    c: Coincident(g8,g9)
    c: Coincident(g9,g10)
    c: Coincident(g10,g11)
    c: Coincident(g11,g12)
    c: Coincident(g12,g13)
    c: Coincident(g13,g14)
    c: Coincident(g14,g15)
    c: Coincident(g15,g16)
    c: Vertical(g16)
    c: Coincident(g16,g17)
    c: Coincident(g17,g18)
    c: Coincident(g18,g19)
    c: Coincident(g19,g20)
    c: Coincident(g20,g21)
    c: Coincident(g21,g22)
    c: Coincident(g22,g23)
    c: Coincident(g23,g24)
    c: Coincident(g24,g25)
    c: Coincident(g25,g26)
    c: PointOnObject(g28,g0)
    c: PointOnObject(g28,g26)
    c: Tangent(g0,g27) = 1.5708
    c: Tangent(g26,g27) = 1.5708
FEATURE [PartDesign::Pocket] Pocket111
  BaseFeature = -> Pad089
  Direction = (0,1,-2e-16)
  Length = 99.95
  Length2 = 5
  Placement = pos=(0,0,0) rot=(1,0,0;1.5708rad)
  Profile = -> Sketch202
  ReferenceAxis = -> Sketch202 [N_Axis]
  Refine = true
  Suppressed = false
  Type = 0
FEATURE [Sketcher::SketchObject] Sketch203
  ArcFitTolerance = 1e-06
  AttachmentSupport = -> [XY_Plane040]
  FullyConstrained = false
  MakeInternals = false
  MapMode = 5
  sketch-geometry (4):
    g0: LineSegment StartX=295 StartY=17.3691 StartZ=0 EndX=295 EndY=-107.641 EndZ=0
    g1: LineSegment StartX=295 StartY=-107.641 StartZ=0 EndX=389.553 EndY=-107.641 EndZ=0
    g2: LineSegment StartX=389.553 StartY=-107.641 StartZ=0 EndX=389.553 EndY=17.3691 EndZ=0
    g3: LineSegment StartX=389.553 StartY=17.3691 StartZ=0 EndX=295 EndY=17.3691 EndZ=0
  constraints (9):
    c: Coincident(g0,g1)
    c: Coincident(g1,g2)
    c: Coincident(g2,g3)
    c: Coincident(g3,g0)
    c: Vertical(g0)
    c: Vertical(g2)
    c: Horizontal(g1)
    c: Horizontal(g3)
    c: DistanceX(g-1,g0) = 295
FEATURE [PartDesign::Pocket] Pocket112
  BaseFeature = -> Pocket111
  Direction = (0,0,-1)
  Length = 5
  Length2 = 5
  Midplane = true
  Placement = pos=(0,0,0) rot=(1,0,0;1.5708rad)
  Profile = -> Sketch203
  ReferenceAxis = -> Sketch203 [N_Axis]
  Refine = true
  Suppressed = false
  Type = 0
FEATURE [Sketcher::SketchObject] Sketch205
  ArcFitTolerance = 1e-06
  AttachmentSupport = -> [XY_Plane040]
  FullyConstrained = true
  MakeInternals = false
  MapMode = 5
  sketch-geometry (12):
    g0: LineSegment StartX=-20 StartY=-7 StartZ=0 EndX=-20 EndY=-117 EndZ=0
    g1: LineSegment StartX=-20 StartY=-117 StartZ=0 EndX=35 EndY=-117 EndZ=0
    g2: LineSegment StartX=35 StartY=-117 StartZ=0 EndX=35 EndY=-7 EndZ=0
    g3: LineSegment StartX=35 StartY=-7 StartZ=0 EndX=-20 EndY=-7 EndZ=0
    g4: LineSegment StartX=40 StartY=-7 StartZ=0 EndX=40 EndY=-117 EndZ=0
    g5: LineSegment StartX=40 StartY=-117 StartZ=0 EndX=165 EndY=-117 EndZ=0
    g6: LineSegment StartX=165 StartY=-117 StartZ=0 EndX=165 EndY=-7 EndZ=0
    g7: LineSegment StartX=165 StartY=-7 StartZ=0 EndX=40 EndY=-7 EndZ=0
    g8: LineSegment StartX=170 StartY=-7 StartZ=0 EndX=170 EndY=-117 EndZ=0
    g9: LineSegment StartX=170 StartY=-117 StartZ=0 EndX=300 EndY=-117 EndZ=0
    g10: LineSegment StartX=300 StartY=-117 StartZ=0 EndX=300 EndY=-7 EndZ=0
    g11: LineSegment StartX=300 StartY=-7 StartZ=0 EndX=170 EndY=-7 EndZ=0
  constraints (36):
    c: Coincident(g0,g1)
    c: Coincident(g1,g2)
    c: Coincident(g2,g3)
    c: Coincident(g3,g0)
    c: Vertical(g0)
    c: Vertical(g2)
    c: Horizontal(g1)
    c: Horizontal(g3)
    c: Coincident(g4,g5)
    c: Coincident(g5,g6)
    c: Coincident(g6,g7)
    c: Coincident(g7,g4)
    c: Vertical(g4)
    c: Vertical(g6)
    c: Horizontal(g5)
    c: Horizontal(g7)
    c: Coincident(g8,g9)
    c: Coincident(g9,g10)
    c: Coincident(g10,g11)
    c: Coincident(g11,g8)
    c: Vertical(g8)
    c: Vertical(g10)
    c: Horizontal(g9)
    c: Horizontal(g11)
    c: DistanceY(g10,g-1) = 7
    c: DistanceY(g6,g-1) = 7
    c: DistanceY(g2,g-1) = 7
    c: DistanceX(g0,g-1) = 20
    c: DistanceY(g0,g0) = 110
    c: Distance(g4,g2) = 5
    c: Distance(g8,g6) = 5
    c: DistanceY(g4,g4) = 110
    c: DistanceY(g8,g8) = 110
    c: DistanceX(g-1,g9) = 300
    c: DistanceX(g-1,g1) = 35
    c: DistanceX(g-1,g5) = 165
FEATURE [PartDesign::Pocket] Pocket113
  BaseFeature = -> Pocket112
  Direction = (0,0,-1)
  Length = 100
  Length2 = 5
  Midplane = true
  Placement = pos=(0,0,0) rot=(1,0,0;1.5708rad)
  Profile = -> Sketch205
  ReferenceAxis = -> Sketch205 [N_Axis]
  Refine = true
  Suppressed = false
  Type = 0
FEATURE [Sketcher::SketchObject] Sketch204
  ArcFitTolerance = 1e-06
  AttachmentSupport = -> [Pocket113]
  FullyConstrained = false
  MakeInternals = false
  MapMode = 5
  Placement = pos=(0,-7,-2.3e-15) rot=(1,0,0;1.5708rad)
  sketch-geometry (42):
    g0: LineSegment StartX=45.884 StartY=17.7219 StartZ=0 EndX=33.93 EndY=-4.65497 EndZ=0
    g1: LineSegment StartX=49.8645 StartY=18.8062 StartZ=0 EndX=37.3312 EndY=-4.65497 EndZ=0
    g2: LineSegment StartX=45.884 StartY=17.7219 StartZ=0 EndX=49.8645 EndY=18.8062 EndZ=0
    g3: LineSegment StartX=33.93 StartY=-4.65497 StartZ=0 EndX=37.3312 EndY=-4.65497 EndZ=0
    g4: ArcOfCircle CenterX=18 CenterY=3 CenterZ=0 NormalX=0 NormalY=0 NormalZ=1 AngleXU=0 Radius=6.5 StartAngle=2.58175 EndAngle=4.38597
    g5: LineSegment StartX=20.6963 StartY=8.91437 StartZ=0 EndX=19.1912 EndY=11.3613 EndZ=0
    g6: LineSegment StartX=12.4923 StartY=6.45183 StartZ=0 EndX=11.7252 EndY=8.2111 EndZ=0
    g7: LineSegment StartX=11.7252 StartY=8.2111 StartZ=0 EndX=19.1912 EndY=11.3613 EndZ=0
    g8: LineSegment StartX=23.9272 StartY=0.331954 StartZ=0 EndX=26.093 EndY=-4.58272 EndZ=0
    g9: LineSegment StartX=15.9158 StartY=-3.15679 StartZ=0 EndX=16.6159 EndY=-4.58272 EndZ=0
    g10: LineSegment StartX=16.6159 StartY=-4.58272 StartZ=0 EndX=26.093 EndY=-4.58272 EndZ=0
    g11: LineSegment StartX=74.8373 StartY=20.9684 StartZ=0 EndX=89.2063 EndY=-4.24973 EndZ=0
    g12: LineSegment StartX=89.2063 StartY=-4.24973 StartZ=0 EndX=92.6591 EndY=-4.24973 EndZ=0
    g13: LineSegment StartX=92.6591 StartY=-4.24973 StartZ=0 EndX=78.184 EndY=21.1546 EndZ=0
    g14: LineSegment StartX=78.184 StartY=21.1546 StartZ=0 EndX=74.8373 EndY=20.9684 EndZ=0
    g15: LineSegment StartX=113.372 StartY=-3.61742 StartZ=0 EndX=125.992 EndY=20.9865 EndZ=0
    g16: LineSegment StartX=125.992 StartY=20.9865 StartZ=0 EndX=129.338 EndY=20.9348 EndZ=0
    g17: LineSegment StartX=129.338 StartY=20.9348 StartZ=0 EndX=116.743 EndY=-3.61742 EndZ=0
    g18: LineSegment StartX=116.743 StartY=-3.61742 StartZ=0 EndX=113.372 EndY=-3.61742 EndZ=0
    g19: LineSegment StartX=156.49 StartY=19.0126 StartZ=0 EndX=171.224 EndY=-2.18705 EndZ=0
    g20: LineSegment StartX=171.224 StartY=-2.18705 StartZ=0 EndX=175.064 EndY=-2.45586 EndZ=0
    g21: LineSegment StartX=175.064 StartY=-2.45586 StartZ=0 EndX=160.386 EndY=18.6636 EndZ=0
    g22: LineSegment StartX=160.386 StartY=18.6636 StartZ=0 EndX=156.49 EndY=19.0126 EndZ=0
    g23: LineSegment StartX=195.991 StartY=-1.14503 StartZ=0 EndX=209.19 EndY=12.3205 EndZ=0
    g24: LineSegment StartX=209.19 StartY=12.3205 StartZ=0 EndX=213.44 EndY=12.3702 EndZ=0
    g25: LineSegment StartX=213.44 StartY=12.3702 StartZ=0 EndX=200.192 EndY=-1.14503 EndZ=0
    g26: LineSegment StartX=200.192 StartY=-1.14503 StartZ=0 EndX=195.991 EndY=-1.14503 EndZ=0
    g27: LineSegment StartX=229.838 StartY=9.19446 StartZ=0 EndX=237.096 EndY=0 EndZ=0
    g28: LineSegment StartX=237.096 StartY=0 StartZ=0 EndX=240.918 EndY=0 EndZ=0
    g29: LineSegment StartX=240.918 StartY=0 StartZ=0 EndX=234.226 EndY=8.47688 EndZ=0
    g30: LineSegment StartX=234.226 StartY=8.47688 StartZ=0 EndX=229.838 EndY=9.19446 EndZ=0
    g31: ArcOfCircle CenterX=18 CenterY=3 CenterZ=0 NormalX=0 NormalY=0 NormalZ=1 AngleXU=0 Radius=6.5 StartAngle=5.86022 EndAngle=7.42624
    g32: Circle CenterX=18 CenterY=3 CenterZ=0 NormalX=0 NormalY=0 NormalZ=1 AngleXU=0 Radius=4.1
    g33: Circle CenterX=185 CenterY=7 CenterZ=0 NormalX=0 NormalY=0 NormalZ=1 AngleXU=0 Radius=4.1
    g34: ArcOfCircle CenterX=185 CenterY=7 CenterZ=0 NormalX=0 NormalY=0 NormalZ=1 AngleXU=0 Radius=6.5 StartAngle=1.96559 EndAngle=4.3176
    g35: LineSegment StartX=182.5 StartY=13 StartZ=0 EndX=182.5 EndY=15.9367 EndZ=0
    g36: LineSegment StartX=182.5 StartY=15.9367 StartZ=0 EndX=187.5 EndY=15.5349 EndZ=0
    g37: LineSegment StartX=187.5 StartY=15.5349 StartZ=0 EndX=187.5 EndY=13 EndZ=0
    g38: LineSegment StartX=182.5 StartY=1 StartZ=0 EndX=182.5 EndY=-1.79994 EndZ=0
    g39: LineSegment StartX=182.5 StartY=-1.79994 StartZ=0 EndX=187.5 EndY=-1.79994 EndZ=0
    g40: LineSegment StartX=187.5 StartY=-1.79994 StartZ=0 EndX=187.5 EndY=1 EndZ=0
    g41: ArcOfCircle CenterX=185 CenterY=7 CenterZ=0 NormalX=0 NormalY=0 NormalZ=1 AngleXU=0 Radius=6.5 StartAngle=5.10718 EndAngle=7.45919
  constraints (84):
    c: Coincident(g2,g0)
    c: Coincident(g2,g1)
    c: Coincident(g3,g0)
    c: Coincident(g3,g1)
    c: Horizontal(g3)
    c: Parallel(g0,g1)
    c: Distance(g1,g0) = 3
    c: Diameter(g4) = 13
    c: DistanceY(g-1,g4) = 3
    c: DistanceX(g-1,g4) = 18
    c: Coincident(g7,g6)
    c: Coincident(g7,g5)
    c: PointOnObject(g8,g31)
    c: Coincident(g10,g9)
    c: Horizontal(g10)
    c: Coincident(g10,g8)
    c: Coincident(g11,g12)
    c: Horizontal(g12)
    c: Coincident(g12,g13)
    c: Coincident(g13,g14)
    c: Coincident(g14,g11)
    c: Parallel(g11,g13)
    c: Distance(g13,g11) = 3
    c: Coincident(g15,g16)
    c: Coincident(g16,g17)
    c: Coincident(g17,g18)
    c: Coincident(g18,g15)
    c: Horizontal(g18)
    c: Parallel(g17,g15)
    c: Distance(g17,g15) = 3
    c: Coincident(g19,g20)
    c: Coincident(g20,g21)
    c: Coincident(g21,g22)
    c: Coincident(g22,g19)
    c: Parallel(g19,g21)
    c: Distance(g21,g19) = 3
    c: Coincident(g23,g24)
    c: Coincident(g24,g25)
    c: Coincident(g25,g26)
    c: Horizontal(g26)
    c: Parallel(g23,g25)
    c: Distance(g25,g23) = 3
    c: PointOnObject(g27,g-1)
    c: Coincident(g27,g28)
    c: PointOnObject(g28,g-1)
    c: Coincident(g28,g29)
    c: Coincident(g29,g30)
    c: Coincident(g30,g27)
    c: Parallel(g27,g29)
    c: Distance(g29,g27) = 3
    c: Coincident(g31,g5)
    c: Coincident(g4,g6)
    c: Equal(g4,g31)
    c: Coincident(g4,g9)
    c: PointOnObject(g31,g8)
    c: Coincident(g4,g31)
    c: Coincident(g26,g23)
    c: Diameter(g32) = 8.2
    c: Coincident(g32,g4)
    c: Diameter(g33) = 8.2
    c: DistanceY(g-1,g33) = 7
    c: DistanceX(g-1,g33) = 185
    c: Diameter(g34) = 13
    c: Coincident(g34,g33)
    c: Coincident(g35,g36)
    c: Coincident(g36,g37)
    c: Vertical(g37)
    c: Vertical(g38)
    c: Coincident(g38,g39)
    c: Horizontal(g39)
    c: Coincident(g39,g40)
    c: PointOnObject(g40,g41)
    c: Vertical(g40)
    c: Vertical(g35)
    c: Distance(g37,g35) = 5
    c: DistanceX(g35,g33) = 2.5
    c: Distance(g38,g40) = 5
    c: DistanceX(g38,g33) = 2.5
    c: Coincident(g41,g37)
    c: Coincident(g34,g35)
    c: Equal(g34,g41)
    c: Coincident(g34,g38)
    c: PointOnObject(g41,g40)
    c: Coincident(g34,g41)
FEATURE [PartDesign::Pad] Pad090
  BaseFeature = -> Pocket113
  Direction = (0,-1,2e-16)
  Length = 7
  Length2 = 10
  Placement = pos=(0,0,0) rot=(1,0,0;1.5708rad)
  Profile = -> Sketch204
  ReferenceAxis = -> Sketch204 [N_Axis]
  Refine = true
  Reversed = true
  Suppressed = false
  Type = 0
FEATURE [Sketcher::SketchObject] Sketch206
  ArcFitTolerance = 1e-06
  AttachmentSupport = -> [Pad090]
  FullyConstrained = false
  MakeInternals = false
  MapMode = 5
  Placement = pos=(35,0,0) rot=(0.707107,0,-0.707107;3.14159rad)
  sketch-geometry (25):
    g0: LineSegment [constr] StartX=-33.5639 StartY=50 StartZ=0 EndX=22.3562 EndY=50 EndZ=0
    g1: LineSegment StartX=-17.0984 StartY=50 StartZ=0 EndX=-16.0002 EndY=50 EndZ=0
    g2: LineSegment StartX=-16.0002 StartY=50 StartZ=0 EndX=5.93914 EndY=8.47552 EndZ=0
    g3: LineSegment StartX=5.93914 StartY=8.47552 StartZ=0 EndX=5.96134 EndY=7.0893 EndZ=0
    g4: LineSegment StartX=5.96134 StartY=7.0893 StartZ=0 EndX=4.40956 EndY=7.0893 EndZ=0
    g5: LineSegment StartX=4.40956 StartY=7.0893 StartZ=0 EndX=-17.1228 EndY=47.8435 EndZ=0
    g6: LineSegment StartX=-17.1228 StartY=47.8435 StartZ=0 EndX=-17.0984 EndY=50 EndZ=0
    g7: LineSegment StartX=-17.1293 StartY=7.10705 StartZ=0 EndX=-17.1293 EndY=9.14543 EndZ=0
    g8: LineSegment StartX=-17.1293 StartY=9.14543 StartZ=0 EndX=4.55828 EndY=50 EndZ=0
    g9: LineSegment StartX=4.55828 StartY=50 StartZ=0 EndX=5.87403 EndY=50.0018 EndZ=0
    g10: LineSegment StartX=5.87403 StartY=50.0018 StartZ=0 EndX=5.93974 EndY=48.3369 EndZ=0
    g11: LineSegment StartX=5.93974 StartY=48.3369 StartZ=0 EndX=-15.9471 EndY=7.10705 EndZ=0
    g12: LineSegment StartX=-15.9471 StartY=7.10705 StartZ=0 EndX=-17.1293 EndY=7.10705 EndZ=0
    g13: LineSegment StartX=-17.1358 StartY=50 StartZ=0 EndX=-15.9776 EndY=50.0877 EndZ=0
    g14: LineSegment StartX=-15.9776 StartY=50.0877 StartZ=0 EndX=5.97119 EndY=97.9201 EndZ=0
    g15: LineSegment StartX=5.97119 StartY=97.9201 StartZ=0 EndX=5.97119 EndY=99.8598 EndZ=0
    g16: LineSegment StartX=5.97119 StartY=99.8598 StartZ=0 EndX=4.66077 EndY=99.8598 EndZ=0
    g17: LineSegment StartX=4.66077 StartY=99.8598 StartZ=0 EndX=-17.1358 EndY=52.3592 EndZ=0
    g18: LineSegment StartX=-17.1358 StartY=52.3592 StartZ=0 EndX=-17.1358 EndY=50 EndZ=0
    g19: LineSegment StartX=-15.9576 StartY=99.8854 StartZ=0 EndX=-17.034 EndY=99.8854 EndZ=0
    g20: LineSegment StartX=-17.034 StartY=99.8854 StartZ=0 EndX=-17.0782 EndY=97.5311 EndZ=0
    g21: LineSegment StartX=-17.0782 StartY=97.5311 StartZ=0 EndX=4.71765 EndY=50 EndZ=0
    g22: LineSegment StartX=4.71765 StartY=50 StartZ=0 EndX=5.8275 EndY=50.1579 EndZ=0
    g23: LineSegment StartX=5.8275 StartY=50.1579 StartZ=0 EndX=5.8275 EndY=52.3779 EndZ=0
    g24: LineSegment StartX=5.8275 StartY=52.3779 StartZ=0 EndX=-15.9576 EndY=99.8854 EndZ=0
  constraints (47):
    c: Horizontal(g0)
    c: DistanceY(g-1,g0) = 50
    c: PointOnObject(g1,g0)
    c: Horizontal(g1)
    c: Coincident(g1,g2)
    c: Coincident(g2,g3)
    c: Coincident(g3,g4)
    c: Horizontal(g4)
    c: Coincident(g4,g5)
    c: Coincident(g5,g6)
    c: Vertical(g7)
    c: Coincident(g7,g8)
    c: PointOnObject(g8,g0)
    c: Coincident(g8,g9)
    c: Coincident(g9,g10)
    c: Coincident(g10,g11)
    c: Coincident(g11,g12)
    c: Coincident(g12,g7)
    c: Horizontal(g12)
    c: Parallel(g5,g2)
    c: Parallel(g8,g11)
    c: Distance(g2,g5) = 2
    c: Distance(g8,g11) = 2
    c: Coincident(g6,g1)
    c: PointOnObject(g13,g0)
    c: Coincident(g13,g14)
    c: Coincident(g14,g15)
    c: Vertical(g15)
    c: Coincident(g15,g16)
    c: Horizontal(g16)
    c: Coincident(g16,g17)
    c: Coincident(g17,g18)
    c: Coincident(g18,g13)
    c: Parallel(g17,g14)
    c: Vertical(g18)
    c: Distance(g14,g17) = 2
    c: Horizontal(g19)
    c: Coincident(g19,g20)
    c: Coincident(g20,g21)
    c: PointOnObject(g21,g0)
    c: Coincident(g21,g22)
    c: Coincident(g22,g23)
    c: Vertical(g23)
    c: Coincident(g23,g24)
    c: Coincident(g24,g19)
    c: Parallel(g24,g21)
    c: Distance(g21,g24) = 2
FEATURE [PartDesign::Pad] Pad091
  BaseFeature = -> Pad090
  Direction = (-1,0,-2e-16)
  Length = 5
  Length2 = 10
  Placement = pos=(0,0,0) rot=(1,0,0;1.5708rad)
  Profile = -> Sketch206
  ReferenceAxis = -> Sketch206 [N_Axis]
  Refine = true
  Reversed = true
  Suppressed = false
  Type = 0
FEATURE [Sketcher::SketchObject] Sketch207
  ArcFitTolerance = 1e-06
  AttachmentSupport = -> [Pad091]
  FullyConstrained = false
  MakeInternals = false
  MapMode = 5
  Placement = pos=(170,0,0) rot=(0.707107,0,0.707107;3.14159rad)
  sketch-geometry (25):
    g0: LineSegment [constr] StartX=-9.20711 StartY=50 StartZ=0 EndX=31.5955 EndY=50 EndZ=0
    g1: LineSegment StartX=-3.23071 StartY=7.09197 StartZ=0 EndX=-2.05702 EndY=7.09197 EndZ=0
    g2: LineSegment StartX=-2.05702 StartY=7.09197 StartZ=0 EndX=18.4375 EndY=47.7755 EndZ=0
    g3: LineSegment StartX=18.4375 StartY=47.7755 StartZ=0 EndX=18.4375 EndY=50 EndZ=0
    g4: LineSegment StartX=18.4375 StartY=50 StartZ=0 EndX=17.3084 EndY=49.9795 EndZ=0
    g5: LineSegment StartX=17.3084 StartY=49.9795 StartZ=0 EndX=-3.23071 EndY=9.20758 EndZ=0
    g6: LineSegment StartX=-3.23071 StartY=9.20758 StartZ=0 EndX=-3.23071 EndY=7.09197 EndZ=0
    g7: LineSegment StartX=17.1226 StartY=7.07983 StartZ=0 EndX=18.4953 EndY=7.07983 EndZ=0
    g8: LineSegment StartX=18.4953 StartY=7.07983 StartZ=0 EndX=18.4953 EndY=8.80663 EndZ=0
    g9: LineSegment StartX=18.4953 StartY=8.80663 StartZ=0 EndX=-2.09857 EndY=50 EndZ=0
    g10: LineSegment StartX=-2.09857 StartY=50 StartZ=0 EndX=-3.17562 EndY=49.9159 EndZ=0
    g11: LineSegment StartX=-3.17562 StartY=49.9159 StartZ=0 EndX=-3.17562 EndY=47.6818 EndZ=0
    g12: LineSegment StartX=-3.17562 StartY=47.6818 StartZ=0 EndX=17.1226 EndY=7.07983 EndZ=0
    g13: LineSegment StartX=-3.19345 StartY=99.8693 StartZ=0 EndX=-2.03057 EndY=99.8693 EndZ=0
    g14: LineSegment StartX=-2.03057 StartY=99.8693 StartZ=0 EndX=18.4277 EndY=53.15 EndZ=0
    g15: LineSegment StartX=18.4277 StartY=53.15 StartZ=0 EndX=18.5025 EndY=50 EndZ=0
    g16: LineSegment StartX=18.5025 StartY=50 StartZ=0 EndX=17.5757 EndY=50.1098 EndZ=0
    g17: LineSegment StartX=17.5757 StartY=50.1098 StartZ=0 EndX=-3.19345 EndY=97.5389 EndZ=0
    g18: LineSegment StartX=-3.19345 StartY=97.5389 StartZ=0 EndX=-3.19345 EndY=99.8693 EndZ=0
    g19: LineSegment StartX=-3.22366 StartY=50 StartZ=0 EndX=-3.22366 EndY=52.3177 EndZ=0
    g20: LineSegment StartX=-3.22366 StartY=52.3177 StartZ=0 EndX=17.471 EndY=99.8606 EndZ=0
    g21: LineSegment StartX=17.471 StartY=99.8606 StartZ=0 EndX=18.4521 EndY=99.8606 EndZ=0
    g22: LineSegment StartX=18.4521 StartY=99.8606 StartZ=0 EndX=18.4521 EndY=97.1035 EndZ=0
    g23: LineSegment StartX=18.4521 StartY=97.1035 StartZ=0 EndX=-2.05909 EndY=49.982 EndZ=0
    g24: LineSegment StartX=-2.05909 StartY=49.982 StartZ=0 EndX=-3.22366 EndY=50 EndZ=0
  constraints (49):
    c: Horizontal(g0)
    c: DistanceY(g-1,g0) = 50
    c: Horizontal(g1)
    c: Coincident(g1,g2)
    c: Coincident(g2,g3)
    c: PointOnObject(g3,g0)
    c: Vertical(g3)
    c: Coincident(g3,g4)
    c: Coincident(g4,g5)
    c: Coincident(g5,g6)
    c: Coincident(g6,g1)
    c: Horizontal(g7)
    c: Coincident(g7,g8)
    c: Vertical(g8)
    c: Coincident(g8,g9)
    c: PointOnObject(g9,g0)
    c: Coincident(g9,g10)
    c: Coincident(g10,g11)
    c: Vertical(g11)
    c: Coincident(g11,g12)
    c: Coincident(g12,g7)
    c: Parallel(g9,g12)
    c: Parallel(g5,g2)
    c: Distance(g2,g5) = 2
    c: Distance(g12,g9) = 2
    c: Vertical(g6)
    c: Horizontal(g13)
    c: Coincident(g13,g14)
    c: Coincident(g14,g15)
    c: PointOnObject(g15,g0)
    c: Coincident(g15,g16)
    c: Coincident(g16,g17)
    c: Coincident(g17,g18)
    c: Coincident(g18,g13)
    c: Vertical(g18)
    c: PointOnObject(g19,g0)
    c: Vertical(g19)
    c: Coincident(g19,g20)
    c: Coincident(g20,g21)
    c: Horizontal(g21)
    c: Coincident(g21,g22)
    c: Vertical(g22)
    c: Coincident(g22,g23)
    c: Coincident(g23,g24)
    c: Coincident(g24,g19)
    c: Parallel(g17,g14)
    c: Parallel(g23,g20)
    c: Distance(g23,g20) = 2
    c: Distance(g14,g17) = 2
FEATURE [PartDesign::Pad] Pad092
  BaseFeature = -> Pad091
  Direction = (1,0,-2e-16)
  Length = 5
  Length2 = 10
  Placement = pos=(0,0,0) rot=(1,0,0;1.5708rad)
  Profile = -> Sketch207
  ReferenceAxis = -> Sketch207 [N_Axis]
  Refine = true
  Reversed = true
  Suppressed = false
  Type = 0
FEATURE [PartDesign::Body] Body040  label="wingspar 007"
  AllowCompound = false
  Group = -> [Sketch201,Pad089,Sketch202,Pocket111,Sketch203,Pocket112,Pocket113,Sketch204,Pad090,Sketch205,Sketch206,Pad091,Sketch207,Pad092]
  Origin = -> Origin040
  Placement = pos=(0,-500,0) rot=(0,0,1;0rad)
  Tip = -> Pad092
FEATURE [PartDesign::Chamfer] Chamfer005
  Angle = 45
  Base = -> Pad076 [Edge188,Edge189]
  BaseFeature = -> Pad076
  ChamferType = 0
  FlipDirection = false
  Placement = pos=(0,0,0) rot=(1,0,0;1.5708rad)
  Refine = true
  Size = 1
  Size2 = 1
  SupportTransform = false
  Suppressed = false
  UseAllEdges = false
FEATURE [PartDesign::Body] Body006  label="wingspar 003"
  AllowCompound = false
  Group = -> [Sketch030,Pad012,Sketch031,Pocket016,Sketch032,Pocket017,Pocket101,Sketch033,Pad013,Sketch177,Sketch178,Pad075,Sketch179,Pad076,Chamfer005]
  Origin = -> Origin006
  Placement = pos=(0,-100,0) rot=(0,0,1;0rad)
  Tip = -> Chamfer005
FEATURE [Sketcher::SketchObject] Sketch208
  ArcFitTolerance = 1e-06
  FullyConstrained = false
  MakeInternals = false
  Placement = pos=(0,0,0) rot=(1,0,0;1.5708rad)
  sketch-geometry (125):
    g0: BSplineCurve PolesCount=62 KnotsCount=62 Degree=3 IsPeriodic=1
    g1-g62: Circle [constr] x62 (B-spline internal-alignment scaffolding for g0; pole/knot coordinates omitted)
    g63-g124: GeomPoint [constr] x62 (B-spline internal-alignment scaffolding for g0; pole/knot coordinates omitted)
  constraints (125):
    c: InternalAlignment(g1,g0)
    c: Weight(g1) = 1
    c: InternalAlignment(g2,g0)
    c: Equal(g2,g1)
    c: InternalAlignment(g3,g0)
    c: Equal(g3,g1)
    c: InternalAlignment(g4,g0)
    c: Equal(g4,g1)
    c: InternalAlignment(g5,g0)
    c: Equal(g5,g1)
    c: InternalAlignment(g6,g0)
    c: Equal(g6,g1)
    c: InternalAlignment(g7,g0)
    c: Equal(g7,g1)
    c: InternalAlignment(g8,g0)
    c: Equal(g8,g1)
    c: InternalAlignment(g9,g0)
    c: Equal(g9,g1)
    c: InternalAlignment(g10,g0)
    c: Equal(g10,g1)
    c: InternalAlignment(g11,g0)
    c: Equal(g11,g1)
    c: InternalAlignment(g12,g0)
    c: Equal(g12,g1)
    c: InternalAlignment(g13,g0)
    c: Equal(g13,g1)
    c: InternalAlignment(g14,g0)
    c: Equal(g14,g1)
    c: InternalAlignment(g15,g0)
    c: Equal(g15,g1)
    c: InternalAlignment(g16,g0)
    c: Equal(g16,g1)
    c: InternalAlignment(g17,g0)
    c: Equal(g17,g1)
    c: InternalAlignment(g18,g0)
    c: Equal(g18,g1)
    c: InternalAlignment(g19,g0)
    c: Equal(g19,g1)
    c: InternalAlignment(g20,g0)
    c: Equal(g20,g1)
    c: InternalAlignment(g21,g0)
    c: Equal(g21,g1)
    c: InternalAlignment(g22,g0)
    c: Equal(g22,g1)
    c: InternalAlignment(g23,g0)
    c: Equal(g23,g1)
    c: InternalAlignment(g24,g0)
    c: Equal(g24,g1)
    c: InternalAlignment(g25,g0)
    c: Equal(g25,g1)
    c: InternalAlignment(g26,g0)
    c: Equal(g26,g1)
    c: InternalAlignment(g27,g0)
    c: Equal(g27,g1)
    c: InternalAlignment(g28,g0)
    c: Equal(g28,g1)
    c: InternalAlignment(g29,g0)
    c: Equal(g29,g1)
    c: InternalAlignment(g30,g0)
    c: Equal(g30,g1)
    c: InternalAlignment(g31,g0)
    c: Equal(g31,g1)
    c: InternalAlignment(g32,g0)
    c: Equal(g32,g1)
    c: InternalAlignment(g33,g0)
    c: Equal(g33,g1)
    c: InternalAlignment(g34,g0)
    c: Equal(g34,g1)
    c: InternalAlignment(g35,g0)
    c: Equal(g35,g1)
    c: InternalAlignment(g36,g0)
    c: Equal(g36,g1)
    c: InternalAlignment(g37,g0)
    c: Equal(g37,g1)
    c: InternalAlignment(g38,g0)
    c: Equal(g38,g1)
    c: InternalAlignment(g39,g0)
    c: Equal(g39,g1)
    c: InternalAlignment(g40,g0)
    c: Equal(g40,g1)
    c: InternalAlignment(g41,g0)
    c: Equal(g41,g1)
    c: InternalAlignment(g42,g0)
    c: Equal(g42,g1)
    c: InternalAlignment(g43,g0)
    c: Equal(g43,g1)
    c: InternalAlignment(g44,g0)
    c: Equal(g44,g1)
    c: InternalAlignment(g45,g0)
    c: Equal(g45,g1)
    c: InternalAlignment(g46,g0)
    c: Equal(g46,g1)
    c: InternalAlignment(g47,g0)
    c: Equal(g47,g1)
    c: InternalAlignment(g48,g0)
    c: Equal(g48,g1)
    c: InternalAlignment(g49,g0)
    c: Equal(g49,g1)
    c: InternalAlignment(g50,g0)
    c: Equal(g50,g1)
    c: InternalAlignment(g51,g0)
    c: Equal(g51,g1)
    c: InternalAlignment(g52,g0)
    c: Equal(g52,g1)
    c: InternalAlignment(g53,g0)
    c: Equal(g53,g1)
    c: InternalAlignment(g54,g0)
    c: Equal(g54,g1)
    c: InternalAlignment(g55,g0)
    c: Equal(g55,g1)
    c: InternalAlignment(g56,g0)
    c: Equal(g56,g1)
    c: InternalAlignment(g57,g0)
    c: Equal(g57,g1)
    c: InternalAlignment(g58,g0)
    c: Equal(g58,g1)
    c: InternalAlignment(g59,g0)
    c: Equal(g59,g1)
    c: InternalAlignment(g60,g0)
    c: Equal(g60,g1)
    c: InternalAlignment(g61,g0)
    c: Equal(g61,g1)
    c: InternalAlignment(g62,g0)
    c: Equal(g62,g1)
    c: InternalAlignment(g63-g124 -> g0) x62
FEATURE [PartDesign::Pad] Pad093
  Direction = (0,-1,2e-16)
  Length = 99.95
  Length2 = 10
  Placement = pos=(0,0,0) rot=(1,0,0;1.5708rad)
  Profile = -> Sketch208
  ReferenceAxis = -> Sketch208 [N_Axis]
  Refine = true
  Suppressed = false
  Type = 0
FEATURE [Sketcher::SketchObject] Sketch209
  ArcFitTolerance = 1e-06
  AttachmentSupport = -> [Pad093]
  FullyConstrained = false
  MakeInternals = false
  MapMode = 5
  Placement = pos=(0,-99.95,2.2e-14) rot=(1,0,0;1.5708rad)
  sketch-geometry (29):
    g0: LineSegment StartX=2.71326 StartY=0.775372 StartZ=0 EndX=3.3867 EndY=1.52303 EndZ=0
    g1: LineSegment StartX=3.3867 StartY=1.52303 StartZ=0 EndX=5.99321 EndY=4.17962 EndZ=0
    g2: LineSegment StartX=5.99321 StartY=4.17962 StartZ=0 EndX=11.2308 EndY=7.18071 EndZ=0
    g3: LineSegment StartX=11.2308 StartY=7.18071 StartZ=0 EndX=18.9287 EndY=10.4927 EndZ=0
    g4: LineSegment StartX=18.9287 StartY=10.4927 StartZ=0 EndX=30.0156 EndY=13.8045 EndZ=0
    g5: LineSegment StartX=30.0156 StartY=13.8045 StartZ=0 EndX=43.7053 EndY=16.6585 EndZ=0
    g6: LineSegment StartX=43.7053 StartY=16.6585 StartZ=0 EndX=58.3753 EndY=18.5837 EndZ=0
    g7: LineSegment StartX=58.3753 StartY=18.5837 StartZ=0 EndX=81.9328 EndY=20.1998 EndZ=0
    g8: LineSegment StartX=81.9328 StartY=20.1998 StartZ=0 EndX=99.116 EndY=20.5815 EndZ=0
    g9: LineSegment StartX=99.116 StartY=20.5815 StartZ=0 EndX=120.506 EndY=20.1998 EndZ=0
    g10: LineSegment StartX=120.506 StartY=20.1998 StartZ=0 EndX=145.772 EndY=18.6559 EndZ=0
    g11: LineSegment StartX=145.772 StartY=18.6559 StartZ=0 EndX=175.748 EndY=15.7728 EndZ=0
    g12: LineSegment StartX=175.748 StartY=15.7728 StartZ=0 EndX=200.436 EndY=12.5699 EndZ=0
    g13: LineSegment StartX=200.436 StartY=12.5699 StartZ=0 EndX=229.384 EndY=8.60252 EndZ=0
    g14: LineSegment StartX=229.384 StartY=8.60252 StartZ=0 EndX=252.135 EndY=5.21302 EndZ=0
    g15: LineSegment StartX=252.135 StartY=5.21302 StartZ=0 EndX=269.07 EndY=2.67143 EndZ=0
    g16: LineSegment StartX=269.07 StartY=2.67143 StartZ=0 EndX=269.07 EndY=1.39956 EndZ=0
    g17: LineSegment StartX=269.07 StartY=1.39956 StartZ=0 EndX=224.761 EndY=0.436598 EndZ=0
    g18: LineSegment StartX=224.761 StartY=0.436598 StartZ=0 EndX=175.487 EndY=-1.02731 EndZ=0
    g19: LineSegment StartX=175.487 StartY=-1.02731 StartZ=0 EndX=123.478 EndY=-2.41293 EndZ=0
    g20: LineSegment StartX=123.478 StartY=-2.41293 StartZ=0 EndX=62.0775 EndY=-3.87655 EndZ=0
    g21: LineSegment StartX=62.0775 StartY=-3.87655 StartZ=0 EndX=32.0529 EndY=-3.76091 EndZ=0
    g22: LineSegment StartX=32.0529 StartY=-3.76091 StartZ=0 EndX=18.888 EndY=-3.18288 EndZ=0
    g23: LineSegment StartX=18.888 StartY=-3.18288 StartZ=0 EndX=12.7286 EndY=-2.48971 EndZ=0
    g24: LineSegment StartX=12.7286 StartY=-2.48971 StartZ=0 EndX=8.49342 EndY=-1.8722 EndZ=0
    g25: LineSegment StartX=8.49342 StartY=-1.8722 StartZ=0 EndX=4.56236 EndY=-0.768246 EndZ=0
    g26: LineSegment StartX=4.56236 StartY=-0.768246 StartZ=0 EndX=3.01395 EndY=-0.301296 EndZ=0
    g27: ArcOfCircle CenterX=3.20505 CenterY=0.332397 CenterZ=0 NormalX=0 NormalY=0 NormalZ=1 AngleXU=0 Radius=0.661881 StartAngle=2.40837 EndAngle=4.41949
    g28: GeomPoint [constr] X=2.01486 Y=0 Z=0
  constraints (32):
    c: PointOnObject(g28,g-1)
    c: Coincident(g0,g1)
    c: Coincident(g1,g2)
    c: Coincident(g2,g3)
    c: Coincident(g3,g4)
    c: Coincident(g4,g5)
    c: Coincident(g5,g6)
    c: Coincident(g6,g7)
    c: Coincident(g7,g8)
    c: Coincident(g8,g9)
    c: Coincident(g9,g10)
    c: Coincident(g10,g11)
    c: Coincident(g11,g12)
    c: Coincident(g12,g13)
    c: Coincident(g13,g14)
    c: Coincident(g14,g15)
    c: Coincident(g15,g16)
    c: Vertical(g16)
    c: Coincident(g16,g17)
    c: Coincident(g17,g18)
    c: Coincident(g18,g19)
    c: Coincident(g19,g20)
    c: Coincident(g20,g21)
    c: Coincident(g21,g22)
    c: Coincident(g22,g23)
    c: Coincident(g23,g24)
    c: Coincident(g24,g25)
    c: Coincident(g25,g26)
    c: PointOnObject(g28,g0)
    c: PointOnObject(g28,g26)
    c: Tangent(g0,g27) = 1.5708
    c: Tangent(g26,g27) = 1.5708
FEATURE [PartDesign::Pocket] Pocket114
  BaseFeature = -> Pad093
  Direction = (0,1,-2e-16)
  Length = 99.95
  Length2 = 5
  Placement = pos=(0,0,0) rot=(1,0,0;1.5708rad)
  Profile = -> Sketch209
  ReferenceAxis = -> Sketch209 [N_Axis]
  Refine = true
  Suppressed = false
  Type = 0
FEATURE [Sketcher::SketchObject] Sketch210
  ArcFitTolerance = 1e-06
  AttachmentSupport = -> [XY_Plane041]
  FullyConstrained = false
  MakeInternals = false
  MapMode = 5
  sketch-geometry (4):
    g0: LineSegment StartX=295 StartY=17.3691 StartZ=0 EndX=295 EndY=-107.641 EndZ=0
    g1: LineSegment StartX=295 StartY=-107.641 StartZ=0 EndX=389.553 EndY=-107.641 EndZ=0
    g2: LineSegment StartX=389.553 StartY=-107.641 StartZ=0 EndX=389.553 EndY=17.3691 EndZ=0
    g3: LineSegment StartX=389.553 StartY=17.3691 StartZ=0 EndX=295 EndY=17.3691 EndZ=0
  constraints (9):
    c: Coincident(g0,g1)
    c: Coincident(g1,g2)
    c: Coincident(g2,g3)
    c: Coincident(g3,g0)
    c: Vertical(g0)
    c: Vertical(g2)
    c: Horizontal(g1)
    c: Horizontal(g3)
    c: DistanceX(g-1,g0) = 295
FEATURE [PartDesign::Pocket] Pocket115
  BaseFeature = -> Pocket114
  Direction = (0,0,-1)
  Length = 5
  Length2 = 5
  Midplane = true
  Placement = pos=(0,0,0) rot=(1,0,0;1.5708rad)
  Profile = -> Sketch210
  ReferenceAxis = -> Sketch210 [N_Axis]
  Refine = true
  Suppressed = false
  Type = 0
FEATURE [Sketcher::SketchObject] Sketch212
  ArcFitTolerance = 1e-06
  AttachmentSupport = -> [XY_Plane041]
  FullyConstrained = true
  MakeInternals = false
  MapMode = 5
  sketch-geometry (12):
    g0: LineSegment StartX=-20 StartY=-7 StartZ=0 EndX=-20 EndY=-117 EndZ=0
    g1: LineSegment StartX=-20 StartY=-117 StartZ=0 EndX=35 EndY=-117 EndZ=0
    g2: LineSegment StartX=35 StartY=-117 StartZ=0 EndX=35 EndY=-7 EndZ=0
    g3: LineSegment StartX=35 StartY=-7 StartZ=0 EndX=-20 EndY=-7 EndZ=0
    g4: LineSegment StartX=40 StartY=-7 StartZ=0 EndX=40 EndY=-117 EndZ=0
    g5: LineSegment StartX=40 StartY=-117 StartZ=0 EndX=165 EndY=-117 EndZ=0
    g6: LineSegment StartX=165 StartY=-117 StartZ=0 EndX=165 EndY=-7 EndZ=0
    g7: LineSegment StartX=165 StartY=-7 StartZ=0 EndX=40 EndY=-7 EndZ=0
    g8: LineSegment StartX=170 StartY=-7 StartZ=0 EndX=170 EndY=-117 EndZ=0
    g9: LineSegment StartX=170 StartY=-117 StartZ=0 EndX=300 EndY=-117 EndZ=0
    g10: LineSegment StartX=300 StartY=-117 StartZ=0 EndX=300 EndY=-7 EndZ=0
    g11: LineSegment StartX=300 StartY=-7 StartZ=0 EndX=170 EndY=-7 EndZ=0
  constraints (36):
    c: Coincident(g0,g1)
    c: Coincident(g1,g2)
    c: Coincident(g2,g3)
    c: Coincident(g3,g0)
    c: Vertical(g0)
    c: Vertical(g2)
    c: Horizontal(g1)
    c: Horizontal(g3)
    c: Coincident(g4,g5)
    c: Coincident(g5,g6)
    c: Coincident(g6,g7)
    c: Coincident(g7,g4)
    c: Vertical(g4)
    c: Vertical(g6)
    c: Horizontal(g5)
    c: Horizontal(g7)
    c: Coincident(g8,g9)
    c: Coincident(g9,g10)
    c: Coincident(g10,g11)
    c: Coincident(g11,g8)
    c: Vertical(g8)
    c: Vertical(g10)
    c: Horizontal(g9)
    c: Horizontal(g11)
    c: DistanceY(g10,g-1) = 7
    c: DistanceY(g6,g-1) = 7
    c: DistanceY(g2,g-1) = 7
    c: DistanceX(g0,g-1) = 20
    c: DistanceY(g0,g0) = 110
    c: Distance(g4,g2) = 5
    c: Distance(g8,g6) = 5
    c: DistanceY(g4,g4) = 110
    c: DistanceY(g8,g8) = 110
    c: DistanceX(g-1,g9) = 300
    c: DistanceX(g-1,g1) = 35
    c: DistanceX(g-1,g5) = 165
FEATURE [PartDesign::Pocket] Pocket116
  BaseFeature = -> Pocket115
  Direction = (0,0,-1)
  Length = 100
  Length2 = 5
  Midplane = true
  Placement = pos=(0,0,0) rot=(1,0,0;1.5708rad)
  Profile = -> Sketch212
  ReferenceAxis = -> Sketch212 [N_Axis]
  Refine = true
  Suppressed = false
  Type = 0
FEATURE [Sketcher::SketchObject] Sketch211
  ArcFitTolerance = 1e-06
  AttachmentSupport = -> [Pocket116]
  FullyConstrained = false
  MakeInternals = false
  MapMode = 5
  Placement = pos=(0,-7,-2.3e-15) rot=(1,0,0;1.5708rad)
  sketch-geometry (42):
    g0: LineSegment StartX=45.884 StartY=17.7219 StartZ=0 EndX=33.93 EndY=-4.65497 EndZ=0
    g1: LineSegment StartX=49.8645 StartY=18.8062 StartZ=0 EndX=37.3312 EndY=-4.65497 EndZ=0
    g2: LineSegment StartX=45.884 StartY=17.7219 StartZ=0 EndX=49.8645 EndY=18.8062 EndZ=0
    g3: LineSegment StartX=33.93 StartY=-4.65497 StartZ=0 EndX=37.3312 EndY=-4.65497 EndZ=0
    g4: ArcOfCircle CenterX=18 CenterY=3 CenterZ=0 NormalX=0 NormalY=0 NormalZ=1 AngleXU=0 Radius=6.5 StartAngle=2.58175 EndAngle=4.38597
    g5: LineSegment StartX=20.6963 StartY=8.91437 StartZ=0 EndX=19.1912 EndY=11.3613 EndZ=0
    g6: LineSegment StartX=12.4923 StartY=6.45183 StartZ=0 EndX=11.7252 EndY=8.2111 EndZ=0
    g7: LineSegment StartX=11.7252 StartY=8.2111 StartZ=0 EndX=19.1912 EndY=11.3613 EndZ=0
    g8: LineSegment StartX=23.9272 StartY=0.331954 StartZ=0 EndX=26.093 EndY=-4.58272 EndZ=0
    g9: LineSegment StartX=15.9158 StartY=-3.15679 StartZ=0 EndX=16.6159 EndY=-4.58272 EndZ=0
    g10: LineSegment StartX=16.6159 StartY=-4.58272 StartZ=0 EndX=26.093 EndY=-4.58272 EndZ=0
    g11: LineSegment StartX=74.8373 StartY=20.9684 StartZ=0 EndX=89.2063 EndY=-4.24973 EndZ=0
    g12: LineSegment StartX=89.2063 StartY=-4.24973 StartZ=0 EndX=92.6591 EndY=-4.24973 EndZ=0
    g13: LineSegment StartX=92.6591 StartY=-4.24973 StartZ=0 EndX=78.184 EndY=21.1546 EndZ=0
    g14: LineSegment StartX=78.184 StartY=21.1546 StartZ=0 EndX=74.8373 EndY=20.9684 EndZ=0
    g15: LineSegment StartX=113.372 StartY=-3.61742 StartZ=0 EndX=125.992 EndY=20.9865 EndZ=0
    g16: LineSegment StartX=125.992 StartY=20.9865 StartZ=0 EndX=129.338 EndY=20.9348 EndZ=0
    g17: LineSegment StartX=129.338 StartY=20.9348 StartZ=0 EndX=116.743 EndY=-3.61742 EndZ=0
    g18: LineSegment StartX=116.743 StartY=-3.61742 StartZ=0 EndX=113.372 EndY=-3.61742 EndZ=0
    g19: LineSegment StartX=156.49 StartY=19.0126 StartZ=0 EndX=171.224 EndY=-2.18705 EndZ=0
    g20: LineSegment StartX=171.224 StartY=-2.18705 StartZ=0 EndX=175.064 EndY=-2.45586 EndZ=0
    g21: LineSegment StartX=175.064 StartY=-2.45586 StartZ=0 EndX=160.386 EndY=18.6636 EndZ=0
    g22: LineSegment StartX=160.386 StartY=18.6636 StartZ=0 EndX=156.49 EndY=19.0126 EndZ=0
    g23: LineSegment StartX=195.991 StartY=-1.14503 StartZ=0 EndX=209.19 EndY=12.3205 EndZ=0
    g24: LineSegment StartX=209.19 StartY=12.3205 StartZ=0 EndX=213.44 EndY=12.3702 EndZ=0
    g25: LineSegment StartX=213.44 StartY=12.3702 StartZ=0 EndX=200.192 EndY=-1.14503 EndZ=0
    g26: LineSegment StartX=200.192 StartY=-1.14503 StartZ=0 EndX=195.991 EndY=-1.14503 EndZ=0
    g27: LineSegment StartX=229.838 StartY=9.19446 StartZ=0 EndX=237.096 EndY=0 EndZ=0
    g28: LineSegment StartX=237.096 StartY=0 StartZ=0 EndX=240.918 EndY=0 EndZ=0
    g29: LineSegment StartX=240.918 StartY=0 StartZ=0 EndX=234.226 EndY=8.47688 EndZ=0
    g30: LineSegment StartX=234.226 StartY=8.47688 StartZ=0 EndX=229.838 EndY=9.19446 EndZ=0
    g31: ArcOfCircle CenterX=18 CenterY=3 CenterZ=0 NormalX=0 NormalY=0 NormalZ=1 AngleXU=0 Radius=6.5 StartAngle=5.86022 EndAngle=7.42624
    g32: Circle CenterX=18 CenterY=3 CenterZ=0 NormalX=0 NormalY=0 NormalZ=1 AngleXU=0 Radius=4.1
    g33: Circle CenterX=185 CenterY=7 CenterZ=0 NormalX=0 NormalY=0 NormalZ=1 AngleXU=0 Radius=4.1
    g34: ArcOfCircle CenterX=185 CenterY=7 CenterZ=0 NormalX=0 NormalY=0 NormalZ=1 AngleXU=0 Radius=6.5 StartAngle=1.96559 EndAngle=4.3176
    g35: LineSegment StartX=182.5 StartY=13 StartZ=0 EndX=182.5 EndY=15.9367 EndZ=0
    g36: LineSegment StartX=182.5 StartY=15.9367 StartZ=0 EndX=187.5 EndY=15.5349 EndZ=0
    g37: LineSegment StartX=187.5 StartY=15.5349 StartZ=0 EndX=187.5 EndY=13 EndZ=0
    g38: LineSegment StartX=182.5 StartY=1 StartZ=0 EndX=182.5 EndY=-1.79994 EndZ=0
    g39: LineSegment StartX=182.5 StartY=-1.79994 StartZ=0 EndX=187.5 EndY=-1.79994 EndZ=0
    g40: LineSegment StartX=187.5 StartY=-1.79994 StartZ=0 EndX=187.5 EndY=1 EndZ=0
    g41: ArcOfCircle CenterX=185 CenterY=7 CenterZ=0 NormalX=0 NormalY=0 NormalZ=1 AngleXU=0 Radius=6.5 StartAngle=5.10718 EndAngle=7.45919
  constraints (84):
    c: Coincident(g2,g0)
    c: Coincident(g2,g1)
    c: Coincident(g3,g0)
    c: Coincident(g3,g1)
    c: Horizontal(g3)
    c: Parallel(g0,g1)
    c: Distance(g1,g0) = 3
    c: Diameter(g4) = 13
    c: DistanceY(g-1,g4) = 3
    c: DistanceX(g-1,g4) = 18
    c: Coincident(g7,g6)
    c: Coincident(g7,g5)
    c: PointOnObject(g8,g31)
    c: Coincident(g10,g9)
    c: Horizontal(g10)
    c: Coincident(g10,g8)
    c: Coincident(g11,g12)
    c: Horizontal(g12)
    c: Coincident(g12,g13)
    c: Coincident(g13,g14)
    c: Coincident(g14,g11)
    c: Parallel(g11,g13)
    c: Distance(g13,g11) = 3
    c: Coincident(g15,g16)
    c: Coincident(g16,g17)
    c: Coincident(g17,g18)
    c: Coincident(g18,g15)
    c: Horizontal(g18)
    c: Parallel(g17,g15)
    c: Distance(g17,g15) = 3
    c: Coincident(g19,g20)
    c: Coincident(g20,g21)
    c: Coincident(g21,g22)
    c: Coincident(g22,g19)
    c: Parallel(g19,g21)
    c: Distance(g21,g19) = 3
    c: Coincident(g23,g24)
    c: Coincident(g24,g25)
    c: Coincident(g25,g26)
    c: Horizontal(g26)
    c: Parallel(g23,g25)
    c: Distance(g25,g23) = 3
    c: PointOnObject(g27,g-1)
    c: Coincident(g27,g28)
    c: PointOnObject(g28,g-1)
    c: Coincident(g28,g29)
    c: Coincident(g29,g30)
    c: Coincident(g30,g27)
    c: Parallel(g27,g29)
    c: Distance(g29,g27) = 3
    c: Coincident(g31,g5)
    c: Coincident(g4,g6)
    c: Equal(g4,g31)
    c: Coincident(g4,g9)
    c: PointOnObject(g31,g8)
    c: Coincident(g4,g31)
    c: Coincident(g26,g23)
    c: Diameter(g32) = 8.2
    c: Coincident(g32,g4)
    c: Diameter(g33) = 8.2
    c: DistanceY(g-1,g33) = 7
    c: DistanceX(g-1,g33) = 185
    c: Diameter(g34) = 13
    c: Coincident(g34,g33)
    c: Coincident(g35,g36)
    c: Coincident(g36,g37)
    c: Vertical(g37)
    c: Vertical(g38)
    c: Coincident(g38,g39)
    c: Horizontal(g39)
    c: Coincident(g39,g40)
    c: PointOnObject(g40,g41)
    c: Vertical(g40)
    c: Vertical(g35)
    c: Distance(g37,g35) = 5
    c: DistanceX(g35,g33) = 2.5
    c: Distance(g38,g40) = 5
    c: DistanceX(g38,g33) = 2.5
    c: Coincident(g41,g37)
    c: Coincident(g34,g35)
    c: Equal(g34,g41)
    c: Coincident(g34,g38)
    c: PointOnObject(g41,g40)
    c: Coincident(g34,g41)
FEATURE [PartDesign::Pad] Pad094
  BaseFeature = -> Pocket116
  Direction = (0,-1,2e-16)
  Length = 7
  Length2 = 10
  Placement = pos=(0,0,0) rot=(1,0,0;1.5708rad)
  Profile = -> Sketch211
  ReferenceAxis = -> Sketch211 [N_Axis]
  Refine = true
  Reversed = true
  Suppressed = false
  Type = 0
FEATURE [Sketcher::SketchObject] Sketch213
  ArcFitTolerance = 1e-06
  AttachmentSupport = -> [Pad094]
  FullyConstrained = false
  MakeInternals = false
  MapMode = 5
  Placement = pos=(35,0,0) rot=(0.707107,0,-0.707107;3.14159rad)
  sketch-geometry (25):
    g0: LineSegment [constr] StartX=-33.5639 StartY=50 StartZ=0 EndX=22.3562 EndY=50 EndZ=0
    g1: LineSegment StartX=-17.0984 StartY=50 StartZ=0 EndX=-16.0002 EndY=50 EndZ=0
    g2: LineSegment StartX=-16.0002 StartY=50 StartZ=0 EndX=5.93914 EndY=8.47552 EndZ=0
    g3: LineSegment StartX=5.93914 StartY=8.47552 StartZ=0 EndX=5.96134 EndY=7.0893 EndZ=0
    g4: LineSegment StartX=5.96134 StartY=7.0893 StartZ=0 EndX=4.40956 EndY=7.0893 EndZ=0
    g5: LineSegment StartX=4.40956 StartY=7.0893 StartZ=0 EndX=-17.1228 EndY=47.8435 EndZ=0
    g6: LineSegment StartX=-17.1228 StartY=47.8435 StartZ=0 EndX=-17.0984 EndY=50 EndZ=0
    g7: LineSegment StartX=-17.1293 StartY=7.10705 StartZ=0 EndX=-17.1293 EndY=9.14543 EndZ=0
    g8: LineSegment StartX=-17.1293 StartY=9.14543 StartZ=0 EndX=4.55828 EndY=50 EndZ=0
    g9: LineSegment StartX=4.55828 StartY=50 StartZ=0 EndX=5.87403 EndY=50.0018 EndZ=0
    g10: LineSegment StartX=5.87403 StartY=50.0018 StartZ=0 EndX=5.93974 EndY=48.3369 EndZ=0
    g11: LineSegment StartX=5.93974 StartY=48.3369 StartZ=0 EndX=-15.9471 EndY=7.10705 EndZ=0
    g12: LineSegment StartX=-15.9471 StartY=7.10705 StartZ=0 EndX=-17.1293 EndY=7.10705 EndZ=0
    g13: LineSegment StartX=-17.1358 StartY=50 StartZ=0 EndX=-15.9776 EndY=50.0877 EndZ=0
    g14: LineSegment StartX=-15.9776 StartY=50.0877 StartZ=0 EndX=5.97119 EndY=97.9201 EndZ=0
    g15: LineSegment StartX=5.97119 StartY=97.9201 StartZ=0 EndX=5.97119 EndY=99.8598 EndZ=0
    g16: LineSegment StartX=5.97119 StartY=99.8598 StartZ=0 EndX=4.66077 EndY=99.8598 EndZ=0
    g17: LineSegment StartX=4.66077 StartY=99.8598 StartZ=0 EndX=-17.1358 EndY=52.3592 EndZ=0
    g18: LineSegment StartX=-17.1358 StartY=52.3592 StartZ=0 EndX=-17.1358 EndY=50 EndZ=0
    g19: LineSegment StartX=-15.9576 StartY=99.8854 StartZ=0 EndX=-17.034 EndY=99.8854 EndZ=0
    g20: LineSegment StartX=-17.034 StartY=99.8854 StartZ=0 EndX=-17.0782 EndY=97.5311 EndZ=0
    g21: LineSegment StartX=-17.0782 StartY=97.5311 StartZ=0 EndX=4.71765 EndY=50 EndZ=0
    g22: LineSegment StartX=4.71765 StartY=50 StartZ=0 EndX=5.8275 EndY=50.1579 EndZ=0
    g23: LineSegment StartX=5.8275 StartY=50.1579 StartZ=0 EndX=5.8275 EndY=52.3779 EndZ=0
    g24: LineSegment StartX=5.8275 StartY=52.3779 StartZ=0 EndX=-15.9576 EndY=99.8854 EndZ=0
  constraints (47):
    c: Horizontal(g0)
    c: DistanceY(g-1,g0) = 50
    c: PointOnObject(g1,g0)
    c: Horizontal(g1)
    c: Coincident(g1,g2)
    c: Coincident(g2,g3)
    c: Coincident(g3,g4)
    c: Horizontal(g4)
    c: Coincident(g4,g5)
    c: Coincident(g5,g6)
    c: Vertical(g7)
    c: Coincident(g7,g8)
    c: PointOnObject(g8,g0)
    c: Coincident(g8,g9)
    c: Coincident(g9,g10)
    c: Coincident(g10,g11)
    c: Coincident(g11,g12)
    c: Coincident(g12,g7)
    c: Horizontal(g12)
    c: Parallel(g5,g2)
    c: Parallel(g8,g11)
    c: Distance(g2,g5) = 2
    c: Distance(g8,g11) = 2
    c: Coincident(g6,g1)
    c: PointOnObject(g13,g0)
    c: Coincident(g13,g14)
    c: Coincident(g14,g15)
    c: Vertical(g15)
    c: Coincident(g15,g16)
    c: Horizontal(g16)
    c: Coincident(g16,g17)
    c: Coincident(g17,g18)
    c: Coincident(g18,g13)
    c: Parallel(g17,g14)
    c: Vertical(g18)
    c: Distance(g14,g17) = 2
    c: Horizontal(g19)
    c: Coincident(g19,g20)
    c: Coincident(g20,g21)
    c: PointOnObject(g21,g0)
    c: Coincident(g21,g22)
    c: Coincident(g22,g23)
    c: Vertical(g23)
    c: Coincident(g23,g24)
    c: Coincident(g24,g19)
    c: Parallel(g24,g21)
    c: Distance(g21,g24) = 2
FEATURE [PartDesign::Pad] Pad095
  BaseFeature = -> Pad094
  Direction = (-1,0,-2e-16)
  Length = 5
  Length2 = 10
  Placement = pos=(0,0,0) rot=(1,0,0;1.5708rad)
  Profile = -> Sketch213
  ReferenceAxis = -> Sketch213 [N_Axis]
  Refine = true
  Reversed = true
  Suppressed = false
  Type = 0
FEATURE [Sketcher::SketchObject] Sketch214
  ArcFitTolerance = 1e-06
  AttachmentSupport = -> [Pad095]
  FullyConstrained = false
  MakeInternals = false
  MapMode = 5
  Placement = pos=(170,0,0) rot=(0.707107,0,0.707107;3.14159rad)
  sketch-geometry (25):
    g0: LineSegment [constr] StartX=-9.20711 StartY=50 StartZ=0 EndX=31.5955 EndY=50 EndZ=0
    g1: LineSegment StartX=-3.23071 StartY=7.09197 StartZ=0 EndX=-2.05702 EndY=7.09197 EndZ=0
    g2: LineSegment StartX=-2.05702 StartY=7.09197 StartZ=0 EndX=18.4375 EndY=47.7755 EndZ=0
    g3: LineSegment StartX=18.4375 StartY=47.7755 StartZ=0 EndX=18.4375 EndY=50 EndZ=0
    g4: LineSegment StartX=18.4375 StartY=50 StartZ=0 EndX=17.3084 EndY=49.9795 EndZ=0
    g5: LineSegment StartX=17.3084 StartY=49.9795 StartZ=0 EndX=-3.23071 EndY=9.20758 EndZ=0
    g6: LineSegment StartX=-3.23071 StartY=9.20758 StartZ=0 EndX=-3.23071 EndY=7.09197 EndZ=0
    g7: LineSegment StartX=17.1226 StartY=7.07983 StartZ=0 EndX=18.4953 EndY=7.07983 EndZ=0
    g8: LineSegment StartX=18.4953 StartY=7.07983 StartZ=0 EndX=18.4953 EndY=8.80663 EndZ=0
    g9: LineSegment StartX=18.4953 StartY=8.80663 StartZ=0 EndX=-2.09857 EndY=50 EndZ=0
    g10: LineSegment StartX=-2.09857 StartY=50 StartZ=0 EndX=-3.17562 EndY=49.9159 EndZ=0
    g11: LineSegment StartX=-3.17562 StartY=49.9159 StartZ=0 EndX=-3.17562 EndY=47.6818 EndZ=0
    g12: LineSegment StartX=-3.17562 StartY=47.6818 StartZ=0 EndX=17.1226 EndY=7.07983 EndZ=0
    g13: LineSegment StartX=-3.19345 StartY=99.8693 StartZ=0 EndX=-2.03057 EndY=99.8693 EndZ=0
    g14: LineSegment StartX=-2.03057 StartY=99.8693 StartZ=0 EndX=18.4277 EndY=53.15 EndZ=0
    g15: LineSegment StartX=18.4277 StartY=53.15 StartZ=0 EndX=18.5025 EndY=50 EndZ=0
    g16: LineSegment StartX=18.5025 StartY=50 StartZ=0 EndX=17.5757 EndY=50.1098 EndZ=0
    g17: LineSegment StartX=17.5757 StartY=50.1098 StartZ=0 EndX=-3.19345 EndY=97.5389 EndZ=0
    g18: LineSegment StartX=-3.19345 StartY=97.5389 StartZ=0 EndX=-3.19345 EndY=99.8693 EndZ=0
    g19: LineSegment StartX=-3.22366 StartY=50 StartZ=0 EndX=-3.22366 EndY=52.3177 EndZ=0
    g20: LineSegment StartX=-3.22366 StartY=52.3177 StartZ=0 EndX=17.471 EndY=99.8606 EndZ=0
    g21: LineSegment StartX=17.471 StartY=99.8606 StartZ=0 EndX=18.4521 EndY=99.8606 EndZ=0
    g22: LineSegment StartX=18.4521 StartY=99.8606 StartZ=0 EndX=18.4521 EndY=97.1035 EndZ=0
    g23: LineSegment StartX=18.4521 StartY=97.1035 StartZ=0 EndX=-2.05909 EndY=49.982 EndZ=0
    g24: LineSegment StartX=-2.05909 StartY=49.982 StartZ=0 EndX=-3.22366 EndY=50 EndZ=0
  constraints (49):
    c: Horizontal(g0)
    c: DistanceY(g-1,g0) = 50
    c: Horizontal(g1)
    c: Coincident(g1,g2)
    c: Coincident(g2,g3)
    c: PointOnObject(g3,g0)
    c: Vertical(g3)
    c: Coincident(g3,g4)
    c: Coincident(g4,g5)
    c: Coincident(g5,g6)
    c: Coincident(g6,g1)
    c: Horizontal(g7)
    c: Coincident(g7,g8)
    c: Vertical(g8)
    c: Coincident(g8,g9)
    c: PointOnObject(g9,g0)
    c: Coincident(g9,g10)
    c: Coincident(g10,g11)
    c: Vertical(g11)
    c: Coincident(g11,g12)
    c: Coincident(g12,g7)
    c: Parallel(g9,g12)
    c: Parallel(g5,g2)
    c: Distance(g2,g5) = 2
    c: Distance(g12,g9) = 2
    c: Vertical(g6)
    c: Horizontal(g13)
    c: Coincident(g13,g14)
    c: Coincident(g14,g15)
    c: PointOnObject(g15,g0)
    c: Coincident(g15,g16)
    c: Coincident(g16,g17)
    c: Coincident(g17,g18)
    c: Coincident(g18,g13)
    c: Vertical(g18)
    c: PointOnObject(g19,g0)
    c: Vertical(g19)
    c: Coincident(g19,g20)
    c: Coincident(g20,g21)
    c: Horizontal(g21)
    c: Coincident(g21,g22)
    c: Vertical(g22)
    c: Coincident(g22,g23)
    c: Coincident(g23,g24)
    c: Coincident(g24,g19)
    c: Parallel(g17,g14)
    c: Parallel(g23,g20)
    c: Distance(g23,g20) = 2
    c: Distance(g14,g17) = 2
FEATURE [PartDesign::Pad] Pad096
  BaseFeature = -> Pad095
  Direction = (1,0,-2e-16)
  Length = 5
  Length2 = 10
  Placement = pos=(0,0,0) rot=(1,0,0;1.5708rad)
  Profile = -> Sketch214
  ReferenceAxis = -> Sketch214 [N_Axis]
  Refine = true
  Reversed = true
  Suppressed = false
  Type = 0
FEATURE [Sketcher::SketchObject] Sketch215
  ArcFitTolerance = 1e-06
  AttachmentSupport = -> [XY_Plane041]
  FullyConstrained = false
  MakeInternals = false
  MapMode = 5
  sketch-geometry (4):
    g0: LineSegment StartX=192 StartY=42.6691 StartZ=0 EndX=192 EndY=-48.1885 EndZ=0
    g1: LineSegment StartX=192 StartY=-48.1885 StartZ=0 EndX=335.25 EndY=-48.1885 EndZ=0
    g2: LineSegment StartX=335.25 StartY=-48.1885 StartZ=0 EndX=335.25 EndY=42.6691 EndZ=0
    g3: LineSegment StartX=335.25 StartY=42.6691 StartZ=0 EndX=192 EndY=42.6691 EndZ=0
  constraints (9):
    c: Coincident(g0,g1)
    c: Coincident(g1,g2)
    c: Coincident(g2,g3)
    c: Coincident(g3,g0)
    c: Vertical(g0)
    c: Vertical(g2)
    c: Horizontal(g1)
    c: Horizontal(g3)
    c: DistanceX(g-1,g0) = 192
FEATURE [PartDesign::Pocket] Pocket117
  BaseFeature = -> Pad096
  Direction = (0,0,-1)
  Length = 100
  Length2 = 5
  Midplane = true
  Placement = pos=(0,0,0) rot=(1,0,0;1.5708rad)
  Profile = -> Sketch215
  ReferenceAxis = -> Sketch215 [N_Axis]
  Refine = true
  Suppressed = false
  Type = 0
FEATURE [PartDesign::Body] Body041  label="wingspar 009"
  AllowCompound = false
  Group = -> [Sketch208,Pad093,Sketch209,Pocket114,Sketch210,Pocket115,Pocket116,Sketch211,Pad094,Sketch212,Sketch213,Pad095,Sketch214,Pad096,Sketch215,Pocket117]
  Origin = -> Origin041
  Placement = pos=(0,-700,0) rot=(0,0,1;0rad)
  Tip = -> Pocket117
FEATURE [Sketcher::SketchObject] Sketch216
  ArcFitTolerance = 1e-06
  FullyConstrained = false
  MakeInternals = false
  Placement = pos=(0,0,0) rot=(1,0,0;1.5708rad)
  sketch-geometry (125):
    g0: BSplineCurve PolesCount=62 KnotsCount=62 Degree=3 IsPeriodic=1
    g1-g62: Circle [constr] x62 (B-spline internal-alignment scaffolding for g0; pole/knot coordinates omitted)
    g63-g124: GeomPoint [constr] x62 (B-spline internal-alignment scaffolding for g0; pole/knot coordinates omitted)
  constraints (125):
    c: InternalAlignment(g1,g0)
    c: Weight(g1) = 1
    c: InternalAlignment(g2,g0)
    c: Equal(g2,g1)
    c: InternalAlignment(g3,g0)
    c: Equal(g3,g1)
    c: InternalAlignment(g4,g0)
    c: Equal(g4,g1)
    c: InternalAlignment(g5,g0)
    c: Equal(g5,g1)
    c: InternalAlignment(g6,g0)
    c: Equal(g6,g1)
    c: InternalAlignment(g7,g0)
    c: Equal(g7,g1)
    c: InternalAlignment(g8,g0)
    c: Equal(g8,g1)
    c: InternalAlignment(g9,g0)
    c: Equal(g9,g1)
    c: InternalAlignment(g10,g0)
    c: Equal(g10,g1)
    c: InternalAlignment(g11,g0)
    c: Equal(g11,g1)
    c: InternalAlignment(g12,g0)
    c: Equal(g12,g1)
    c: InternalAlignment(g13,g0)
    c: Equal(g13,g1)
    c: InternalAlignment(g14,g0)
    c: Equal(g14,g1)
    c: InternalAlignment(g15,g0)
    c: Equal(g15,g1)
    c: InternalAlignment(g16,g0)
    c: Equal(g16,g1)
    c: InternalAlignment(g17,g0)
    c: Equal(g17,g1)
    c: InternalAlignment(g18,g0)
    c: Equal(g18,g1)
    c: InternalAlignment(g19,g0)
    c: Equal(g19,g1)
    c: InternalAlignment(g20,g0)
    c: Equal(g20,g1)
    c: InternalAlignment(g21,g0)
    c: Equal(g21,g1)
    c: InternalAlignment(g22,g0)
    c: Equal(g22,g1)
    c: InternalAlignment(g23,g0)
    c: Equal(g23,g1)
    c: InternalAlignment(g24,g0)
    c: Equal(g24,g1)
    c: InternalAlignment(g25,g0)
    c: Equal(g25,g1)
    c: InternalAlignment(g26,g0)
    c: Equal(g26,g1)
    c: InternalAlignment(g27,g0)
    c: Equal(g27,g1)
    c: InternalAlignment(g28,g0)
    c: Equal(g28,g1)
    c: InternalAlignment(g29,g0)
    c: Equal(g29,g1)
    c: InternalAlignment(g30,g0)
    c: Equal(g30,g1)
    c: InternalAlignment(g31,g0)
    c: Equal(g31,g1)
    c: InternalAlignment(g32,g0)
    c: Equal(g32,g1)
    c: InternalAlignment(g33,g0)
    c: Equal(g33,g1)
    c: InternalAlignment(g34,g0)
    c: Equal(g34,g1)
    c: InternalAlignment(g35,g0)
    c: Equal(g35,g1)
    c: InternalAlignment(g36,g0)
    c: Equal(g36,g1)
    c: InternalAlignment(g37,g0)
    c: Equal(g37,g1)
    c: InternalAlignment(g38,g0)
    c: Equal(g38,g1)
    c: InternalAlignment(g39,g0)
    c: Equal(g39,g1)
    c: InternalAlignment(g40,g0)
    c: Equal(g40,g1)
    c: InternalAlignment(g41,g0)
    c: Equal(g41,g1)
    c: InternalAlignment(g42,g0)
    c: Equal(g42,g1)
    c: InternalAlignment(g43,g0)
    c: Equal(g43,g1)
    c: InternalAlignment(g44,g0)
    c: Equal(g44,g1)
    c: InternalAlignment(g45,g0)
    c: Equal(g45,g1)
    c: InternalAlignment(g46,g0)
    c: Equal(g46,g1)
    c: InternalAlignment(g47,g0)
    c: Equal(g47,g1)
    c: InternalAlignment(g48,g0)
    c: Equal(g48,g1)
    c: InternalAlignment(g49,g0)
    c: Equal(g49,g1)
    c: InternalAlignment(g50,g0)
    c: Equal(g50,g1)
    c: InternalAlignment(g51,g0)
    c: Equal(g51,g1)
    c: InternalAlignment(g52,g0)
    c: Equal(g52,g1)
    c: InternalAlignment(g53,g0)
    c: Equal(g53,g1)
    c: InternalAlignment(g54,g0)
    c: Equal(g54,g1)
    c: InternalAlignment(g55,g0)
    c: Equal(g55,g1)
    c: InternalAlignment(g56,g0)
    c: Equal(g56,g1)
    c: InternalAlignment(g57,g0)
    c: Equal(g57,g1)
    c: InternalAlignment(g58,g0)
    c: Equal(g58,g1)
    c: InternalAlignment(g59,g0)
    c: Equal(g59,g1)
    c: InternalAlignment(g60,g0)
    c: Equal(g60,g1)
    c: InternalAlignment(g61,g0)
    c: Equal(g61,g1)
    c: InternalAlignment(g62,g0)
    c: Equal(g62,g1)
    c: InternalAlignment(g63-g124 -> g0) x62
FEATURE [PartDesign::Pad] Pad097
  Direction = (0,-1,2e-16)
  Length = 99.95
  Length2 = 10
  Placement = pos=(0,0,0) rot=(1,0,0;1.5708rad)
  Profile = -> Sketch216
  ReferenceAxis = -> Sketch216 [N_Axis]
  Refine = true
  Suppressed = false
  Type = 0
FEATURE [Sketcher::SketchObject] Sketch217
  ArcFitTolerance = 1e-06
  AttachmentSupport = -> [Pad097]
  FullyConstrained = false
  MakeInternals = false
  MapMode = 5
  Placement = pos=(0,-99.95,2.2e-14) rot=(1,0,0;1.5708rad)
  sketch-geometry (29):
    g0: LineSegment StartX=2.71326 StartY=0.775372 StartZ=0 EndX=3.3867 EndY=1.52303 EndZ=0
    g1: LineSegment StartX=3.3867 StartY=1.52303 StartZ=0 EndX=5.99321 EndY=4.17962 EndZ=0
    g2: LineSegment StartX=5.99321 StartY=4.17962 StartZ=0 EndX=11.2308 EndY=7.18071 EndZ=0
    g3: LineSegment StartX=11.2308 StartY=7.18071 StartZ=0 EndX=18.9287 EndY=10.4927 EndZ=0
    g4: LineSegment StartX=18.9287 StartY=10.4927 StartZ=0 EndX=30.0156 EndY=13.8045 EndZ=0
    g5: LineSegment StartX=30.0156 StartY=13.8045 StartZ=0 EndX=43.7053 EndY=16.6585 EndZ=0
    g6: LineSegment StartX=43.7053 StartY=16.6585 StartZ=0 EndX=58.3753 EndY=18.5837 EndZ=0
    g7: LineSegment StartX=58.3753 StartY=18.5837 StartZ=0 EndX=81.9328 EndY=20.1998 EndZ=0
    g8: LineSegment StartX=81.9328 StartY=20.1998 StartZ=0 EndX=99.116 EndY=20.5815 EndZ=0
    g9: LineSegment StartX=99.116 StartY=20.5815 StartZ=0 EndX=120.506 EndY=20.1998 EndZ=0
    g10: LineSegment StartX=120.506 StartY=20.1998 StartZ=0 EndX=145.772 EndY=18.6559 EndZ=0
    g11: LineSegment StartX=145.772 StartY=18.6559 StartZ=0 EndX=175.748 EndY=15.7728 EndZ=0
    g12: LineSegment StartX=175.748 StartY=15.7728 StartZ=0 EndX=200.436 EndY=12.5699 EndZ=0
    g13: LineSegment StartX=200.436 StartY=12.5699 StartZ=0 EndX=229.384 EndY=8.60252 EndZ=0
    g14: LineSegment StartX=229.384 StartY=8.60252 StartZ=0 EndX=252.135 EndY=5.21302 EndZ=0
    g15: LineSegment StartX=252.135 StartY=5.21302 StartZ=0 EndX=269.07 EndY=2.67143 EndZ=0
    g16: LineSegment StartX=269.07 StartY=2.67143 StartZ=0 EndX=269.07 EndY=1.39956 EndZ=0
    g17: LineSegment StartX=269.07 StartY=1.39956 StartZ=0 EndX=224.761 EndY=0.436598 EndZ=0
    g18: LineSegment StartX=224.761 StartY=0.436598 StartZ=0 EndX=175.487 EndY=-1.02731 EndZ=0
    g19: LineSegment StartX=175.487 StartY=-1.02731 StartZ=0 EndX=123.478 EndY=-2.41293 EndZ=0
    g20: LineSegment StartX=123.478 StartY=-2.41293 StartZ=0 EndX=62.0775 EndY=-3.87655 EndZ=0
    g21: LineSegment StartX=62.0775 StartY=-3.87655 StartZ=0 EndX=32.0529 EndY=-3.76091 EndZ=0
    g22: LineSegment StartX=32.0529 StartY=-3.76091 StartZ=0 EndX=18.888 EndY=-3.18288 EndZ=0
    g23: LineSegment StartX=18.888 StartY=-3.18288 StartZ=0 EndX=12.7286 EndY=-2.48971 EndZ=0
    g24: LineSegment StartX=12.7286 StartY=-2.48971 StartZ=0 EndX=8.49342 EndY=-1.8722 EndZ=0
    g25: LineSegment StartX=8.49342 StartY=-1.8722 StartZ=0 EndX=4.56236 EndY=-0.768246 EndZ=0
    g26: LineSegment StartX=4.56236 StartY=-0.768246 StartZ=0 EndX=3.01395 EndY=-0.301296 EndZ=0
    g27: ArcOfCircle CenterX=3.20505 CenterY=0.332397 CenterZ=0 NormalX=0 NormalY=0 NormalZ=1 AngleXU=0 Radius=0.661881 StartAngle=2.40837 EndAngle=4.41949
    g28: GeomPoint [constr] X=2.01486 Y=0 Z=0
  constraints (32):
    c: PointOnObject(g28,g-1)
    c: Coincident(g0,g1)
    c: Coincident(g1,g2)
    c: Coincident(g2,g3)
    c: Coincident(g3,g4)
    c: Coincident(g4,g5)
    c: Coincident(g5,g6)
    c: Coincident(g6,g7)
    c: Coincident(g7,g8)
    c: Coincident(g8,g9)
    c: Coincident(g9,g10)
    c: Coincident(g10,g11)
    c: Coincident(g11,g12)
    c: Coincident(g12,g13)
    c: Coincident(g13,g14)
    c: Coincident(g14,g15)
    c: Coincident(g15,g16)
    c: Vertical(g16)
    c: Coincident(g16,g17)
    c: Coincident(g17,g18)
    c: Coincident(g18,g19)
    c: Coincident(g19,g20)
    c: Coincident(g20,g21)
    c: Coincident(g21,g22)
    c: Coincident(g22,g23)
    c: Coincident(g23,g24)
    c: Coincident(g24,g25)
    c: Coincident(g25,g26)
    c: PointOnObject(g28,g0)
    c: PointOnObject(g28,g26)
    c: Tangent(g0,g27) = 1.5708
    c: Tangent(g26,g27) = 1.5708
FEATURE [PartDesign::Pocket] Pocket118
  BaseFeature = -> Pad097
  Direction = (0,1,-2e-16)
  Length = 99.95
  Length2 = 5
  Placement = pos=(0,0,0) rot=(1,0,0;1.5708rad)
  Profile = -> Sketch217
  ReferenceAxis = -> Sketch217 [N_Axis]
  Refine = true
  Suppressed = false
  Type = 0
FEATURE [Sketcher::SketchObject] Sketch218
  ArcFitTolerance = 1e-06
  AttachmentSupport = -> [XY_Plane042]
  FullyConstrained = false
  MakeInternals = false
  MapMode = 5
  sketch-geometry (4):
    g0: LineSegment StartX=295 StartY=17.3691 StartZ=0 EndX=295 EndY=-107.641 EndZ=0
    g1: LineSegment StartX=295 StartY=-107.641 StartZ=0 EndX=389.553 EndY=-107.641 EndZ=0
    g2: LineSegment StartX=389.553 StartY=-107.641 StartZ=0 EndX=389.553 EndY=17.3691 EndZ=0
    g3: LineSegment StartX=389.553 StartY=17.3691 StartZ=0 EndX=295 EndY=17.3691 EndZ=0
  constraints (9):
    c: Coincident(g0,g1)
    c: Coincident(g1,g2)
    c: Coincident(g2,g3)
    c: Coincident(g3,g0)
    c: Vertical(g0)
    c: Vertical(g2)
    c: Horizontal(g1)
    c: Horizontal(g3)
    c: DistanceX(g-1,g0) = 295
FEATURE [PartDesign::Pocket] Pocket119
  BaseFeature = -> Pocket118
  Direction = (0,0,-1)
  Length = 5
  Length2 = 5
  Midplane = true
  Placement = pos=(0,0,0) rot=(1,0,0;1.5708rad)
  Profile = -> Sketch218
  ReferenceAxis = -> Sketch218 [N_Axis]
  Refine = true
  Suppressed = false
  Type = 0
FEATURE [Sketcher::SketchObject] Sketch220
  ArcFitTolerance = 1e-06
  AttachmentSupport = -> [XY_Plane042]
  FullyConstrained = true
  MakeInternals = false
  MapMode = 5
  sketch-geometry (12):
    g0: LineSegment StartX=-20 StartY=-7 StartZ=0 EndX=-20 EndY=-117 EndZ=0
    g1: LineSegment StartX=-20 StartY=-117 StartZ=0 EndX=35 EndY=-117 EndZ=0
    g2: LineSegment StartX=35 StartY=-117 StartZ=0 EndX=35 EndY=-7 EndZ=0
    g3: LineSegment StartX=35 StartY=-7 StartZ=0 EndX=-20 EndY=-7 EndZ=0
    g4: LineSegment StartX=40 StartY=-7 StartZ=0 EndX=40 EndY=-117 EndZ=0
    g5: LineSegment StartX=40 StartY=-117 StartZ=0 EndX=165 EndY=-117 EndZ=0
    g6: LineSegment StartX=165 StartY=-117 StartZ=0 EndX=165 EndY=-7 EndZ=0
    g7: LineSegment StartX=165 StartY=-7 StartZ=0 EndX=40 EndY=-7 EndZ=0
    g8: LineSegment StartX=170 StartY=-7 StartZ=0 EndX=170 EndY=-117 EndZ=0
    g9: LineSegment StartX=170 StartY=-117 StartZ=0 EndX=300 EndY=-117 EndZ=0
    g10: LineSegment StartX=300 StartY=-117 StartZ=0 EndX=300 EndY=-7 EndZ=0
    g11: LineSegment StartX=300 StartY=-7 StartZ=0 EndX=170 EndY=-7 EndZ=0
  constraints (36):
    c: Coincident(g0,g1)
    c: Coincident(g1,g2)
    c: Coincident(g2,g3)
    c: Coincident(g3,g0)
    c: Vertical(g0)
    c: Vertical(g2)
    c: Horizontal(g1)
    c: Horizontal(g3)
    c: Coincident(g4,g5)
    c: Coincident(g5,g6)
    c: Coincident(g6,g7)
    c: Coincident(g7,g4)
    c: Vertical(g4)
    c: Vertical(g6)
    c: Horizontal(g5)
    c: Horizontal(g7)
    c: Coincident(g8,g9)
    c: Coincident(g9,g10)
    c: Coincident(g10,g11)
    c: Coincident(g11,g8)
    c: Vertical(g8)
    c: Vertical(g10)
    c: Horizontal(g9)
    c: Horizontal(g11)
    c: DistanceY(g10,g-1) = 7
    c: DistanceY(g6,g-1) = 7
    c: DistanceY(g2,g-1) = 7
    c: DistanceX(g0,g-1) = 20
    c: DistanceY(g0,g0) = 110
    c: Distance(g4,g2) = 5
    c: Distance(g8,g6) = 5
    c: DistanceY(g4,g4) = 110
    c: DistanceY(g8,g8) = 110
    c: DistanceX(g-1,g9) = 300
    c: DistanceX(g-1,g1) = 35
    c: DistanceX(g-1,g5) = 165
FEATURE [PartDesign::Pocket] Pocket120
  BaseFeature = -> Pocket119
  Direction = (0,0,-1)
  Length = 100
  Length2 = 5
  Midplane = true
  Placement = pos=(0,0,0) rot=(1,0,0;1.5708rad)
  Profile = -> Sketch220
  ReferenceAxis = -> Sketch220 [N_Axis]
  Refine = true
  Suppressed = false
  Type = 0
FEATURE [Sketcher::SketchObject] Sketch219
  ArcFitTolerance = 1e-06
  AttachmentSupport = -> [Pocket120]
  FullyConstrained = false
  MakeInternals = false
  MapMode = 5
  Placement = pos=(0,-7,-2.3e-15) rot=(1,0,0;1.5708rad)
  sketch-geometry (42):
    g0: LineSegment StartX=45.884 StartY=17.7219 StartZ=0 EndX=33.93 EndY=-4.65497 EndZ=0
    g1: LineSegment StartX=49.8645 StartY=18.8062 StartZ=0 EndX=37.3312 EndY=-4.65497 EndZ=0
    g2: LineSegment StartX=45.884 StartY=17.7219 StartZ=0 EndX=49.8645 EndY=18.8062 EndZ=0
    g3: LineSegment StartX=33.93 StartY=-4.65497 StartZ=0 EndX=37.3312 EndY=-4.65497 EndZ=0
    g4: ArcOfCircle CenterX=18 CenterY=3 CenterZ=0 NormalX=0 NormalY=0 NormalZ=1 AngleXU=0 Radius=6.5 StartAngle=2.58175 EndAngle=4.38597
    g5: LineSegment StartX=20.6963 StartY=8.91437 StartZ=0 EndX=19.1912 EndY=11.3613 EndZ=0
    g6: LineSegment StartX=12.4923 StartY=6.45183 StartZ=0 EndX=11.7252 EndY=8.2111 EndZ=0
    g7: LineSegment StartX=11.7252 StartY=8.2111 StartZ=0 EndX=19.1912 EndY=11.3613 EndZ=0
    g8: LineSegment StartX=23.9272 StartY=0.331954 StartZ=0 EndX=26.093 EndY=-4.58272 EndZ=0
    g9: LineSegment StartX=15.9158 StartY=-3.15679 StartZ=0 EndX=16.6159 EndY=-4.58272 EndZ=0
    g10: LineSegment StartX=16.6159 StartY=-4.58272 StartZ=0 EndX=26.093 EndY=-4.58272 EndZ=0
    g11: LineSegment StartX=74.8373 StartY=20.9684 StartZ=0 EndX=89.2063 EndY=-4.24973 EndZ=0
    g12: LineSegment StartX=89.2063 StartY=-4.24973 StartZ=0 EndX=92.6591 EndY=-4.24973 EndZ=0
    g13: LineSegment StartX=92.6591 StartY=-4.24973 StartZ=0 EndX=78.184 EndY=21.1546 EndZ=0
    g14: LineSegment StartX=78.184 StartY=21.1546 StartZ=0 EndX=74.8373 EndY=20.9684 EndZ=0
    g15: LineSegment StartX=113.372 StartY=-3.61742 StartZ=0 EndX=125.992 EndY=20.9865 EndZ=0
    g16: LineSegment StartX=125.992 StartY=20.9865 StartZ=0 EndX=129.338 EndY=20.9348 EndZ=0
    g17: LineSegment StartX=129.338 StartY=20.9348 StartZ=0 EndX=116.743 EndY=-3.61742 EndZ=0
    g18: LineSegment StartX=116.743 StartY=-3.61742 StartZ=0 EndX=113.372 EndY=-3.61742 EndZ=0
    g19: LineSegment StartX=156.49 StartY=19.0126 StartZ=0 EndX=171.224 EndY=-2.18705 EndZ=0
    g20: LineSegment StartX=171.224 StartY=-2.18705 StartZ=0 EndX=175.064 EndY=-2.45586 EndZ=0
    g21: LineSegment StartX=175.064 StartY=-2.45586 StartZ=0 EndX=160.386 EndY=18.6636 EndZ=0
    g22: LineSegment StartX=160.386 StartY=18.6636 StartZ=0 EndX=156.49 EndY=19.0126 EndZ=0
    g23: LineSegment StartX=195.991 StartY=-1.14503 StartZ=0 EndX=209.19 EndY=12.3205 EndZ=0
    g24: LineSegment StartX=209.19 StartY=12.3205 StartZ=0 EndX=213.44 EndY=12.3702 EndZ=0
    g25: LineSegment StartX=213.44 StartY=12.3702 StartZ=0 EndX=200.192 EndY=-1.14503 EndZ=0
    g26: LineSegment StartX=200.192 StartY=-1.14503 StartZ=0 EndX=195.991 EndY=-1.14503 EndZ=0
    g27: LineSegment StartX=229.838 StartY=9.19446 StartZ=0 EndX=237.096 EndY=0 EndZ=0
    g28: LineSegment StartX=237.096 StartY=0 StartZ=0 EndX=240.918 EndY=0 EndZ=0
    g29: LineSegment StartX=240.918 StartY=0 StartZ=0 EndX=234.226 EndY=8.47688 EndZ=0
    g30: LineSegment StartX=234.226 StartY=8.47688 StartZ=0 EndX=229.838 EndY=9.19446 EndZ=0
    g31: ArcOfCircle CenterX=18 CenterY=3 CenterZ=0 NormalX=0 NormalY=0 NormalZ=1 AngleXU=0 Radius=6.5 StartAngle=5.86022 EndAngle=7.42624
    g32: Circle CenterX=18 CenterY=3 CenterZ=0 NormalX=0 NormalY=0 NormalZ=1 AngleXU=0 Radius=4.1
    g33: Circle CenterX=185 CenterY=7 CenterZ=0 NormalX=0 NormalY=0 NormalZ=1 AngleXU=0 Radius=4.1
    g34: ArcOfCircle CenterX=185 CenterY=7 CenterZ=0 NormalX=0 NormalY=0 NormalZ=1 AngleXU=0 Radius=6.5 StartAngle=1.96559 EndAngle=4.3176
    g35: LineSegment StartX=182.5 StartY=13 StartZ=0 EndX=182.5 EndY=15.9367 EndZ=0
    g36: LineSegment StartX=182.5 StartY=15.9367 StartZ=0 EndX=187.5 EndY=15.5349 EndZ=0
    g37: LineSegment StartX=187.5 StartY=15.5349 StartZ=0 EndX=187.5 EndY=13 EndZ=0
    g38: LineSegment StartX=182.5 StartY=1 StartZ=0 EndX=182.5 EndY=-1.79994 EndZ=0
    g39: LineSegment StartX=182.5 StartY=-1.79994 StartZ=0 EndX=187.5 EndY=-1.79994 EndZ=0
    g40: LineSegment StartX=187.5 StartY=-1.79994 StartZ=0 EndX=187.5 EndY=1 EndZ=0
    g41: ArcOfCircle CenterX=185 CenterY=7 CenterZ=0 NormalX=0 NormalY=0 NormalZ=1 AngleXU=0 Radius=6.5 StartAngle=5.10718 EndAngle=7.45919
  constraints (84):
    c: Coincident(g2,g0)
    c: Coincident(g2,g1)
    c: Coincident(g3,g0)
    c: Coincident(g3,g1)
    c: Horizontal(g3)
    c: Parallel(g0,g1)
    c: Distance(g1,g0) = 3
    c: Diameter(g4) = 13
    c: DistanceY(g-1,g4) = 3
    c: DistanceX(g-1,g4) = 18
    c: Coincident(g7,g6)
    c: Coincident(g7,g5)
    c: PointOnObject(g8,g31)
    c: Coincident(g10,g9)
    c: Horizontal(g10)
    c: Coincident(g10,g8)
    c: Coincident(g11,g12)
    c: Horizontal(g12)
    c: Coincident(g12,g13)
    c: Coincident(g13,g14)
    c: Coincident(g14,g11)
    c: Parallel(g11,g13)
    c: Distance(g13,g11) = 3
    c: Coincident(g15,g16)
    c: Coincident(g16,g17)
    c: Coincident(g17,g18)
    c: Coincident(g18,g15)
    c: Horizontal(g18)
    c: Parallel(g17,g15)
    c: Distance(g17,g15) = 3
    c: Coincident(g19,g20)
    c: Coincident(g20,g21)
    c: Coincident(g21,g22)
    c: Coincident(g22,g19)
    c: Parallel(g19,g21)
    c: Distance(g21,g19) = 3
    c: Coincident(g23,g24)
    c: Coincident(g24,g25)
    c: Coincident(g25,g26)
    c: Horizontal(g26)
    c: Parallel(g23,g25)
    c: Distance(g25,g23) = 3
    c: PointOnObject(g27,g-1)
    c: Coincident(g27,g28)
    c: PointOnObject(g28,g-1)
    c: Coincident(g28,g29)
    c: Coincident(g29,g30)
    c: Coincident(g30,g27)
    c: Parallel(g27,g29)
    c: Distance(g29,g27) = 3
    c: Coincident(g31,g5)
    c: Coincident(g4,g6)
    c: Equal(g4,g31)
    c: Coincident(g4,g9)
    c: PointOnObject(g31,g8)
    c: Coincident(g4,g31)
    c: Coincident(g26,g23)
    c: Diameter(g32) = 8.2
    c: Coincident(g32,g4)
    c: Diameter(g33) = 8.2
    c: DistanceY(g-1,g33) = 7
    c: DistanceX(g-1,g33) = 185
    c: Diameter(g34) = 13
    c: Coincident(g34,g33)
    c: Coincident(g35,g36)
    c: Coincident(g36,g37)
    c: Vertical(g37)
    c: Vertical(g38)
    c: Coincident(g38,g39)
    c: Horizontal(g39)
    c: Coincident(g39,g40)
    c: PointOnObject(g40,g41)
    c: Vertical(g40)
    c: Vertical(g35)
    c: Distance(g37,g35) = 5
    c: DistanceX(g35,g33) = 2.5
    c: Distance(g38,g40) = 5
    c: DistanceX(g38,g33) = 2.5
    c: Coincident(g41,g37)
    c: Coincident(g34,g35)
    c: Equal(g34,g41)
    c: Coincident(g34,g38)
    c: PointOnObject(g41,g40)
    c: Coincident(g34,g41)
FEATURE [PartDesign::Pad] Pad098
  BaseFeature = -> Pocket120
  Direction = (0,-1,2e-16)
  Length = 7
  Length2 = 10
  Placement = pos=(0,0,0) rot=(1,0,0;1.5708rad)
  Profile = -> Sketch219
  ReferenceAxis = -> Sketch219 [N_Axis]
  Refine = true
  Reversed = true
  Suppressed = false
  Type = 0
FEATURE [Sketcher::SketchObject] Sketch221
  ArcFitTolerance = 1e-06
  AttachmentSupport = -> [Pad098]
  FullyConstrained = false
  MakeInternals = false
  MapMode = 5
  Placement = pos=(35,0,0) rot=(0.707107,0,-0.707107;3.14159rad)
  sketch-geometry (25):
    g0: LineSegment [constr] StartX=-33.5639 StartY=50 StartZ=0 EndX=22.3562 EndY=50 EndZ=0
    g1: LineSegment StartX=-17.0984 StartY=50 StartZ=0 EndX=-16.0002 EndY=50 EndZ=0
    g2: LineSegment StartX=-16.0002 StartY=50 StartZ=0 EndX=5.93914 EndY=8.47552 EndZ=0
    g3: LineSegment StartX=5.93914 StartY=8.47552 StartZ=0 EndX=5.96134 EndY=7.0893 EndZ=0
    g4: LineSegment StartX=5.96134 StartY=7.0893 StartZ=0 EndX=4.40956 EndY=7.0893 EndZ=0
    g5: LineSegment StartX=4.40956 StartY=7.0893 StartZ=0 EndX=-17.1228 EndY=47.8435 EndZ=0
    g6: LineSegment StartX=-17.1228 StartY=47.8435 StartZ=0 EndX=-17.0984 EndY=50 EndZ=0
    g7: LineSegment StartX=-17.1293 StartY=7.10705 StartZ=0 EndX=-17.1293 EndY=9.14543 EndZ=0
    g8: LineSegment StartX=-17.1293 StartY=9.14543 StartZ=0 EndX=4.55828 EndY=50 EndZ=0
    g9: LineSegment StartX=4.55828 StartY=50 StartZ=0 EndX=5.87403 EndY=50.0018 EndZ=0
    g10: LineSegment StartX=5.87403 StartY=50.0018 StartZ=0 EndX=5.93974 EndY=48.3369 EndZ=0
    g11: LineSegment StartX=5.93974 StartY=48.3369 StartZ=0 EndX=-15.9471 EndY=7.10705 EndZ=0
    g12: LineSegment StartX=-15.9471 StartY=7.10705 StartZ=0 EndX=-17.1293 EndY=7.10705 EndZ=0
    g13: LineSegment StartX=-17.1358 StartY=50 StartZ=0 EndX=-15.9776 EndY=50.0877 EndZ=0
    g14: LineSegment StartX=-15.9776 StartY=50.0877 StartZ=0 EndX=5.97119 EndY=97.9201 EndZ=0
    g15: LineSegment StartX=5.97119 StartY=97.9201 StartZ=0 EndX=5.97119 EndY=99.8598 EndZ=0
    g16: LineSegment StartX=5.97119 StartY=99.8598 StartZ=0 EndX=4.66077 EndY=99.8598 EndZ=0
    g17: LineSegment StartX=4.66077 StartY=99.8598 StartZ=0 EndX=-17.1358 EndY=52.3592 EndZ=0
    g18: LineSegment StartX=-17.1358 StartY=52.3592 StartZ=0 EndX=-17.1358 EndY=50 EndZ=0
    g19: LineSegment StartX=-15.9576 StartY=99.8854 StartZ=0 EndX=-17.034 EndY=99.8854 EndZ=0
    g20: LineSegment StartX=-17.034 StartY=99.8854 StartZ=0 EndX=-17.0782 EndY=97.5311 EndZ=0
    g21: LineSegment StartX=-17.0782 StartY=97.5311 StartZ=0 EndX=4.71765 EndY=50 EndZ=0
    g22: LineSegment StartX=4.71765 StartY=50 StartZ=0 EndX=5.8275 EndY=50.1579 EndZ=0
    g23: LineSegment StartX=5.8275 StartY=50.1579 StartZ=0 EndX=5.8275 EndY=52.3779 EndZ=0
    g24: LineSegment StartX=5.8275 StartY=52.3779 StartZ=0 EndX=-15.9576 EndY=99.8854 EndZ=0
  constraints (47):
    c: Horizontal(g0)
    c: DistanceY(g-1,g0) = 50
    c: PointOnObject(g1,g0)
    c: Horizontal(g1)
    c: Coincident(g1,g2)
    c: Coincident(g2,g3)
    c: Coincident(g3,g4)
    c: Horizontal(g4)
    c: Coincident(g4,g5)
    c: Coincident(g5,g6)
    c: Vertical(g7)
    c: Coincident(g7,g8)
    c: PointOnObject(g8,g0)
    c: Coincident(g8,g9)
    c: Coincident(g9,g10)
    c: Coincident(g10,g11)
    c: Coincident(g11,g12)
    c: Coincident(g12,g7)
    c: Horizontal(g12)
    c: Parallel(g5,g2)
    c: Parallel(g8,g11)
    c: Distance(g2,g5) = 2
    c: Distance(g8,g11) = 2
    c: Coincident(g6,g1)
    c: PointOnObject(g13,g0)
    c: Coincident(g13,g14)
    c: Coincident(g14,g15)
    c: Vertical(g15)
    c: Coincident(g15,g16)
    c: Horizontal(g16)
    c: Coincident(g16,g17)
    c: Coincident(g17,g18)
    c: Coincident(g18,g13)
    c: Parallel(g17,g14)
    c: Vertical(g18)
    c: Distance(g14,g17) = 2
    c: Horizontal(g19)
    c: Coincident(g19,g20)
    c: Coincident(g20,g21)
    c: PointOnObject(g21,g0)
    c: Coincident(g21,g22)
    c: Coincident(g22,g23)
    c: Vertical(g23)
    c: Coincident(g23,g24)
    c: Coincident(g24,g19)
    c: Parallel(g24,g21)
    c: Distance(g21,g24) = 2
FEATURE [PartDesign::Pad] Pad099
  BaseFeature = -> Pad098
  Direction = (-1,0,-2e-16)
  Length = 5
  Length2 = 10
  Placement = pos=(0,0,0) rot=(1,0,0;1.5708rad)
  Profile = -> Sketch221
  ReferenceAxis = -> Sketch221 [N_Axis]
  Refine = true
  Reversed = true
  Suppressed = false
  Type = 0
FEATURE [Sketcher::SketchObject] Sketch222
  ArcFitTolerance = 1e-06
  AttachmentSupport = -> [Pad099]
  FullyConstrained = false
  MakeInternals = false
  MapMode = 5
  Placement = pos=(170,0,0) rot=(0.707107,0,0.707107;3.14159rad)
  sketch-geometry (25):
    g0: LineSegment [constr] StartX=-9.20711 StartY=50 StartZ=0 EndX=31.5955 EndY=50 EndZ=0
    g1: LineSegment StartX=-3.23071 StartY=7.09197 StartZ=0 EndX=-2.05702 EndY=7.09197 EndZ=0
    g2: LineSegment StartX=-2.05702 StartY=7.09197 StartZ=0 EndX=18.4375 EndY=47.7755 EndZ=0
    g3: LineSegment StartX=18.4375 StartY=47.7755 StartZ=0 EndX=18.4375 EndY=50 EndZ=0
    g4: LineSegment StartX=18.4375 StartY=50 StartZ=0 EndX=17.3084 EndY=49.9795 EndZ=0
    g5: LineSegment StartX=17.3084 StartY=49.9795 StartZ=0 EndX=-3.23071 EndY=9.20758 EndZ=0
    g6: LineSegment StartX=-3.23071 StartY=9.20758 StartZ=0 EndX=-3.23071 EndY=7.09197 EndZ=0
    g7: LineSegment StartX=17.1226 StartY=7.07983 StartZ=0 EndX=18.4953 EndY=7.07983 EndZ=0
    g8: LineSegment StartX=18.4953 StartY=7.07983 StartZ=0 EndX=18.4953 EndY=8.80663 EndZ=0
    g9: LineSegment StartX=18.4953 StartY=8.80663 StartZ=0 EndX=-2.09857 EndY=50 EndZ=0
    g10: LineSegment StartX=-2.09857 StartY=50 StartZ=0 EndX=-3.17562 EndY=49.9159 EndZ=0
    g11: LineSegment StartX=-3.17562 StartY=49.9159 StartZ=0 EndX=-3.17562 EndY=47.6818 EndZ=0
    g12: LineSegment StartX=-3.17562 StartY=47.6818 StartZ=0 EndX=17.1226 EndY=7.07983 EndZ=0
    g13: LineSegment StartX=-3.19345 StartY=99.8693 StartZ=0 EndX=-2.03057 EndY=99.8693 EndZ=0
    g14: LineSegment StartX=-2.03057 StartY=99.8693 StartZ=0 EndX=18.4277 EndY=53.15 EndZ=0
    g15: LineSegment StartX=18.4277 StartY=53.15 StartZ=0 EndX=18.5025 EndY=50 EndZ=0
    g16: LineSegment StartX=18.5025 StartY=50 StartZ=0 EndX=17.5757 EndY=50.1098 EndZ=0
    g17: LineSegment StartX=17.5757 StartY=50.1098 StartZ=0 EndX=-3.19345 EndY=97.5389 EndZ=0
    g18: LineSegment StartX=-3.19345 StartY=97.5389 StartZ=0 EndX=-3.19345 EndY=99.8693 EndZ=0
    g19: LineSegment StartX=-3.22366 StartY=50 StartZ=0 EndX=-3.22366 EndY=52.3177 EndZ=0
    g20: LineSegment StartX=-3.22366 StartY=52.3177 StartZ=0 EndX=17.471 EndY=99.8606 EndZ=0
    g21: LineSegment StartX=17.471 StartY=99.8606 StartZ=0 EndX=18.4521 EndY=99.8606 EndZ=0
    g22: LineSegment StartX=18.4521 StartY=99.8606 StartZ=0 EndX=18.4521 EndY=97.1035 EndZ=0
    g23: LineSegment StartX=18.4521 StartY=97.1035 StartZ=0 EndX=-2.05909 EndY=49.982 EndZ=0
    g24: LineSegment StartX=-2.05909 StartY=49.982 StartZ=0 EndX=-3.22366 EndY=50 EndZ=0
  constraints (49):
    c: Horizontal(g0)
    c: DistanceY(g-1,g0) = 50
    c: Horizontal(g1)
    c: Coincident(g1,g2)
    c: Coincident(g2,g3)
    c: PointOnObject(g3,g0)
    c: Vertical(g3)
    c: Coincident(g3,g4)
    c: Coincident(g4,g5)
    c: Coincident(g5,g6)
    c: Coincident(g6,g1)
    c: Horizontal(g7)
    c: Coincident(g7,g8)
    c: Vertical(g8)
    c: Coincident(g8,g9)
    c: PointOnObject(g9,g0)
    c: Coincident(g9,g10)
    c: Coincident(g10,g11)
    c: Vertical(g11)
    c: Coincident(g11,g12)
    c: Coincident(g12,g7)
    c: Parallel(g9,g12)
    c: Parallel(g5,g2)
    c: Distance(g2,g5) = 2
    c: Distance(g12,g9) = 2
    c: Vertical(g6)
    c: Horizontal(g13)
    c: Coincident(g13,g14)
    c: Coincident(g14,g15)
    c: PointOnObject(g15,g0)
    c: Coincident(g15,g16)
    c: Coincident(g16,g17)
    c: Coincident(g17,g18)
    c: Coincident(g18,g13)
    c: Vertical(g18)
    c: PointOnObject(g19,g0)
    c: Vertical(g19)
    c: Coincident(g19,g20)
    c: Coincident(g20,g21)
    c: Horizontal(g21)
    c: Coincident(g21,g22)
    c: Vertical(g22)
    c: Coincident(g22,g23)
    c: Coincident(g23,g24)
    c: Coincident(g24,g19)
    c: Parallel(g17,g14)
    c: Parallel(g23,g20)
    c: Distance(g23,g20) = 2
    c: Distance(g14,g17) = 2
FEATURE [PartDesign::Pad] Pad100
  BaseFeature = -> Pad099
  Direction = (1,0,-2e-16)
  Length = 5
  Length2 = 10
  Placement = pos=(0,0,0) rot=(1,0,0;1.5708rad)
  Profile = -> Sketch222
  ReferenceAxis = -> Sketch222 [N_Axis]
  Refine = true
  Reversed = true
  Suppressed = false
  Type = 0
FEATURE [Sketcher::SketchObject] Sketch223
  ArcFitTolerance = 1e-06
  AttachmentSupport = -> [XY_Plane042]
  FullyConstrained = false
  MakeInternals = false
  MapMode = 5
  sketch-geometry (4):
    g0: LineSegment StartX=192 StartY=42.6691 StartZ=0 EndX=192 EndY=-48.1885 EndZ=0
    g1: LineSegment StartX=192 StartY=-48.1885 StartZ=0 EndX=335.25 EndY=-48.1885 EndZ=0
    g2: LineSegment StartX=335.25 StartY=-48.1885 StartZ=0 EndX=335.25 EndY=42.6691 EndZ=0
    g3: LineSegment StartX=335.25 StartY=42.6691 StartZ=0 EndX=192 EndY=42.6691 EndZ=0
  constraints (9):
    c: Coincident(g0,g1)
    c: Coincident(g1,g2)
    c: Coincident(g2,g3)
    c: Coincident(g3,g0)
    c: Vertical(g0)
    c: Vertical(g2)
    c: Horizontal(g1)
    c: Horizontal(g3)
    c: DistanceX(g-1,g0) = 192
FEATURE [PartDesign::Pocket] Pocket121
  BaseFeature = -> Pad100
  Direction = (0,0,-1)
  Length = 100
  Length2 = 5
  Midplane = true
  Placement = pos=(0,0,0) rot=(1,0,0;1.5708rad)
  Profile = -> Sketch223
  ReferenceAxis = -> Sketch223 [N_Axis]
  Refine = true
  Suppressed = false
  Type = 0
FEATURE [PartDesign::Body] Body042  label="wingspar 010"
  AllowCompound = false
  Group = -> [Sketch216,Pad097,Sketch217,Pocket118,Sketch218,Pocket119,Pocket120,Sketch219,Pad098,Sketch220,Sketch221,Pad099,Sketch222,Pad100,Sketch223,Pocket121]
  Origin = -> Origin042
  Placement = pos=(0,-800,0) rot=(0,0,1;0rad)
  Tip = -> Pocket121
FEATURE [Sketcher::SketchObject] Sketch224
  ArcFitTolerance = 1e-06
  FullyConstrained = false
  MakeInternals = false
  Placement = pos=(0,0,0) rot=(1,0,0;1.5708rad)
  sketch-geometry (125):
    g0: BSplineCurve PolesCount=62 KnotsCount=62 Degree=3 IsPeriodic=1
    g1-g62: Circle [constr] x62 (B-spline internal-alignment scaffolding for g0; pole/knot coordinates omitted)
    g63-g124: GeomPoint [constr] x62 (B-spline internal-alignment scaffolding for g0; pole/knot coordinates omitted)
  constraints (125):
    c: InternalAlignment(g1,g0)
    c: Weight(g1) = 1
    c: InternalAlignment(g2,g0)
    c: Equal(g2,g1)
    c: InternalAlignment(g3,g0)
    c: Equal(g3,g1)
    c: InternalAlignment(g4,g0)
    c: Equal(g4,g1)
    c: InternalAlignment(g5,g0)
    c: Equal(g5,g1)
    c: InternalAlignment(g6,g0)
    c: Equal(g6,g1)
    c: InternalAlignment(g7,g0)
    c: Equal(g7,g1)
    c: InternalAlignment(g8,g0)
    c: Equal(g8,g1)
    c: InternalAlignment(g9,g0)
    c: Equal(g9,g1)
    c: InternalAlignment(g10,g0)
    c: Equal(g10,g1)
    c: InternalAlignment(g11,g0)
    c: Equal(g11,g1)
    c: InternalAlignment(g12,g0)
    c: Equal(g12,g1)
    c: InternalAlignment(g13,g0)
    c: Equal(g13,g1)
    c: InternalAlignment(g14,g0)
    c: Equal(g14,g1)
    c: InternalAlignment(g15,g0)
    c: Equal(g15,g1)
    c: InternalAlignment(g16,g0)
    c: Equal(g16,g1)
    c: InternalAlignment(g17,g0)
    c: Equal(g17,g1)
    c: InternalAlignment(g18,g0)
    c: Equal(g18,g1)
    c: InternalAlignment(g19,g0)
    c: Equal(g19,g1)
    c: InternalAlignment(g20,g0)
    c: Equal(g20,g1)
    c: InternalAlignment(g21,g0)
    c: Equal(g21,g1)
    c: InternalAlignment(g22,g0)
    c: Equal(g22,g1)
    c: InternalAlignment(g23,g0)
    c: Equal(g23,g1)
    c: InternalAlignment(g24,g0)
    c: Equal(g24,g1)
    c: InternalAlignment(g25,g0)
    c: Equal(g25,g1)
    c: InternalAlignment(g26,g0)
    c: Equal(g26,g1)
    c: InternalAlignment(g27,g0)
    c: Equal(g27,g1)
    c: InternalAlignment(g28,g0)
    c: Equal(g28,g1)
    c: InternalAlignment(g29,g0)
    c: Equal(g29,g1)
    c: InternalAlignment(g30,g0)
    c: Equal(g30,g1)
    c: InternalAlignment(g31,g0)
    c: Equal(g31,g1)
    c: InternalAlignment(g32,g0)
    c: Equal(g32,g1)
    c: InternalAlignment(g33,g0)
    c: Equal(g33,g1)
    c: InternalAlignment(g34,g0)
    c: Equal(g34,g1)
    c: InternalAlignment(g35,g0)
    c: Equal(g35,g1)
    c: InternalAlignment(g36,g0)
    c: Equal(g36,g1)
    c: InternalAlignment(g37,g0)
    c: Equal(g37,g1)
    c: InternalAlignment(g38,g0)
    c: Equal(g38,g1)
    c: InternalAlignment(g39,g0)
    c: Equal(g39,g1)
    c: InternalAlignment(g40,g0)
    c: Equal(g40,g1)
    c: InternalAlignment(g41,g0)
    c: Equal(g41,g1)
    c: InternalAlignment(g42,g0)
    c: Equal(g42,g1)
    c: InternalAlignment(g43,g0)
    c: Equal(g43,g1)
    c: InternalAlignment(g44,g0)
    c: Equal(g44,g1)
    c: InternalAlignment(g45,g0)
    c: Equal(g45,g1)
    c: InternalAlignment(g46,g0)
    c: Equal(g46,g1)
    c: InternalAlignment(g47,g0)
    c: Equal(g47,g1)
    c: InternalAlignment(g48,g0)
    c: Equal(g48,g1)
    c: InternalAlignment(g49,g0)
    c: Equal(g49,g1)
    c: InternalAlignment(g50,g0)
    c: Equal(g50,g1)
    c: InternalAlignment(g51,g0)
    c: Equal(g51,g1)
    c: InternalAlignment(g52,g0)
    c: Equal(g52,g1)
    c: InternalAlignment(g53,g0)
    c: Equal(g53,g1)
    c: InternalAlignment(g54,g0)
    c: Equal(g54,g1)
    c: InternalAlignment(g55,g0)
    c: Equal(g55,g1)
    c: InternalAlignment(g56,g0)
    c: Equal(g56,g1)
    c: InternalAlignment(g57,g0)
    c: Equal(g57,g1)
    c: InternalAlignment(g58,g0)
    c: Equal(g58,g1)
    c: InternalAlignment(g59,g0)
    c: Equal(g59,g1)
    c: InternalAlignment(g60,g0)
    c: Equal(g60,g1)
    c: InternalAlignment(g61,g0)
    c: Equal(g61,g1)
    c: InternalAlignment(g62,g0)
    c: Equal(g62,g1)
    c: InternalAlignment(g63-g124 -> g0) x62
FEATURE [PartDesign::Pad] Pad101
  Direction = (0,-1,2e-16)
  Length = 49.95
  Length2 = 10
  Placement = pos=(0,0,0) rot=(1,0,0;1.5708rad)
  Profile = -> Sketch224
  ReferenceAxis = -> Sketch224 [N_Axis]
  Refine = true
  Suppressed = false
  Type = 0
FEATURE [Sketcher::SketchObject] Sketch225
  ArcFitTolerance = 1e-06
  AttachmentSupport = -> [Pad101]
  FullyConstrained = false
  MakeInternals = false
  MapMode = 5
  Placement = pos=(0,-49.95,1.1e-14) rot=(1,0,0;1.5708rad)
  sketch-geometry (29):
    g0: LineSegment StartX=2.71326 StartY=0.775372 StartZ=0 EndX=3.3867 EndY=1.52303 EndZ=0
    g1: LineSegment StartX=3.3867 StartY=1.52303 StartZ=0 EndX=5.99321 EndY=4.17962 EndZ=0
    g2: LineSegment StartX=5.99321 StartY=4.17962 StartZ=0 EndX=11.2308 EndY=7.18071 EndZ=0
    g3: LineSegment StartX=11.2308 StartY=7.18071 StartZ=0 EndX=18.9287 EndY=10.4927 EndZ=0
    g4: LineSegment StartX=18.9287 StartY=10.4927 StartZ=0 EndX=30.0156 EndY=13.8045 EndZ=0
    g5: LineSegment StartX=30.0156 StartY=13.8045 StartZ=0 EndX=43.7053 EndY=16.6585 EndZ=0
    g6: LineSegment StartX=43.7053 StartY=16.6585 StartZ=0 EndX=58.3753 EndY=18.5837 EndZ=0
    g7: LineSegment StartX=58.3753 StartY=18.5837 StartZ=0 EndX=81.9328 EndY=20.1998 EndZ=0
    g8: LineSegment StartX=81.9328 StartY=20.1998 StartZ=0 EndX=99.116 EndY=20.5815 EndZ=0
    g9: LineSegment StartX=99.116 StartY=20.5815 StartZ=0 EndX=120.506 EndY=20.1998 EndZ=0
    g10: LineSegment StartX=120.506 StartY=20.1998 StartZ=0 EndX=145.772 EndY=18.6559 EndZ=0
    g11: LineSegment StartX=145.772 StartY=18.6559 StartZ=0 EndX=175.748 EndY=15.7728 EndZ=0
    g12: LineSegment StartX=175.748 StartY=15.7728 StartZ=0 EndX=200.436 EndY=12.5699 EndZ=0
    g13: LineSegment StartX=200.436 StartY=12.5699 StartZ=0 EndX=229.384 EndY=8.60252 EndZ=0
    g14: LineSegment StartX=229.384 StartY=8.60252 StartZ=0 EndX=252.135 EndY=5.21302 EndZ=0
    g15: LineSegment StartX=252.135 StartY=5.21302 StartZ=0 EndX=269.07 EndY=2.67143 EndZ=0
    g16: LineSegment StartX=269.07 StartY=2.67143 StartZ=0 EndX=269.07 EndY=1.39956 EndZ=0
    g17: LineSegment StartX=269.07 StartY=1.39956 StartZ=0 EndX=224.761 EndY=0.436598 EndZ=0
    g18: LineSegment StartX=224.761 StartY=0.436598 StartZ=0 EndX=175.487 EndY=-1.02731 EndZ=0
    g19: LineSegment StartX=175.487 StartY=-1.02731 StartZ=0 EndX=123.478 EndY=-2.41293 EndZ=0
    g20: LineSegment StartX=123.478 StartY=-2.41293 StartZ=0 EndX=62.0775 EndY=-3.87655 EndZ=0
    g21: LineSegment StartX=62.0775 StartY=-3.87655 StartZ=0 EndX=32.0529 EndY=-3.76091 EndZ=0
    g22: LineSegment StartX=32.0529 StartY=-3.76091 StartZ=0 EndX=18.888 EndY=-3.18288 EndZ=0
    g23: LineSegment StartX=18.888 StartY=-3.18288 StartZ=0 EndX=12.7286 EndY=-2.48971 EndZ=0
    g24: LineSegment StartX=12.7286 StartY=-2.48971 StartZ=0 EndX=8.49342 EndY=-1.8722 EndZ=0
    g25: LineSegment StartX=8.49342 StartY=-1.8722 StartZ=0 EndX=4.56236 EndY=-0.768246 EndZ=0
    g26: LineSegment StartX=4.56236 StartY=-0.768246 StartZ=0 EndX=3.01395 EndY=-0.301296 EndZ=0
    g27: ArcOfCircle CenterX=3.20505 CenterY=0.332397 CenterZ=0 NormalX=0 NormalY=0 NormalZ=1 AngleXU=0 Radius=0.661881 StartAngle=2.40837 EndAngle=4.41949
    g28: GeomPoint [constr] X=2.01486 Y=0 Z=0
  constraints (32):
    c: PointOnObject(g28,g-1)
    c: Coincident(g0,g1)
    c: Coincident(g1,g2)
    c: Coincident(g2,g3)
    c: Coincident(g3,g4)
    c: Coincident(g4,g5)
    c: Coincident(g5,g6)
    c: Coincident(g6,g7)
    c: Coincident(g7,g8)
    c: Coincident(g8,g9)
    c: Coincident(g9,g10)
    c: Coincident(g10,g11)
    c: Coincident(g11,g12)
    c: Coincident(g12,g13)
    c: Coincident(g13,g14)
    c: Coincident(g14,g15)
    c: Coincident(g15,g16)
    c: Vertical(g16)
    c: Coincident(g16,g17)
    c: Coincident(g17,g18)
    c: Coincident(g18,g19)
    c: Coincident(g19,g20)
    c: Coincident(g20,g21)
    c: Coincident(g21,g22)
    c: Coincident(g22,g23)
    c: Coincident(g23,g24)
    c: Coincident(g24,g25)
    c: Coincident(g25,g26)
    c: PointOnObject(g28,g0)
    c: PointOnObject(g28,g26)
    c: Tangent(g0,g27) = 1.5708
    c: Tangent(g26,g27) = 1.5708
FEATURE [PartDesign::Pocket] Pocket122
  BaseFeature = -> Pad101
  Direction = (0,1,-2e-16)
  Length = 49.95
  Length2 = 5
  Placement = pos=(0,0,0) rot=(1,0,0;1.5708rad)
  Profile = -> Sketch225
  ReferenceAxis = -> Sketch225 [N_Axis]
  Refine = true
  Suppressed = false
  Type = 0
FEATURE [Sketcher::SketchObject] Sketch226
  ArcFitTolerance = 1e-06
  AttachmentSupport = -> [XY_Plane043]
  FullyConstrained = false
  MakeInternals = false
  MapMode = 5
  sketch-geometry (4):
    g0: LineSegment StartX=295 StartY=17.3691 StartZ=0 EndX=295 EndY=-79.0747 EndZ=0
    g1: LineSegment StartX=295 StartY=-79.0747 StartZ=0 EndX=384.545 EndY=-79.0747 EndZ=0
    g2: LineSegment StartX=384.545 StartY=-79.0747 StartZ=0 EndX=384.545 EndY=17.3691 EndZ=0
    g3: LineSegment StartX=384.545 StartY=17.3691 StartZ=0 EndX=295 EndY=17.3691 EndZ=0
  constraints (9):
    c: Coincident(g0,g1)
    c: Coincident(g1,g2)
    c: Coincident(g2,g3)
    c: Coincident(g3,g0)
    c: Vertical(g0)
    c: Vertical(g2)
    c: Horizontal(g1)
    c: Horizontal(g3)
    c: DistanceX(g-1,g0) = 295
FEATURE [PartDesign::Pocket] Pocket123
  BaseFeature = -> Pocket122
  Direction = (0,0,-1)
  Length = 5
  Length2 = 5
  Midplane = true
  Placement = pos=(0,0,0) rot=(1,0,0;1.5708rad)
  Profile = -> Sketch226
  ReferenceAxis = -> Sketch226 [N_Axis]
  Refine = true
  Suppressed = false
  Type = 0
FEATURE [Sketcher::SketchObject] Sketch228
  ArcFitTolerance = 1e-06
  AttachmentSupport = -> [XY_Plane043]
  FullyConstrained = true
  MakeInternals = false
  MapMode = 5
  sketch-geometry (12):
    g0: LineSegment StartX=-10 StartY=-7 StartZ=0 EndX=-10 EndY=-67 EndZ=0
    g1: LineSegment StartX=-10 StartY=-67 StartZ=0 EndX=35 EndY=-67 EndZ=0
    g2: LineSegment StartX=35 StartY=-67 StartZ=0 EndX=35 EndY=-7 EndZ=0
    g3: LineSegment StartX=35 StartY=-7 StartZ=0 EndX=-10 EndY=-7 EndZ=0
    g4: LineSegment StartX=40 StartY=-67 StartZ=0 EndX=165 EndY=-67 EndZ=0
    g5: LineSegment StartX=165 StartY=-67 StartZ=0 EndX=165 EndY=-7 EndZ=0
    g6: LineSegment StartX=165 StartY=-7 StartZ=0 EndX=40 EndY=-7 EndZ=0
    g7: LineSegment StartX=40 StartY=-7 StartZ=0 EndX=40 EndY=-67 EndZ=0
    g8: LineSegment StartX=170 StartY=-67 StartZ=0 EndX=300 EndY=-67 EndZ=0
    g9: LineSegment StartX=300 StartY=-67 StartZ=0 EndX=300 EndY=-7 EndZ=0
    g10: LineSegment StartX=300 StartY=-7 StartZ=0 EndX=170 EndY=-7 EndZ=0
    g11: LineSegment StartX=170 StartY=-7 StartZ=0 EndX=170 EndY=-67 EndZ=0
  constraints (36):
    c: Coincident(g0,g1)
    c: Coincident(g1,g2)
    c: Coincident(g2,g3)
    c: Coincident(g3,g0)
    c: Vertical(g0)
    c: Vertical(g2)
    c: Horizontal(g1)
    c: Horizontal(g3)
    c: Coincident(g4,g5)
    c: Coincident(g5,g6)
    c: Coincident(g6,g7)
    c: Coincident(g7,g4)
    c: Horizontal(g4)
    c: Horizontal(g6)
    c: Vertical(g5)
    c: Vertical(g7)
    c: Coincident(g8,g9)
    c: Coincident(g9,g10)
    c: Coincident(g10,g11)
    c: Coincident(g11,g8)
    c: Horizontal(g8)
    c: Horizontal(g10)
    c: Vertical(g9)
    c: Vertical(g11)
    c: DistanceY(g9,g-1) = 7
    c: DistanceY(g5,g-1) = 7
    c: DistanceY(g2,g-1) = 7
    c: Distance(g2,g7) = 5
    c: DistanceX(g0,g-1) = 10
    c: DistanceX(g-1,g9) = 300
    c: DistanceX(g-1,g1) = 35
    c: DistanceX(g-1,g4) = 165
    c: Distance(g5,g11) = 5
    c: DistanceY(g0,g0) = 60
    c: DistanceY(g7,g7) = 60
    c: DistanceY(g11,g11) = 60
FEATURE [PartDesign::Pocket] Pocket124
  BaseFeature = -> Pocket123
  Direction = (0,0,-1)
  Length = 100
  Length2 = 5
  Midplane = true
  Placement = pos=(0,0,0) rot=(1,0,0;1.5708rad)
  Profile = -> Sketch228
  ReferenceAxis = -> Sketch228 [N_Axis]
  Refine = true
  Suppressed = false
  Type = 0
FEATURE [Sketcher::SketchObject] Sketch227
  ArcFitTolerance = 1e-06
  AttachmentSupport = -> [Pocket124]
  FullyConstrained = false
  MakeInternals = false
  MapMode = 5
  Placement = pos=(0,-7,-2.3e-15) rot=(1,0,0;1.5708rad)
  sketch-geometry (60):
    g0: LineSegment StartX=45.884 StartY=17.7219 StartZ=0 EndX=33.93 EndY=-4.65497 EndZ=0
    g1: LineSegment StartX=49.8645 StartY=18.8062 StartZ=0 EndX=37.3312 EndY=-4.65497 EndZ=0
    g2: LineSegment StartX=45.884 StartY=17.7219 StartZ=0 EndX=49.8645 EndY=18.8062 EndZ=0
    g3: LineSegment StartX=33.93 StartY=-4.65497 StartZ=0 EndX=37.3312 EndY=-4.65497 EndZ=0
    g4: ArcOfCircle CenterX=18 CenterY=3 CenterZ=0 NormalX=0 NormalY=0 NormalZ=1 AngleXU=0 Radius=6.5 StartAngle=2.58175 EndAngle=4.38597
    g5: LineSegment StartX=20.6963 StartY=8.91437 StartZ=0 EndX=19.1912 EndY=11.3613 EndZ=0
    g6: LineSegment StartX=12.4923 StartY=6.45183 StartZ=0 EndX=11.7252 EndY=8.2111 EndZ=0
    g7: LineSegment StartX=11.7252 StartY=8.2111 StartZ=0 EndX=19.1912 EndY=11.3613 EndZ=0
    g8: LineSegment StartX=23.9272 StartY=0.331954 StartZ=0 EndX=26.093 EndY=-4.58272 EndZ=0
    g9: LineSegment StartX=15.9158 StartY=-3.15679 StartZ=0 EndX=16.6159 EndY=-4.58272 EndZ=0
    g10: LineSegment StartX=16.6159 StartY=-4.58272 StartZ=0 EndX=26.093 EndY=-4.58272 EndZ=0
    g11: LineSegment StartX=74.8373 StartY=20.9684 StartZ=0 EndX=89.2063 EndY=-4.24973 EndZ=0
    g12: LineSegment StartX=89.2063 StartY=-4.24973 StartZ=0 EndX=92.6591 EndY=-4.24973 EndZ=0
    g13: LineSegment StartX=92.6591 StartY=-4.24973 StartZ=0 EndX=78.184 EndY=21.1546 EndZ=0
    g14: LineSegment StartX=78.184 StartY=21.1546 StartZ=0 EndX=74.8373 EndY=20.9684 EndZ=0
    g15: LineSegment StartX=113.372 StartY=-3.61742 StartZ=0 EndX=125.992 EndY=20.9865 EndZ=0
    g16: LineSegment StartX=125.992 StartY=20.9865 StartZ=0 EndX=129.338 EndY=20.9348 EndZ=0
    g17: LineSegment StartX=129.338 StartY=20.9348 StartZ=0 EndX=116.743 EndY=-3.61742 EndZ=0
    g18: LineSegment StartX=116.743 StartY=-3.61742 StartZ=0 EndX=113.372 EndY=-3.61742 EndZ=0
    g19: LineSegment StartX=156.49 StartY=19.0126 StartZ=0 EndX=171.224 EndY=-2.18705 EndZ=0
    g20: LineSegment StartX=171.224 StartY=-2.18705 StartZ=0 EndX=175.064 EndY=-2.45586 EndZ=0
    g21: LineSegment StartX=175.064 StartY=-2.45586 StartZ=0 EndX=160.386 EndY=18.6636 EndZ=0
    g22: LineSegment StartX=160.386 StartY=18.6636 StartZ=0 EndX=156.49 EndY=19.0126 EndZ=0
    g23: LineSegment StartX=195.991 StartY=-1.14503 StartZ=0 EndX=209.19 EndY=12.3205 EndZ=0
    g24: LineSegment StartX=209.19 StartY=12.3205 StartZ=0 EndX=213.44 EndY=12.3702 EndZ=0
    g25: LineSegment StartX=213.44 StartY=12.3702 StartZ=0 EndX=200.192 EndY=-1.14503 EndZ=0
    g26: LineSegment StartX=200.192 StartY=-1.14503 StartZ=0 EndX=195.991 EndY=-1.14503 EndZ=0
    g27: LineSegment StartX=229.838 StartY=9.19446 StartZ=0 EndX=237.096 EndY=0 EndZ=0
    g28: LineSegment StartX=237.096 StartY=0 StartZ=0 EndX=240.918 EndY=0 EndZ=0
    g29: LineSegment StartX=240.918 StartY=0 StartZ=0 EndX=234.226 EndY=8.47688 EndZ=0
    g30: LineSegment StartX=234.226 StartY=8.47688 StartZ=0 EndX=229.838 EndY=9.19446 EndZ=0
    g31: ArcOfCircle CenterX=18 CenterY=3 CenterZ=0 NormalX=0 NormalY=0 NormalZ=1 AngleXU=0 Radius=6.5 StartAngle=5.86022 EndAngle=7.42624
    g32: Circle CenterX=18 CenterY=3 CenterZ=0 NormalX=0 NormalY=0 NormalZ=1 AngleXU=0 Radius=4.1
    g33: Circle CenterX=60 CenterY=8 CenterZ=0 NormalX=0 NormalY=0 NormalZ=1 AngleXU=0 Radius=4.1
    g34: Circle CenterX=150 CenterY=8 CenterZ=0 NormalX=0 NormalY=0 NormalZ=1 AngleXU=0 Radius=4.1
    g35: ArcOfCircle CenterX=60 CenterY=8 CenterZ=0 NormalX=0 NormalY=0 NormalZ=1 AngleXU=0 Radius=6.5 StartAngle=1.96559 EndAngle=4.3176
    g36: Circle CenterX=185 CenterY=7 CenterZ=0 NormalX=0 NormalY=0 NormalZ=1 AngleXU=0 Radius=4.1
    g37: LineSegment StartX=57.5 StartY=14 StartZ=0 EndX=57.5 EndY=19.5561 EndZ=0
    g38: LineSegment StartX=62.5 StartY=14 StartZ=0 EndX=62.5 EndY=20.0342 EndZ=0
    g39: LineSegment StartX=62.5 StartY=20.0342 StartZ=0 EndX=57.5 EndY=19.5561 EndZ=0
    g40: LineSegment StartX=57.5 StartY=2 StartZ=0 EndX=57.5 EndY=-4.90591 EndZ=0
    g41: LineSegment StartX=57.5 StartY=-4.90591 StartZ=0 EndX=62.5 EndY=-4.90591 EndZ=0
    g42: LineSegment StartX=62.5 StartY=-4.90591 StartZ=0 EndX=62.5 EndY=2 EndZ=0
    g43: ArcOfCircle CenterX=60 CenterY=8 CenterZ=0 NormalX=0 NormalY=0 NormalZ=1 AngleXU=0 Radius=6.5 StartAngle=5.10718 EndAngle=7.45919
    g44: ArcOfCircle CenterX=150 CenterY=8 CenterZ=0 NormalX=0 NormalY=0 NormalZ=1 AngleXU=0 Radius=6.5 StartAngle=1.96559 EndAngle=4.3176
    g45: ArcOfCircle CenterX=185 CenterY=7 CenterZ=0 NormalX=0 NormalY=0 NormalZ=1 AngleXU=0 Radius=6.5 StartAngle=1.96559 EndAngle=4.3176
    g46: LineSegment StartX=147.5 StartY=14 StartZ=0 EndX=147.5 EndY=19.2414 EndZ=0
    g47: LineSegment StartX=147.5 StartY=19.2414 StartZ=0 EndX=152.5 EndY=18.961 EndZ=0
    g48: LineSegment StartX=152.5 StartY=18.961 StartZ=0 EndX=152.5 EndY=14 EndZ=0
    g49: LineSegment StartX=147.5 StartY=2 StartZ=0 EndX=147.5 EndY=-2.5624 EndZ=0
    g50: LineSegment StartX=147.5 StartY=-2.5624 StartZ=0 EndX=152.5 EndY=-2.5624 EndZ=0
    g51: LineSegment StartX=152.5 StartY=-2.5624 StartZ=0 EndX=152.5 EndY=2 EndZ=0
    g52: ArcOfCircle CenterX=150 CenterY=8 CenterZ=0 NormalX=0 NormalY=0 NormalZ=1 AngleXU=0 Radius=6.5 StartAngle=5.10718 EndAngle=7.45919
    g53: LineSegment StartX=182.5 StartY=13 StartZ=0 EndX=182.5 EndY=15.9367 EndZ=0
    g54: LineSegment StartX=182.5 StartY=15.9367 StartZ=0 EndX=187.5 EndY=15.5349 EndZ=0
    g55: LineSegment StartX=187.5 StartY=15.5349 StartZ=0 EndX=187.5 EndY=13 EndZ=0
    g56: LineSegment StartX=182.5 StartY=1 StartZ=0 EndX=182.5 EndY=-1.79994 EndZ=0
    g57: LineSegment StartX=182.5 StartY=-1.79994 StartZ=0 EndX=187.5 EndY=-1.79994 EndZ=0
    g58: LineSegment StartX=187.5 StartY=-1.79994 StartZ=0 EndX=187.5 EndY=1 EndZ=0
    g59: ArcOfCircle CenterX=185 CenterY=7 CenterZ=0 NormalX=0 NormalY=0 NormalZ=1 AngleXU=0 Radius=6.5 StartAngle=5.10718 EndAngle=7.45919
  constraints (134):
    c: Coincident(g2,g0)
    c: Coincident(g2,g1)
    c: Coincident(g3,g0)
    c: Coincident(g3,g1)
    c: Horizontal(g3)
    c: Parallel(g0,g1)
    c: Distance(g1,g0) = 3
    c: Diameter(g4) = 13
    c: DistanceY(g-1,g4) = 3
    c: DistanceX(g-1,g4) = 18
    c: Coincident(g7,g6)
    c: Coincident(g7,g5)
    c: PointOnObject(g8,g31)
    c: Coincident(g10,g9)
    c: Horizontal(g10)
    c: Coincident(g10,g8)
    c: Coincident(g11,g12)
    c: Horizontal(g12)
    c: Coincident(g12,g13)
    c: Coincident(g13,g14)
    c: Coincident(g14,g11)
    c: Parallel(g11,g13)
    c: Distance(g13,g11) = 3
    c: Coincident(g15,g16)
    c: Coincident(g16,g17)
    c: Coincident(g17,g18)
    c: Coincident(g18,g15)
    c: Horizontal(g18)
    c: Parallel(g17,g15)
    c: Distance(g17,g15) = 3
    c: Coincident(g19,g20)
    c: Coincident(g20,g21)
    c: Coincident(g21,g22)
    c: Coincident(g22,g19)
    c: Parallel(g19,g21)
    c: Distance(g21,g19) = 3
    c: Coincident(g23,g24)
    c: Coincident(g24,g25)
    c: Coincident(g25,g26)
    c: Horizontal(g26)
    c: Parallel(g23,g25)
    c: Distance(g25,g23) = 3
    c: PointOnObject(g27,g-1)
    c: Coincident(g27,g28)
    c: PointOnObject(g28,g-1)
    c: Coincident(g28,g29)
    c: Coincident(g29,g30)
    c: Coincident(g30,g27)
    c: Parallel(g27,g29)
    c: Distance(g29,g27) = 3
    c: Coincident(g31,g5)
    c: Coincident(g4,g6)
    c: Equal(g4,g31)
    c: Coincident(g4,g9)
    c: PointOnObject(g31,g8)
    c: Coincident(g4,g31)
    c: Coincident(g26,g23)
    c: Diameter(g32) = 8.2
    c: Coincident(g32,g4)
    c: Diameter(g33) = 8.2
    c: Diameter(g34) = 8.2
    c: DistanceX(g33,g34) = 90
    c: Coincident(g35,g33)
    c: Diameter(g35) = 13
    c: DistanceX(g-1,g33) = 60
    c: DistanceY(g-1,g33) = 8
    c: DistanceY(g-1,g34) = 8
    c: Diameter(g36) = 8.2
    c: DistanceY(g-1,g36) = 7
    c: DistanceX(g-1,g36) = 185
    c: Vertical(g37)
    c: Vertical(g38)
    c: Coincident(g39,g38)
    c: Coincident(g39,g37)
    c: Distance(g38,g37) = 5
    c: DistanceX(g37,g33) = 2.5
    c: Coincident(g40,g41)
    c: Horizontal(g41)
    c: Coincident(g41,g42)
    c: PointOnObject(g42,g43)
    c: Vertical(g40)
    c: Vertical(g42)
    c: DistanceX(g40,g33) = 2.5
    c: DistanceX(g41,g41) = 5
    c: Coincident(g43,g38)
    c: Coincident(g35,g37)
    c: Equal(g35,g43)
    c: Coincident(g35,g40)
    c: PointOnObject(g43,g42)
    c: Coincident(g35,g43)
    c: Diameter(g44) = 13
    c: Coincident(g44,g34)
    c: Diameter(g45) = 13
    c: Coincident(g45,g36)
    c: Vertical(g46)
    c: Coincident(g46,g47)
    c: Coincident(g47,g48)
    c: Vertical(g48)
    c: Vertical(g49)
    c: Coincident(g49,g50)
    c: Horizontal(g50)
    c: Coincident(g50,g51)
    c: PointOnObject(g51,g52)
    c: Vertical(g51)
    c: DistanceX(g50,g50) = 5
    c: DistanceX(g49,g34) = 2.5
    c: Distance(g48,g46) = 5
    c: DistanceX(g46,g34) = 2.5
    c: Coincident(g52,g48)
    c: Coincident(g44,g46)
    c: Equal(g44,g52)
    c: Coincident(g44,g49)
    c: PointOnObject(g52,g51)
    c: Coincident(g44,g52)
    c: Coincident(g53,g54)
    c: Coincident(g54,g55)
    c: Vertical(g55)
    c: Vertical(g56)
    c: Coincident(g56,g57)
    c: Horizontal(g57)
    c: Coincident(g57,g58)
    c: PointOnObject(g58,g59)
    c: Vertical(g58)
    c: Vertical(g53)
    c: Distance(g55,g53) = 5
    c: DistanceX(g53,g36) = 2.5
    c: Distance(g56,g58) = 5
    c: DistanceX(g56,g36) = 2.5
    c: Coincident(g59,g55)
    c: Coincident(g45,g53)
    c: Equal(g45,g59)
    c: Coincident(g45,g56)
    c: PointOnObject(g59,g58)
    c: Coincident(g45,g59)
FEATURE [PartDesign::Pad] Pad102
  BaseFeature = -> Pocket124
  Direction = (0,-1,2e-16)
  Length = 7
  Length2 = 10
  Placement = pos=(0,0,0) rot=(1,0,0;1.5708rad)
  Profile = -> Sketch227
  ReferenceAxis = -> Sketch227 [N_Axis]
  Refine = true
  Reversed = true
  Suppressed = false
  Type = 0
FEATURE [Sketcher::SketchObject] Sketch229
  ArcFitTolerance = 1e-06
  AttachmentSupport = -> [Pad102]
  FullyConstrained = false
  MakeInternals = false
  MapMode = 5
  Placement = pos=(170,0,0) rot=(0.707107,0,0.707107;3.14159rad)
  sketch-geometry (14):
    g0: LineSegment StartX=-2.86242 StartY=8.94149 StartZ=0 EndX=6.44299 EndY=28.05 EndZ=0
    g1: LineSegment StartX=16.796 StartY=49.3097 StartZ=0 EndX=17.6093 EndY=49.3097 EndZ=0
    g2: LineSegment StartX=17.6093 StartY=49.3097 StartZ=0 EndX=17.6093 EndY=46.4118 EndZ=0
    g3: LineSegment StartX=17.6093 StartY=46.4118 StartZ=0 EndX=8.66937 EndY=28.0538 EndZ=0
    g4: LineSegment StartX=-1.3402 StartY=7.49928 StartZ=0 EndX=-2.53265 EndY=7.49928 EndZ=0
    g5: LineSegment StartX=-2.53265 StartY=7.49928 StartZ=0 EndX=-2.86242 EndY=8.94149 EndZ=0
    g6: LineSegment StartX=-1.56722 StartY=48.7925 StartZ=0 EndX=7.5685 EndY=30.3349 EndZ=0
    g7: LineSegment StartX=18.4673 StartY=8.20781 StartZ=0 EndX=16.7969 EndY=7.18146 EndZ=0
    g8: LineSegment StartX=16.7969 StartY=7.18146 StartZ=0 EndX=7.58766 EndY=25.7876 EndZ=0
    g9: LineSegment StartX=-2.2596 StartY=45.768 StartZ=0 EndX=-1.56722 EndY=48.7925 EndZ=0
    g10: LineSegment StartX=8.66937 StartY=28.0538 StartZ=0 EndX=18.4673 EndY=8.20781 EndZ=0
    g11: LineSegment StartX=7.5685 StartY=30.3349 StartZ=0 EndX=16.796 EndY=49.3097 EndZ=0
    g12: LineSegment StartX=6.44299 StartY=28.05 StartZ=0 EndX=-2.2596 EndY=45.768 EndZ=0
    g13: LineSegment StartX=7.58766 StartY=25.7876 StartZ=0 EndX=-1.3402 EndY=7.49928 EndZ=0
  constraints (24):
    c: Coincident(g11,g1)
    c: Horizontal(g1)
    c: Coincident(g1,g2)
    c: Vertical(g2)
    c: Coincident(g2,g3)
    c: Coincident(g13,g4)
    c: Horizontal(g4)
    c: Coincident(g4,g5)
    c: Coincident(g5,g0)
    c: Parallel(g0,g3)
    c: Distance(g3,g0) = 2
    c: Coincident(g10,g7)
    c: Coincident(g7,g8)
    c: Parallel(g8,g6)
    c: Distance(g8,g6) = 2
    c: Coincident(g9,g12)
    c: Coincident(g9,g6)
    c: PointOnObject(g6,g11)
    c: PointOnObject(g0,g12)
    c: PointOnObject(g11,g6)
    c: PointOnObject(g8,g13)
    c: PointOnObject(g12,g0)
    c: Coincident(g3,g10)
    c: PointOnObject(g13,g8)
FEATURE [PartDesign::Pad] Pad103
  BaseFeature = -> Pad102
  Direction = (1,0,-2e-16)
  Length = 5
  Length2 = 10
  Placement = pos=(0,0,0) rot=(1,0,0;1.5708rad)
  Profile = -> Sketch229
  ReferenceAxis = -> Sketch229 [N_Axis]
  Refine = true
  Reversed = true
  Suppressed = false
  Type = 0
FEATURE [Sketcher::SketchObject] Sketch230
  ArcFitTolerance = 1e-06
  AttachmentSupport = -> [Pad103]
  FullyConstrained = false
  MakeInternals = false
  MapMode = 5
  Placement = pos=(35,0,0) rot=(0.707107,0,-0.707107;3.14159rad)
  sketch-geometry (12):
    g0: LineSegment StartX=-17.0415 StartY=48.3111 StartZ=0 EndX=-17.0415 EndY=49.7892 EndZ=0
    g1: LineSegment StartX=-17.0415 StartY=49.7892 StartZ=0 EndX=-15.5583 EndY=49.7892 EndZ=0
    g2: LineSegment StartX=-15.5583 StartY=49.7892 StartZ=0 EndX=5.93029 EndY=8.81738 EndZ=0
    g3: LineSegment StartX=5.93029 StartY=8.81738 StartZ=0 EndX=5.93029 EndY=7.1685 EndZ=0
    g4: LineSegment StartX=5.93029 StartY=7.1685 StartZ=0 EndX=4.5367 EndY=7.1685 EndZ=0
    g5: LineSegment StartX=4.5367 StartY=7.1685 StartZ=0 EndX=-17.0415 EndY=48.3111 EndZ=0
    g6: LineSegment StartX=-17.1124 StartY=7.28835 StartZ=0 EndX=-16.1126 EndY=7.28835 EndZ=0
    g7: LineSegment StartX=-16.1126 StartY=7.28835 StartZ=0 EndX=5.8579 EndY=48.0729 EndZ=0
    g8: LineSegment StartX=5.8579 StartY=48.0729 StartZ=0 EndX=5.97735 EndY=49.7725 EndZ=0
    g9: LineSegment StartX=5.97735 StartY=49.7725 StartZ=0 EndX=4.50171 EndY=49.7725 EndZ=0
    g10: LineSegment StartX=4.50171 StartY=49.7725 StartZ=0 EndX=-17.1124 EndY=9.64961 EndZ=0
    g11: LineSegment StartX=-17.1124 StartY=9.64961 StartZ=0 EndX=-17.1124 EndY=7.28835 EndZ=0
  constraints (23):
    c: Vertical(g0)
    c: Coincident(g0,g1)
    c: Horizontal(g1)
    c: Coincident(g1,g2)
    c: Coincident(g2,g3)
    c: Vertical(g3)
    c: Coincident(g3,g4)
    c: Horizontal(g4)
    c: Coincident(g4,g5)
    c: Coincident(g5,g0)
    c: Parallel(g2,g5)
    c: Distance(g5,g2) = 2
    c: Horizontal(g6)
    c: Coincident(g6,g7)
    c: Coincident(g7,g8)
    c: Coincident(g8,g9)
    c: Horizontal(g9)
    c: Coincident(g9,g10)
    c: Coincident(g10,g11)
    c: Coincident(g11,g6)
    c: Vertical(g11)
    c: Parallel(g10,g7)
    c: Distance(g7,g10) = 2
FEATURE [PartDesign::Pad] Pad104
  BaseFeature = -> Pad103
  Direction = (-1,0,-2e-16)
  Length = 5
  Length2 = 10
  Placement = pos=(0,0,0) rot=(1,0,0;1.5708rad)
  Profile = -> Sketch230
  ReferenceAxis = -> Sketch230 [N_Axis]
  Refine = true
  Reversed = true
  Suppressed = false
  Type = 0
FEATURE [PartDesign::Chamfer] Chamfer006
  Angle = 45
  Base = -> Pad104 [Edge189,Edge188]
  BaseFeature = -> Pad104
  ChamferType = 0
  FlipDirection = false
  Placement = pos=(0,0,0) rot=(1,0,0;1.5708rad)
  Refine = true
  Size = 1
  Size2 = 1
  SupportTransform = false
  Suppressed = false
  UseAllEdges = false
FEATURE [PartDesign::Body] Body043  label="wingspar 011"
  AllowCompound = false
  Group = -> [Sketch224,Pad101,Sketch225,Pocket122,Sketch226,Pocket123,Pocket124,Sketch227,Sketch228,Pad102,Sketch229,Pad103,Sketch230,Pad104,Chamfer006]
  Origin = -> Origin043
  Placement = pos=(0,-900,0) rot=(0,0,1;0rad)
  Tip = -> Chamfer006
FEATURE [Sketcher::SketchObject] Sketch231
  ArcFitTolerance = 1e-06
  FullyConstrained = false
  MakeInternals = false
  Placement = pos=(0,0,0) rot=(1,0,0;1.5708rad)
  sketch-geometry (125):
    g0: BSplineCurve PolesCount=62 KnotsCount=62 Degree=3 IsPeriodic=1
    g1-g62: Circle [constr] x62 (B-spline internal-alignment scaffolding for g0; pole/knot coordinates omitted)
    g63-g124: GeomPoint [constr] x62 (B-spline internal-alignment scaffolding for g0; pole/knot coordinates omitted)
  constraints (125):
    c: InternalAlignment(g1,g0)
    c: Weight(g1) = 1
    c: InternalAlignment(g2,g0)
    c: Equal(g2,g1)
    c: InternalAlignment(g3,g0)
    c: Equal(g3,g1)
    c: InternalAlignment(g4,g0)
    c: Equal(g4,g1)
    c: InternalAlignment(g5,g0)
    c: Equal(g5,g1)
    c: InternalAlignment(g6,g0)
    c: Equal(g6,g1)
    c: InternalAlignment(g7,g0)
    c: Equal(g7,g1)
    c: InternalAlignment(g8,g0)
    c: Equal(g8,g1)
    c: InternalAlignment(g9,g0)
    c: Equal(g9,g1)
    c: InternalAlignment(g10,g0)
    c: Equal(g10,g1)
    c: InternalAlignment(g11,g0)
    c: Equal(g11,g1)
    c: InternalAlignment(g12,g0)
    c: Equal(g12,g1)
    c: InternalAlignment(g13,g0)
    c: Equal(g13,g1)
    c: InternalAlignment(g14,g0)
    c: Equal(g14,g1)
    c: InternalAlignment(g15,g0)
    c: Equal(g15,g1)
    c: InternalAlignment(g16,g0)
    c: Equal(g16,g1)
    c: InternalAlignment(g17,g0)
    c: Equal(g17,g1)
    c: InternalAlignment(g18,g0)
    c: Equal(g18,g1)
    c: InternalAlignment(g19,g0)
    c: Equal(g19,g1)
    c: InternalAlignment(g20,g0)
    c: Equal(g20,g1)
    c: InternalAlignment(g21,g0)
    c: Equal(g21,g1)
    c: InternalAlignment(g22,g0)
    c: Equal(g22,g1)
    c: InternalAlignment(g23,g0)
    c: Equal(g23,g1)
    c: InternalAlignment(g24,g0)
    c: Equal(g24,g1)
    c: InternalAlignment(g25,g0)
    c: Equal(g25,g1)
    c: InternalAlignment(g26,g0)
    c: Equal(g26,g1)
    c: InternalAlignment(g27,g0)
    c: Equal(g27,g1)
    c: InternalAlignment(g28,g0)
    c: Equal(g28,g1)
    c: InternalAlignment(g29,g0)
    c: Equal(g29,g1)
    c: InternalAlignment(g30,g0)
    c: Equal(g30,g1)
    c: InternalAlignment(g31,g0)
    c: Equal(g31,g1)
    c: InternalAlignment(g32,g0)
    c: Equal(g32,g1)
    c: InternalAlignment(g33,g0)
    c: Equal(g33,g1)
    c: InternalAlignment(g34,g0)
    c: Equal(g34,g1)
    c: InternalAlignment(g35,g0)
    c: Equal(g35,g1)
    c: InternalAlignment(g36,g0)
    c: Equal(g36,g1)
    c: InternalAlignment(g37,g0)
    c: Equal(g37,g1)
    c: InternalAlignment(g38,g0)
    c: Equal(g38,g1)
    c: InternalAlignment(g39,g0)
    c: Equal(g39,g1)
    c: InternalAlignment(g40,g0)
    c: Equal(g40,g1)
    c: InternalAlignment(g41,g0)
    c: Equal(g41,g1)
    c: InternalAlignment(g42,g0)
    c: Equal(g42,g1)
    c: InternalAlignment(g43,g0)
    c: Equal(g43,g1)
    c: InternalAlignment(g44,g0)
    c: Equal(g44,g1)
    c: InternalAlignment(g45,g0)
    c: Equal(g45,g1)
    c: InternalAlignment(g46,g0)
    c: Equal(g46,g1)
    c: InternalAlignment(g47,g0)
    c: Equal(g47,g1)
    c: InternalAlignment(g48,g0)
    c: Equal(g48,g1)
    c: InternalAlignment(g49,g0)
    c: Equal(g49,g1)
    c: InternalAlignment(g50,g0)
    c: Equal(g50,g1)
    c: InternalAlignment(g51,g0)
    c: Equal(g51,g1)
    c: InternalAlignment(g52,g0)
    c: Equal(g52,g1)
    c: InternalAlignment(g53,g0)
    c: Equal(g53,g1)
    c: InternalAlignment(g54,g0)
    c: Equal(g54,g1)
    c: InternalAlignment(g55,g0)
    c: Equal(g55,g1)
    c: InternalAlignment(g56,g0)
    c: Equal(g56,g1)
    c: InternalAlignment(g57,g0)
    c: Equal(g57,g1)
    c: InternalAlignment(g58,g0)
    c: Equal(g58,g1)
    c: InternalAlignment(g59,g0)
    c: Equal(g59,g1)
    c: InternalAlignment(g60,g0)
    c: Equal(g60,g1)
    c: InternalAlignment(g61,g0)
    c: Equal(g61,g1)
    c: InternalAlignment(g62,g0)
    c: Equal(g62,g1)
    c: InternalAlignment(g63-g124 -> g0) x62
FEATURE [PartDesign::Pad] Pad105
  Direction = (0,-1,2e-16)
  Length = 99.95
  Length2 = 10
  Placement = pos=(0,0,0) rot=(1,0,0;1.5708rad)
  Profile = -> Sketch231
  ReferenceAxis = -> Sketch231 [N_Axis]
  Refine = true
  Suppressed = false
  Type = 0
FEATURE [Sketcher::SketchObject] Sketch232
  ArcFitTolerance = 1e-06
  AttachmentSupport = -> [Pad105]
  FullyConstrained = false
  MakeInternals = false
  MapMode = 5
  Placement = pos=(0,-99.95,2.2e-14) rot=(1,0,0;1.5708rad)
  sketch-geometry (29):
    g0: LineSegment StartX=2.71326 StartY=0.775372 StartZ=0 EndX=3.3867 EndY=1.52303 EndZ=0
    g1: LineSegment StartX=3.3867 StartY=1.52303 StartZ=0 EndX=5.99321 EndY=4.17962 EndZ=0
    g2: LineSegment StartX=5.99321 StartY=4.17962 StartZ=0 EndX=11.2308 EndY=7.18071 EndZ=0
    g3: LineSegment StartX=11.2308 StartY=7.18071 StartZ=0 EndX=18.9287 EndY=10.4927 EndZ=0
    g4: LineSegment StartX=18.9287 StartY=10.4927 StartZ=0 EndX=30.0156 EndY=13.8045 EndZ=0
    g5: LineSegment StartX=30.0156 StartY=13.8045 StartZ=0 EndX=43.7053 EndY=16.6585 EndZ=0
    g6: LineSegment StartX=43.7053 StartY=16.6585 StartZ=0 EndX=58.3753 EndY=18.5837 EndZ=0
    g7: LineSegment StartX=58.3753 StartY=18.5837 StartZ=0 EndX=81.9328 EndY=20.1998 EndZ=0
    g8: LineSegment StartX=81.9328 StartY=20.1998 StartZ=0 EndX=99.116 EndY=20.5815 EndZ=0
    g9: LineSegment StartX=99.116 StartY=20.5815 StartZ=0 EndX=120.506 EndY=20.1998 EndZ=0
    g10: LineSegment StartX=120.506 StartY=20.1998 StartZ=0 EndX=145.772 EndY=18.6559 EndZ=0
    g11: LineSegment StartX=145.772 StartY=18.6559 StartZ=0 EndX=175.748 EndY=15.7728 EndZ=0
    g12: LineSegment StartX=175.748 StartY=15.7728 StartZ=0 EndX=200.436 EndY=12.5699 EndZ=0
    g13: LineSegment StartX=200.436 StartY=12.5699 StartZ=0 EndX=229.384 EndY=8.60252 EndZ=0
    g14: LineSegment StartX=229.384 StartY=8.60252 StartZ=0 EndX=252.135 EndY=5.21302 EndZ=0
    g15: LineSegment StartX=252.135 StartY=5.21302 StartZ=0 EndX=269.07 EndY=2.67143 EndZ=0
    g16: LineSegment StartX=269.07 StartY=2.67143 StartZ=0 EndX=269.07 EndY=1.39956 EndZ=0
    g17: LineSegment StartX=269.07 StartY=1.39956 StartZ=0 EndX=224.761 EndY=0.436598 EndZ=0
    g18: LineSegment StartX=224.761 StartY=0.436598 StartZ=0 EndX=175.487 EndY=-1.02731 EndZ=0
    g19: LineSegment StartX=175.487 StartY=-1.02731 StartZ=0 EndX=123.478 EndY=-2.41293 EndZ=0
    g20: LineSegment StartX=123.478 StartY=-2.41293 StartZ=0 EndX=62.0775 EndY=-3.87655 EndZ=0
    g21: LineSegment StartX=62.0775 StartY=-3.87655 StartZ=0 EndX=32.0529 EndY=-3.76091 EndZ=0
    g22: LineSegment StartX=32.0529 StartY=-3.76091 StartZ=0 EndX=18.888 EndY=-3.18288 EndZ=0
    g23: LineSegment StartX=18.888 StartY=-3.18288 StartZ=0 EndX=12.7286 EndY=-2.48971 EndZ=0
    g24: LineSegment StartX=12.7286 StartY=-2.48971 StartZ=0 EndX=8.49342 EndY=-1.8722 EndZ=0
    g25: LineSegment StartX=8.49342 StartY=-1.8722 StartZ=0 EndX=4.56236 EndY=-0.768246 EndZ=0
    g26: LineSegment StartX=4.56236 StartY=-0.768246 StartZ=0 EndX=3.01395 EndY=-0.301296 EndZ=0
    g27: ArcOfCircle CenterX=3.20505 CenterY=0.332397 CenterZ=0 NormalX=0 NormalY=0 NormalZ=1 AngleXU=0 Radius=0.661881 StartAngle=2.40837 EndAngle=4.41949
    g28: GeomPoint [constr] X=2.01486 Y=0 Z=0
  constraints (32):
    c: PointOnObject(g28,g-1)
    c: Coincident(g0,g1)
    c: Coincident(g1,g2)
    c: Coincident(g2,g3)
    c: Coincident(g3,g4)
    c: Coincident(g4,g5)
    c: Coincident(g5,g6)
    c: Coincident(g6,g7)
    c: Coincident(g7,g8)
    c: Coincident(g8,g9)
    c: Coincident(g9,g10)
    c: Coincident(g10,g11)
    c: Coincident(g11,g12)
    c: Coincident(g12,g13)
    c: Coincident(g13,g14)
    c: Coincident(g14,g15)
    c: Coincident(g15,g16)
    c: Vertical(g16)
    c: Coincident(g16,g17)
    c: Coincident(g17,g18)
    c: Coincident(g18,g19)
    c: Coincident(g19,g20)
    c: Coincident(g20,g21)
    c: Coincident(g21,g22)
    c: Coincident(g22,g23)
    c: Coincident(g23,g24)
    c: Coincident(g24,g25)
    c: Coincident(g25,g26)
    c: PointOnObject(g28,g0)
    c: PointOnObject(g28,g26)
    c: Tangent(g0,g27) = 1.5708
    c: Tangent(g26,g27) = 1.5708
FEATURE [PartDesign::Pocket] Pocket125
  BaseFeature = -> Pad105
  Direction = (0,1,-2e-16)
  Length = 99.95
  Length2 = 5
  Placement = pos=(0,0,0) rot=(1,0,0;1.5708rad)
  Profile = -> Sketch232
  ReferenceAxis = -> Sketch232 [N_Axis]
  Refine = true
  Suppressed = false
  Type = 0
FEATURE [Sketcher::SketchObject] Sketch233
  ArcFitTolerance = 1e-06
  AttachmentSupport = -> [XY_Plane044]
  FullyConstrained = false
  MakeInternals = false
  MapMode = 5
  sketch-geometry (4):
    g0: LineSegment StartX=295 StartY=17.3691 StartZ=0 EndX=295 EndY=-107.641 EndZ=0
    g1: LineSegment StartX=295 StartY=-107.641 StartZ=0 EndX=389.553 EndY=-107.641 EndZ=0
    g2: LineSegment StartX=389.553 StartY=-107.641 StartZ=0 EndX=389.553 EndY=17.3691 EndZ=0
    g3: LineSegment StartX=389.553 StartY=17.3691 StartZ=0 EndX=295 EndY=17.3691 EndZ=0
  constraints (9):
    c: Coincident(g0,g1)
    c: Coincident(g1,g2)
    c: Coincident(g2,g3)
    c: Coincident(g3,g0)
    c: Vertical(g0)
    c: Vertical(g2)
    c: Horizontal(g1)
    c: Horizontal(g3)
    c: DistanceX(g-1,g0) = 295
FEATURE [PartDesign::Pocket] Pocket126
  BaseFeature = -> Pocket125
  Direction = (0,0,-1)
  Length = 5
  Length2 = 5
  Midplane = true
  Placement = pos=(0,0,0) rot=(1,0,0;1.5708rad)
  Profile = -> Sketch233
  ReferenceAxis = -> Sketch233 [N_Axis]
  Refine = true
  Suppressed = false
  Type = 0
FEATURE [Sketcher::SketchObject] Sketch235
  ArcFitTolerance = 1e-06
  AttachmentSupport = -> [XY_Plane044]
  FullyConstrained = true
  MakeInternals = false
  MapMode = 5
  sketch-geometry (12):
    g0: LineSegment StartX=-20 StartY=-7 StartZ=0 EndX=-20 EndY=-117 EndZ=0
    g1: LineSegment StartX=-20 StartY=-117 StartZ=0 EndX=35 EndY=-117 EndZ=0
    g2: LineSegment StartX=35 StartY=-117 StartZ=0 EndX=35 EndY=-7 EndZ=0
    g3: LineSegment StartX=35 StartY=-7 StartZ=0 EndX=-20 EndY=-7 EndZ=0
    g4: LineSegment StartX=40 StartY=-7 StartZ=0 EndX=40 EndY=-117 EndZ=0
    g5: LineSegment StartX=40 StartY=-117 StartZ=0 EndX=165 EndY=-117 EndZ=0
    g6: LineSegment StartX=165 StartY=-117 StartZ=0 EndX=165 EndY=-7 EndZ=0
    g7: LineSegment StartX=165 StartY=-7 StartZ=0 EndX=40 EndY=-7 EndZ=0
    g8: LineSegment StartX=170 StartY=-7 StartZ=0 EndX=170 EndY=-117 EndZ=0
    g9: LineSegment StartX=170 StartY=-117 StartZ=0 EndX=300 EndY=-117 EndZ=0
    g10: LineSegment StartX=300 StartY=-117 StartZ=0 EndX=300 EndY=-7 EndZ=0
    g11: LineSegment StartX=300 StartY=-7 StartZ=0 EndX=170 EndY=-7 EndZ=0
  constraints (36):
    c: Coincident(g0,g1)
    c: Coincident(g1,g2)
    c: Coincident(g2,g3)
    c: Coincident(g3,g0)
    c: Vertical(g0)
    c: Vertical(g2)
    c: Horizontal(g1)
    c: Horizontal(g3)
    c: Coincident(g4,g5)
    c: Coincident(g5,g6)
    c: Coincident(g6,g7)
    c: Coincident(g7,g4)
    c: Vertical(g4)
    c: Vertical(g6)
    c: Horizontal(g5)
    c: Horizontal(g7)
    c: Coincident(g8,g9)
    c: Coincident(g9,g10)
    c: Coincident(g10,g11)
    c: Coincident(g11,g8)
    c: Vertical(g8)
    c: Vertical(g10)
    c: Horizontal(g9)
    c: Horizontal(g11)
    c: DistanceY(g10,g-1) = 7
    c: DistanceY(g6,g-1) = 7
    c: DistanceY(g2,g-1) = 7
    c: DistanceX(g0,g-1) = 20
    c: DistanceY(g0,g0) = 110
    c: Distance(g4,g2) = 5
    c: Distance(g8,g6) = 5
    c: DistanceY(g4,g4) = 110
    c: DistanceY(g8,g8) = 110
    c: DistanceX(g-1,g9) = 300
    c: DistanceX(g-1,g1) = 35
    c: DistanceX(g-1,g5) = 165
FEATURE [PartDesign::Pocket] Pocket127
  BaseFeature = -> Pocket126
  Direction = (0,0,-1)
  Length = 100
  Length2 = 5
  Midplane = true
  Placement = pos=(0,0,0) rot=(1,0,0;1.5708rad)
  Profile = -> Sketch235
  ReferenceAxis = -> Sketch235 [N_Axis]
  Refine = true
  Suppressed = false
  Type = 0
FEATURE [Sketcher::SketchObject] Sketch234
  ArcFitTolerance = 1e-06
  AttachmentSupport = -> [Pocket127]
  FullyConstrained = false
  MakeInternals = false
  MapMode = 5
  Placement = pos=(0,-7,-2.3e-15) rot=(1,0,0;1.5708rad)
  sketch-geometry (42):
    g0: LineSegment StartX=45.884 StartY=17.7219 StartZ=0 EndX=33.93 EndY=-4.65497 EndZ=0
    g1: LineSegment StartX=49.8645 StartY=18.8062 StartZ=0 EndX=37.3312 EndY=-4.65497 EndZ=0
    g2: LineSegment StartX=45.884 StartY=17.7219 StartZ=0 EndX=49.8645 EndY=18.8062 EndZ=0
    g3: LineSegment StartX=33.93 StartY=-4.65497 StartZ=0 EndX=37.3312 EndY=-4.65497 EndZ=0
    g4: ArcOfCircle CenterX=18 CenterY=3 CenterZ=0 NormalX=0 NormalY=0 NormalZ=1 AngleXU=0 Radius=6.5 StartAngle=2.58175 EndAngle=4.38597
    g5: LineSegment StartX=20.6963 StartY=8.91437 StartZ=0 EndX=19.1912 EndY=11.3613 EndZ=0
    g6: LineSegment StartX=12.4923 StartY=6.45183 StartZ=0 EndX=11.7252 EndY=8.2111 EndZ=0
    g7: LineSegment StartX=11.7252 StartY=8.2111 StartZ=0 EndX=19.1912 EndY=11.3613 EndZ=0
    g8: LineSegment StartX=23.9272 StartY=0.331954 StartZ=0 EndX=26.093 EndY=-4.58272 EndZ=0
    g9: LineSegment StartX=15.9158 StartY=-3.15679 StartZ=0 EndX=16.6159 EndY=-4.58272 EndZ=0
    g10: LineSegment StartX=16.6159 StartY=-4.58272 StartZ=0 EndX=26.093 EndY=-4.58272 EndZ=0
    g11: LineSegment StartX=74.8373 StartY=20.9684 StartZ=0 EndX=89.2063 EndY=-4.24973 EndZ=0
    g12: LineSegment StartX=89.2063 StartY=-4.24973 StartZ=0 EndX=92.6591 EndY=-4.24973 EndZ=0
    g13: LineSegment StartX=92.6591 StartY=-4.24973 StartZ=0 EndX=78.184 EndY=21.1546 EndZ=0
    g14: LineSegment StartX=78.184 StartY=21.1546 StartZ=0 EndX=74.8373 EndY=20.9684 EndZ=0
    g15: LineSegment StartX=113.372 StartY=-3.61742 StartZ=0 EndX=125.992 EndY=20.9865 EndZ=0
    g16: LineSegment StartX=125.992 StartY=20.9865 StartZ=0 EndX=129.338 EndY=20.9348 EndZ=0
    g17: LineSegment StartX=129.338 StartY=20.9348 StartZ=0 EndX=116.743 EndY=-3.61742 EndZ=0
    g18: LineSegment StartX=116.743 StartY=-3.61742 StartZ=0 EndX=113.372 EndY=-3.61742 EndZ=0
    g19: LineSegment StartX=156.49 StartY=19.0126 StartZ=0 EndX=171.224 EndY=-2.18705 EndZ=0
    g20: LineSegment StartX=171.224 StartY=-2.18705 StartZ=0 EndX=175.064 EndY=-2.45586 EndZ=0
    g21: LineSegment StartX=175.064 StartY=-2.45586 StartZ=0 EndX=160.386 EndY=18.6636 EndZ=0
    g22: LineSegment StartX=160.386 StartY=18.6636 StartZ=0 EndX=156.49 EndY=19.0126 EndZ=0
    g23: LineSegment StartX=195.991 StartY=-1.14503 StartZ=0 EndX=209.19 EndY=12.3205 EndZ=0
    g24: LineSegment StartX=209.19 StartY=12.3205 StartZ=0 EndX=213.44 EndY=12.3702 EndZ=0
    g25: LineSegment StartX=213.44 StartY=12.3702 StartZ=0 EndX=200.192 EndY=-1.14503 EndZ=0
    g26: LineSegment StartX=200.192 StartY=-1.14503 StartZ=0 EndX=195.991 EndY=-1.14503 EndZ=0
    g27: LineSegment StartX=229.838 StartY=9.19446 StartZ=0 EndX=237.096 EndY=0 EndZ=0
    g28: LineSegment StartX=237.096 StartY=0 StartZ=0 EndX=240.918 EndY=0 EndZ=0
    g29: LineSegment StartX=240.918 StartY=0 StartZ=0 EndX=234.226 EndY=8.47688 EndZ=0
    g30: LineSegment StartX=234.226 StartY=8.47688 StartZ=0 EndX=229.838 EndY=9.19446 EndZ=0
    g31: ArcOfCircle CenterX=18 CenterY=3 CenterZ=0 NormalX=0 NormalY=0 NormalZ=1 AngleXU=0 Radius=6.5 StartAngle=5.86022 EndAngle=7.42624
    g32: Circle CenterX=18 CenterY=3 CenterZ=0 NormalX=0 NormalY=0 NormalZ=1 AngleXU=0 Radius=4.1
    g33: Circle CenterX=185 CenterY=7 CenterZ=0 NormalX=0 NormalY=0 NormalZ=1 AngleXU=0 Radius=4.1
    g34: ArcOfCircle CenterX=185 CenterY=7 CenterZ=0 NormalX=0 NormalY=0 NormalZ=1 AngleXU=0 Radius=6.5 StartAngle=1.96559 EndAngle=4.3176
    g35: LineSegment StartX=182.5 StartY=13 StartZ=0 EndX=182.5 EndY=15.9367 EndZ=0
    g36: LineSegment StartX=182.5 StartY=15.9367 StartZ=0 EndX=187.5 EndY=15.5349 EndZ=0
    g37: LineSegment StartX=187.5 StartY=15.5349 StartZ=0 EndX=187.5 EndY=13 EndZ=0
    g38: LineSegment StartX=182.5 StartY=1 StartZ=0 EndX=182.5 EndY=-1.79994 EndZ=0
    g39: LineSegment StartX=182.5 StartY=-1.79994 StartZ=0 EndX=187.5 EndY=-1.79994 EndZ=0
    g40: LineSegment StartX=187.5 StartY=-1.79994 StartZ=0 EndX=187.5 EndY=1 EndZ=0
    g41: ArcOfCircle CenterX=185 CenterY=7 CenterZ=0 NormalX=0 NormalY=0 NormalZ=1 AngleXU=0 Radius=6.5 StartAngle=5.10718 EndAngle=7.45919
  constraints (84):
    c: Coincident(g2,g0)
    c: Coincident(g2,g1)
    c: Coincident(g3,g0)
    c: Coincident(g3,g1)
    c: Horizontal(g3)
    c: Parallel(g0,g1)
    c: Distance(g1,g0) = 3
    c: Diameter(g4) = 13
    c: DistanceY(g-1,g4) = 3
    c: DistanceX(g-1,g4) = 18
    c: Coincident(g7,g6)
    c: Coincident(g7,g5)
    c: PointOnObject(g8,g31)
    c: Coincident(g10,g9)
    c: Horizontal(g10)
    c: Coincident(g10,g8)
    c: Coincident(g11,g12)
    c: Horizontal(g12)
    c: Coincident(g12,g13)
    c: Coincident(g13,g14)
    c: Coincident(g14,g11)
    c: Parallel(g11,g13)
    c: Distance(g13,g11) = 3
    c: Coincident(g15,g16)
    c: Coincident(g16,g17)
    c: Coincident(g17,g18)
    c: Coincident(g18,g15)
    c: Horizontal(g18)
    c: Parallel(g17,g15)
    c: Distance(g17,g15) = 3
    c: Coincident(g19,g20)
    c: Coincident(g20,g21)
    c: Coincident(g21,g22)
    c: Coincident(g22,g19)
    c: Parallel(g19,g21)
    c: Distance(g21,g19) = 3
    c: Coincident(g23,g24)
    c: Coincident(g24,g25)
    c: Coincident(g25,g26)
    c: Horizontal(g26)
    c: Parallel(g23,g25)
    c: Distance(g25,g23) = 3
    c: PointOnObject(g27,g-1)
    c: Coincident(g27,g28)
    c: PointOnObject(g28,g-1)
    c: Coincident(g28,g29)
    c: Coincident(g29,g30)
    c: Coincident(g30,g27)
    c: Parallel(g27,g29)
    c: Distance(g29,g27) = 3
    c: Coincident(g31,g5)
    c: Coincident(g4,g6)
    c: Equal(g4,g31)
    c: Coincident(g4,g9)
    c: PointOnObject(g31,g8)
    c: Coincident(g4,g31)
    c: Coincident(g26,g23)
    c: Diameter(g32) = 8.2
    c: Coincident(g32,g4)
    c: Diameter(g33) = 8.2
    c: DistanceY(g-1,g33) = 7
    c: DistanceX(g-1,g33) = 185
    c: Diameter(g34) = 13
    c: Coincident(g34,g33)
    c: Coincident(g35,g36)
    c: Coincident(g36,g37)
    c: Vertical(g37)
    c: Vertical(g38)
    c: Coincident(g38,g39)
    c: Horizontal(g39)
    c: Coincident(g39,g40)
    c: PointOnObject(g40,g41)
    c: Vertical(g40)
    c: Vertical(g35)
    c: Distance(g37,g35) = 5
    c: DistanceX(g35,g33) = 2.5
    c: Distance(g38,g40) = 5
    c: DistanceX(g38,g33) = 2.5
    c: Coincident(g41,g37)
    c: Coincident(g34,g35)
    c: Equal(g34,g41)
    c: Coincident(g34,g38)
    c: PointOnObject(g41,g40)
    c: Coincident(g34,g41)
FEATURE [PartDesign::Pad] Pad106
  BaseFeature = -> Pocket127
  Direction = (0,-1,2e-16)
  Length = 7
  Length2 = 10
  Placement = pos=(0,0,0) rot=(1,0,0;1.5708rad)
  Profile = -> Sketch234
  ReferenceAxis = -> Sketch234 [N_Axis]
  Refine = true
  Reversed = true
  Suppressed = false
  Type = 0
FEATURE [Sketcher::SketchObject] Sketch236
  ArcFitTolerance = 1e-06
  AttachmentSupport = -> [Pad106]
  FullyConstrained = false
  MakeInternals = false
  MapMode = 5
  Placement = pos=(35,0,0) rot=(0.707107,0,-0.707107;3.14159rad)
  sketch-geometry (25):
    g0: LineSegment [constr] StartX=-33.5639 StartY=50 StartZ=0 EndX=22.3562 EndY=50 EndZ=0
    g1: LineSegment StartX=-17.0984 StartY=50 StartZ=0 EndX=-16.0002 EndY=50 EndZ=0
    g2: LineSegment StartX=-16.0002 StartY=50 StartZ=0 EndX=5.93914 EndY=8.47552 EndZ=0
    g3: LineSegment StartX=5.93914 StartY=8.47552 StartZ=0 EndX=5.96134 EndY=7.0893 EndZ=0
    g4: LineSegment StartX=5.96134 StartY=7.0893 StartZ=0 EndX=4.40956 EndY=7.0893 EndZ=0
    g5: LineSegment StartX=4.40956 StartY=7.0893 StartZ=0 EndX=-17.1228 EndY=47.8435 EndZ=0
    g6: LineSegment StartX=-17.1228 StartY=47.8435 StartZ=0 EndX=-17.0984 EndY=50 EndZ=0
    g7: LineSegment StartX=-17.1293 StartY=7.10705 StartZ=0 EndX=-17.1293 EndY=9.14543 EndZ=0
    g8: LineSegment StartX=-17.1293 StartY=9.14543 StartZ=0 EndX=4.55828 EndY=50 EndZ=0
    g9: LineSegment StartX=4.55828 StartY=50 StartZ=0 EndX=5.87403 EndY=50.0018 EndZ=0
    g10: LineSegment StartX=5.87403 StartY=50.0018 StartZ=0 EndX=5.93974 EndY=48.3369 EndZ=0
    g11: LineSegment StartX=5.93974 StartY=48.3369 StartZ=0 EndX=-15.9471 EndY=7.10705 EndZ=0
    g12: LineSegment StartX=-15.9471 StartY=7.10705 StartZ=0 EndX=-17.1293 EndY=7.10705 EndZ=0
    g13: LineSegment StartX=-17.1358 StartY=50 StartZ=0 EndX=-15.9776 EndY=50.0877 EndZ=0
    g14: LineSegment StartX=-15.9776 StartY=50.0877 StartZ=0 EndX=5.97119 EndY=97.9201 EndZ=0
    g15: LineSegment StartX=5.97119 StartY=97.9201 StartZ=0 EndX=5.97119 EndY=99.8598 EndZ=0
    g16: LineSegment StartX=5.97119 StartY=99.8598 StartZ=0 EndX=4.66077 EndY=99.8598 EndZ=0
    g17: LineSegment StartX=4.66077 StartY=99.8598 StartZ=0 EndX=-17.1358 EndY=52.3592 EndZ=0
    g18: LineSegment StartX=-17.1358 StartY=52.3592 StartZ=0 EndX=-17.1358 EndY=50 EndZ=0
    g19: LineSegment StartX=-15.9576 StartY=99.8854 StartZ=0 EndX=-17.034 EndY=99.8854 EndZ=0
    g20: LineSegment StartX=-17.034 StartY=99.8854 StartZ=0 EndX=-17.0782 EndY=97.5311 EndZ=0
    g21: LineSegment StartX=-17.0782 StartY=97.5311 StartZ=0 EndX=4.71765 EndY=50 EndZ=0
    g22: LineSegment StartX=4.71765 StartY=50 StartZ=0 EndX=5.8275 EndY=50.1579 EndZ=0
    g23: LineSegment StartX=5.8275 StartY=50.1579 StartZ=0 EndX=5.8275 EndY=52.3779 EndZ=0
    g24: LineSegment StartX=5.8275 StartY=52.3779 StartZ=0 EndX=-15.9576 EndY=99.8854 EndZ=0
  constraints (47):
    c: Horizontal(g0)
    c: DistanceY(g-1,g0) = 50
    c: PointOnObject(g1,g0)
    c: Horizontal(g1)
    c: Coincident(g1,g2)
    c: Coincident(g2,g3)
    c: Coincident(g3,g4)
    c: Horizontal(g4)
    c: Coincident(g4,g5)
    c: Coincident(g5,g6)
    c: Vertical(g7)
    c: Coincident(g7,g8)
    c: PointOnObject(g8,g0)
    c: Coincident(g8,g9)
    c: Coincident(g9,g10)
    c: Coincident(g10,g11)
    c: Coincident(g11,g12)
    c: Coincident(g12,g7)
    c: Horizontal(g12)
    c: Parallel(g5,g2)
    c: Parallel(g8,g11)
    c: Distance(g2,g5) = 2
    c: Distance(g8,g11) = 2
    c: Coincident(g6,g1)
    c: PointOnObject(g13,g0)
    c: Coincident(g13,g14)
    c: Coincident(g14,g15)
    c: Vertical(g15)
    c: Coincident(g15,g16)
    c: Horizontal(g16)
    c: Coincident(g16,g17)
    c: Coincident(g17,g18)
    c: Coincident(g18,g13)
    c: Parallel(g17,g14)
    c: Vertical(g18)
    c: Distance(g14,g17) = 2
    c: Horizontal(g19)
    c: Coincident(g19,g20)
    c: Coincident(g20,g21)
    c: PointOnObject(g21,g0)
    c: Coincident(g21,g22)
    c: Coincident(g22,g23)
    c: Vertical(g23)
    c: Coincident(g23,g24)
    c: Coincident(g24,g19)
    c: Parallel(g24,g21)
    c: Distance(g21,g24) = 2
FEATURE [PartDesign::Pad] Pad107
  BaseFeature = -> Pad106
  Direction = (-1,0,-2e-16)
  Length = 5
  Length2 = 10
  Placement = pos=(0,0,0) rot=(1,0,0;1.5708rad)
  Profile = -> Sketch236
  ReferenceAxis = -> Sketch236 [N_Axis]
  Refine = true
  Reversed = true
  Suppressed = false
  Type = 0
FEATURE [Sketcher::SketchObject] Sketch237
  ArcFitTolerance = 1e-06
  AttachmentSupport = -> [Pad107]
  FullyConstrained = false
  MakeInternals = false
  MapMode = 5
  Placement = pos=(170,0,0) rot=(0.707107,0,0.707107;3.14159rad)
  sketch-geometry (25):
    g0: LineSegment [constr] StartX=-9.20711 StartY=50 StartZ=0 EndX=31.5955 EndY=50 EndZ=0
    g1: LineSegment StartX=-3.23071 StartY=7.09197 StartZ=0 EndX=-2.05702 EndY=7.09197 EndZ=0
    g2: LineSegment StartX=-2.05702 StartY=7.09197 StartZ=0 EndX=18.4375 EndY=47.7755 EndZ=0
    g3: LineSegment StartX=18.4375 StartY=47.7755 StartZ=0 EndX=18.4375 EndY=50 EndZ=0
    g4: LineSegment StartX=18.4375 StartY=50 StartZ=0 EndX=17.3084 EndY=49.9795 EndZ=0
    g5: LineSegment StartX=17.3084 StartY=49.9795 StartZ=0 EndX=-3.23071 EndY=9.20758 EndZ=0
    g6: LineSegment StartX=-3.23071 StartY=9.20758 StartZ=0 EndX=-3.23071 EndY=7.09197 EndZ=0
    g7: LineSegment StartX=17.1226 StartY=7.07983 StartZ=0 EndX=18.4953 EndY=7.07983 EndZ=0
    g8: LineSegment StartX=18.4953 StartY=7.07983 StartZ=0 EndX=18.4953 EndY=8.80663 EndZ=0
    g9: LineSegment StartX=18.4953 StartY=8.80663 StartZ=0 EndX=-2.09857 EndY=50 EndZ=0
    g10: LineSegment StartX=-2.09857 StartY=50 StartZ=0 EndX=-3.17562 EndY=49.9159 EndZ=0
    g11: LineSegment StartX=-3.17562 StartY=49.9159 StartZ=0 EndX=-3.17562 EndY=47.6818 EndZ=0
    g12: LineSegment StartX=-3.17562 StartY=47.6818 StartZ=0 EndX=17.1226 EndY=7.07983 EndZ=0
    g13: LineSegment StartX=-3.19345 StartY=99.8693 StartZ=0 EndX=-2.03057 EndY=99.8693 EndZ=0
    g14: LineSegment StartX=-2.03057 StartY=99.8693 StartZ=0 EndX=18.4277 EndY=53.15 EndZ=0
    g15: LineSegment StartX=18.4277 StartY=53.15 StartZ=0 EndX=18.5025 EndY=50 EndZ=0
    g16: LineSegment StartX=18.5025 StartY=50 StartZ=0 EndX=17.5757 EndY=50.1098 EndZ=0
    g17: LineSegment StartX=17.5757 StartY=50.1098 StartZ=0 EndX=-3.19345 EndY=97.5389 EndZ=0
    g18: LineSegment StartX=-3.19345 StartY=97.5389 StartZ=0 EndX=-3.19345 EndY=99.8693 EndZ=0
    g19: LineSegment StartX=-3.22366 StartY=50 StartZ=0 EndX=-3.22366 EndY=52.3177 EndZ=0
    g20: LineSegment StartX=-3.22366 StartY=52.3177 StartZ=0 EndX=17.471 EndY=99.8606 EndZ=0
    g21: LineSegment StartX=17.471 StartY=99.8606 StartZ=0 EndX=18.4521 EndY=99.8606 EndZ=0
    g22: LineSegment StartX=18.4521 StartY=99.8606 StartZ=0 EndX=18.4521 EndY=97.1035 EndZ=0
    g23: LineSegment StartX=18.4521 StartY=97.1035 StartZ=0 EndX=-2.05909 EndY=49.982 EndZ=0
    g24: LineSegment StartX=-2.05909 StartY=49.982 StartZ=0 EndX=-3.22366 EndY=50 EndZ=0
  constraints (49):
    c: Horizontal(g0)
    c: DistanceY(g-1,g0) = 50
    c: Horizontal(g1)
    c: Coincident(g1,g2)
    c: Coincident(g2,g3)
    c: PointOnObject(g3,g0)
    c: Vertical(g3)
    c: Coincident(g3,g4)
    c: Coincident(g4,g5)
    c: Coincident(g5,g6)
    c: Coincident(g6,g1)
    c: Horizontal(g7)
    c: Coincident(g7,g8)
    c: Vertical(g8)
    c: Coincident(g8,g9)
    c: PointOnObject(g9,g0)
    c: Coincident(g9,g10)
    c: Coincident(g10,g11)
    c: Vertical(g11)
    c: Coincident(g11,g12)
    c: Coincident(g12,g7)
    c: Parallel(g9,g12)
    c: Parallel(g5,g2)
    c: Distance(g2,g5) = 2
    c: Distance(g12,g9) = 2
    c: Vertical(g6)
    c: Horizontal(g13)
    c: Coincident(g13,g14)
    c: Coincident(g14,g15)
    c: PointOnObject(g15,g0)
    c: Coincident(g15,g16)
    c: Coincident(g16,g17)
    c: Coincident(g17,g18)
    c: Coincident(g18,g13)
    c: Vertical(g18)
    c: PointOnObject(g19,g0)
    c: Vertical(g19)
    c: Coincident(g19,g20)
    c: Coincident(g20,g21)
    c: Horizontal(g21)
    c: Coincident(g21,g22)
    c: Vertical(g22)
    c: Coincident(g22,g23)
    c: Coincident(g23,g24)
    c: Coincident(g24,g19)
    c: Parallel(g17,g14)
    c: Parallel(g23,g20)
    c: Distance(g23,g20) = 2
    c: Distance(g14,g17) = 2
FEATURE [PartDesign::Pad] Pad108
  BaseFeature = -> Pad107
  Direction = (1,0,-2e-16)
  Length = 5
  Length2 = 10
  Placement = pos=(0,0,0) rot=(1,0,0;1.5708rad)
  Profile = -> Sketch237
  ReferenceAxis = -> Sketch237 [N_Axis]
  Refine = true
  Reversed = true
  Suppressed = false
  Type = 0
FEATURE [Sketcher::SketchObject] Sketch
  ArcFitTolerance = 1e-06
  AttachmentSupport = -> [Pad108]
  FullyConstrained = true
  MakeInternals = false
  MapMode = 5
  Placement = pos=(0,-7,-2.5e-15) rot=(1,0,0;1.5708rad)
  sketch-geometry (1):
    g0: Circle CenterX=202 CenterY=6 CenterZ=0 NormalX=0 NormalY=0 NormalZ=1 AngleXU=0 Radius=6.5
  constraints (3):
    c: DistanceX(g-1,g0) = 202
    c: DistanceY(g-1,g0) = 6
    c: Diameter(g0) = 13
FEATURE [PartDesign::Pad] Pad109
  BaseFeature = -> Pad108
  Direction = (0,-1,2e-16)
  Length = 7
  Length2 = 10
  Placement = pos=(0,0,0) rot=(1,0,0;1.5708rad)
  Profile = -> Sketch
  ReferenceAxis = -> Sketch [N_Axis]
  Refine = true
  Reversed = true
  Suppressed = false
  Type = 0
FEATURE [Sketcher::SketchObject] Sketch238
  ArcFitTolerance = 1e-06
  AttachmentSupport = -> [Pad109]
  FullyConstrained = true
  MakeInternals = false
  MapMode = 5
  Placement = pos=(0,-7,-4.1e-15) rot=(1,0,0;1.5708rad)
  sketch-geometry (1):
    g0: Circle CenterX=202 CenterY=6 CenterZ=0 NormalX=0 NormalY=0 NormalZ=1 AngleXU=0 Radius=3
  constraints (3):
    c: DistanceY(g-1,g0) = 6
    c: DistanceX(g-1,g0) = 202
    c: Diameter(g0) = 6
FEATURE [PartDesign::Pad] Pad110
  BaseFeature = -> Pad109
  Direction = (0,-1,2e-16)
  Length = 5.5
  Length2 = 10
  Placement = pos=(0,0,0) rot=(1,0,0;1.5708rad)
  Profile = -> Sketch238
  ReferenceAxis = -> Sketch238 [N_Axis]
  Refine = true
  Suppressed = false
  Type = 0
FEATURE [Sketcher::SketchObject] Sketch239
  ArcFitTolerance = 1e-06
  AttachmentSupport = -> [Pad110]
  FullyConstrained = true
  MakeInternals = false
  MapMode = 5
  Placement = pos=(0,-12.5,0) rot=(1,0,0;1.5708rad)
  sketch-geometry (3):
    g0: Circle CenterX=202 CenterY=6 CenterZ=0 NormalX=0 NormalY=0 NormalZ=1 AngleXU=0 Radius=2.45
    g1: Circle CenterX=202 CenterY=6 CenterZ=0 NormalX=0 NormalY=0 NormalZ=1 AngleXU=0 Radius=3.5
    g2: Circle CenterX=202 CenterY=6 CenterZ=0 NormalX=0 NormalY=0 NormalZ=1 AngleXU=0 Radius=1.5
  constraints (7):
    c: DistanceX(g-1,g0) = 202
    c: DistanceY(g-1,g0) = 6
    c: Diameter(g0) = 4.9
    c: Coincident(g1,g0)
    c: Diameter(g1) = 7
    c: Coincident(g2,g0)
    c: Diameter(g2) = 3
FEATURE [PartDesign::Pocket] Pocket128
  BaseFeature = -> Pad110
  Direction = (0,1,-2e-16)
  Length = 3.5
  Length2 = 5
  Placement = pos=(0,0,0) rot=(1,0,0;1.5708rad)
  Profile = -> Sketch239
  ReferenceAxis = -> Sketch239 [N_Axis]
  Refine = true
  Suppressed = false
  Type = 0
FEATURE [PartDesign::Body] Body044  label="wingspar 008"
  AllowCompound = false
  Group = -> [Sketch231,Pad105,Sketch232,Pocket125,Sketch233,Pocket126,Pocket127,Sketch234,Pad106,Sketch235,Sketch236,Pad107,Sketch237,Pad108,Sketch,Pad109,Sketch238,Pad110,Sketch239,Pocket128]
  Origin = -> Origin044
  Placement = pos=(0,-600,0) rot=(0,0,1;0rad)
  Tip = -> Pocket128
FEATURE [Sketcher::SketchObject] Sketch240
  ArcFitTolerance = 1e-06
  AttachmentSupport = -> [XZ_Plane045]
  FullyConstrained = true
  MakeInternals = false
  MapMode = 5
  Placement = pos=(0,0,0) rot=(1,0,0;1.5708rad)
  sketch-geometry (1):
    g0: Circle CenterX=202 CenterY=6 CenterZ=0 NormalX=0 NormalY=0 NormalZ=1 AngleXU=0 Radius=1.45
  constraints (3):
    c: DistanceX(g-1,g0) = 202
    c: DistanceY(g-1,g0) = 6
    c: Diameter(g0) = 2.9
FEATURE [PartDesign::Pad] Pad111
  Direction = (0,-1,2e-16)
  Length = 3.5
  Length2 = 10
  Placement = pos=(0,0,0) rot=(1,0,0;1.5708rad)
  Profile = -> Sketch240
  ReferenceAxis = -> Sketch240 [N_Axis]
  Refine = true
  Suppressed = false
  Type = 0
FEATURE [Sketcher::SketchObject] Sketch241
  ArcFitTolerance = 1e-06
  AttachmentSupport = -> [Pad111]
  FullyConstrained = true
  MakeInternals = false
  MapMode = 5
  Placement = pos=(0,-3.5,0) rot=(1,0,0;1.5708rad)
  sketch-geometry (1):
    g0: Circle CenterX=202 CenterY=6 CenterZ=0 NormalX=0 NormalY=0 NormalZ=1 AngleXU=0 Radius=2.9
  constraints (3):
    c: DistanceX(g-1,g0) = 202
    c: DistanceY(g-1,g0) = 6
    c: Diameter(g0) = 5.8
FEATURE [PartDesign::Pad] Pad112
  BaseFeature = -> Pad111
  Direction = (0,-1,2e-16)
  Length = 1
  Length2 = 10
  Placement = pos=(0,0,0) rot=(1,0,0;1.5708rad)
  Profile = -> Sketch241
  ReferenceAxis = -> Sketch241 [N_Axis]
  Refine = true
  Suppressed = false
  Type = 0
FEATURE [PartDesign::Body] Body045  label="Bearing stopper"
  AllowCompound = false
  Group = -> [Sketch240,Pad111,Sketch241,Pad112]
  Origin = -> Origin045
  Placement = pos=(0,-609,0) rot=(0,0,1;0rad)
  Tip = -> Pad112
FEATURE [Sketcher::SketchObject] Sketch242
  ArcFitTolerance = 1e-06
  AttachmentSupport = -> [YZ_Plane046]
  FullyConstrained = true
  MakeInternals = false
  MapMode = 5
  Placement = pos=(0,0,0) rot=(0.57735,0.57735,0.57735;2.0944rad)
  sketch-geometry (12):
    g0: LineSegment StartX=0 StartY=2.5 StartZ=0 EndX=-3.5 EndY=2.5 EndZ=0
    g1: LineSegment StartX=-3.5 StartY=2.5 StartZ=0 EndX=-3.5 EndY=3 EndZ=0
    g2: LineSegment StartX=-3.5 StartY=3 StartZ=0 EndX=-3 EndY=3 EndZ=0
    g3: LineSegment StartX=-3 StartY=3 StartZ=0 EndX=-3 EndY=3.5 EndZ=0
    g4: LineSegment StartX=-3 StartY=3.5 StartZ=0 EndX=-3.5 EndY=3.5 EndZ=0
    g5: LineSegment StartX=-3.5 StartY=3.5 StartZ=0 EndX=-3.5 EndY=4 EndZ=0
    g6: LineSegment StartX=-3.5 StartY=4 StartZ=0 EndX=0 EndY=4 EndZ=0
    g7: LineSegment StartX=0 StartY=4 StartZ=0 EndX=0 EndY=3.5 EndZ=0
    g8: LineSegment StartX=0 StartY=3.5 StartZ=0 EndX=-0.5 EndY=3.5 EndZ=0
    g9: LineSegment StartX=-0.5 StartY=3.5 StartZ=0 EndX=-0.5 EndY=3 EndZ=0
    g10: LineSegment StartX=-0.5 StartY=3 StartZ=0 EndX=0 EndY=3 EndZ=0
    g11: LineSegment StartX=0 StartY=3 StartZ=0 EndX=0 EndY=2.5 EndZ=0
  constraints (36):
    c: PointOnObject(g0,g-2)
    c: Horizontal(g0)
    c: Coincident(g0,g1)
    c: Coincident(g1,g2)
    c: Horizontal(g2)
    c: Coincident(g2,g3)
    c: Coincident(g3,g4)
    c: Horizontal(g4)
    c: Coincident(g4,g5)
    c: Coincident(g5,g6)
    c: PointOnObject(g6,g-2)
    c: Horizontal(g6)
    c: Coincident(g6,g7)
    c: Coincident(g7,g8)
    c: Coincident(g8,g9)
    c: Coincident(g9,g10)
    c: Coincident(g10,g11)
    c: Coincident(g11,g0)
    c: Vertical(g7)
    c: Vertical(g11)
    c: Vertical(g1)
    c: Vertical(g5)
    c: Vertical(g3)
    c: Vertical(g9)
    c: DistanceX(g6,g6) = 3.5
    c: Horizontal(g8)
    c: Horizontal(g10)
    c: Distance(g8,g8) = 0.5
    c: Distance(g4,g4) = 0.5
    c: DistanceX(g0,g0) = 3.5
    c: DistanceY(g-1,g0) = 2.5
    c: DistanceY(g-1,g6) = 4
    c: DistanceY(g11,g11) = 0.5
    c: DistanceY(g7,g7) = 0.5
    c: DistanceY(g5,g5) = 0.5
    c: DistanceY(g1,g1) = 0.5
FEATURE [PartDesign::Revolution] Revolution
  Angle = 360
  Angle2 = 60
  Axis = (1e-16,1,-1e-16)
  Base = (0,0,0)
  Placement = pos=(0,0,0) rot=(1,1,1;2.0944rad)
  Profile = -> Sketch242
  ReferenceAxis = -> Y_Axis046
  Refine = true
  Suppressed = false
  Type = 0
FEATURE [PartDesign::Body] Body046  label="Bearing left"
  AllowCompound = false
  Group = -> [Sketch242,Revolution]
  Origin = -> Origin046
  Placement = pos=(202,-609,6) rot=(0,0,1;0rad)
  Tip = -> Revolution
FEATURE [Sketcher::SketchObject] Sketch243
  ArcFitTolerance = 1e-06
  AttachmentSupport = -> [Pocket096]
  FullyConstrained = true
  MakeInternals = false
  MapMode = 5
  Placement = pos=(0,-3.6,0) rot=(1,0,0;1.5708rad)
  sketch-geometry (2):
    g0: Circle CenterX=202 CenterY=6 CenterZ=0 NormalX=0 NormalY=0 NormalZ=1 AngleXU=0 Radius=4.5
    g1: Circle CenterX=202 CenterY=6 CenterZ=0 NormalX=0 NormalY=0 NormalZ=1 AngleXU=0 Radius=3.75
  constraints (5):
    c: DistanceX(g-1,g0) = 202
    c: DistanceY(g-1,g0) = 6
    c: Diameter(g0) = 9
    c: Diameter(g1) = 7.5
    c: Coincident(g1,g0)
FEATURE [PartDesign::Pad] Pad113
  BaseFeature = -> Pocket096
  Direction = (0,-1,2e-16)
  Length = 0.5
  Length2 = 10
  Placement = pos=(0,0,0) rot=(1,0,0;1.5708rad)
  Profile = -> Sketch243
  ReferenceAxis = -> Sketch243 [N_Axis]
  Refine = true
  Suppressed = false
  Type = 0
FEATURE [PartDesign::Chamfer] Chamfer007
  Angle = 45
  Base = -> Pad113 [Edge123]
  BaseFeature = -> Pad113
  ChamferType = 0
  FlipDirection = false
  Placement = pos=(0,0,0) rot=(1,0,0;1.5708rad)
  Refine = true
  Size = 0.45
  Size2 = 1
  SupportTransform = false
  Suppressed = false
  UseAllEdges = false
FEATURE [Sketcher::SketchObject] Sketch244
  ArcFitTolerance = 1e-06
  FullyConstrained = false
  MakeInternals = false
  Placement = pos=(0,0,0) rot=(1,0,0;1.5708rad)
  sketch-geometry (125):
    g0: BSplineCurve PolesCount=62 KnotsCount=62 Degree=3 IsPeriodic=1
    g1-g62: Circle [constr] x62 (B-spline internal-alignment scaffolding for g0; pole/knot coordinates omitted)
    g63-g124: GeomPoint [constr] x62 (B-spline internal-alignment scaffolding for g0; pole/knot coordinates omitted)
  constraints (125):
    c: InternalAlignment(g1,g0)
    c: Weight(g1) = 1
    c: InternalAlignment(g2,g0)
    c: Equal(g2,g1)
    c: InternalAlignment(g3,g0)
    c: Equal(g3,g1)
    c: InternalAlignment(g4,g0)
    c: Equal(g4,g1)
    c: InternalAlignment(g5,g0)
    c: Equal(g5,g1)
    c: InternalAlignment(g6,g0)
    c: Equal(g6,g1)
    c: InternalAlignment(g7,g0)
    c: Equal(g7,g1)
    c: InternalAlignment(g8,g0)
    c: Equal(g8,g1)
    c: InternalAlignment(g9,g0)
    c: Equal(g9,g1)
    c: InternalAlignment(g10,g0)
    c: Equal(g10,g1)
    c: InternalAlignment(g11,g0)
    c: Equal(g11,g1)
    c: InternalAlignment(g12,g0)
    c: Equal(g12,g1)
    c: InternalAlignment(g13,g0)
    c: Equal(g13,g1)
    c: InternalAlignment(g14,g0)
    c: Equal(g14,g1)
    c: InternalAlignment(g15,g0)
    c: Equal(g15,g1)
    c: InternalAlignment(g16,g0)
    c: Equal(g16,g1)
    c: InternalAlignment(g17,g0)
    c: Equal(g17,g1)
    c: InternalAlignment(g18,g0)
    c: Equal(g18,g1)
    c: InternalAlignment(g19,g0)
    c: Equal(g19,g1)
    c: InternalAlignment(g20,g0)
    c: Equal(g20,g1)
    c: InternalAlignment(g21,g0)
    c: Equal(g21,g1)
    c: InternalAlignment(g22,g0)
    c: Equal(g22,g1)
    c: InternalAlignment(g23,g0)
    c: Equal(g23,g1)
    c: InternalAlignment(g24,g0)
    c: Equal(g24,g1)
    c: InternalAlignment(g25,g0)
    c: Equal(g25,g1)
    c: InternalAlignment(g26,g0)
    c: Equal(g26,g1)
    c: InternalAlignment(g27,g0)
    c: Equal(g27,g1)
    c: InternalAlignment(g28,g0)
    c: Equal(g28,g1)
    c: InternalAlignment(g29,g0)
    c: Equal(g29,g1)
    c: InternalAlignment(g30,g0)
    c: Equal(g30,g1)
    c: InternalAlignment(g31,g0)
    c: Equal(g31,g1)
    c: InternalAlignment(g32,g0)
    c: Equal(g32,g1)
    c: InternalAlignment(g33,g0)
    c: Equal(g33,g1)
    c: InternalAlignment(g34,g0)
    c: Equal(g34,g1)
    c: InternalAlignment(g35,g0)
    c: Equal(g35,g1)
    c: InternalAlignment(g36,g0)
    c: Equal(g36,g1)
    c: InternalAlignment(g37,g0)
    c: Equal(g37,g1)
    c: InternalAlignment(g38,g0)
    c: Equal(g38,g1)
    c: InternalAlignment(g39,g0)
    c: Equal(g39,g1)
    c: InternalAlignment(g40,g0)
    c: Equal(g40,g1)
    c: InternalAlignment(g41,g0)
    c: Equal(g41,g1)
    c: InternalAlignment(g42,g0)
    c: Equal(g42,g1)
    c: InternalAlignment(g43,g0)
    c: Equal(g43,g1)
    c: InternalAlignment(g44,g0)
    c: Equal(g44,g1)
    c: InternalAlignment(g45,g0)
    c: Equal(g45,g1)
    c: InternalAlignment(g46,g0)
    c: Equal(g46,g1)
    c: InternalAlignment(g47,g0)
    c: Equal(g47,g1)
    c: InternalAlignment(g48,g0)
    c: Equal(g48,g1)
    c: InternalAlignment(g49,g0)
    c: Equal(g49,g1)
    c: InternalAlignment(g50,g0)
    c: Equal(g50,g1)
    c: InternalAlignment(g51,g0)
    c: Equal(g51,g1)
    c: InternalAlignment(g52,g0)
    c: Equal(g52,g1)
    c: InternalAlignment(g53,g0)
    c: Equal(g53,g1)
    c: InternalAlignment(g54,g0)
    c: Equal(g54,g1)
    c: InternalAlignment(g55,g0)
    c: Equal(g55,g1)
    c: InternalAlignment(g56,g0)
    c: Equal(g56,g1)
    c: InternalAlignment(g57,g0)
    c: Equal(g57,g1)
    c: InternalAlignment(g58,g0)
    c: Equal(g58,g1)
    c: InternalAlignment(g59,g0)
    c: Equal(g59,g1)
    c: InternalAlignment(g60,g0)
    c: Equal(g60,g1)
    c: InternalAlignment(g61,g0)
    c: Equal(g61,g1)
    c: InternalAlignment(g62,g0)
    c: Equal(g62,g1)
    c: InternalAlignment(g63-g124 -> g0) x62
FEATURE [PartDesign::Pad] Pad114
  Direction = (0,-1,2e-16)
  Length = 3.6
  Length2 = 10
  Placement = pos=(0,0,0) rot=(1,0,0;1.5708rad)
  Profile = -> Sketch244
  ReferenceAxis = -> Sketch244 [N_Axis]
  Refine = true
  Suppressed = false
  Type = 0
FEATURE [Sketcher::SketchObject] Sketch245
  ArcFitTolerance = 1e-06
  AttachmentSupport = -> [XY_Plane047]
  FullyConstrained = false
  MakeInternals = false
  MapMode = 5
  sketch-geometry (4):
    g0: LineSegment StartX=201.5 StartY=17.3691 StartZ=0 EndX=201.5 EndY=-319.321 EndZ=0
    g1: LineSegment StartX=201.5 StartY=-319.321 StartZ=0 EndX=401.455 EndY=-319.321 EndZ=0
    g2: LineSegment StartX=401.455 StartY=-319.321 StartZ=0 EndX=401.455 EndY=17.3691 EndZ=0
    g3: LineSegment StartX=401.455 StartY=17.3691 StartZ=0 EndX=201.5 EndY=17.3691 EndZ=0
  constraints (9):
    c: Coincident(g0,g1)
    c: Coincident(g1,g2)
    c: Coincident(g2,g3)
    c: Coincident(g3,g0)
    c: Vertical(g0)
    c: Vertical(g2)
    c: Horizontal(g1)
    c: Horizontal(g3)
    c: DistanceX(g-1,g0) = 201.5
FEATURE [PartDesign::Pocket] Pocket129
  BaseFeature = -> Pad114
  Direction = (0,0,-1)
  Length = 100
  Length2 = 5
  Midplane = true
  Placement = pos=(0,0,0) rot=(1,0,0;1.5708rad)
  Profile = -> Sketch245
  ReferenceAxis = -> Sketch245 [N_Axis]
  Refine = true
  Suppressed = false
  Type = 0
FEATURE [Sketcher::SketchObject] Sketch246
  ArcFitTolerance = 1e-06
  AttachmentSupport = -> [Pocket129]
  FullyConstrained = false
  MakeInternals = false
  MapMode = 5
  Placement = pos=(0,-3.6,8e-16) rot=(1,0,0;1.5708rad)
  sketch-geometry (7):
    g0: ArcOfCircle CenterX=202 CenterY=6 CenterZ=0 NormalX=0 NormalY=0 NormalZ=1 AngleXU=0 Radius=8.6 StartAngle=1.5708 EndAngle=4.71239
    g1: LineSegment [constr] StartX=202 StartY=-2.6 StartZ=0 EndX=202 EndY=14.6 EndZ=0
    g2: LineSegment StartX=202 StartY=14.6 StartZ=0 EndX=188.969 EndY=46.4532 EndZ=0
    g3: LineSegment StartX=188.969 StartY=46.4532 StartZ=0 EndX=-27.7275 EndY=31.7802 EndZ=0
    g4: LineSegment StartX=-27.7275 StartY=31.7802 StartZ=0 EndX=-22.8987 EndY=-30.946 EndZ=0
    g5: LineSegment StartX=-22.8987 StartY=-30.946 StartZ=0 EndX=213.748 EndY=-30.946 EndZ=0
    g6: LineSegment StartX=213.748 StartY=-30.946 StartZ=0 EndX=202 EndY=-2.6 EndZ=0
  constraints (14):
    c: DistanceX(g-1,g0) = 202
    c: DistanceY(g-1,g0) = 6
    c: Vertical(g1)
    c: PointOnObject(g0,g1)
    c: Coincident(g0,g1)
    c: Coincident(g1,g0)
    c: Radius(g0) = 8.6
    c: Coincident(g0,g2)
    c: Coincident(g2,g3)
    c: Coincident(g3,g4)
    c: Coincident(g4,g5)
    c: Horizontal(g5)
    c: Coincident(g5,g6)
    c: Coincident(g6,g0)
FEATURE [PartDesign::Pocket] Pocket130
  BaseFeature = -> Pocket129
  Direction = (0,1,-2e-16)
  Length = 300
  Length2 = 5
  Placement = pos=(0,0,0) rot=(1,0,0;1.5708rad)
  Profile = -> Sketch246
  ReferenceAxis = -> Sketch246 [N_Axis]
  Refine = true
  Suppressed = false
  Type = 0
FEATURE [Sketcher::SketchObject] Sketch247
  ArcFitTolerance = 1e-06
  AttachmentSupport = -> [Pocket130]
  FullyConstrained = true
  MakeInternals = false
  MapMode = 5
  Placement = pos=(0,-3.6,8e-16) rot=(1,0,0;1.5708rad)
  sketch-geometry (1):
    g0: Circle CenterX=202 CenterY=6 CenterZ=0 NormalX=0 NormalY=0 NormalZ=1 AngleXU=0 Radius=4.05
  constraints (3):
    c: DistanceX(g-1,g0) = 202
    c: DistanceY(g-1,g0) = 6
    c: Diameter(g0) = 8.1
FEATURE [PartDesign::Pocket] Pocket131
  BaseFeature = -> Pocket130
  Direction = (0,1,-2e-16)
  Length = 5
  Length2 = 5
  Placement = pos=(0,0,0) rot=(1,0,0;1.5708rad)
  Profile = -> Sketch247
  ReferenceAxis = -> Sketch247 [N_Axis]
  Refine = true
  Suppressed = false
  Type = 0
FEATURE [Sketcher::SketchObject] Sketch248
  ArcFitTolerance = 1e-06
  AttachmentSupport = -> [Pocket131]
  FullyConstrained = true
  MakeInternals = false
  MapMode = 5
  Placement = pos=(201.5,0,0) rot=(0.707107,0,0.707107;3.14159rad)
  sketch-geometry (2):
    g0: Circle CenterX=12.3 CenterY=1.8 CenterZ=0 NormalX=0 NormalY=0 NormalZ=1 AngleXU=0 Radius=0.8
    g1: Circle CenterX=-0.3 CenterY=1.8 CenterZ=0 NormalX=0 NormalY=0 NormalZ=1 AngleXU=0 Radius=0.8
  constraints (6):
    c: Diameter(g1) = 1.6
    c: Diameter(g0) = 1.6
    c: DistanceY(g-1,g1) = 1.8
    c: DistanceY(g-1,g0) = 1.8
    c: DistanceX(g-1,g0) = 12.3
    c: DistanceX(g1,g-1) = 0.3
FEATURE [PartDesign::Pocket] Pocket132
  BaseFeature = -> Pocket131
  Direction = (-1,0,2e-16)
  Length = 10
  Length2 = 5
  Placement = pos=(0,0,0) rot=(1,0,0;1.5708rad)
  Profile = -> Sketch248
  ReferenceAxis = -> Sketch248 [N_Axis]
  Refine = true
  Suppressed = false
  Type = 0
FEATURE [PartDesign::Plane] DatumPlane001
  AttachmentOffset = pos=(0,0,-8) rot=(0,0,1;0rad)
  AttachmentSupport = -> [Pocket132]
  Length = 60
  MapMode = 5
  Placement = pos=(193.5,0,1.8e-15) rot=(0.707107,0,0.707107;3.14159rad)
  ResizeMode = 0
  Width = 60
FEATURE [Sketcher::SketchObject] Sketch249
  ArcFitTolerance = 1e-06
  AttachmentSupport = -> [DatumPlane001]
  FullyConstrained = true
  MakeInternals = false
  MapMode = 5
  Placement = pos=(193.5,0,1.8e-15) rot=(0.707107,0,0.707107;3.14159rad)
  sketch-geometry (2):
    g0: Circle CenterX=12.3 CenterY=1.8 CenterZ=0 NormalX=0 NormalY=0 NormalZ=1 AngleXU=0 Radius=1.75
    g1: Circle CenterX=-0.3 CenterY=1.8 CenterZ=0 NormalX=0 NormalY=0 NormalZ=1 AngleXU=0 Radius=1.75
  constraints (6):
    c: Diameter(g0) = 3.5
    c: DistanceY(g-1,g0) = 1.8
    c: DistanceX(g-1,g0) = 12.3
    c: Diameter(g1) = 3.5
    c: DistanceY(g-1,g1) = 1.8
    c: DistanceX(g1,g-1) = 0.3
FEATURE [PartDesign::Pocket] Pocket133
  BaseFeature = -> Pocket132
  Direction = (-1,0,2e-16)
  Length = 4.5
  Length2 = 5
  Placement = pos=(0,0,0) rot=(1,0,0;1.5708rad)
  Profile = -> Sketch249
  ReferenceAxis = -> Sketch249 [N_Axis]
  Refine = true
  Reversed = true
  Suppressed = false
  Type = 0
FEATURE [PartDesign::Body] Body047  label="rudder 001 clamp"
  AllowCompound = false
  Group = -> [Sketch244,Pad114,Sketch245,Pocket129,Sketch246,Pocket130,Sketch247,Pocket131,Sketch248,Pocket132,DatumPlane001,Sketch249,Pocket133]
  Origin = -> Origin047
  Placement = pos=(0,-609,0) rot=(0,0,1;0rad)
  Tip = -> Pocket133
FEATURE [Sketcher::SketchObject] Sketch250
  ArcFitTolerance = 1e-06
  AttachmentSupport = -> [XY_Plane035]
  FullyConstrained = false
  MakeInternals = false
  MapMode = 5
  sketch-geometry (4):
    g0: LineSegment StartX=191.652 StartY=1e-16 StartZ=0 EndX=191.652 EndY=-3.7 EndZ=0
    g1: LineSegment StartX=191.652 StartY=-3.7 StartZ=0 EndX=202.5 EndY=-3.7 EndZ=0
    g2: LineSegment StartX=202.5 StartY=-3.7 StartZ=0 EndX=202.5 EndY=0 EndZ=0
    g3: LineSegment StartX=202.5 StartY=1e-16 StartZ=0 EndX=191.652 EndY=1e-16 EndZ=0
  constraints (11):
    c: Coincident(g0,g1)
    c: Coincident(g1,g2)
    c: Coincident(g2,g3)
    c: Coincident(g3,g0)
    c: Vertical(g0)
    c: Vertical(g2)
    c: Horizontal(g1)
    c: Horizontal(g3)
    c: PointOnObject(g0,g-1)
    c: DistanceX(g-1,g1) = 202.5
    c: DistanceY(g0,g0) = 3.7
FEATURE [PartDesign::Pocket] Pocket134
  BaseFeature = -> Chamfer007
  Direction = (0,0,-1)
  Length = 100
  Length2 = 5
  Midplane = true
  Placement = pos=(0,0,0) rot=(1,0,0;1.5708rad)
  Profile = -> Sketch250
  ReferenceAxis = -> Sketch250 [N_Axis]
  Refine = true
  Suppressed = false
  Type = 0
FEATURE [PartDesign::Pocket] Pocket135
  BaseFeature = -> Pocket134
  Direction = (0,-1,-1e-16)
  Length = 5
  Length2 = 5
  Placement = pos=(0,0,0) rot=(1,0,0;1.5708rad)
  Profile = -> Pocket134 [Face4]
  Refine = true
  Suppressed = false
  Type = 0
FEATURE [Sketcher::SketchObject] Sketch251
  ArcFitTolerance = 1e-06
  AttachmentSupport = -> [Pocket135]
  FullyConstrained = true
  MakeInternals = false
  MapMode = 5
  Placement = pos=(202.5,0,0) rot=(0.707107,0,-0.707107;3.14159rad)
  sketch-geometry (2):
    g0: Circle CenterX=-12.3 CenterY=1.8 CenterZ=0 NormalX=0 NormalY=0 NormalZ=1 AngleXU=0 Radius=0.8
    g1: Circle CenterX=0.3 CenterY=1.8 CenterZ=0 NormalX=0 NormalY=0 NormalZ=1 AngleXU=0 Radius=0.8
  constraints (6):
    c: Diameter(g0) = 1.6
    c: Diameter(g1) = 1.6
    c: DistanceY(g-1,g1) = 1.8
    c: DistanceX(g-1,g1) = 0.3
    c: DistanceY(g-1,g0) = 1.8
    c: DistanceX(g0,g-1) = 12.3
FEATURE [PartDesign::Pocket] Pocket136
  BaseFeature = -> Pocket135
  Direction = (1,0,2e-16)
  Length = 10
  Length2 = 5
  Placement = pos=(0,0,0) rot=(1,0,0;1.5708rad)
  Profile = -> Sketch251
  ReferenceAxis = -> Sketch251 [N_Axis]
  Refine = true
  Suppressed = false
  Type = 0
FEATURE [PartDesign::Body] Body035  label="rudder 001"
  AllowCompound = false
  Group = -> [Sketch152,Pad064,Sketch154,Pocket088,Sketch155,Pocket089,DatumPlane,Sketch156,Pocket090,Sketch157,Pocket091,Sketch158,Pocket092,Sketch159,Pocket093,Sketch160,Sketch161,Pocket094,Pocket095,Sketch162,Pocket096,Sketch243,Pad113,Chamfer007,Sketch250,Pocket134,Pocket135,Sketch251,Pocket136]
  Origin = -> Origin035
  Placement = pos=(0,-609,0) rot=(0,0,1;0rad)
  Tip = -> Pocket136
